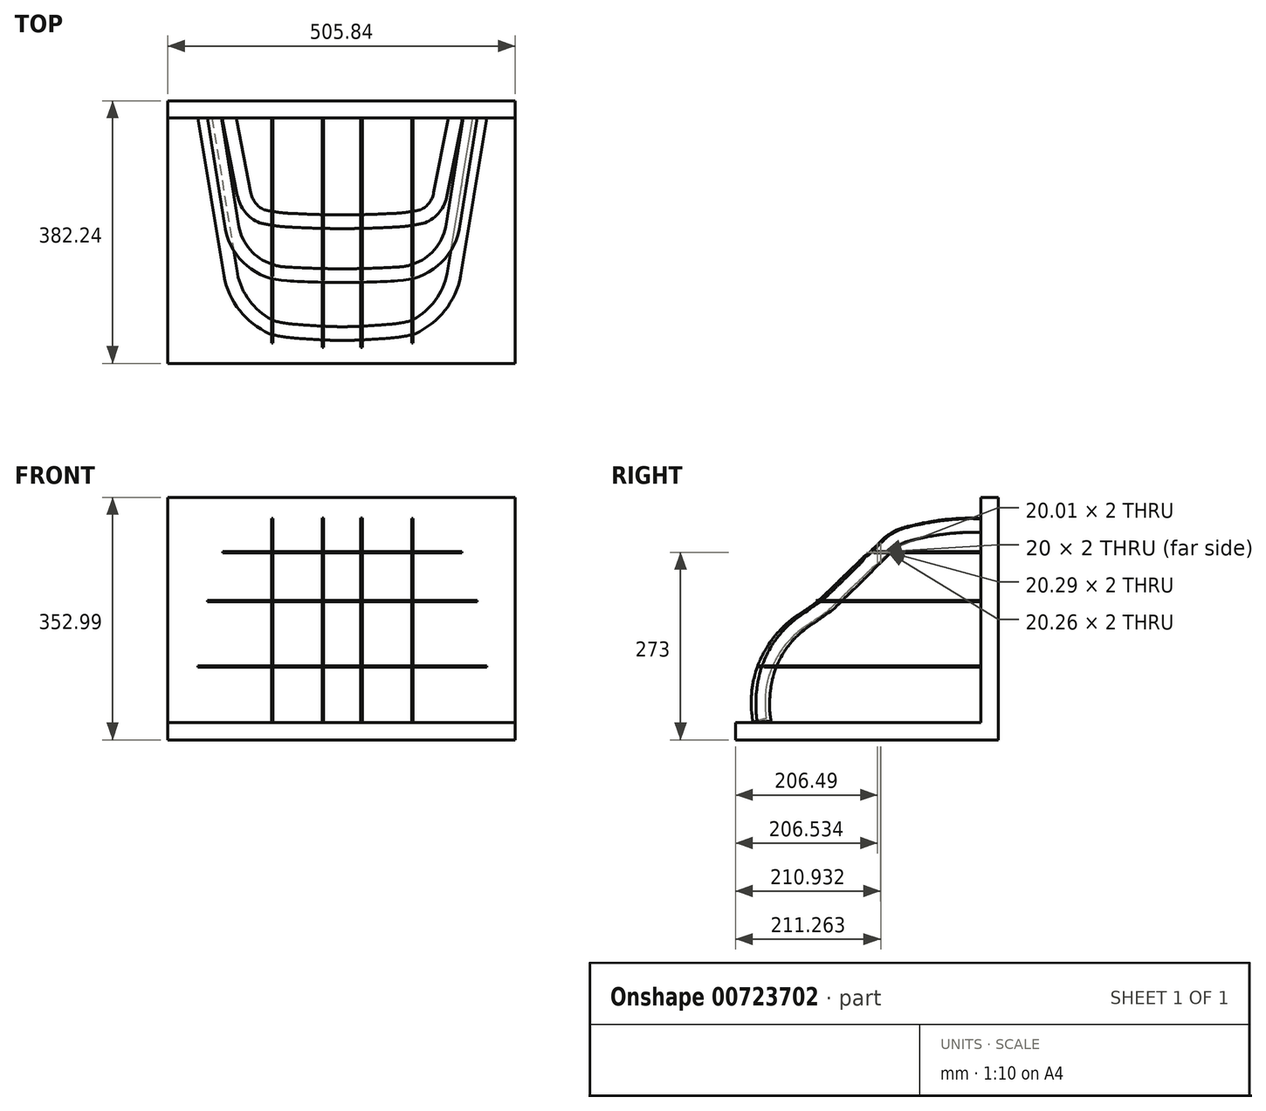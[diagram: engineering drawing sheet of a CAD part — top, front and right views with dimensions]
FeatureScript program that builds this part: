
annotation { "Feature Type Name" : "Feature", "Feature Type Description" : "" }
export const myFeature = defineFeature(function(context is Context, id is Id, definition is map)
    precondition{}
    {
        {
            var Q0;
            Q0=qCreatedBy(makeId("Right.planeOp"),FACE);
            cPlane(context, id + "F0", {"entities" : qUnion([Q0]), "cplaneType" : CPlaneType.OFFSET, "offset" : 28 * mm, "width" : 150 * mm, "height" : 150 * mm});
        }
        {
            var Q0;
            Q0=qCreatedBy(id+"F0.planeOp",FACE);
            var sketch = newSketch(context, id + "F1", { "sketchPlane" : qUnion([Q0])});
            skPoint(sketch, "E0", {"position": v(0, 0) * mm});
            skLineSegment(sketch, "E1", {"start": v(0, 0) * mm, "end": v(-336.64, 0) * mm});
            skLineSegment(sketch, "E2", {"start": v(0, 302.93) * mm, "end": v(-1.33, 302.66) * mm});
            skLineSegment(sketch, "E3", {"start": v(-1.33, 302.66) * mm, "end": v(-1.75, 302.63) * mm});
            skLineSegment(sketch, "E4", {"start": v(-1.75, 302.63) * mm, "end": v(-3.18, 302.69) * mm});
            skLineSegment(sketch, "E5", {"start": v(-3.18, 302.69) * mm, "end": v(-4.19, 302.72) * mm});
            skLineSegment(sketch, "E6", {"start": v(-4.19, 302.72) * mm, "end": v(-4.73, 302.74) * mm});
            skLineSegment(sketch, "E7", {"start": v(-4.73, 302.74) * mm, "end": v(-7.22, 302.8) * mm});
            skLineSegment(sketch, "E8", {"start": v(-7.22, 302.8) * mm, "end": v(-9.08, 302.77) * mm});
            skLineSegment(sketch, "E9", {"start": v(-9.08, 302.77) * mm, "end": v(-11.39, 302.77) * mm});
            skLineSegment(sketch, "E10", {"start": v(-11.39, 302.77) * mm, "end": v(-14.62, 302.87) * mm});
            skLineSegment(sketch, "E11", {"start": v(-14.62, 302.87) * mm, "end": v(-15.84, 302.9) * mm});
            skLineSegment(sketch, "E12", {"start": v(-15.84, 302.9) * mm, "end": v(-16.17, 302.91) * mm});
            skLineSegment(sketch, "E13", {"start": v(-16.17, 302.91) * mm, "end": v(-16.53, 302.91) * mm});
            skLineSegment(sketch, "E14", {"start": v(-16.53, 302.91) * mm, "end": v(-19.91, 302.89) * mm});
            skLineSegment(sketch, "E15", {"start": v(-19.91, 302.89) * mm, "end": v(-22.68, 302.78) * mm});
            skLineSegment(sketch, "E16", {"start": v(-22.68, 302.78) * mm, "end": v(-26.11, 302.63) * mm});
            skLineSegment(sketch, "E17", {"start": v(-26.11, 302.63) * mm, "end": v(-31.16, 302.43) * mm});
            skLineSegment(sketch, "E18", {"start": v(-31.16, 302.43) * mm, "end": v(-32.29, 302.39) * mm});
            skLineSegment(sketch, "E19", {"start": v(-32.29, 302.39) * mm, "end": v(-33.37, 302.32) * mm});
            skLineSegment(sketch, "E20", {"start": v(-33.37, 302.32) * mm, "end": v(-36.32, 302.12) * mm});
            skLineSegment(sketch, "E21", {"start": v(-36.32, 302.12) * mm, "end": v(-38.52, 301.96) * mm});
            skLineSegment(sketch, "E22", {"start": v(-38.52, 301.96) * mm, "end": v(-40.75, 301.8) * mm});
            skLineSegment(sketch, "E23", {"start": v(-40.75, 301.8) * mm, "end": v(-42.89, 301.62) * mm});
            skLineSegment(sketch, "E24", {"start": v(-42.89, 301.62) * mm, "end": v(-43.02, 301.61) * mm});
            skLineSegment(sketch, "E25", {"start": v(-43.02, 301.61) * mm, "end": v(-47.21, 301.28) * mm});
            skLineSegment(sketch, "E26", {"start": v(-47.21, 301.28) * mm, "end": v(-48.36, 301.18) * mm});
            skLineSegment(sketch, "E27", {"start": v(-48.36, 301.18) * mm, "end": v(-51.91, 300.85) * mm});
            skLineSegment(sketch, "E28", {"start": v(-51.91, 300.85) * mm, "end": v(-52.52, 300.78) * mm});
            skLineSegment(sketch, "E29", {"start": v(-52.52, 300.78) * mm, "end": v(-54.54, 300.56) * mm});
            skLineSegment(sketch, "E30", {"start": v(-54.54, 300.56) * mm, "end": v(-57.85, 300.12) * mm});
            skLineSegment(sketch, "E31", {"start": v(-57.85, 300.12) * mm, "end": v(-58.76, 300) * mm});
            skLineSegment(sketch, "E32", {"start": v(-58.76, 300) * mm, "end": v(-62.24, 299.52) * mm});
            skLineSegment(sketch, "E33", {"start": v(-62.24, 299.52) * mm, "end": v(-65.37, 299.1) * mm});
            skLineSegment(sketch, "E34", {"start": v(-65.37, 299.1) * mm, "end": v(-69.73, 298.47) * mm});
            skLineSegment(sketch, "E35", {"start": v(-69.73, 298.47) * mm, "end": v(-71.93, 298.15) * mm});
            skLineSegment(sketch, "E36", {"start": v(-71.93, 298.15) * mm, "end": v(-73.76, 297.84) * mm});
            skLineSegment(sketch, "E37", {"start": v(-73.76, 297.84) * mm, "end": v(-76.97, 297.28) * mm});
            skLineSegment(sketch, "E38", {"start": v(-76.97, 297.28) * mm, "end": v(-79.2, 296.9) * mm});
            skLineSegment(sketch, "E39", {"start": v(-79.2, 296.9) * mm, "end": v(-83.2, 296.17) * mm});
            skLineSegment(sketch, "E40", {"start": v(-83.2, 296.17) * mm, "end": v(-85.92, 295.66) * mm});
            skLineSegment(sketch, "E41", {"start": v(-85.92, 295.66) * mm, "end": v(-87.06, 295.42) * mm});
            skLineSegment(sketch, "E42", {"start": v(-87.06, 295.42) * mm, "end": v(-90.16, 294.74) * mm});
            skLineSegment(sketch, "E43", {"start": v(-90.16, 294.74) * mm, "end": v(-92.74, 294.23) * mm});
            skLineSegment(sketch, "E44", {"start": v(-92.74, 294.23) * mm, "end": v(-96.17, 293.46) * mm});
            skLineSegment(sketch, "E45", {"start": v(-96.17, 293.46) * mm, "end": v(-97.36, 293.2) * mm});
            skLineSegment(sketch, "E46", {"start": v(-97.36, 293.2) * mm, "end": v(-98.2, 293) * mm});
            skLineSegment(sketch, "E47", {"start": v(-98.2, 293) * mm, "end": v(-103.97, 291.56) * mm});
            skLineSegment(sketch, "E48", {"start": v(-103.97, 291.56) * mm, "end": v(-104.02, 291.55) * mm});
            skLineSegment(sketch, "E49", {"start": v(-104.02, 291.55) * mm, "end": v(-104.07, 291.54) * mm});
            skLineSegment(sketch, "E50", {"start": v(-104.07, 291.54) * mm, "end": v(-107.9, 290.6) * mm});
            skLineSegment(sketch, "E51", {"start": v(-107.9, 290.6) * mm, "end": v(-109.48, 290.16) * mm});
            skLineSegment(sketch, "E52", {"start": v(-109.48, 290.16) * mm, "end": v(-112.69, 289.3) * mm});
            skLineSegment(sketch, "E53", {"start": v(-112.69, 289.3) * mm, "end": v(-113, 289.22) * mm});
            skLineSegment(sketch, "E54", {"start": v(-113, 289.22) * mm, "end": v(-113.13, 289.18) * mm});
            skLineSegment(sketch, "E55", {"start": v(-113.13, 289.18) * mm, "end": v(-113.84, 288.97) * mm});
            skLineSegment(sketch, "E56", {"start": v(-113.84, 288.97) * mm, "end": v(-116.81, 288.1) * mm});
            skLineSegment(sketch, "E57", {"start": v(-116.81, 288.1) * mm, "end": v(-118.25, 287.64) * mm});
            skLineSegment(sketch, "E58", {"start": v(-118.25, 287.64) * mm, "end": v(-120.24, 286.96) * mm});
            skLineSegment(sketch, "E59", {"start": v(-120.24, 286.96) * mm, "end": v(-122.17, 286.17) * mm});
            skLineSegment(sketch, "E60", {"start": v(-122.17, 286.17) * mm, "end": v(-123.8, 285.5) * mm});
            skLineSegment(sketch, "E61", {"start": v(-123.8, 285.5) * mm, "end": v(-126.08, 284.5) * mm});
            skLineSegment(sketch, "E62", {"start": v(-126.08, 284.5) * mm, "end": v(-127.05, 283.99) * mm});
            skLineSegment(sketch, "E63", {"start": v(-127.05, 283.99) * mm, "end": v(-129.84, 282.57) * mm});
            skLineSegment(sketch, "E64", {"start": v(-129.84, 282.57) * mm, "end": v(-131.55, 281.62) * mm});
            skLineSegment(sketch, "E65", {"start": v(-131.55, 281.62) * mm, "end": v(-132.06, 281.35) * mm});
            skLineSegment(sketch, "E66", {"start": v(-132.06, 281.35) * mm, "end": v(-132.92, 280.81) * mm});
            skLineSegment(sketch, "E67", {"start": v(-132.92, 280.81) * mm, "end": v(-135.31, 279.39) * mm});
            skLineSegment(sketch, "E68", {"start": v(-135.31, 279.39) * mm, "end": v(-137.16, 278.12) * mm});
            skLineSegment(sketch, "E69", {"start": v(-137.16, 278.12) * mm, "end": v(-138.07, 277.49) * mm});
            skLineSegment(sketch, "E70", {"start": v(-138.07, 277.49) * mm, "end": v(-139.84, 276.19) * mm});
            skLineSegment(sketch, "E71", {"start": v(-139.84, 276.19) * mm, "end": v(-140.9, 275.41) * mm});
            skLineSegment(sketch, "E72", {"start": v(-140.9, 275.41) * mm, "end": v(-141.31, 275.08) * mm});
            skLineSegment(sketch, "E73", {"start": v(-141.31, 275.08) * mm, "end": v(-142.88, 273.8) * mm});
            skLineSegment(sketch, "E74", {"start": v(-142.88, 273.8) * mm, "end": v(-144.14, 272.67) * mm});
            skLineSegment(sketch, "E75", {"start": v(-144.14, 272.67) * mm, "end": v(-145.09, 271.82) * mm});
            skLineSegment(sketch, "E76", {"start": v(-145.09, 271.82) * mm, "end": v(-145.86, 271.04) * mm});
            skLineSegment(sketch, "E77", {"start": v(-145.86, 271.04) * mm, "end": v(-148.57, 268.42) * mm});
            skLineSegment(sketch, "E78", {"start": v(-148.57, 268.42) * mm, "end": v(-148.88, 268.1) * mm});
            skLineSegment(sketch, "E79", {"start": v(-148.88, 268.1) * mm, "end": v(-151.46, 265.56) * mm});
            skLineSegment(sketch, "E80", {"start": v(-151.46, 265.56) * mm, "end": v(-152.25, 264.79) * mm});
            skLineSegment(sketch, "E81", {"start": v(-152.25, 264.79) * mm, "end": v(-153.7, 263.33) * mm});
            skLineSegment(sketch, "E82", {"start": v(-153.7, 263.33) * mm, "end": v(-154.53, 262.44) * mm});
            skLineSegment(sketch, "E83", {"start": v(-154.53, 262.44) * mm, "end": v(-155.9, 261.16) * mm});
            skLineSegment(sketch, "E84", {"start": v(-155.9, 261.16) * mm, "end": v(-156.74, 260.4) * mm});
            skLineSegment(sketch, "E85", {"start": v(-156.74, 260.4) * mm, "end": v(-158.23, 258.88) * mm});
            skLineSegment(sketch, "E86", {"start": v(-158.23, 258.88) * mm, "end": v(-158.94, 258.15) * mm});
            skLineSegment(sketch, "E87", {"start": v(-158.94, 258.15) * mm, "end": v(-160, 257.23) * mm});
            skLineSegment(sketch, "E88", {"start": v(-160, 257.23) * mm, "end": v(-160.75, 256.56) * mm});
            skLineSegment(sketch, "E89", {"start": v(-160.75, 256.56) * mm, "end": v(-161.54, 255.85) * mm});
            skLineSegment(sketch, "E90", {"start": v(-161.54, 255.85) * mm, "end": v(-162.05, 255.37) * mm});
            skLineSegment(sketch, "E91", {"start": v(-162.05, 255.37) * mm, "end": v(-162.8, 254.67) * mm});
            skLineSegment(sketch, "E92", {"start": v(-162.8, 254.67) * mm, "end": v(-164, 253.4) * mm});
            skLineSegment(sketch, "E93", {"start": v(-164, 253.4) * mm, "end": v(-165.4, 251.9) * mm});
            skLineSegment(sketch, "E94", {"start": v(-165.4, 251.9) * mm, "end": v(-165.92, 251.36) * mm});
            skLineSegment(sketch, "E95", {"start": v(-165.92, 251.36) * mm, "end": v(-167.8, 249.6) * mm});
            skLineSegment(sketch, "E96", {"start": v(-167.8, 249.6) * mm, "end": v(-167.93, 249.47) * mm});
            skLineSegment(sketch, "E97", {"start": v(-167.93, 249.47) * mm, "end": v(-167.99, 249.42) * mm});
            skLineSegment(sketch, "E98", {"start": v(-167.99, 249.42) * mm, "end": v(-169.9, 248.03) * mm});
            skLineSegment(sketch, "E99", {"start": v(-169.9, 248.03) * mm, "end": v(-170.93, 247.48) * mm});
            skLineSegment(sketch, "E100", {"start": v(-170.93, 247.48) * mm, "end": v(-172.86, 246.29) * mm});
            skLineSegment(sketch, "E101", {"start": v(-172.86, 246.29) * mm, "end": v(-173.5, 245.9) * mm});
            skLineSegment(sketch, "E102", {"start": v(-173.5, 245.9) * mm, "end": v(-174.08, 245.4) * mm});
            skLineSegment(sketch, "E103", {"start": v(-174.08, 245.4) * mm, "end": v(-175.59, 243.84) * mm});
            skLineSegment(sketch, "E104", {"start": v(-175.59, 243.84) * mm, "end": v(-177.02, 242.22) * mm});
            skLineSegment(sketch, "E105", {"start": v(-177.02, 242.22) * mm, "end": v(-177.21, 242.02) * mm});
            skLineSegment(sketch, "E106", {"start": v(-177.21, 242.02) * mm, "end": v(-177.34, 241.86) * mm});
            skLineSegment(sketch, "E107", {"start": v(-177.34, 241.86) * mm, "end": v(-179.3, 239.74) * mm});
            skLineSegment(sketch, "E108", {"start": v(-179.3, 239.74) * mm, "end": v(-179.45, 239.59) * mm});
            skLineSegment(sketch, "E109", {"start": v(-179.45, 239.59) * mm, "end": v(-180.97, 238.05) * mm});
            skLineSegment(sketch, "E110", {"start": v(-180.97, 238.05) * mm, "end": v(-182.31, 236.77) * mm});
            skLineSegment(sketch, "E111", {"start": v(-182.31, 236.77) * mm, "end": v(-182.86, 236.26) * mm});
            skLineSegment(sketch, "E112", {"start": v(-182.86, 236.26) * mm, "end": v(-182.94, 236.17) * mm});
            skLineSegment(sketch, "E113", {"start": v(-182.94, 236.17) * mm, "end": v(-183.1, 236.01) * mm});
            skLineSegment(sketch, "E114", {"start": v(-183.1, 236.01) * mm, "end": v(-185.59, 233.52) * mm});
            skLineSegment(sketch, "E115", {"start": v(-185.59, 233.52) * mm, "end": v(-187.96, 231.4) * mm});
            skLineSegment(sketch, "E116", {"start": v(-187.96, 231.4) * mm, "end": v(-188.49, 230.9) * mm});
            skLineSegment(sketch, "E117", {"start": v(-188.49, 230.9) * mm, "end": v(-188.86, 230.57) * mm});
            skLineSegment(sketch, "E118", {"start": v(-188.86, 230.57) * mm, "end": v(-189.59, 229.85) * mm});
            skLineSegment(sketch, "E119", {"start": v(-189.59, 229.85) * mm, "end": v(-190.57, 228.87) * mm});
            skLineSegment(sketch, "E120", {"start": v(-190.57, 228.87) * mm, "end": v(-191.42, 228.01) * mm});
            skLineSegment(sketch, "E121", {"start": v(-191.42, 228.01) * mm, "end": v(-192.44, 226.97) * mm});
            skLineSegment(sketch, "E122", {"start": v(-192.44, 226.97) * mm, "end": v(-193, 226.42) * mm});
            skLineSegment(sketch, "E123", {"start": v(-193, 226.42) * mm, "end": v(-194.05, 225.39) * mm});
            skLineSegment(sketch, "E124", {"start": v(-194.05, 225.39) * mm, "end": v(-195.33, 224.13) * mm});
            skLineSegment(sketch, "E125", {"start": v(-195.33, 224.13) * mm, "end": v(-195.92, 223.58) * mm});
            skLineSegment(sketch, "E126", {"start": v(-195.92, 223.58) * mm, "end": v(-197.38, 222.22) * mm});
            skLineSegment(sketch, "E127", {"start": v(-197.38, 222.22) * mm, "end": v(-198.82, 220.76) * mm});
            skLineSegment(sketch, "E128", {"start": v(-198.82, 220.76) * mm, "end": v(-199.99, 219.64) * mm});
            skLineSegment(sketch, "E129", {"start": v(-199.99, 219.64) * mm, "end": v(-201.56, 218.25) * mm});
            skLineSegment(sketch, "E130", {"start": v(-201.56, 218.25) * mm, "end": v(-202.86, 217.04) * mm});
            skLineSegment(sketch, "E131", {"start": v(-202.86, 217.04) * mm, "end": v(-203.74, 216.2) * mm});
            skLineSegment(sketch, "E132", {"start": v(-203.74, 216.2) * mm, "end": v(-205.3, 214.66) * mm});
            skLineSegment(sketch, "E133", {"start": v(-205.3, 214.66) * mm, "end": v(-205.58, 214.38) * mm});
            skLineSegment(sketch, "E134", {"start": v(-205.58, 214.38) * mm, "end": v(-205.87, 214.1) * mm});
            skLineSegment(sketch, "E135", {"start": v(-205.87, 214.1) * mm, "end": v(-206.83, 213.19) * mm});
            skLineSegment(sketch, "E136", {"start": v(-206.83, 213.19) * mm, "end": v(-207.48, 212.61) * mm});
            skLineSegment(sketch, "E137", {"start": v(-207.48, 212.61) * mm, "end": v(-209.68, 210.47) * mm});
            skLineSegment(sketch, "E138", {"start": v(-209.68, 210.47) * mm, "end": v(-209.85, 210.3) * mm});
            skLineSegment(sketch, "E139", {"start": v(-209.85, 210.3) * mm, "end": v(-210.41, 209.77) * mm});
            skLineSegment(sketch, "E140", {"start": v(-210.41, 209.77) * mm, "end": v(-211.57, 208.68) * mm});
            skLineSegment(sketch, "E141", {"start": v(-211.57, 208.68) * mm, "end": v(-211.66, 208.6) * mm});
            skLineSegment(sketch, "E142", {"start": v(-211.66, 208.6) * mm, "end": v(-211.92, 208.3) * mm});
            skLineSegment(sketch, "E143", {"start": v(-211.92, 208.3) * mm, "end": v(-213.3, 206.78) * mm});
            skLineSegment(sketch, "E144", {"start": v(-213.3, 206.78) * mm, "end": v(-213.97, 206.14) * mm});
            skLineSegment(sketch, "E145", {"start": v(-213.97, 206.14) * mm, "end": v(-215.47, 204.64) * mm});
            skLineSegment(sketch, "E146", {"start": v(-215.47, 204.64) * mm, "end": v(-215.51, 204.6) * mm});
            skLineSegment(sketch, "E147", {"start": v(-215.51, 204.6) * mm, "end": v(-217.9, 202.46) * mm});
            skLineSegment(sketch, "E148", {"start": v(-217.9, 202.46) * mm, "end": v(-218.65, 201.68) * mm});
            skLineSegment(sketch, "E149", {"start": v(-218.65, 201.68) * mm, "end": v(-220.09, 200.3) * mm});
            skLineSegment(sketch, "E150", {"start": v(-220.09, 200.3) * mm, "end": v(-221.2, 199.2) * mm});
            skLineSegment(sketch, "E151", {"start": v(-221.2, 199.2) * mm, "end": v(-222.08, 198.31) * mm});
            skLineSegment(sketch, "E152", {"start": v(-222.08, 198.31) * mm, "end": v(-224.26, 196.17) * mm});
            skLineSegment(sketch, "E153", {"start": v(-224.26, 196.17) * mm, "end": v(-224.63, 195.81) * mm});
            skLineSegment(sketch, "E154", {"start": v(-224.63, 195.81) * mm, "end": v(-226.97, 193.6) * mm});
            skLineSegment(sketch, "E155", {"start": v(-226.97, 193.6) * mm, "end": v(-227.75, 192.8) * mm});
            skLineSegment(sketch, "E156", {"start": v(-227.75, 192.8) * mm, "end": v(-228.92, 191.65) * mm});
            skLineSegment(sketch, "E157", {"start": v(-228.92, 191.65) * mm, "end": v(-229.52, 191.09) * mm});
            skLineSegment(sketch, "E158", {"start": v(-229.52, 191.09) * mm, "end": v(-231.22, 189.58) * mm});
            skLineSegment(sketch, "E159", {"start": v(-231.22, 189.58) * mm, "end": v(-231.9, 188.94) * mm});
            skLineSegment(sketch, "E160", {"start": v(-231.9, 188.94) * mm, "end": v(-233.03, 187.87) * mm});
            skLineSegment(sketch, "E161", {"start": v(-233.03, 187.87) * mm, "end": v(-234.44, 186.51) * mm});
            skLineSegment(sketch, "E162", {"start": v(-234.44, 186.51) * mm, "end": v(-234.92, 186.02) * mm});
            skLineSegment(sketch, "E163", {"start": v(-234.92, 186.02) * mm, "end": v(-236.27, 184.62) * mm});
            skLineSegment(sketch, "E164", {"start": v(-236.27, 184.62) * mm, "end": v(-237.66, 183.36) * mm});
            skLineSegment(sketch, "E165", {"start": v(-237.66, 183.36) * mm, "end": v(-238.98, 182.21) * mm});
            skLineSegment(sketch, "E166", {"start": v(-238.98, 182.21) * mm, "end": v(-239.39, 181.85) * mm});
            skLineSegment(sketch, "E167", {"start": v(-239.39, 181.85) * mm, "end": v(-240.67, 180.81) * mm});
            skLineSegment(sketch, "E168", {"start": v(-240.67, 180.81) * mm, "end": v(-242.01, 179.8) * mm});
            skLineSegment(sketch, "E169", {"start": v(-242.01, 179.8) * mm, "end": v(-244.77, 177.54) * mm});
            skLineSegment(sketch, "E170", {"start": v(-244.77, 177.54) * mm, "end": v(-245.52, 176.99) * mm});
            skLineSegment(sketch, "E171", {"start": v(-245.52, 176.99) * mm, "end": v(-248.8, 174.71) * mm});
            skLineSegment(sketch, "E172", {"start": v(-248.8, 174.71) * mm, "end": v(-250.8, 173.34) * mm});
            skLineSegment(sketch, "E173", {"start": v(-250.8, 173.34) * mm, "end": v(-252.2, 172.38) * mm});
            skLineSegment(sketch, "E174", {"start": v(-252.2, 172.38) * mm, "end": v(-252.45, 172.2) * mm});
            skLineSegment(sketch, "E175", {"start": v(-252.45, 172.2) * mm, "end": v(-255.33, 170.33) * mm});
            skLineSegment(sketch, "E176", {"start": v(-255.33, 170.33) * mm, "end": v(-256.3, 169.66) * mm});
            skLineSegment(sketch, "E177", {"start": v(-256.3, 169.66) * mm, "end": v(-258.98, 167.8) * mm});
            skLineSegment(sketch, "E178", {"start": v(-258.98, 167.8) * mm, "end": v(-260.16, 167.01) * mm});
            skLineSegment(sketch, "E179", {"start": v(-260.16, 167.01) * mm, "end": v(-263.77, 164.64) * mm});
            skLineSegment(sketch, "E180", {"start": v(-263.77, 164.64) * mm, "end": v(-265.93, 163.2) * mm});
            skLineSegment(sketch, "E181", {"start": v(-265.93, 163.2) * mm, "end": v(-268.76, 161.26) * mm});
            skLineSegment(sketch, "E182", {"start": v(-268.76, 161.26) * mm, "end": v(-270.69, 160) * mm});
            skLineSegment(sketch, "E183", {"start": v(-270.69, 160) * mm, "end": v(-272.92, 158.48) * mm});
            skLineSegment(sketch, "E184", {"start": v(-272.92, 158.48) * mm, "end": v(-273.06, 158.38) * mm});
            skLineSegment(sketch, "E185", {"start": v(-273.06, 158.38) * mm, "end": v(-278.26, 154.45) * mm});
            skLineSegment(sketch, "E186", {"start": v(-278.26, 154.45) * mm, "end": v(-278.78, 154.07) * mm});
            skLineSegment(sketch, "E187", {"start": v(-278.78, 154.07) * mm, "end": v(-279.79, 153.26) * mm});
            skLineSegment(sketch, "E188", {"start": v(-279.79, 153.26) * mm, "end": v(-282.35, 151.15) * mm});
            skLineSegment(sketch, "E189", {"start": v(-282.35, 151.15) * mm, "end": v(-284.38, 149.41) * mm});
            skLineSegment(sketch, "E190", {"start": v(-284.38, 149.41) * mm, "end": v(-285, 148.87) * mm});
            skLineSegment(sketch, "E191", {"start": v(-285, 148.87) * mm, "end": v(-285.22, 148.68) * mm});
            skLineSegment(sketch, "E192", {"start": v(-285.22, 148.68) * mm, "end": v(-285.57, 148.34) * mm});
            skLineSegment(sketch, "E193", {"start": v(-285.57, 148.34) * mm, "end": v(-288.77, 145.41) * mm});
            skLineSegment(sketch, "E194", {"start": v(-288.77, 145.41) * mm, "end": v(-290.44, 144.04) * mm});
            skLineSegment(sketch, "E195", {"start": v(-290.44, 144.04) * mm, "end": v(-290.8, 143.72) * mm});
            skLineSegment(sketch, "E196", {"start": v(-290.8, 143.72) * mm, "end": v(-292.79, 141.76) * mm});
            skLineSegment(sketch, "E197", {"start": v(-292.79, 141.76) * mm, "end": v(-292.98, 141.56) * mm});
            skLineSegment(sketch, "E198", {"start": v(-292.98, 141.56) * mm, "end": v(-294.2, 140.16) * mm});
            skLineSegment(sketch, "E199", {"start": v(-294.2, 140.16) * mm, "end": v(-296.16, 138.08) * mm});
            skLineSegment(sketch, "E200", {"start": v(-296.16, 138.08) * mm, "end": v(-296.9, 137.28) * mm});
            skLineSegment(sketch, "E201", {"start": v(-296.9, 137.28) * mm, "end": v(-296.96, 137.23) * mm});
            skLineSegment(sketch, "E202", {"start": v(-296.96, 137.23) * mm, "end": v(-297.05, 137.12) * mm});
            skLineSegment(sketch, "E203", {"start": v(-297.05, 137.12) * mm, "end": v(-299.8, 134) * mm});
            skLineSegment(sketch, "E204", {"start": v(-299.8, 134) * mm, "end": v(-302.82, 130.57) * mm});
            skLineSegment(sketch, "E205", {"start": v(-302.82, 130.57) * mm, "end": v(-303.24, 130.12) * mm});
            skLineSegment(sketch, "E206", {"start": v(-303.24, 130.12) * mm, "end": v(-303.57, 129.73) * mm});
            skLineSegment(sketch, "E207", {"start": v(-303.57, 129.73) * mm, "end": v(-303.8, 129.44) * mm});
            skLineSegment(sketch, "E208", {"start": v(-303.8, 129.44) * mm, "end": v(-305.28, 127.58) * mm});
            skLineSegment(sketch, "E209", {"start": v(-305.28, 127.58) * mm, "end": v(-306.17, 126.46) * mm});
            skLineSegment(sketch, "E210", {"start": v(-306.17, 126.46) * mm, "end": v(-307.05, 125.26) * mm});
            skLineSegment(sketch, "E211", {"start": v(-307.05, 125.26) * mm, "end": v(-308.44, 123.37) * mm});
            skLineSegment(sketch, "E212", {"start": v(-308.44, 123.37) * mm, "end": v(-309.47, 121.95) * mm});
            skLineSegment(sketch, "E213", {"start": v(-309.47, 121.95) * mm, "end": v(-310.93, 119.94) * mm});
            skLineSegment(sketch, "E214", {"start": v(-310.93, 119.94) * mm, "end": v(-313.12, 116.8) * mm});
            skLineSegment(sketch, "E215", {"start": v(-313.12, 116.8) * mm, "end": v(-313.66, 116.02) * mm});
            skLineSegment(sketch, "E216", {"start": v(-313.66, 116.02) * mm, "end": v(-313.96, 115.53) * mm});
            skLineSegment(sketch, "E217", {"start": v(-313.96, 115.53) * mm, "end": v(-315.95, 112.29) * mm});
            skLineSegment(sketch, "E218", {"start": v(-315.95, 112.29) * mm, "end": v(-317.6, 109.48) * mm});
            skLineSegment(sketch, "E219", {"start": v(-317.6, 109.48) * mm, "end": v(-317.87, 109.03) * mm});
            skLineSegment(sketch, "E220", {"start": v(-317.87, 109.03) * mm, "end": v(-318.02, 108.73) * mm});
            skLineSegment(sketch, "E221", {"start": v(-318.02, 108.73) * mm, "end": v(-319.3, 106.4) * mm});
            skLineSegment(sketch, "E222", {"start": v(-319.3, 106.4) * mm, "end": v(-320.24, 104.75) * mm});
            skLineSegment(sketch, "E223", {"start": v(-320.24, 104.75) * mm, "end": v(-320.63, 104.06) * mm});
            skLineSegment(sketch, "E224", {"start": v(-320.63, 104.06) * mm, "end": v(-321.62, 102.24) * mm});
            skLineSegment(sketch, "E225", {"start": v(-321.62, 102.24) * mm, "end": v(-323.03, 99.6) * mm});
            skLineSegment(sketch, "E226", {"start": v(-323.03, 99.6) * mm, "end": v(-323.47, 98.71) * mm});
            skLineSegment(sketch, "E227", {"start": v(-323.47, 98.71) * mm, "end": v(-323.78, 98.1) * mm});
            skLineSegment(sketch, "E228", {"start": v(-323.78, 98.1) * mm, "end": v(-323.98, 97.7) * mm});
            skLineSegment(sketch, "E229", {"start": v(-323.98, 97.7) * mm, "end": v(-325.52, 94.3) * mm});
            skLineSegment(sketch, "E230", {"start": v(-325.52, 94.3) * mm, "end": v(-325.87, 93.48) * mm});
            skLineSegment(sketch, "E231", {"start": v(-325.87, 93.48) * mm, "end": v(-326.33, 92.45) * mm});
            skLineSegment(sketch, "E232", {"start": v(-326.33, 92.45) * mm, "end": v(-327.26, 90.3) * mm});
            skLineSegment(sketch, "E233", {"start": v(-327.26, 90.3) * mm, "end": v(-327.7, 89.25) * mm});
            skLineSegment(sketch, "E234", {"start": v(-327.7, 89.25) * mm, "end": v(-328.15, 88.13) * mm});
            skLineSegment(sketch, "E235", {"start": v(-328.15, 88.13) * mm, "end": v(-329.16, 85.49) * mm});
            skLineSegment(sketch, "E236", {"start": v(-329.16, 85.49) * mm, "end": v(-329.47, 84.67) * mm});
            skLineSegment(sketch, "E237", {"start": v(-329.47, 84.67) * mm, "end": v(-331.44, 79.2) * mm});
            skLineSegment(sketch, "E238", {"start": v(-331.44, 79.2) * mm, "end": v(-331.45, 79.17) * mm});
            skLineSegment(sketch, "E239", {"start": v(-331.45, 79.17) * mm, "end": v(-331.46, 79.16) * mm});
            skLineSegment(sketch, "E240", {"start": v(-331.46, 79.16) * mm, "end": v(-331.48, 79.1) * mm});
            skLineSegment(sketch, "E241", {"start": v(-331.48, 79.1) * mm, "end": v(-332.52, 75.95) * mm});
            skLineSegment(sketch, "E242", {"start": v(-332.52, 75.95) * mm, "end": v(-333.6, 72.07) * mm});
            skLineSegment(sketch, "E243", {"start": v(-333.6, 72.07) * mm, "end": v(-333.86, 71.11) * mm});
            skLineSegment(sketch, "E244", {"start": v(-333.86, 71.11) * mm, "end": v(-334.1, 70.22) * mm});
            skLineSegment(sketch, "E245", {"start": v(-334.1, 70.22) * mm, "end": v(-334.92, 67.13) * mm});
            skLineSegment(sketch, "E246", {"start": v(-334.92, 67.13) * mm, "end": v(-335.44, 64.95) * mm});
            skLineSegment(sketch, "E247", {"start": v(-335.44, 64.95) * mm, "end": v(-335.62, 64.11) * mm});
            skLineSegment(sketch, "E248", {"start": v(-335.62, 64.11) * mm, "end": v(-335.76, 63.51) * mm});
            skLineSegment(sketch, "E249", {"start": v(-335.76, 63.51) * mm, "end": v(-336.5, 59.88) * mm});
            skLineSegment(sketch, "E250", {"start": v(-336.5, 59.88) * mm, "end": v(-336.71, 58.45) * mm});
            skLineSegment(sketch, "E251", {"start": v(-336.71, 58.45) * mm, "end": v(-337.06, 56.22) * mm});
            skLineSegment(sketch, "E252", {"start": v(-337.06, 56.22) * mm, "end": v(-337.22, 55.2) * mm});
            skLineSegment(sketch, "E253", {"start": v(-337.22, 55.2) * mm, "end": v(-337.28, 54.78) * mm});
            skLineSegment(sketch, "E254", {"start": v(-337.28, 54.78) * mm, "end": v(-337.72, 52.05) * mm});
            skLineSegment(sketch, "E255", {"start": v(-337.72, 52.05) * mm, "end": v(-337.77, 51.76) * mm});
            skLineSegment(sketch, "E256", {"start": v(-337.77, 51.76) * mm, "end": v(-337.78, 51.72) * mm});
            skLineSegment(sketch, "E257", {"start": v(-337.78, 51.72) * mm, "end": v(-337.84, 51.19) * mm});
            skLineSegment(sketch, "E258", {"start": v(-337.84, 51.19) * mm, "end": v(-338.28, 47.58) * mm});
            skLineSegment(sketch, "E259", {"start": v(-338.28, 47.58) * mm, "end": v(-338.3, 47.38) * mm});
            skLineSegment(sketch, "E260", {"start": v(-338.3, 47.38) * mm, "end": v(-338.32, 47.23) * mm});
            skLineSegment(sketch, "E261", {"start": v(-338.32, 47.23) * mm, "end": v(-338.38, 46.46) * mm});
            skLineSegment(sketch, "E262", {"start": v(-338.38, 46.46) * mm, "end": v(-338.65, 42.8) * mm});
            skLineSegment(sketch, "E263", {"start": v(-338.65, 42.8) * mm, "end": v(-338.73, 41.68) * mm});
            skLineSegment(sketch, "E264", {"start": v(-338.73, 41.68) * mm, "end": v(-338.94, 38.25) * mm});
            skLineSegment(sketch, "E265", {"start": v(-338.94, 38.25) * mm, "end": v(-339.02, 36.07) * mm});
            skLineSegment(sketch, "E266", {"start": v(-339.02, 36.07) * mm, "end": v(-339.05, 34.23) * mm});
            skLineSegment(sketch, "E267", {"start": v(-339.05, 34.23) * mm, "end": v(-339.13, 31.14) * mm});
            skLineSegment(sketch, "E268", {"start": v(-339.13, 31.14) * mm, "end": v(-339.17, 29) * mm});
            skLineSegment(sketch, "E269", {"start": v(-339.17, 29) * mm, "end": v(-339.16, 26.99) * mm});
            skLineSegment(sketch, "E270", {"start": v(-339.16, 26.99) * mm, "end": v(-339.06, 22.17) * mm});
            skLineSegment(sketch, "E271", {"start": v(-339.06, 22.17) * mm, "end": v(-339.05, 21.97) * mm});
            skLineSegment(sketch, "E272", {"start": v(-339.05, 21.97) * mm, "end": v(-338.98, 18.69) * mm});
            skLineSegment(sketch, "E273", {"start": v(-338.98, 18.69) * mm, "end": v(-338.98, 18.55) * mm});
            skLineSegment(sketch, "E274", {"start": v(-338.98, 18.55) * mm, "end": v(-338.97, 18.41) * mm});
            skLineSegment(sketch, "E275", {"start": v(-338.97, 18.41) * mm, "end": v(-338.55, 14.3) * mm});
            skLineSegment(sketch, "E276", {"start": v(-338.55, 14.3) * mm, "end": v(-338.47, 13.43) * mm});
            skLineSegment(sketch, "E277", {"start": v(-338.47, 13.43) * mm, "end": v(-338.23, 10.74) * mm});
            skLineSegment(sketch, "E278", {"start": v(-338.23, 10.74) * mm, "end": v(-338.2, 10.44) * mm});
            skLineSegment(sketch, "E279", {"start": v(-338.2, 10.44) * mm, "end": v(-337.78, 7.15) * mm});
            skLineSegment(sketch, "E280", {"start": v(-337.78, 7.15) * mm, "end": v(-337.77, 7.1) * mm});
            skLineSegment(sketch, "E281", {"start": v(-337.77, 7.1) * mm, "end": v(-337.07, 2.53) * mm});
            skLineSegment(sketch, "E282", {"start": v(-337.07, 2.53) * mm, "end": v(-336.8, 0.73) * mm});
            skLineSegment(sketch, "E283", {"start": v(-336.8, 0.73) * mm, "end": v(-336.64, 0) * mm});
            skLineSegment(sketch, "E284.0", {"start": v(-312.36, 6.3) * mm, "end": v(-312.35, 6.3) * mm});
            skLineSegment(sketch, "E284.1", {"start": v(-313.03, 10.68) * mm, "end": v(-312.36, 6.3) * mm});
            skLineSegment(sketch, "E284.2", {"start": v(-313.36, 13.3) * mm, "end": v(-313.03, 10.68) * mm});
            skLineSegment(sketch, "E284.3", {"start": v(-313.57, 15.7) * mm, "end": v(-313.36, 13.3) * mm});
            skLineSegment(sketch, "E284.4", {"start": v(-313.67, 16.71) * mm, "end": v(-313.57, 15.7) * mm});
            skLineSegment(sketch, "E284.5", {"start": v(-314, 20.02) * mm, "end": v(-313.67, 16.71) * mm});
            skLineSegment(sketch, "E284.6", {"start": v(-314.06, 22.62) * mm, "end": v(-314, 20.02) * mm});
            skLineSegment(sketch, "E284.7", {"start": v(-314.06, 22.81) * mm, "end": v(-314.06, 22.62) * mm});
            skLineSegment(sketch, "E284.8", {"start": v(-186.3, 198.28) * mm, "end": v(-187.73, 196.87) * mm});
            skLineSegment(sketch, "E284.9", {"start": v(-185.69, 198.88) * mm, "end": v(-186.3, 198.28) * mm});
            skLineSegment(sketch, "E284.10", {"start": v(-184.78, 199.72) * mm, "end": v(-185.69, 198.88) * mm});
            skLineSegment(sketch, "E284.11", {"start": v(-183.07, 201.23) * mm, "end": v(-184.78, 199.72) * mm});
            skLineSegment(sketch, "E284.12", {"start": v(-181.27, 202.95) * mm, "end": v(-183.07, 201.23) * mm});
            skLineSegment(sketch, "E284.13", {"start": v(-179.93, 204.3) * mm, "end": v(-181.27, 202.95) * mm});
            skLineSegment(sketch, "E284.14", {"start": v(-178.83, 205.33) * mm, "end": v(-179.93, 204.3) * mm});
            skLineSegment(sketch, "E284.15", {"start": v(-178.04, 206.08) * mm, "end": v(-178.83, 205.33) * mm});
            skLineSegment(sketch, "E284.16", {"start": v(-176.53, 207.54) * mm, "end": v(-178.04, 206.08) * mm});
            skLineSegment(sketch, "E284.17", {"start": v(-175.5, 208.57) * mm, "end": v(-176.53, 207.54) * mm});
            skLineSegment(sketch, "E284.18", {"start": v(-174.77, 209.28) * mm, "end": v(-175.5, 208.57) * mm});
            skLineSegment(sketch, "E284.19", {"start": v(-173.57, 210.51) * mm, "end": v(-174.77, 209.28) * mm});
            skLineSegment(sketch, "E284.20", {"start": v(-172.87, 211.22) * mm, "end": v(-173.57, 210.51) * mm});
            skLineSegment(sketch, "E284.21", {"start": v(-171.63, 212.45) * mm, "end": v(-172.87, 211.22) * mm});
            skLineSegment(sketch, "E284.22", {"start": v(-168.38, 215.37) * mm, "end": v(-171.63, 212.45) * mm});
            skLineSegment(sketch, "E284.23", {"start": v(-165.38, 218.37) * mm, "end": v(-168.38, 215.37) * mm});
            skLineSegment(sketch, "E284.24", {"start": v(-163.47, 220.2) * mm, "end": v(-165.38, 218.37) * mm});
            skLineSegment(sketch, "E284.25", {"start": v(-161.5, 222.18) * mm, "end": v(-163.47, 220.2) * mm});
            skLineSegment(sketch, "E284.26", {"start": v(-161.04, 222.66) * mm, "end": v(-161.5, 222.18) * mm});
            skLineSegment(sketch, "E284.27", {"start": v(-158.54, 225.37) * mm, "end": v(-161.04, 222.66) * mm});
            skLineSegment(sketch, "E284.28", {"start": v(-152.7, 229.64) * mm, "end": v(-158.54, 225.37) * mm});
            skLineSegment(sketch, "E284.29", {"start": v(-151.44, 230.66) * mm, "end": v(-152.7, 229.64) * mm});
            skLineSegment(sketch, "E284.30", {"start": v(-150.68, 231.37) * mm, "end": v(-151.44, 230.66) * mm});
            skLineSegment(sketch, "E284.31", {"start": v(-148.34, 233.58) * mm, "end": v(-150.68, 231.37) * mm});
            skLineSegment(sketch, "E284.32", {"start": v(-147.23, 234.73) * mm, "end": v(-148.34, 233.58) * mm});
            skLineSegment(sketch, "E284.33", {"start": v(-145.08, 237.04) * mm, "end": v(-147.23, 234.73) * mm});
            skLineSegment(sketch, "E284.34", {"start": v(-143.49, 238.45) * mm, "end": v(-145.08, 237.04) * mm});
            skLineSegment(sketch, "E284.35", {"start": v(-141.78, 239.94) * mm, "end": v(-143.49, 238.45) * mm});
            skLineSegment(sketch, "E284.36", {"start": v(-140.34, 241.4) * mm, "end": v(-141.78, 239.94) * mm});
            skLineSegment(sketch, "E284.37", {"start": v(-139.42, 242.35) * mm, "end": v(-140.34, 241.4) * mm});
            skLineSegment(sketch, "E284.38", {"start": v(-136.9, 244.69) * mm, "end": v(-139.42, 242.35) * mm});
            skLineSegment(sketch, "E284.39", {"start": v(-135.7, 245.96) * mm, "end": v(-136.9, 244.69) * mm});
            skLineSegment(sketch, "E284.40", {"start": v(-134.62, 247.06) * mm, "end": v(-135.7, 245.96) * mm});
            skLineSegment(sketch, "E284.41", {"start": v(-133.96, 247.71) * mm, "end": v(-134.62, 247.06) * mm});
            skLineSegment(sketch, "E284.42", {"start": v(-131.23, 250.4) * mm, "end": v(-133.96, 247.71) * mm});
            skLineSegment(sketch, "E284.43", {"start": v(-130.98, 250.65) * mm, "end": v(-131.23, 250.4) * mm});
            skLineSegment(sketch, "E284.44", {"start": v(-126.64, 254.86) * mm, "end": v(-130.98, 250.65) * mm});
            skLineSegment(sketch, "E284.45", {"start": v(-123.5, 257.17) * mm, "end": v(-126.64, 254.86) * mm});
            skLineSegment(sketch, "E284.46", {"start": v(-122.94, 257.56) * mm, "end": v(-123.5, 257.17) * mm});
            skLineSegment(sketch, "E284.47", {"start": v(-121.84, 258.32) * mm, "end": v(-122.94, 257.56) * mm});
            skLineSegment(sketch, "E284.48", {"start": v(-119.22, 259.87) * mm, "end": v(-121.84, 258.32) * mm});
            skLineSegment(sketch, "E284.49", {"start": v(-118.11, 260.49) * mm, "end": v(-119.22, 259.87) * mm});
            skLineSegment(sketch, "E284.50", {"start": v(-114.7, 262.22) * mm, "end": v(-118.11, 260.49) * mm});
            skLineSegment(sketch, "E284.51", {"start": v(-112.72, 263.03) * mm, "end": v(-114.7, 262.22) * mm});
            skLineSegment(sketch, "E284.52", {"start": v(-111.22, 263.64) * mm, "end": v(-112.72, 263.03) * mm});
            skLineSegment(sketch, "E284.53", {"start": v(-109.51, 264.18) * mm, "end": v(-111.22, 263.64) * mm});
            skLineSegment(sketch, "E284.54", {"start": v(-106.74, 265) * mm, "end": v(-109.51, 264.18) * mm});
            skLineSegment(sketch, "E284.55", {"start": v(-106.24, 265.15) * mm, "end": v(-106.74, 265) * mm});
            skLineSegment(sketch, "E284.56", {"start": v(-102.94, 266.03) * mm, "end": v(-106.24, 265.15) * mm});
            skLineSegment(sketch, "E284.57", {"start": v(-101.63, 266.4) * mm, "end": v(-102.94, 266.03) * mm});
            skLineSegment(sketch, "E284.58", {"start": v(-41.08, 276.69) * mm, "end": v(-45.18, 276.36) * mm});
            skLineSegment(sketch, "E284.59", {"start": v(-40.91, 276.7) * mm, "end": v(-41.08, 276.69) * mm});
            skLineSegment(sketch, "E284.60", {"start": v(-38.8, 276.87) * mm, "end": v(-40.91, 276.7) * mm});
            skLineSegment(sketch, "E284.61", {"start": v(-36.73, 277.03) * mm, "end": v(-38.8, 276.87) * mm});
            skLineSegment(sketch, "E284.62", {"start": v(-34.6, 277.17) * mm, "end": v(-36.73, 277.03) * mm});
            skLineSegment(sketch, "E284.63", {"start": v(-31.71, 277.37) * mm, "end": v(-34.6, 277.17) * mm});
            skLineSegment(sketch, "E284.64", {"start": v(-30.98, 277.42) * mm, "end": v(-31.71, 277.37) * mm});
            skLineSegment(sketch, "E284.65", {"start": v(-30.17, 277.45) * mm, "end": v(-30.98, 277.42) * mm});
            skLineSegment(sketch, "E284.66", {"start": v(-25.07, 277.65) * mm, "end": v(-30.17, 277.45) * mm});
            skLineSegment(sketch, "E284.67", {"start": v(-21.66, 277.8) * mm, "end": v(-25.07, 277.65) * mm});
            skLineSegment(sketch, "E284.68", {"start": v(-19.34, 277.89) * mm, "end": v(-21.66, 277.8) * mm});
            skLineSegment(sketch, "E284.69", {"start": v(-16.39, 277.91) * mm, "end": v(-19.34, 277.89) * mm});
            skLineSegment(sketch, "E284.70", {"start": v(-4.14, 277.7) * mm, "end": v(-5.03, 277.74) * mm});
            skLineSegment(sketch, "E284.71", {"start": v(-1.3, 277.59) * mm, "end": v(-4.14, 277.7) * mm});
            skLineSegment(sketch, "E284.72", {"start": v(2.14, 277.85) * mm, "end": v(-1.3, 277.59) * mm});
            skLineSegment(sketch, "E284.73", {"start": v(5, 278.43) * mm, "end": v(2.14, 277.85) * mm});
            skLineSegment(sketch, "E284.74", {"start": v(-5.03, 277.74) * mm, "end": v(-5.42, 277.75) * mm});
            skLineSegment(sketch, "E284.75", {"start": v(-5.42, 277.75) * mm, "end": v(-7.36, 277.8) * mm});
            skLineSegment(sketch, "E284.76", {"start": v(-7.36, 277.8) * mm, "end": v(-8.9, 277.77) * mm});
            skLineSegment(sketch, "E284.77", {"start": v(-8.9, 277.77) * mm, "end": v(-11.77, 277.77) * mm});
            skLineSegment(sketch, "E284.78", {"start": v(-11.77, 277.77) * mm, "end": v(-15.35, 277.88) * mm});
            skLineSegment(sketch, "E284.79", {"start": v(-15.35, 277.88) * mm, "end": v(-16.39, 277.91) * mm});
            skLineSegment(sketch, "E284.80", {"start": v(-45.18, 276.36) * mm, "end": v(-46.14, 276.28) * mm});
            skLineSegment(sketch, "E284.81", {"start": v(-46.14, 276.28) * mm, "end": v(-49.45, 275.97) * mm});
            skLineSegment(sketch, "E284.82", {"start": v(-49.45, 275.97) * mm, "end": v(-49.87, 275.93) * mm});
            skLineSegment(sketch, "E284.83", {"start": v(-49.87, 275.93) * mm, "end": v(-51.53, 275.74) * mm});
            skLineSegment(sketch, "E284.84", {"start": v(-51.53, 275.74) * mm, "end": v(-54.54, 275.34) * mm});
            skLineSegment(sketch, "E284.85", {"start": v(-54.54, 275.34) * mm, "end": v(-55.38, 275.23) * mm});
            skLineSegment(sketch, "E284.86", {"start": v(-55.38, 275.23) * mm, "end": v(-58.87, 274.74) * mm});
            skLineSegment(sketch, "E284.87", {"start": v(-58.87, 274.74) * mm, "end": v(-61.95, 274.34) * mm});
            skLineSegment(sketch, "E284.88", {"start": v(-61.95, 274.34) * mm, "end": v(-66.11, 273.74) * mm});
            skLineSegment(sketch, "E284.89", {"start": v(-66.11, 273.74) * mm, "end": v(-68.03, 273.45) * mm});
            skLineSegment(sketch, "E284.90", {"start": v(-68.03, 273.45) * mm, "end": v(-69.54, 273.2) * mm});
            skLineSegment(sketch, "E284.91", {"start": v(-69.54, 273.2) * mm, "end": v(-72.72, 272.64) * mm});
            skLineSegment(sketch, "E284.92", {"start": v(-72.72, 272.64) * mm, "end": v(-74.85, 272.28) * mm});
            skLineSegment(sketch, "E284.93", {"start": v(-74.85, 272.28) * mm, "end": v(-78.67, 271.58) * mm});
            skLineSegment(sketch, "E284.94", {"start": v(-78.67, 271.58) * mm, "end": v(-81.05, 271.14) * mm});
            skLineSegment(sketch, "E284.95", {"start": v(-81.05, 271.14) * mm, "end": v(-81.77, 270.99) * mm});
            skLineSegment(sketch, "E284.96", {"start": v(-81.77, 270.99) * mm, "end": v(-85.04, 270.27) * mm});
            skLineSegment(sketch, "E284.97", {"start": v(-85.04, 270.27) * mm, "end": v(-87.6, 269.76) * mm});
            skLineSegment(sketch, "E284.98", {"start": v(-87.6, 269.76) * mm, "end": v(-90.78, 269.05) * mm});
            skLineSegment(sketch, "E284.99", {"start": v(-90.78, 269.05) * mm, "end": v(-91.67, 268.85) * mm});
            skLineSegment(sketch, "E284.100", {"start": v(-91.67, 268.85) * mm, "end": v(-92.17, 268.73) * mm});
            skLineSegment(sketch, "E284.101", {"start": v(-92.17, 268.73) * mm, "end": v(-98.07, 267.27) * mm});
            skLineSegment(sketch, "E284.102", {"start": v(-98.07, 267.27) * mm, "end": v(-98.13, 267.25) * mm});
            skLineSegment(sketch, "E284.103", {"start": v(-98.13, 267.25) * mm, "end": v(-101.63, 266.4) * mm});
            skLineSegment(sketch, "E284.104", {"start": v(-187.73, 196.87) * mm, "end": v(-188, 196.62) * mm});
            skLineSegment(sketch, "E284.105", {"start": v(-188, 196.62) * mm, "end": v(-188.5, 196.11) * mm});
            skLineSegment(sketch, "E284.106", {"start": v(-188.5, 196.11) * mm, "end": v(-189.96, 194.74) * mm});
            skLineSegment(sketch, "E284.107", {"start": v(-189.96, 194.74) * mm, "end": v(-190.45, 194.3) * mm});
            skLineSegment(sketch, "E284.108", {"start": v(-190.45, 194.3) * mm, "end": v(-192.16, 192.63) * mm});
            skLineSegment(sketch, "E284.109", {"start": v(-192.16, 192.63) * mm, "end": v(-192.48, 192.32) * mm});
            skLineSegment(sketch, "E284.110", {"start": v(-192.48, 192.32) * mm, "end": v(-193.78, 191.1) * mm});
            skLineSegment(sketch, "E284.111", {"start": v(-193.78, 191.1) * mm, "end": v(-195.39, 189.31) * mm});
            skLineSegment(sketch, "E284.112", {"start": v(-195.39, 189.31) * mm, "end": v(-196.5, 188.25) * mm});
            skLineSegment(sketch, "E284.113", {"start": v(-196.5, 188.25) * mm, "end": v(-198.15, 186.6) * mm});
            skLineSegment(sketch, "E284.114", {"start": v(-198.15, 186.6) * mm, "end": v(-198.72, 186.08) * mm});
            skLineSegment(sketch, "E284.115", {"start": v(-198.72, 186.08) * mm, "end": v(-200.02, 184.91) * mm});
            skLineSegment(sketch, "E284.116", {"start": v(-200.02, 184.91) * mm, "end": v(-202.66, 182.37) * mm});
            skLineSegment(sketch, "E284.117", {"start": v(-202.66, 182.37) * mm, "end": v(-203.59, 181.46) * mm});
            skLineSegment(sketch, "E284.118", {"start": v(-203.59, 181.46) * mm, "end": v(-204.45, 180.59) * mm});
            skLineSegment(sketch, "E284.119", {"start": v(-204.45, 180.59) * mm, "end": v(-206.8, 178.28) * mm});
            skLineSegment(sketch, "E284.120", {"start": v(-206.8, 178.28) * mm, "end": v(-207.35, 177.75) * mm});
            skLineSegment(sketch, "E284.121", {"start": v(-207.35, 177.75) * mm, "end": v(-209.42, 175.78) * mm});
            skLineSegment(sketch, "E284.122", {"start": v(-209.42, 175.78) * mm, "end": v(-210.06, 175.13) * mm});
            skLineSegment(sketch, "E284.123", {"start": v(-210.06, 175.13) * mm, "end": v(-211.66, 173.56) * mm});
            skLineSegment(sketch, "E284.124", {"start": v(-211.66, 173.56) * mm, "end": v(-212.71, 172.59) * mm});
            skLineSegment(sketch, "E284.125", {"start": v(-212.71, 172.59) * mm, "end": v(-214.53, 170.96) * mm});
            skLineSegment(sketch, "E284.126", {"start": v(-214.53, 170.96) * mm, "end": v(-215.71, 169.83) * mm});
            skLineSegment(sketch, "E284.127", {"start": v(-215.71, 169.83) * mm, "end": v(-216.85, 168.74) * mm});
            skLineSegment(sketch, "E284.128", {"start": v(-216.85, 168.74) * mm, "end": v(-218.9, 166.61) * mm});
            skLineSegment(sketch, "E284.129", {"start": v(-218.9, 166.61) * mm, "end": v(-221.1, 164.65) * mm});
            skLineSegment(sketch, "E284.130", {"start": v(-221.1, 164.65) * mm, "end": v(-222.46, 163.45) * mm});
            skLineSegment(sketch, "E284.131", {"start": v(-222.46, 163.45) * mm, "end": v(-223.2, 162.79) * mm});
            skLineSegment(sketch, "E284.132", {"start": v(-223.2, 162.79) * mm, "end": v(-225.25, 161.13) * mm});
            skLineSegment(sketch, "E284.133", {"start": v(-225.25, 161.13) * mm, "end": v(-226.54, 160.15) * mm});
            skLineSegment(sketch, "E284.134", {"start": v(-226.54, 160.15) * mm, "end": v(-229.4, 157.81) * mm});
            skLineSegment(sketch, "E284.135", {"start": v(-229.4, 157.81) * mm, "end": v(-230.96, 156.66) * mm});
            skLineSegment(sketch, "E284.136", {"start": v(-230.96, 156.66) * mm, "end": v(-234.63, 154.12) * mm});
            skLineSegment(sketch, "E284.137", {"start": v(-234.63, 154.12) * mm, "end": v(-236.61, 152.76) * mm});
            skLineSegment(sketch, "E284.138", {"start": v(-236.61, 152.76) * mm, "end": v(-238.2, 151.67) * mm});
            skLineSegment(sketch, "E284.139", {"start": v(-238.2, 151.67) * mm, "end": v(-238.73, 151.31) * mm});
            skLineSegment(sketch, "E284.140", {"start": v(-238.73, 151.31) * mm, "end": v(-241.35, 149.6) * mm});
            skLineSegment(sketch, "E284.141", {"start": v(-241.35, 149.6) * mm, "end": v(-242.05, 149.12) * mm});
            skLineSegment(sketch, "E284.142", {"start": v(-242.05, 149.12) * mm, "end": v(-244.9, 147.14) * mm});
            skLineSegment(sketch, "E284.143", {"start": v(-244.9, 147.14) * mm, "end": v(-246.34, 146.17) * mm});
            skLineSegment(sketch, "E284.144", {"start": v(-246.34, 146.17) * mm, "end": v(-249.97, 143.8) * mm});
            skLineSegment(sketch, "E284.145", {"start": v(-249.97, 143.8) * mm, "end": v(-251.92, 142.5) * mm});
            skLineSegment(sketch, "E284.146", {"start": v(-251.92, 142.5) * mm, "end": v(-254.86, 140.48) * mm});
            skLineSegment(sketch, "E284.147", {"start": v(-254.86, 140.48) * mm, "end": v(-256.8, 139.21) * mm});
            skLineSegment(sketch, "E284.148", {"start": v(-256.8, 139.21) * mm, "end": v(-258.38, 138.14) * mm});
            skLineSegment(sketch, "E284.149", {"start": v(-258.38, 138.14) * mm, "end": v(-263.74, 134.08) * mm});
            skLineSegment(sketch, "E284.150", {"start": v(-263.74, 134.08) * mm, "end": v(-266.29, 132) * mm});
            skLineSegment(sketch, "E284.151", {"start": v(-266.29, 132) * mm, "end": v(-268.16, 130.39) * mm});
            skLineSegment(sketch, "E284.152", {"start": v(-268.16, 130.39) * mm, "end": v(-272.38, 126.53) * mm});
            skLineSegment(sketch, "E284.153", {"start": v(-272.38, 126.53) * mm, "end": v(-273.82, 125.34) * mm});
            skLineSegment(sketch, "E284.154", {"start": v(-273.82, 125.34) * mm, "end": v(-277.95, 120.94) * mm});
            skLineSegment(sketch, "E284.155", {"start": v(-277.95, 120.94) * mm, "end": v(-278.47, 120.4) * mm});
            skLineSegment(sketch, "E284.156", {"start": v(-278.47, 120.4) * mm, "end": v(-281.04, 117.48) * mm});
            skLineSegment(sketch, "E284.157", {"start": v(-281.04, 117.48) * mm, "end": v(-284.5, 113.55) * mm});
            skLineSegment(sketch, "E284.158", {"start": v(-284.5, 113.55) * mm, "end": v(-285.72, 112) * mm});
            skLineSegment(sketch, "E284.159", {"start": v(-285.72, 112) * mm, "end": v(-286.34, 111.23) * mm});
            skLineSegment(sketch, "E284.160", {"start": v(-286.34, 111.23) * mm, "end": v(-286.92, 110.44) * mm});
            skLineSegment(sketch, "E284.161", {"start": v(-286.92, 110.44) * mm, "end": v(-288.24, 108.65) * mm});
            skLineSegment(sketch, "E284.162", {"start": v(-288.24, 108.65) * mm, "end": v(-289.23, 107.28) * mm});
            skLineSegment(sketch, "E284.163", {"start": v(-289.23, 107.28) * mm, "end": v(-290.56, 105.45) * mm});
            skLineSegment(sketch, "E284.164", {"start": v(-290.56, 105.45) * mm, "end": v(-292.73, 102.32) * mm});
            skLineSegment(sketch, "E284.165", {"start": v(-292.73, 102.32) * mm, "end": v(-294.52, 99.41) * mm});
            skLineSegment(sketch, "E284.166", {"start": v(-294.52, 99.41) * mm, "end": v(-296, 96.9) * mm});
            skLineSegment(sketch, "E284.167", {"start": v(-296, 96.9) * mm, "end": v(-297.48, 94.2) * mm});
            skLineSegment(sketch, "E284.168", {"start": v(-297.48, 94.2) * mm, "end": v(-298.47, 92.47) * mm});
            skLineSegment(sketch, "E284.169", {"start": v(-298.47, 92.47) * mm, "end": v(-298.72, 92.02) * mm});
            skLineSegment(sketch, "E284.170", {"start": v(-298.72, 92.02) * mm, "end": v(-299.61, 90.37) * mm});
            skLineSegment(sketch, "E284.171", {"start": v(-299.61, 90.37) * mm, "end": v(-300.81, 88.13) * mm});
            skLineSegment(sketch, "E284.172", {"start": v(-300.81, 88.13) * mm, "end": v(-301.52, 86.7) * mm});
            skLineSegment(sketch, "E284.173", {"start": v(-301.52, 86.7) * mm, "end": v(-302.64, 84.24) * mm});
            skLineSegment(sketch, "E284.174", {"start": v(-302.64, 84.24) * mm, "end": v(-302.92, 83.57) * mm});
            skLineSegment(sketch, "E284.175", {"start": v(-302.92, 83.57) * mm, "end": v(-303.41, 82.45) * mm});
            skLineSegment(sketch, "E284.176", {"start": v(-303.41, 82.45) * mm, "end": v(-304.29, 80.44) * mm});
            skLineSegment(sketch, "E284.177", {"start": v(-304.29, 80.44) * mm, "end": v(-304.56, 79.8) * mm});
            skLineSegment(sketch, "E284.178", {"start": v(-304.56, 79.8) * mm, "end": v(-304.85, 79.06) * mm});
            skLineSegment(sketch, "E284.179", {"start": v(-304.85, 79.06) * mm, "end": v(-305.77, 76.68) * mm});
            skLineSegment(sketch, "E284.180", {"start": v(-305.77, 76.68) * mm, "end": v(-305.99, 76.08) * mm});
            skLineSegment(sketch, "E284.181", {"start": v(-305.99, 76.08) * mm, "end": v(-307.82, 71) * mm});
            skLineSegment(sketch, "E284.182", {"start": v(-307.82, 71) * mm, "end": v(-308.6, 68.67) * mm});
            skLineSegment(sketch, "E284.183", {"start": v(-308.6, 68.67) * mm, "end": v(-309.5, 65.4) * mm});
            skLineSegment(sketch, "E284.184", {"start": v(-309.5, 65.4) * mm, "end": v(-309.75, 64.5) * mm});
            skLineSegment(sketch, "E284.185", {"start": v(-309.75, 64.5) * mm, "end": v(-309.96, 63.74) * mm});
            skLineSegment(sketch, "E284.186", {"start": v(-309.96, 63.74) * mm, "end": v(-310.67, 61.03) * mm});
            skLineSegment(sketch, "E284.187", {"start": v(-310.67, 61.03) * mm, "end": v(-311.05, 59.45) * mm});
            skLineSegment(sketch, "E284.188", {"start": v(-311.05, 59.45) * mm, "end": v(-311.2, 58.74) * mm});
            skLineSegment(sketch, "E284.189", {"start": v(-311.2, 58.74) * mm, "end": v(-311.32, 58.2) * mm});
            skLineSegment(sketch, "E284.190", {"start": v(-311.32, 58.2) * mm, "end": v(-311.87, 55.54) * mm});
            skLineSegment(sketch, "E284.191", {"start": v(-311.87, 55.54) * mm, "end": v(-312, 54.66) * mm});
            skLineSegment(sketch, "E284.192", {"start": v(-312, 54.66) * mm, "end": v(-312.36, 52.36) * mm});
            skLineSegment(sketch, "E284.193", {"start": v(-312.36, 52.36) * mm, "end": v(-312.5, 51.5) * mm});
            skLineSegment(sketch, "E284.194", {"start": v(-312.5, 51.5) * mm, "end": v(-312.57, 50.98) * mm});
            skLineSegment(sketch, "E284.195", {"start": v(-312.57, 50.98) * mm, "end": v(-313.02, 48.24) * mm});
            skLineSegment(sketch, "E284.196", {"start": v(-313.02, 48.24) * mm, "end": v(-313.44, 44.74) * mm});
            skLineSegment(sketch, "E284.197", {"start": v(-313.44, 44.74) * mm, "end": v(-313.72, 41.02) * mm});
            skLineSegment(sketch, "E284.198", {"start": v(-313.72, 41.02) * mm, "end": v(-313.78, 40.04) * mm});
            skLineSegment(sketch, "E284.199", {"start": v(-313.78, 40.04) * mm, "end": v(-313.97, 37.04) * mm});
            skLineSegment(sketch, "E284.200", {"start": v(-313.97, 37.04) * mm, "end": v(-314.03, 35.44) * mm});
            skLineSegment(sketch, "E284.201", {"start": v(-314.03, 35.44) * mm, "end": v(-314.05, 33.72) * mm});
            skLineSegment(sketch, "E284.202", {"start": v(-314.05, 33.72) * mm, "end": v(-314.13, 30.57) * mm});
            skLineSegment(sketch, "E284.203", {"start": v(-314.13, 30.57) * mm, "end": v(-314.17, 28.81) * mm});
            skLineSegment(sketch, "E284.204", {"start": v(-314.17, 28.81) * mm, "end": v(-314.16, 27.32) * mm});
            skLineSegment(sketch, "E284.205", {"start": v(-314.16, 27.32) * mm, "end": v(-314.06, 22.81) * mm});
            skLineSegment(sketch, "E285.0", {"start": v(-331.88, 1.64) * mm, "end": v(-331.75, 1.06) * mm});
            skLineSegment(sketch, "E285.1", {"start": v(-332.13, 3.28) * mm, "end": v(-331.88, 1.64) * mm});
            skLineSegment(sketch, "E285.2", {"start": v(-332.84, 7.9) * mm, "end": v(-332.13, 3.28) * mm});
            skLineSegment(sketch, "E285.3", {"start": v(-333.23, 11.03) * mm, "end": v(-332.84, 7.9) * mm});
            skLineSegment(sketch, "E285.4", {"start": v(-333.26, 11.24) * mm, "end": v(-333.23, 11.03) * mm});
            skLineSegment(sketch, "E285.5", {"start": v(-333.5, 13.88) * mm, "end": v(-333.26, 11.24) * mm});
            skLineSegment(sketch, "E285.6", {"start": v(-333.58, 14.78) * mm, "end": v(-333.5, 13.88) * mm});
            skLineSegment(sketch, "E285.7", {"start": v(-333.98, 18.8) * mm, "end": v(-333.58, 14.78) * mm});
            skLineSegment(sketch, "E285.8", {"start": v(-334.05, 22.1) * mm, "end": v(-333.98, 18.8) * mm});
            skLineSegment(sketch, "E285.9", {"start": v(-334.06, 22.3) * mm, "end": v(-334.05, 22.1) * mm});
            skLineSegment(sketch, "E285.10", {"start": v(-334.16, 27.05) * mm, "end": v(-334.06, 22.3) * mm});
            skLineSegment(sketch, "E285.11", {"start": v(-334.17, 28.97) * mm, "end": v(-334.16, 27.05) * mm});
            skLineSegment(sketch, "E285.12", {"start": v(-334.13, 31.03) * mm, "end": v(-334.17, 28.97) * mm});
            skLineSegment(sketch, "E285.13", {"start": v(-334.05, 34.12) * mm, "end": v(-334.13, 31.03) * mm});
            skLineSegment(sketch, "E285.14", {"start": v(-334.02, 35.95) * mm, "end": v(-334.05, 34.12) * mm});
            skLineSegment(sketch, "E285.15", {"start": v(-333.95, 38.01) * mm, "end": v(-334.02, 35.95) * mm});
            skLineSegment(sketch, "E285.16", {"start": v(-333.74, 41.35) * mm, "end": v(-333.95, 38.01) * mm});
            skLineSegment(sketch, "E285.17", {"start": v(-333.67, 42.45) * mm, "end": v(-333.74, 41.35) * mm});
            skLineSegment(sketch, "E285.18", {"start": v(-333.4, 46.07) * mm, "end": v(-333.67, 42.45) * mm});
            skLineSegment(sketch, "E285.19", {"start": v(-333.34, 46.77) * mm, "end": v(-333.4, 46.07) * mm});
            skLineSegment(sketch, "E285.20", {"start": v(-333.33, 46.82) * mm, "end": v(-333.34, 46.77) * mm});
            skLineSegment(sketch, "E285.21", {"start": v(-333.31, 46.99) * mm, "end": v(-333.33, 46.82) * mm});
            skLineSegment(sketch, "E285.22", {"start": v(-332.88, 50.58) * mm, "end": v(-333.31, 46.99) * mm});
            skLineSegment(sketch, "E285.23", {"start": v(-332.82, 51.04) * mm, "end": v(-332.88, 50.58) * mm});
            skLineSegment(sketch, "E285.24", {"start": v(-332.79, 51.26) * mm, "end": v(-332.82, 51.04) * mm});
            skLineSegment(sketch, "E285.25", {"start": v(-332.34, 54.02) * mm, "end": v(-332.79, 51.26) * mm});
            skLineSegment(sketch, "E285.26", {"start": v(-332.28, 54.47) * mm, "end": v(-332.34, 54.02) * mm});
            skLineSegment(sketch, "E285.27", {"start": v(-332.12, 55.45) * mm, "end": v(-332.28, 54.47) * mm});
            skLineSegment(sketch, "E285.28", {"start": v(-331.77, 57.7) * mm, "end": v(-332.12, 55.45) * mm});
            skLineSegment(sketch, "E285.29", {"start": v(-331.57, 59.01) * mm, "end": v(-331.77, 57.7) * mm});
            skLineSegment(sketch, "E285.30", {"start": v(-330.87, 62.45) * mm, "end": v(-331.57, 59.01) * mm});
            skLineSegment(sketch, "E285.31", {"start": v(-330.73, 63.04) * mm, "end": v(-330.87, 62.45) * mm});
            skLineSegment(sketch, "E285.32", {"start": v(-330.57, 63.85) * mm, "end": v(-330.73, 63.04) * mm});
            skLineSegment(sketch, "E285.33", {"start": v(-330.07, 65.91) * mm, "end": v(-330.57, 63.85) * mm});
            skLineSegment(sketch, "E285.34", {"start": v(-329.28, 68.93) * mm, "end": v(-330.07, 65.91) * mm});
            skLineSegment(sketch, "E285.35", {"start": v(-329.04, 69.8) * mm, "end": v(-329.28, 68.93) * mm});
            skLineSegment(sketch, "E285.36", {"start": v(-328.78, 70.74) * mm, "end": v(-329.04, 69.8) * mm});
            skLineSegment(sketch, "E285.37", {"start": v(-327.73, 74.5) * mm, "end": v(-328.78, 70.74) * mm});
            skLineSegment(sketch, "E285.38", {"start": v(-326.73, 77.53) * mm, "end": v(-327.73, 74.5) * mm});
            skLineSegment(sketch, "E285.39", {"start": v(-324.77, 82.95) * mm, "end": v(-326.73, 77.53) * mm});
            skLineSegment(sketch, "E285.40", {"start": v(-324.48, 83.72) * mm, "end": v(-324.77, 82.95) * mm});
            skLineSegment(sketch, "E285.41", {"start": v(-323.49, 86.32) * mm, "end": v(-324.48, 83.72) * mm});
            skLineSegment(sketch, "E285.42", {"start": v(-323.08, 87.36) * mm, "end": v(-323.49, 86.32) * mm});
            skLineSegment(sketch, "E285.43", {"start": v(-322.67, 88.33) * mm, "end": v(-323.08, 87.36) * mm});
            skLineSegment(sketch, "E285.44", {"start": v(-321.74, 90.45) * mm, "end": v(-322.67, 88.33) * mm});
            skLineSegment(sketch, "E285.45", {"start": v(-321.28, 91.5) * mm, "end": v(-321.74, 90.45) * mm});
            skLineSegment(sketch, "E285.46", {"start": v(-320.95, 92.3) * mm, "end": v(-321.28, 91.5) * mm});
            skLineSegment(sketch, "E285.47", {"start": v(-319.47, 95.55) * mm, "end": v(-320.95, 92.3) * mm});
            skLineSegment(sketch, "E285.48", {"start": v(-319.32, 95.84) * mm, "end": v(-319.47, 95.55) * mm});
            skLineSegment(sketch, "E285.49", {"start": v(-319, 96.46) * mm, "end": v(-319.32, 95.84) * mm});
            skLineSegment(sketch, "E285.50", {"start": v(-318.59, 97.3) * mm, "end": v(-319, 96.46) * mm});
            skLineSegment(sketch, "E285.51", {"start": v(-317.22, 99.86) * mm, "end": v(-318.59, 97.3) * mm});
            skLineSegment(sketch, "E285.52", {"start": v(-316.24, 101.65) * mm, "end": v(-317.22, 99.86) * mm});
            skLineSegment(sketch, "E285.53", {"start": v(-315.89, 102.3) * mm, "end": v(-316.24, 101.65) * mm});
            skLineSegment(sketch, "E285.54", {"start": v(-314.93, 103.97) * mm, "end": v(-315.89, 102.3) * mm});
            skLineSegment(sketch, "E285.55", {"start": v(-313.61, 106.38) * mm, "end": v(-314.93, 103.97) * mm});
            skLineSegment(sketch, "E285.56", {"start": v(-313.49, 106.61) * mm, "end": v(-313.61, 106.38) * mm});
            skLineSegment(sketch, "E285.57", {"start": v(-313.3, 106.94) * mm, "end": v(-313.49, 106.61) * mm});
            skLineSegment(sketch, "E285.58", {"start": v(-311.67, 109.71) * mm, "end": v(-313.3, 106.94) * mm});
            skLineSegment(sketch, "E285.59", {"start": v(-309.7, 112.91) * mm, "end": v(-311.67, 109.71) * mm});
            skLineSegment(sketch, "E285.60", {"start": v(-309.47, 113.28) * mm, "end": v(-309.7, 112.91) * mm});
            skLineSegment(sketch, "E285.61", {"start": v(-309.01, 113.95) * mm, "end": v(-309.47, 113.28) * mm});
            skLineSegment(sketch, "E285.62", {"start": v(-306.86, 117.04) * mm, "end": v(-309.01, 113.95) * mm});
            skLineSegment(sketch, "E285.63", {"start": v(-305.42, 119.02) * mm, "end": v(-306.86, 117.04) * mm});
            skLineSegment(sketch, "E285.64", {"start": v(-304.4, 120.43) * mm, "end": v(-305.42, 119.02) * mm});
            skLineSegment(sketch, "E285.65", {"start": v(-303.03, 122.3) * mm, "end": v(-304.4, 120.43) * mm});
            skLineSegment(sketch, "E285.66", {"start": v(-302.2, 123.42) * mm, "end": v(-303.03, 122.3) * mm});
            skLineSegment(sketch, "E285.67", {"start": v(-301.37, 124.46) * mm, "end": v(-302.2, 123.42) * mm});
            skLineSegment(sketch, "E285.68", {"start": v(-299.86, 126.36) * mm, "end": v(-301.37, 124.46) * mm});
            skLineSegment(sketch, "E285.69", {"start": v(-299.7, 126.57) * mm, "end": v(-299.86, 126.36) * mm});
            skLineSegment(sketch, "E285.70", {"start": v(-299.52, 126.78) * mm, "end": v(-299.7, 126.57) * mm});
            skLineSegment(sketch, "E285.71", {"start": v(-299.11, 127.21) * mm, "end": v(-299.52, 126.78) * mm});
            skLineSegment(sketch, "E285.72", {"start": v(-164.63, 245.7) * mm, "end": v(-164.93, 245.46) * mm});
            skLineSegment(sketch, "E285.73", {"start": v(-164.37, 245.95) * mm, "end": v(-164.63, 245.7) * mm});
            skLineSegment(sketch, "E285.74", {"start": v(-162.4, 247.8) * mm, "end": v(-164.37, 245.95) * mm});
            skLineSegment(sketch, "E285.75", {"start": v(-161.76, 248.47) * mm, "end": v(-162.4, 247.8) * mm});
            skLineSegment(sketch, "E285.76", {"start": v(-160.36, 249.98) * mm, "end": v(-161.76, 248.47) * mm});
            skLineSegment(sketch, "E285.77", {"start": v(-159.28, 251.11) * mm, "end": v(-160.36, 249.98) * mm});
            skLineSegment(sketch, "E285.78", {"start": v(-158.63, 251.73) * mm, "end": v(-159.28, 251.11) * mm});
            skLineSegment(sketch, "E285.79", {"start": v(-158.16, 252.17) * mm, "end": v(-158.63, 251.73) * mm});
            skLineSegment(sketch, "E285.80", {"start": v(-157.42, 252.83) * mm, "end": v(-158.16, 252.17) * mm});
            skLineSegment(sketch, "E285.81", {"start": v(-156.7, 253.48) * mm, "end": v(-157.42, 252.83) * mm});
            skLineSegment(sketch, "E285.82", {"start": v(-155.5, 254.5) * mm, "end": v(-156.7, 253.48) * mm});
            skLineSegment(sketch, "E285.83", {"start": v(-154.65, 255.38) * mm, "end": v(-155.5, 254.5) * mm});
            skLineSegment(sketch, "E285.84", {"start": v(-153.27, 256.8) * mm, "end": v(-154.65, 255.38) * mm});
            skLineSegment(sketch, "E285.85", {"start": v(-152.52, 257.49) * mm, "end": v(-153.27, 256.8) * mm});
            skLineSegment(sketch, "E285.86", {"start": v(-151, 258.89) * mm, "end": v(-152.52, 257.49) * mm});
            skLineSegment(sketch, "E285.87", {"start": v(-150.1, 259.85) * mm, "end": v(-151, 258.89) * mm});
            skLineSegment(sketch, "E285.88", {"start": v(-148.73, 261.24) * mm, "end": v(-150.1, 259.85) * mm});
            skLineSegment(sketch, "E285.89", {"start": v(-147.96, 262) * mm, "end": v(-148.73, 261.24) * mm});
            skLineSegment(sketch, "E285.90", {"start": v(-145.35, 264.56) * mm, "end": v(-147.96, 262) * mm});
            skLineSegment(sketch, "E285.91", {"start": v(-145.05, 264.86) * mm, "end": v(-145.35, 264.56) * mm});
            skLineSegment(sketch, "E285.92", {"start": v(-142.35, 267.48) * mm, "end": v(-145.05, 264.86) * mm});
            skLineSegment(sketch, "E285.93", {"start": v(-141.64, 268.19) * mm, "end": v(-142.35, 267.48) * mm});
            skLineSegment(sketch, "E285.94", {"start": v(-140.79, 268.96) * mm, "end": v(-141.64, 268.19) * mm});
            skLineSegment(sketch, "E285.95", {"start": v(-139.63, 270) * mm, "end": v(-140.79, 268.96) * mm});
            skLineSegment(sketch, "E285.96", {"start": v(-138.17, 271.19) * mm, "end": v(-139.63, 270) * mm});
            skLineSegment(sketch, "E285.97", {"start": v(-137.84, 271.45) * mm, "end": v(-138.17, 271.19) * mm});
            skLineSegment(sketch, "E285.98", {"start": v(-136.88, 272.15) * mm, "end": v(-137.84, 271.45) * mm});
            skLineSegment(sketch, "E285.99", {"start": v(-135.16, 273.42) * mm, "end": v(-136.88, 272.15) * mm});
            skLineSegment(sketch, "E285.100", {"start": v(-134.32, 274) * mm, "end": v(-135.16, 273.42) * mm});
            skLineSegment(sketch, "E285.101", {"start": v(-132.62, 275.18) * mm, "end": v(-134.32, 274) * mm});
            skLineSegment(sketch, "E285.102", {"start": v(-130.32, 276.54) * mm, "end": v(-132.62, 275.18) * mm});
            skLineSegment(sketch, "E285.103", {"start": v(-129.55, 277.02) * mm, "end": v(-130.32, 276.54) * mm});
            skLineSegment(sketch, "E285.104", {"start": v(-129.16, 277.23) * mm, "end": v(-129.55, 277.02) * mm});
            skLineSegment(sketch, "E285.105", {"start": v(-127.5, 278.15) * mm, "end": v(-129.16, 277.23) * mm});
            skLineSegment(sketch, "E285.106", {"start": v(-124.77, 279.54) * mm, "end": v(-127.5, 278.15) * mm});
            skLineSegment(sketch, "E285.107", {"start": v(-123.9, 279.98) * mm, "end": v(-124.77, 279.54) * mm});
            skLineSegment(sketch, "E285.108", {"start": v(-121.83, 280.91) * mm, "end": v(-123.9, 279.98) * mm});
            skLineSegment(sketch, "E285.109", {"start": v(-120.28, 281.54) * mm, "end": v(-121.83, 280.91) * mm});
            skLineSegment(sketch, "E285.110", {"start": v(-118.5, 282.28) * mm, "end": v(-120.28, 281.54) * mm});
            skLineSegment(sketch, "E285.111", {"start": v(-116.7, 282.89) * mm, "end": v(-118.5, 282.28) * mm});
            skLineSegment(sketch, "E285.112", {"start": v(-115.35, 283.31) * mm, "end": v(-116.7, 282.89) * mm});
            skLineSegment(sketch, "E285.113", {"start": v(-112.42, 284.17) * mm, "end": v(-115.35, 283.31) * mm});
            skLineSegment(sketch, "E285.114", {"start": v(-111.72, 284.38) * mm, "end": v(-112.42, 284.17) * mm});
            skLineSegment(sketch, "E285.115", {"start": v(-111.66, 284.4) * mm, "end": v(-111.72, 284.38) * mm});
            skLineSegment(sketch, "E285.116", {"start": v(-111.4, 284.47) * mm, "end": v(-111.66, 284.4) * mm});
            skLineSegment(sketch, "E285.117", {"start": v(-108.18, 285.34) * mm, "end": v(-111.4, 284.47) * mm});
            skLineSegment(sketch, "E285.118", {"start": v(-106.65, 285.75) * mm, "end": v(-108.18, 285.34) * mm});
            skLineSegment(sketch, "E285.119", {"start": v(-102.87, 286.68) * mm, "end": v(-106.65, 285.75) * mm});
            skLineSegment(sketch, "E285.120", {"start": v(-102.84, 286.69) * mm, "end": v(-102.87, 286.68) * mm});
            skLineSegment(sketch, "E285.121", {"start": v(-102.8, 286.7) * mm, "end": v(-102.84, 286.69) * mm});
            skLineSegment(sketch, "E285.122", {"start": v(-40.36, 296.81) * mm, "end": v(-42.5, 296.64) * mm});
            skLineSegment(sketch, "E285.123", {"start": v(-38.16, 296.98) * mm, "end": v(-40.36, 296.81) * mm});
            skLineSegment(sketch, "E285.124", {"start": v(-35.97, 297.13) * mm, "end": v(-38.16, 296.98) * mm});
            skLineSegment(sketch, "E285.125", {"start": v(-33.04, 297.33) * mm, "end": v(-35.97, 297.13) * mm});
            skLineSegment(sketch, "E285.126", {"start": v(-32.03, 297.4) * mm, "end": v(-33.04, 297.33) * mm});
            skLineSegment(sketch, "E285.127", {"start": v(-30.96, 297.44) * mm, "end": v(-32.03, 297.4) * mm});
            skLineSegment(sketch, "E285.128", {"start": v(-25.9, 297.63) * mm, "end": v(-30.96, 297.44) * mm});
            skLineSegment(sketch, "E285.129", {"start": v(-22.47, 297.79) * mm, "end": v(-25.9, 297.63) * mm});
            skLineSegment(sketch, "E285.130", {"start": v(-19.8, 297.89) * mm, "end": v(-22.47, 297.79) * mm});
            skLineSegment(sketch, "E285.131", {"start": v(-16.5, 297.91) * mm, "end": v(-19.8, 297.89) * mm});
            skLineSegment(sketch, "E285.132", {"start": v(-16.2, 297.91) * mm, "end": v(-16.5, 297.91) * mm});
            skLineSegment(sketch, "E285.133", {"start": v(-15.97, 297.9) * mm, "end": v(-16.2, 297.91) * mm});
            skLineSegment(sketch, "E285.134", {"start": v(-3.37, 297.69) * mm, "end": v(-4.35, 297.72) * mm});
            skLineSegment(sketch, "E285.135", {"start": v(-1.66, 297.62) * mm, "end": v(-3.37, 297.69) * mm});
            skLineSegment(sketch, "E285.136", {"start": v(-0.63, 297.7) * mm, "end": v(-1.66, 297.62) * mm});
            skLineSegment(sketch, "E285.137", {"start": v(1, 298.03) * mm, "end": v(-0.63, 297.7) * mm});
            skLineSegment(sketch, "E285.138", {"start": v(-4.35, 297.72) * mm, "end": v(-4.87, 297.74) * mm});
            skLineSegment(sketch, "E285.139", {"start": v(-4.87, 297.74) * mm, "end": v(-7.25, 297.8) * mm});
            skLineSegment(sketch, "E285.140", {"start": v(-7.25, 297.8) * mm, "end": v(-9.05, 297.77) * mm});
            skLineSegment(sketch, "E285.141", {"start": v(-9.05, 297.77) * mm, "end": v(-11.46, 297.77) * mm});
            skLineSegment(sketch, "E285.142", {"start": v(-11.46, 297.77) * mm, "end": v(-14.76, 297.88) * mm});
            skLineSegment(sketch, "E285.143", {"start": v(-14.76, 297.88) * mm, "end": v(-15.97, 297.9) * mm});
            skLineSegment(sketch, "E285.144", {"start": v(-42.5, 296.64) * mm, "end": v(-42.63, 296.63) * mm});
            skLineSegment(sketch, "E285.145", {"start": v(-42.63, 296.63) * mm, "end": v(-46.8, 296.3) * mm});
            skLineSegment(sketch, "E285.146", {"start": v(-46.8, 296.3) * mm, "end": v(-47.92, 296.2) * mm});
            skLineSegment(sketch, "E285.147", {"start": v(-47.92, 296.2) * mm, "end": v(-51.42, 295.87) * mm});
            skLineSegment(sketch, "E285.148", {"start": v(-51.42, 295.87) * mm, "end": v(-51.99, 295.81) * mm});
            skLineSegment(sketch, "E285.149", {"start": v(-51.99, 295.81) * mm, "end": v(-53.94, 295.6) * mm});
            skLineSegment(sketch, "E285.150", {"start": v(-53.94, 295.6) * mm, "end": v(-57.19, 295.17) * mm});
            skLineSegment(sketch, "E285.151", {"start": v(-57.19, 295.17) * mm, "end": v(-58.09, 295.05) * mm});
            skLineSegment(sketch, "E285.152", {"start": v(-58.09, 295.05) * mm, "end": v(-61.56, 294.56) * mm});
            skLineSegment(sketch, "E285.153", {"start": v(-61.56, 294.56) * mm, "end": v(-64.69, 294.15) * mm});
            skLineSegment(sketch, "E285.154", {"start": v(-64.69, 294.15) * mm, "end": v(-69, 293.53) * mm});
            skLineSegment(sketch, "E285.155", {"start": v(-69, 293.53) * mm, "end": v(-71.15, 293.2) * mm});
            skLineSegment(sketch, "E285.156", {"start": v(-71.15, 293.2) * mm, "end": v(-72.91, 292.91) * mm});
            skLineSegment(sketch, "E285.157", {"start": v(-72.91, 292.91) * mm, "end": v(-76.12, 292.35) * mm});
            skLineSegment(sketch, "E285.158", {"start": v(-76.12, 292.35) * mm, "end": v(-78.33, 291.98) * mm});
            skLineSegment(sketch, "E285.159", {"start": v(-78.33, 291.98) * mm, "end": v(-82.3, 291.25) * mm});
            skLineSegment(sketch, "E285.160", {"start": v(-82.3, 291.25) * mm, "end": v(-84.94, 290.76) * mm});
            skLineSegment(sketch, "E285.161", {"start": v(-84.94, 290.76) * mm, "end": v(-86, 290.53) * mm});
            skLineSegment(sketch, "E285.162", {"start": v(-86, 290.53) * mm, "end": v(-89.14, 289.84) * mm});
            skLineSegment(sketch, "E285.163", {"start": v(-89.14, 289.84) * mm, "end": v(-91.71, 289.33) * mm});
            skLineSegment(sketch, "E285.164", {"start": v(-91.71, 289.33) * mm, "end": v(-95.09, 288.58) * mm});
            skLineSegment(sketch, "E285.165", {"start": v(-95.09, 288.58) * mm, "end": v(-96.22, 288.33) * mm});
            skLineSegment(sketch, "E285.166", {"start": v(-96.22, 288.33) * mm, "end": v(-97, 288.14) * mm});
            skLineSegment(sketch, "E285.167", {"start": v(-97, 288.14) * mm, "end": v(-102.8, 286.7) * mm});
            skLineSegment(sketch, "E285.168", {"start": v(-164.93, 245.46) * mm, "end": v(-167.23, 243.79) * mm});
            skLineSegment(sketch, "E285.169", {"start": v(-167.23, 243.79) * mm, "end": v(-168.43, 243.14) * mm});
            skLineSegment(sketch, "E285.170", {"start": v(-168.43, 243.14) * mm, "end": v(-170.26, 242.01) * mm});
            skLineSegment(sketch, "E285.171", {"start": v(-170.26, 242.01) * mm, "end": v(-170.6, 241.82) * mm});
            skLineSegment(sketch, "E285.172", {"start": v(-170.6, 241.82) * mm, "end": v(-171.92, 240.44) * mm});
            skLineSegment(sketch, "E285.173", {"start": v(-171.92, 240.44) * mm, "end": v(-173.35, 238.82) * mm});
            skLineSegment(sketch, "E285.174", {"start": v(-173.35, 238.82) * mm, "end": v(-173.46, 238.7) * mm});
            skLineSegment(sketch, "E285.175", {"start": v(-173.46, 238.7) * mm, "end": v(-173.56, 238.59) * mm});
            skLineSegment(sketch, "E285.176", {"start": v(-173.56, 238.59) * mm, "end": v(-175.65, 236.32) * mm});
            skLineSegment(sketch, "E285.177", {"start": v(-175.65, 236.32) * mm, "end": v(-175.86, 236.1) * mm});
            skLineSegment(sketch, "E285.178", {"start": v(-175.86, 236.1) * mm, "end": v(-177.47, 234.48) * mm});
            skLineSegment(sketch, "E285.179", {"start": v(-177.47, 234.48) * mm, "end": v(-178.87, 233.14) * mm});
            skLineSegment(sketch, "E285.180", {"start": v(-178.87, 233.14) * mm, "end": v(-179.38, 232.67) * mm});
            skLineSegment(sketch, "E285.181", {"start": v(-179.38, 232.67) * mm, "end": v(-179.53, 232.5) * mm});
            skLineSegment(sketch, "E285.182", {"start": v(-179.53, 232.5) * mm, "end": v(-182.14, 229.89) * mm});
            skLineSegment(sketch, "E285.183", {"start": v(-182.14, 229.89) * mm, "end": v(-184.61, 227.67) * mm});
            skLineSegment(sketch, "E285.184", {"start": v(-184.61, 227.67) * mm, "end": v(-185.13, 227.2) * mm});
            skLineSegment(sketch, "E285.185", {"start": v(-185.13, 227.2) * mm, "end": v(-185.41, 226.95) * mm});
            skLineSegment(sketch, "E285.186", {"start": v(-185.41, 226.95) * mm, "end": v(-186.07, 226.3) * mm});
            skLineSegment(sketch, "E285.187", {"start": v(-186.07, 226.3) * mm, "end": v(-187.03, 225.34) * mm});
            skLineSegment(sketch, "E285.188", {"start": v(-187.03, 225.34) * mm, "end": v(-187.85, 224.51) * mm});
            skLineSegment(sketch, "E285.189", {"start": v(-187.85, 224.51) * mm, "end": v(-188.9, 223.43) * mm});
            skLineSegment(sketch, "E285.190", {"start": v(-188.9, 223.43) * mm, "end": v(-189.5, 222.85) * mm});
            skLineSegment(sketch, "E285.191", {"start": v(-189.5, 222.85) * mm, "end": v(-190.54, 221.82) * mm});
            skLineSegment(sketch, "E285.192", {"start": v(-190.54, 221.82) * mm, "end": v(-191.87, 220.52) * mm});
            skLineSegment(sketch, "E285.193", {"start": v(-191.87, 220.52) * mm, "end": v(-192.5, 219.93) * mm});
            skLineSegment(sketch, "E285.194", {"start": v(-192.5, 219.93) * mm, "end": v(-193.9, 218.64) * mm});
            skLineSegment(sketch, "E285.195", {"start": v(-193.9, 218.64) * mm, "end": v(-195.3, 217.2) * mm});
            skLineSegment(sketch, "E285.196", {"start": v(-195.3, 217.2) * mm, "end": v(-196.6, 215.96) * mm});
            skLineSegment(sketch, "E285.197", {"start": v(-196.6, 215.96) * mm, "end": v(-198.2, 214.54) * mm});
            skLineSegment(sketch, "E285.198", {"start": v(-198.2, 214.54) * mm, "end": v(-199.43, 213.4) * mm});
            skLineSegment(sketch, "E285.199", {"start": v(-199.43, 213.4) * mm, "end": v(-200.25, 212.61) * mm});
            skLineSegment(sketch, "E285.200", {"start": v(-200.25, 212.61) * mm, "end": v(-201.79, 211.1) * mm});
            skLineSegment(sketch, "E285.201", {"start": v(-201.79, 211.1) * mm, "end": v(-202.06, 210.83) * mm});
            skLineSegment(sketch, "E285.202", {"start": v(-202.06, 210.83) * mm, "end": v(-202.4, 210.5) * mm});
            skLineSegment(sketch, "E285.203", {"start": v(-202.4, 210.5) * mm, "end": v(-203.46, 209.5) * mm});
            skLineSegment(sketch, "E285.204", {"start": v(-203.46, 209.5) * mm, "end": v(-204.08, 208.95) * mm});
            skLineSegment(sketch, "E285.205", {"start": v(-204.08, 208.95) * mm, "end": v(-206.17, 206.9) * mm});
            skLineSegment(sketch, "E285.206", {"start": v(-206.17, 206.9) * mm, "end": v(-206.38, 206.7) * mm});
            skLineSegment(sketch, "E285.207", {"start": v(-206.38, 206.7) * mm, "end": v(-206.99, 206.13) * mm});
            skLineSegment(sketch, "E285.208", {"start": v(-206.99, 206.13) * mm, "end": v(-208.05, 205.13) * mm});
            skLineSegment(sketch, "E285.209", {"start": v(-208.05, 205.13) * mm, "end": v(-208.2, 204.96) * mm});
            skLineSegment(sketch, "E285.210", {"start": v(-208.2, 204.96) * mm, "end": v(-209.71, 203.29) * mm});
            skLineSegment(sketch, "E285.211", {"start": v(-209.71, 203.29) * mm, "end": v(-210.48, 202.56) * mm});
            skLineSegment(sketch, "E285.212", {"start": v(-210.48, 202.56) * mm, "end": v(-212, 201.03) * mm});
            skLineSegment(sketch, "E285.213", {"start": v(-212, 201.03) * mm, "end": v(-212.15, 200.9) * mm});
            skLineSegment(sketch, "E285.214", {"start": v(-212.15, 200.9) * mm, "end": v(-214.43, 198.86) * mm});
            skLineSegment(sketch, "E285.215", {"start": v(-214.43, 198.86) * mm, "end": v(-215.1, 198.16) * mm});
            skLineSegment(sketch, "E285.216", {"start": v(-215.1, 198.16) * mm, "end": v(-216.6, 196.7) * mm});
            skLineSegment(sketch, "E285.217", {"start": v(-216.6, 196.7) * mm, "end": v(-217.67, 195.66) * mm});
            skLineSegment(sketch, "E285.218", {"start": v(-217.67, 195.66) * mm, "end": v(-218.56, 194.77) * mm});
            skLineSegment(sketch, "E285.219", {"start": v(-218.56, 194.77) * mm, "end": v(-220.77, 192.6) * mm});
            skLineSegment(sketch, "E285.220", {"start": v(-220.77, 192.6) * mm, "end": v(-221.17, 192.2) * mm});
            skLineSegment(sketch, "E285.221", {"start": v(-221.17, 192.2) * mm, "end": v(-223.46, 190.03) * mm});
            skLineSegment(sketch, "E285.222", {"start": v(-223.46, 190.03) * mm, "end": v(-224.2, 189.27) * mm});
            skLineSegment(sketch, "E285.223", {"start": v(-224.2, 189.27) * mm, "end": v(-225.47, 188.03) * mm});
            skLineSegment(sketch, "E285.224", {"start": v(-225.47, 188.03) * mm, "end": v(-226.16, 187.39) * mm});
            skLineSegment(sketch, "E285.225", {"start": v(-226.16, 187.39) * mm, "end": v(-227.86, 185.88) * mm});
            skLineSegment(sketch, "E285.226", {"start": v(-227.86, 185.88) * mm, "end": v(-228.47, 185.3) * mm});
            skLineSegment(sketch, "E285.227", {"start": v(-228.47, 185.3) * mm, "end": v(-229.57, 184.26) * mm});
            skLineSegment(sketch, "E285.228", {"start": v(-229.57, 184.26) * mm, "end": v(-230.92, 182.96) * mm});
            skLineSegment(sketch, "E285.229", {"start": v(-230.92, 182.96) * mm, "end": v(-231.33, 182.54) * mm});
            skLineSegment(sketch, "E285.230", {"start": v(-231.33, 182.54) * mm, "end": v(-232.8, 181.02) * mm});
            skLineSegment(sketch, "E285.231", {"start": v(-232.8, 181.02) * mm, "end": v(-234.35, 179.62) * mm});
            skLineSegment(sketch, "E285.232", {"start": v(-234.35, 179.62) * mm, "end": v(-235.68, 178.46) * mm});
            skLineSegment(sketch, "E285.233", {"start": v(-235.68, 178.46) * mm, "end": v(-236.15, 178.04) * mm});
            skLineSegment(sketch, "E285.234", {"start": v(-236.15, 178.04) * mm, "end": v(-237.59, 176.87) * mm});
            skLineSegment(sketch, "E285.235", {"start": v(-237.59, 176.87) * mm, "end": v(-238.92, 175.87) * mm});
            skLineSegment(sketch, "E285.236", {"start": v(-238.92, 175.87) * mm, "end": v(-241.7, 173.6) * mm});
            skLineSegment(sketch, "E285.237", {"start": v(-241.7, 173.6) * mm, "end": v(-242.6, 172.92) * mm});
            skLineSegment(sketch, "E285.238", {"start": v(-242.6, 172.92) * mm, "end": v(-245.97, 170.6) * mm});
            skLineSegment(sketch, "E285.239", {"start": v(-245.97, 170.6) * mm, "end": v(-247.96, 169.23) * mm});
            skLineSegment(sketch, "E285.240", {"start": v(-247.96, 169.23) * mm, "end": v(-249.4, 168.24) * mm});
            skLineSegment(sketch, "E285.241", {"start": v(-249.4, 168.24) * mm, "end": v(-249.7, 168.03) * mm});
            skLineSegment(sketch, "E285.242", {"start": v(-249.7, 168.03) * mm, "end": v(-252.53, 166.19) * mm});
            skLineSegment(sketch, "E285.243", {"start": v(-252.53, 166.19) * mm, "end": v(-253.44, 165.55) * mm});
            skLineSegment(sketch, "E285.244", {"start": v(-253.44, 165.55) * mm, "end": v(-256.16, 163.67) * mm});
            skLineSegment(sketch, "E285.245", {"start": v(-256.16, 163.67) * mm, "end": v(-257.4, 162.84) * mm});
            skLineSegment(sketch, "E285.246", {"start": v(-257.4, 162.84) * mm, "end": v(-261.01, 160.48) * mm});
            skLineSegment(sketch, "E285.247", {"start": v(-261.01, 160.48) * mm, "end": v(-263.13, 159.06) * mm});
            skLineSegment(sketch, "E285.248", {"start": v(-263.13, 159.06) * mm, "end": v(-265.98, 157.1) * mm});
            skLineSegment(sketch, "E285.249", {"start": v(-265.98, 157.1) * mm, "end": v(-267.91, 155.84) * mm});
            skLineSegment(sketch, "E285.250", {"start": v(-267.91, 155.84) * mm, "end": v(-270.05, 154.4) * mm});
            skLineSegment(sketch, "E285.251", {"start": v(-270.05, 154.4) * mm, "end": v(-275.28, 150.43) * mm});
            skLineSegment(sketch, "E285.252", {"start": v(-275.28, 150.43) * mm, "end": v(-275.74, 150.1) * mm});
            skLineSegment(sketch, "E285.253", {"start": v(-275.74, 150.1) * mm, "end": v(-276.63, 149.38) * mm});
            skLineSegment(sketch, "E285.254", {"start": v(-276.63, 149.38) * mm, "end": v(-279.14, 147.32) * mm});
            skLineSegment(sketch, "E285.255", {"start": v(-279.14, 147.32) * mm, "end": v(-281.12, 145.62) * mm});
            skLineSegment(sketch, "E285.256", {"start": v(-281.12, 145.62) * mm, "end": v(-281.7, 145.12) * mm});
            skLineSegment(sketch, "E285.257", {"start": v(-281.7, 145.12) * mm, "end": v(-281.8, 145.03) * mm});
            skLineSegment(sketch, "E285.258", {"start": v(-281.8, 145.03) * mm, "end": v(-282.15, 144.7) * mm});
            skLineSegment(sketch, "E285.259", {"start": v(-282.15, 144.7) * mm, "end": v(-285.5, 141.63) * mm});
            skLineSegment(sketch, "E285.260", {"start": v(-285.5, 141.63) * mm, "end": v(-287.2, 140.23) * mm});
            skLineSegment(sketch, "E285.261", {"start": v(-287.2, 140.23) * mm, "end": v(-287.4, 140.06) * mm});
            skLineSegment(sketch, "E285.262", {"start": v(-287.4, 140.06) * mm, "end": v(-289.24, 138.24) * mm});
            skLineSegment(sketch, "E285.263", {"start": v(-289.24, 138.24) * mm, "end": v(-289.3, 138.18) * mm});
            skLineSegment(sketch, "E285.264", {"start": v(-289.3, 138.18) * mm, "end": v(-290.49, 136.81) * mm});
            skLineSegment(sketch, "E285.265", {"start": v(-290.49, 136.81) * mm, "end": v(-292.52, 134.65) * mm});
            skLineSegment(sketch, "E285.266", {"start": v(-292.52, 134.65) * mm, "end": v(-293.25, 133.87) * mm});
            skLineSegment(sketch, "E285.267", {"start": v(-293.25, 133.87) * mm, "end": v(-293.29, 133.83) * mm});
            skLineSegment(sketch, "E285.268", {"start": v(-293.29, 133.83) * mm, "end": v(-296.05, 130.7) * mm});
            skLineSegment(sketch, "E285.269", {"start": v(-296.05, 130.7) * mm, "end": v(-299.11, 127.21) * mm});
            skLineSegment(sketch, "E286", {"start": v(1, 298.03) * mm, "end": v(5, 278.43) * mm});
            skLineSegment(sketch, "E287", {"start": v(-312.35, 6.3) * mm, "end": v(-331.75, 1.06) * mm});
            skSolve(sketch);
        }
        {
            var Q0;
            Q0=qCreatedBy(makeId("Right.planeOp"),FACE);
            cPlane(context, id + "F2", {"entities" : qUnion([Q0]), "cplaneType" : CPlaneType.OFFSET, "offset" : 28 * mm, "oppositeDirection" : true, "width" : 150 * mm, "height" : 150 * mm});
        }
        {
            var Q0;
            Q0=qCreatedBy(id+"F2.planeOp",FACE);
            var sketch = newSketch(context, id + "F3", { "sketchPlane" : qUnion([Q0])});
            skPoint(sketch, "E288", {"position": v(0, 0) * mm});
            skLineSegment(sketch, "E289", {"start": v(0, 302.93) * mm, "end": v(-1.33, 302.66) * mm});
            skLineSegment(sketch, "E290", {"start": v(-1.33, 302.66) * mm, "end": v(-1.75, 302.63) * mm});
            skLineSegment(sketch, "E291", {"start": v(-1.75, 302.63) * mm, "end": v(-3.18, 302.69) * mm});
            skLineSegment(sketch, "E292", {"start": v(-3.18, 302.69) * mm, "end": v(-4.19, 302.72) * mm});
            skLineSegment(sketch, "E293", {"start": v(-4.19, 302.72) * mm, "end": v(-4.73, 302.74) * mm});
            skLineSegment(sketch, "E294", {"start": v(-4.73, 302.74) * mm, "end": v(-7.22, 302.8) * mm});
            skLineSegment(sketch, "E295", {"start": v(-7.22, 302.8) * mm, "end": v(-9.08, 302.77) * mm});
            skLineSegment(sketch, "E296", {"start": v(-9.08, 302.77) * mm, "end": v(-11.39, 302.77) * mm});
            skLineSegment(sketch, "E297", {"start": v(-11.39, 302.77) * mm, "end": v(-14.62, 302.87) * mm});
            skLineSegment(sketch, "E298", {"start": v(-14.62, 302.87) * mm, "end": v(-15.84, 302.9) * mm});
            skLineSegment(sketch, "E299", {"start": v(-15.84, 302.9) * mm, "end": v(-16.17, 302.91) * mm});
            skLineSegment(sketch, "E300", {"start": v(-16.17, 302.91) * mm, "end": v(-16.53, 302.91) * mm});
            skLineSegment(sketch, "E301", {"start": v(-16.53, 302.91) * mm, "end": v(-19.91, 302.89) * mm});
            skLineSegment(sketch, "E302", {"start": v(-19.91, 302.89) * mm, "end": v(-22.68, 302.78) * mm});
            skLineSegment(sketch, "E303", {"start": v(-22.68, 302.78) * mm, "end": v(-26.11, 302.63) * mm});
            skLineSegment(sketch, "E304", {"start": v(-26.11, 302.63) * mm, "end": v(-31.16, 302.43) * mm});
            skLineSegment(sketch, "E305", {"start": v(-31.16, 302.43) * mm, "end": v(-32.29, 302.39) * mm});
            skLineSegment(sketch, "E306", {"start": v(-32.29, 302.39) * mm, "end": v(-33.37, 302.32) * mm});
            skLineSegment(sketch, "E307", {"start": v(-33.37, 302.32) * mm, "end": v(-36.32, 302.12) * mm});
            skLineSegment(sketch, "E308", {"start": v(-36.32, 302.12) * mm, "end": v(-38.52, 301.96) * mm});
            skLineSegment(sketch, "E309", {"start": v(-38.52, 301.96) * mm, "end": v(-40.75, 301.8) * mm});
            skLineSegment(sketch, "E310", {"start": v(-40.75, 301.8) * mm, "end": v(-42.89, 301.62) * mm});
            skLineSegment(sketch, "E311", {"start": v(-42.89, 301.62) * mm, "end": v(-43.02, 301.61) * mm});
            skLineSegment(sketch, "E312", {"start": v(-43.02, 301.61) * mm, "end": v(-47.21, 301.28) * mm});
            skLineSegment(sketch, "E313", {"start": v(-47.21, 301.28) * mm, "end": v(-48.36, 301.18) * mm});
            skLineSegment(sketch, "E314", {"start": v(-48.36, 301.18) * mm, "end": v(-51.91, 300.85) * mm});
            skLineSegment(sketch, "E315", {"start": v(-51.91, 300.85) * mm, "end": v(-52.52, 300.78) * mm});
            skLineSegment(sketch, "E316", {"start": v(-52.52, 300.78) * mm, "end": v(-54.54, 300.56) * mm});
            skLineSegment(sketch, "E317", {"start": v(-54.54, 300.56) * mm, "end": v(-57.85, 300.12) * mm});
            skLineSegment(sketch, "E318", {"start": v(-57.85, 300.12) * mm, "end": v(-58.76, 300) * mm});
            skLineSegment(sketch, "E319", {"start": v(-58.76, 300) * mm, "end": v(-62.24, 299.52) * mm});
            skLineSegment(sketch, "E320", {"start": v(-62.24, 299.52) * mm, "end": v(-65.37, 299.1) * mm});
            skLineSegment(sketch, "E321", {"start": v(-65.37, 299.1) * mm, "end": v(-69.73, 298.47) * mm});
            skLineSegment(sketch, "E322", {"start": v(-69.73, 298.47) * mm, "end": v(-71.93, 298.15) * mm});
            skLineSegment(sketch, "E323", {"start": v(-71.93, 298.15) * mm, "end": v(-73.76, 297.84) * mm});
            skLineSegment(sketch, "E324", {"start": v(-73.76, 297.84) * mm, "end": v(-76.97, 297.28) * mm});
            skLineSegment(sketch, "E325", {"start": v(-76.97, 297.28) * mm, "end": v(-79.2, 296.9) * mm});
            skLineSegment(sketch, "E326", {"start": v(-79.2, 296.9) * mm, "end": v(-83.2, 296.17) * mm});
            skLineSegment(sketch, "E327", {"start": v(-83.2, 296.17) * mm, "end": v(-85.92, 295.66) * mm});
            skLineSegment(sketch, "E328", {"start": v(-85.92, 295.66) * mm, "end": v(-87.06, 295.42) * mm});
            skLineSegment(sketch, "E329", {"start": v(-87.06, 295.42) * mm, "end": v(-90.16, 294.74) * mm});
            skLineSegment(sketch, "E330", {"start": v(-90.16, 294.74) * mm, "end": v(-92.74, 294.23) * mm});
            skLineSegment(sketch, "E331", {"start": v(-92.74, 294.23) * mm, "end": v(-96.17, 293.46) * mm});
            skLineSegment(sketch, "E332", {"start": v(-96.17, 293.46) * mm, "end": v(-97.36, 293.2) * mm});
            skLineSegment(sketch, "E333", {"start": v(-97.36, 293.2) * mm, "end": v(-98.2, 293) * mm});
            skLineSegment(sketch, "E334", {"start": v(-98.2, 293) * mm, "end": v(-103.97, 291.56) * mm});
            skLineSegment(sketch, "E335", {"start": v(-103.97, 291.56) * mm, "end": v(-104.02, 291.55) * mm});
            skLineSegment(sketch, "E336", {"start": v(-104.02, 291.55) * mm, "end": v(-104.07, 291.54) * mm});
            skLineSegment(sketch, "E337", {"start": v(-104.07, 291.54) * mm, "end": v(-107.9, 290.6) * mm});
            skLineSegment(sketch, "E338", {"start": v(-107.9, 290.6) * mm, "end": v(-109.48, 290.16) * mm});
            skLineSegment(sketch, "E339", {"start": v(-109.48, 290.16) * mm, "end": v(-112.69, 289.3) * mm});
            skLineSegment(sketch, "E340", {"start": v(-112.69, 289.3) * mm, "end": v(-113, 289.22) * mm});
            skLineSegment(sketch, "E341", {"start": v(-113, 289.22) * mm, "end": v(-113.13, 289.18) * mm});
            skLineSegment(sketch, "E342", {"start": v(-113.13, 289.18) * mm, "end": v(-113.84, 288.97) * mm});
            skLineSegment(sketch, "E343", {"start": v(-113.84, 288.97) * mm, "end": v(-116.81, 288.1) * mm});
            skLineSegment(sketch, "E344", {"start": v(-116.81, 288.1) * mm, "end": v(-118.25, 287.64) * mm});
            skLineSegment(sketch, "E345", {"start": v(-118.25, 287.64) * mm, "end": v(-120.24, 286.96) * mm});
            skLineSegment(sketch, "E346", {"start": v(-120.24, 286.96) * mm, "end": v(-122.17, 286.17) * mm});
            skLineSegment(sketch, "E347", {"start": v(-122.17, 286.17) * mm, "end": v(-123.8, 285.5) * mm});
            skLineSegment(sketch, "E348", {"start": v(-123.8, 285.5) * mm, "end": v(-126.08, 284.5) * mm});
            skLineSegment(sketch, "E349", {"start": v(-126.08, 284.5) * mm, "end": v(-127.05, 283.99) * mm});
            skLineSegment(sketch, "E350", {"start": v(-127.05, 283.99) * mm, "end": v(-129.84, 282.57) * mm});
            skLineSegment(sketch, "E351", {"start": v(-129.84, 282.57) * mm, "end": v(-131.55, 281.62) * mm});
            skLineSegment(sketch, "E352", {"start": v(-131.55, 281.62) * mm, "end": v(-132.06, 281.35) * mm});
            skLineSegment(sketch, "E353", {"start": v(-132.06, 281.35) * mm, "end": v(-132.92, 280.81) * mm});
            skLineSegment(sketch, "E354", {"start": v(-132.92, 280.81) * mm, "end": v(-135.31, 279.39) * mm});
            skLineSegment(sketch, "E355", {"start": v(-135.31, 279.39) * mm, "end": v(-137.16, 278.12) * mm});
            skLineSegment(sketch, "E356", {"start": v(-137.16, 278.12) * mm, "end": v(-138.07, 277.49) * mm});
            skLineSegment(sketch, "E357", {"start": v(-138.07, 277.49) * mm, "end": v(-139.84, 276.19) * mm});
            skLineSegment(sketch, "E358", {"start": v(-139.84, 276.19) * mm, "end": v(-140.9, 275.41) * mm});
            skLineSegment(sketch, "E359", {"start": v(-140.9, 275.41) * mm, "end": v(-141.31, 275.08) * mm});
            skLineSegment(sketch, "E360", {"start": v(-141.31, 275.08) * mm, "end": v(-142.88, 273.8) * mm});
            skLineSegment(sketch, "E361", {"start": v(-142.88, 273.8) * mm, "end": v(-144.14, 272.67) * mm});
            skLineSegment(sketch, "E362", {"start": v(-144.14, 272.67) * mm, "end": v(-145.09, 271.82) * mm});
            skLineSegment(sketch, "E363", {"start": v(-145.09, 271.82) * mm, "end": v(-145.86, 271.04) * mm});
            skLineSegment(sketch, "E364", {"start": v(-145.86, 271.04) * mm, "end": v(-148.57, 268.42) * mm});
            skLineSegment(sketch, "E365", {"start": v(-148.57, 268.42) * mm, "end": v(-148.88, 268.1) * mm});
            skLineSegment(sketch, "E366", {"start": v(-148.88, 268.1) * mm, "end": v(-151.46, 265.56) * mm});
            skLineSegment(sketch, "E367", {"start": v(-151.46, 265.56) * mm, "end": v(-152.25, 264.79) * mm});
            skLineSegment(sketch, "E368", {"start": v(-152.25, 264.79) * mm, "end": v(-153.7, 263.33) * mm});
            skLineSegment(sketch, "E369", {"start": v(-153.7, 263.33) * mm, "end": v(-154.53, 262.44) * mm});
            skLineSegment(sketch, "E370", {"start": v(-154.53, 262.44) * mm, "end": v(-155.9, 261.16) * mm});
            skLineSegment(sketch, "E371", {"start": v(-155.9, 261.16) * mm, "end": v(-156.74, 260.4) * mm});
            skLineSegment(sketch, "E372", {"start": v(-156.74, 260.4) * mm, "end": v(-158.23, 258.88) * mm});
            skLineSegment(sketch, "E373", {"start": v(-158.23, 258.88) * mm, "end": v(-158.94, 258.15) * mm});
            skLineSegment(sketch, "E374", {"start": v(-158.94, 258.15) * mm, "end": v(-160, 257.23) * mm});
            skLineSegment(sketch, "E375", {"start": v(-160, 257.23) * mm, "end": v(-160.75, 256.56) * mm});
            skLineSegment(sketch, "E376", {"start": v(-160.75, 256.56) * mm, "end": v(-161.54, 255.85) * mm});
            skLineSegment(sketch, "E377", {"start": v(-161.54, 255.85) * mm, "end": v(-162.05, 255.37) * mm});
            skLineSegment(sketch, "E378", {"start": v(-162.05, 255.37) * mm, "end": v(-162.8, 254.67) * mm});
            skLineSegment(sketch, "E379", {"start": v(-162.8, 254.67) * mm, "end": v(-164, 253.4) * mm});
            skLineSegment(sketch, "E380", {"start": v(-164, 253.4) * mm, "end": v(-165.4, 251.9) * mm});
            skLineSegment(sketch, "E381", {"start": v(-165.4, 251.9) * mm, "end": v(-165.92, 251.36) * mm});
            skLineSegment(sketch, "E382", {"start": v(-165.92, 251.36) * mm, "end": v(-167.8, 249.6) * mm});
            skLineSegment(sketch, "E383", {"start": v(-167.8, 249.6) * mm, "end": v(-167.93, 249.47) * mm});
            skLineSegment(sketch, "E384", {"start": v(-167.93, 249.47) * mm, "end": v(-167.99, 249.42) * mm});
            skLineSegment(sketch, "E385", {"start": v(-167.99, 249.42) * mm, "end": v(-169.9, 248.03) * mm});
            skLineSegment(sketch, "E386", {"start": v(-169.9, 248.03) * mm, "end": v(-170.93, 247.48) * mm});
            skLineSegment(sketch, "E387", {"start": v(-170.93, 247.48) * mm, "end": v(-172.86, 246.29) * mm});
            skLineSegment(sketch, "E388", {"start": v(-172.86, 246.29) * mm, "end": v(-173.5, 245.9) * mm});
            skLineSegment(sketch, "E389", {"start": v(-173.5, 245.9) * mm, "end": v(-174.08, 245.4) * mm});
            skLineSegment(sketch, "E390", {"start": v(-174.08, 245.4) * mm, "end": v(-175.59, 243.84) * mm});
            skLineSegment(sketch, "E391", {"start": v(-175.59, 243.84) * mm, "end": v(-177.02, 242.22) * mm});
            skLineSegment(sketch, "E392", {"start": v(-177.02, 242.22) * mm, "end": v(-177.21, 242.02) * mm});
            skLineSegment(sketch, "E393", {"start": v(-177.21, 242.02) * mm, "end": v(-177.34, 241.86) * mm});
            skLineSegment(sketch, "E394", {"start": v(-177.34, 241.86) * mm, "end": v(-179.3, 239.74) * mm});
            skLineSegment(sketch, "E395", {"start": v(-179.3, 239.74) * mm, "end": v(-179.45, 239.59) * mm});
            skLineSegment(sketch, "E396", {"start": v(-179.45, 239.59) * mm, "end": v(-180.97, 238.05) * mm});
            skLineSegment(sketch, "E397", {"start": v(-180.97, 238.05) * mm, "end": v(-182.31, 236.77) * mm});
            skLineSegment(sketch, "E398", {"start": v(-182.31, 236.77) * mm, "end": v(-182.86, 236.26) * mm});
            skLineSegment(sketch, "E399", {"start": v(-182.86, 236.26) * mm, "end": v(-182.94, 236.17) * mm});
            skLineSegment(sketch, "E400", {"start": v(-182.94, 236.17) * mm, "end": v(-183.1, 236.01) * mm});
            skLineSegment(sketch, "E401", {"start": v(-183.1, 236.01) * mm, "end": v(-185.59, 233.52) * mm});
            skLineSegment(sketch, "E402", {"start": v(-185.59, 233.52) * mm, "end": v(-187.96, 231.4) * mm});
            skLineSegment(sketch, "E403", {"start": v(-187.96, 231.4) * mm, "end": v(-188.49, 230.9) * mm});
            skLineSegment(sketch, "E404", {"start": v(-188.49, 230.9) * mm, "end": v(-188.86, 230.57) * mm});
            skLineSegment(sketch, "E405", {"start": v(-188.86, 230.57) * mm, "end": v(-189.59, 229.85) * mm});
            skLineSegment(sketch, "E406", {"start": v(-189.59, 229.85) * mm, "end": v(-190.57, 228.87) * mm});
            skLineSegment(sketch, "E407", {"start": v(-190.57, 228.87) * mm, "end": v(-191.42, 228.01) * mm});
            skLineSegment(sketch, "E408", {"start": v(-191.42, 228.01) * mm, "end": v(-192.44, 226.97) * mm});
            skLineSegment(sketch, "E409", {"start": v(-192.44, 226.97) * mm, "end": v(-193, 226.42) * mm});
            skLineSegment(sketch, "E410", {"start": v(-193, 226.42) * mm, "end": v(-194.05, 225.39) * mm});
            skLineSegment(sketch, "E411", {"start": v(-194.05, 225.39) * mm, "end": v(-195.33, 224.13) * mm});
            skLineSegment(sketch, "E412", {"start": v(-195.33, 224.13) * mm, "end": v(-195.92, 223.58) * mm});
            skLineSegment(sketch, "E413", {"start": v(-195.92, 223.58) * mm, "end": v(-197.38, 222.22) * mm});
            skLineSegment(sketch, "E414", {"start": v(-197.38, 222.22) * mm, "end": v(-198.82, 220.76) * mm});
            skLineSegment(sketch, "E415", {"start": v(-198.82, 220.76) * mm, "end": v(-199.99, 219.64) * mm});
            skLineSegment(sketch, "E416", {"start": v(-199.99, 219.64) * mm, "end": v(-201.56, 218.25) * mm});
            skLineSegment(sketch, "E417", {"start": v(-201.56, 218.25) * mm, "end": v(-202.86, 217.04) * mm});
            skLineSegment(sketch, "E418", {"start": v(-202.86, 217.04) * mm, "end": v(-203.74, 216.2) * mm});
            skLineSegment(sketch, "E419", {"start": v(-203.74, 216.2) * mm, "end": v(-205.3, 214.66) * mm});
            skLineSegment(sketch, "E420", {"start": v(-205.3, 214.66) * mm, "end": v(-205.58, 214.38) * mm});
            skLineSegment(sketch, "E421", {"start": v(-205.58, 214.38) * mm, "end": v(-205.87, 214.1) * mm});
            skLineSegment(sketch, "E422", {"start": v(-205.87, 214.1) * mm, "end": v(-206.83, 213.19) * mm});
            skLineSegment(sketch, "E423", {"start": v(-206.83, 213.19) * mm, "end": v(-207.48, 212.61) * mm});
            skLineSegment(sketch, "E424", {"start": v(-207.48, 212.61) * mm, "end": v(-209.68, 210.47) * mm});
            skLineSegment(sketch, "E425", {"start": v(-209.68, 210.47) * mm, "end": v(-209.85, 210.3) * mm});
            skLineSegment(sketch, "E426", {"start": v(-209.85, 210.3) * mm, "end": v(-210.41, 209.77) * mm});
            skLineSegment(sketch, "E427", {"start": v(-210.41, 209.77) * mm, "end": v(-211.57, 208.68) * mm});
            skLineSegment(sketch, "E428", {"start": v(-211.57, 208.68) * mm, "end": v(-211.66, 208.6) * mm});
            skLineSegment(sketch, "E429", {"start": v(-211.66, 208.6) * mm, "end": v(-211.92, 208.3) * mm});
            skLineSegment(sketch, "E430", {"start": v(-211.92, 208.3) * mm, "end": v(-213.3, 206.78) * mm});
            skLineSegment(sketch, "E431", {"start": v(-213.3, 206.78) * mm, "end": v(-213.97, 206.14) * mm});
            skLineSegment(sketch, "E432", {"start": v(-213.97, 206.14) * mm, "end": v(-215.47, 204.64) * mm});
            skLineSegment(sketch, "E433", {"start": v(-215.47, 204.64) * mm, "end": v(-215.51, 204.6) * mm});
            skLineSegment(sketch, "E434", {"start": v(-215.51, 204.6) * mm, "end": v(-217.9, 202.46) * mm});
            skLineSegment(sketch, "E435", {"start": v(-217.9, 202.46) * mm, "end": v(-218.65, 201.68) * mm});
            skLineSegment(sketch, "E436", {"start": v(-218.65, 201.68) * mm, "end": v(-220.09, 200.3) * mm});
            skLineSegment(sketch, "E437", {"start": v(-220.09, 200.3) * mm, "end": v(-221.2, 199.2) * mm});
            skLineSegment(sketch, "E438", {"start": v(-221.2, 199.2) * mm, "end": v(-222.08, 198.31) * mm});
            skLineSegment(sketch, "E439", {"start": v(-222.08, 198.31) * mm, "end": v(-224.26, 196.17) * mm});
            skLineSegment(sketch, "E440", {"start": v(-224.26, 196.17) * mm, "end": v(-224.63, 195.81) * mm});
            skLineSegment(sketch, "E441", {"start": v(-224.63, 195.81) * mm, "end": v(-226.97, 193.6) * mm});
            skLineSegment(sketch, "E442", {"start": v(-226.97, 193.6) * mm, "end": v(-227.75, 192.8) * mm});
            skLineSegment(sketch, "E443", {"start": v(-227.75, 192.8) * mm, "end": v(-228.92, 191.65) * mm});
            skLineSegment(sketch, "E444", {"start": v(-228.92, 191.65) * mm, "end": v(-229.52, 191.09) * mm});
            skLineSegment(sketch, "E445", {"start": v(-229.52, 191.09) * mm, "end": v(-231.22, 189.58) * mm});
            skLineSegment(sketch, "E446", {"start": v(-231.22, 189.58) * mm, "end": v(-231.9, 188.94) * mm});
            skLineSegment(sketch, "E447", {"start": v(-231.9, 188.94) * mm, "end": v(-233.03, 187.87) * mm});
            skLineSegment(sketch, "E448", {"start": v(-233.03, 187.87) * mm, "end": v(-234.44, 186.51) * mm});
            skLineSegment(sketch, "E449", {"start": v(-234.44, 186.51) * mm, "end": v(-234.92, 186.02) * mm});
            skLineSegment(sketch, "E450", {"start": v(-234.92, 186.02) * mm, "end": v(-236.27, 184.62) * mm});
            skLineSegment(sketch, "E451", {"start": v(-236.27, 184.62) * mm, "end": v(-237.66, 183.36) * mm});
            skLineSegment(sketch, "E452", {"start": v(-237.66, 183.36) * mm, "end": v(-238.98, 182.21) * mm});
            skLineSegment(sketch, "E453", {"start": v(-238.98, 182.21) * mm, "end": v(-239.39, 181.85) * mm});
            skLineSegment(sketch, "E454", {"start": v(-239.39, 181.85) * mm, "end": v(-240.67, 180.81) * mm});
            skLineSegment(sketch, "E455", {"start": v(-240.67, 180.81) * mm, "end": v(-242.01, 179.8) * mm});
            skLineSegment(sketch, "E456", {"start": v(-242.01, 179.8) * mm, "end": v(-244.77, 177.54) * mm});
            skLineSegment(sketch, "E457", {"start": v(-244.77, 177.54) * mm, "end": v(-245.52, 176.99) * mm});
            skLineSegment(sketch, "E458", {"start": v(-245.52, 176.99) * mm, "end": v(-248.8, 174.71) * mm});
            skLineSegment(sketch, "E459", {"start": v(-248.8, 174.71) * mm, "end": v(-250.8, 173.34) * mm});
            skLineSegment(sketch, "E460", {"start": v(-250.8, 173.34) * mm, "end": v(-252.2, 172.38) * mm});
            skLineSegment(sketch, "E461", {"start": v(-252.2, 172.38) * mm, "end": v(-252.45, 172.2) * mm});
            skLineSegment(sketch, "E462", {"start": v(-252.45, 172.2) * mm, "end": v(-255.33, 170.33) * mm});
            skLineSegment(sketch, "E463", {"start": v(-255.33, 170.33) * mm, "end": v(-256.3, 169.66) * mm});
            skLineSegment(sketch, "E464", {"start": v(-256.3, 169.66) * mm, "end": v(-258.98, 167.8) * mm});
            skLineSegment(sketch, "E465", {"start": v(-258.98, 167.8) * mm, "end": v(-260.16, 167.01) * mm});
            skLineSegment(sketch, "E466", {"start": v(-260.16, 167.01) * mm, "end": v(-263.77, 164.64) * mm});
            skLineSegment(sketch, "E467", {"start": v(-263.77, 164.64) * mm, "end": v(-265.93, 163.2) * mm});
            skLineSegment(sketch, "E468", {"start": v(-265.93, 163.2) * mm, "end": v(-268.76, 161.26) * mm});
            skLineSegment(sketch, "E469", {"start": v(-268.76, 161.26) * mm, "end": v(-270.69, 160) * mm});
            skLineSegment(sketch, "E470", {"start": v(-270.69, 160) * mm, "end": v(-272.92, 158.48) * mm});
            skLineSegment(sketch, "E471", {"start": v(-272.92, 158.48) * mm, "end": v(-273.06, 158.38) * mm});
            skLineSegment(sketch, "E472", {"start": v(-273.06, 158.38) * mm, "end": v(-278.26, 154.45) * mm});
            skLineSegment(sketch, "E473", {"start": v(-278.26, 154.45) * mm, "end": v(-278.78, 154.07) * mm});
            skLineSegment(sketch, "E474", {"start": v(-278.78, 154.07) * mm, "end": v(-279.79, 153.26) * mm});
            skLineSegment(sketch, "E475", {"start": v(-279.79, 153.26) * mm, "end": v(-282.35, 151.15) * mm});
            skLineSegment(sketch, "E476", {"start": v(-282.35, 151.15) * mm, "end": v(-284.38, 149.41) * mm});
            skLineSegment(sketch, "E477", {"start": v(-284.38, 149.41) * mm, "end": v(-285, 148.87) * mm});
            skLineSegment(sketch, "E478", {"start": v(-285, 148.87) * mm, "end": v(-285.22, 148.68) * mm});
            skLineSegment(sketch, "E479", {"start": v(-285.22, 148.68) * mm, "end": v(-285.57, 148.34) * mm});
            skLineSegment(sketch, "E480", {"start": v(-285.57, 148.34) * mm, "end": v(-288.77, 145.41) * mm});
            skLineSegment(sketch, "E481", {"start": v(-288.77, 145.41) * mm, "end": v(-290.44, 144.04) * mm});
            skLineSegment(sketch, "E482", {"start": v(-290.44, 144.04) * mm, "end": v(-290.8, 143.72) * mm});
            skLineSegment(sketch, "E483", {"start": v(-290.8, 143.72) * mm, "end": v(-292.79, 141.76) * mm});
            skLineSegment(sketch, "E484", {"start": v(-292.79, 141.76) * mm, "end": v(-292.98, 141.56) * mm});
            skLineSegment(sketch, "E485", {"start": v(-292.98, 141.56) * mm, "end": v(-294.2, 140.16) * mm});
            skLineSegment(sketch, "E486", {"start": v(-294.2, 140.16) * mm, "end": v(-296.16, 138.08) * mm});
            skLineSegment(sketch, "E487", {"start": v(-296.16, 138.08) * mm, "end": v(-296.9, 137.28) * mm});
            skLineSegment(sketch, "E488", {"start": v(-296.9, 137.28) * mm, "end": v(-296.96, 137.23) * mm});
            skLineSegment(sketch, "E489", {"start": v(-296.96, 137.23) * mm, "end": v(-297.05, 137.12) * mm});
            skLineSegment(sketch, "E490", {"start": v(-297.05, 137.12) * mm, "end": v(-299.8, 134) * mm});
            skLineSegment(sketch, "E491", {"start": v(-299.8, 134) * mm, "end": v(-302.82, 130.57) * mm});
            skLineSegment(sketch, "E492", {"start": v(-302.82, 130.57) * mm, "end": v(-303.24, 130.12) * mm});
            skLineSegment(sketch, "E493", {"start": v(-303.24, 130.12) * mm, "end": v(-303.57, 129.73) * mm});
            skLineSegment(sketch, "E494", {"start": v(-303.57, 129.73) * mm, "end": v(-303.8, 129.44) * mm});
            skLineSegment(sketch, "E495", {"start": v(-303.8, 129.44) * mm, "end": v(-305.28, 127.58) * mm});
            skLineSegment(sketch, "E496", {"start": v(-305.28, 127.58) * mm, "end": v(-306.17, 126.46) * mm});
            skLineSegment(sketch, "E497", {"start": v(-306.17, 126.46) * mm, "end": v(-307.05, 125.26) * mm});
            skLineSegment(sketch, "E498", {"start": v(-307.05, 125.26) * mm, "end": v(-308.44, 123.37) * mm});
            skLineSegment(sketch, "E499", {"start": v(-308.44, 123.37) * mm, "end": v(-309.47, 121.95) * mm});
            skLineSegment(sketch, "E500", {"start": v(-309.47, 121.95) * mm, "end": v(-310.93, 119.94) * mm});
            skLineSegment(sketch, "E501", {"start": v(-310.93, 119.94) * mm, "end": v(-313.12, 116.8) * mm});
            skLineSegment(sketch, "E502", {"start": v(-313.12, 116.8) * mm, "end": v(-313.66, 116.02) * mm});
            skLineSegment(sketch, "E503", {"start": v(-313.66, 116.02) * mm, "end": v(-313.96, 115.53) * mm});
            skLineSegment(sketch, "E504", {"start": v(-313.96, 115.53) * mm, "end": v(-315.95, 112.29) * mm});
            skLineSegment(sketch, "E505", {"start": v(-315.95, 112.29) * mm, "end": v(-317.6, 109.48) * mm});
            skLineSegment(sketch, "E506", {"start": v(-317.6, 109.48) * mm, "end": v(-317.87, 109.03) * mm});
            skLineSegment(sketch, "E507", {"start": v(-317.87, 109.03) * mm, "end": v(-318.02, 108.73) * mm});
            skLineSegment(sketch, "E508", {"start": v(-318.02, 108.73) * mm, "end": v(-319.3, 106.4) * mm});
            skLineSegment(sketch, "E509", {"start": v(-319.3, 106.4) * mm, "end": v(-320.24, 104.75) * mm});
            skLineSegment(sketch, "E510", {"start": v(-320.24, 104.75) * mm, "end": v(-320.63, 104.06) * mm});
            skLineSegment(sketch, "E511", {"start": v(-320.63, 104.06) * mm, "end": v(-321.62, 102.24) * mm});
            skLineSegment(sketch, "E512", {"start": v(-321.62, 102.24) * mm, "end": v(-323.03, 99.6) * mm});
            skLineSegment(sketch, "E513", {"start": v(-323.03, 99.6) * mm, "end": v(-323.47, 98.71) * mm});
            skLineSegment(sketch, "E514", {"start": v(-323.47, 98.71) * mm, "end": v(-323.78, 98.1) * mm});
            skLineSegment(sketch, "E515", {"start": v(-323.78, 98.1) * mm, "end": v(-323.98, 97.7) * mm});
            skLineSegment(sketch, "E516", {"start": v(-323.98, 97.7) * mm, "end": v(-325.52, 94.3) * mm});
            skLineSegment(sketch, "E517", {"start": v(-325.52, 94.3) * mm, "end": v(-325.87, 93.48) * mm});
            skLineSegment(sketch, "E518", {"start": v(-325.87, 93.48) * mm, "end": v(-326.33, 92.45) * mm});
            skLineSegment(sketch, "E519", {"start": v(-326.33, 92.45) * mm, "end": v(-327.26, 90.3) * mm});
            skLineSegment(sketch, "E520", {"start": v(-327.26, 90.3) * mm, "end": v(-327.7, 89.25) * mm});
            skLineSegment(sketch, "E521", {"start": v(-327.7, 89.25) * mm, "end": v(-328.15, 88.13) * mm});
            skLineSegment(sketch, "E522", {"start": v(-328.15, 88.13) * mm, "end": v(-329.16, 85.49) * mm});
            skLineSegment(sketch, "E523", {"start": v(-329.16, 85.49) * mm, "end": v(-329.47, 84.67) * mm});
            skLineSegment(sketch, "E524", {"start": v(-329.47, 84.67) * mm, "end": v(-331.44, 79.2) * mm});
            skLineSegment(sketch, "E525", {"start": v(-331.44, 79.2) * mm, "end": v(-331.45, 79.17) * mm});
            skLineSegment(sketch, "E526", {"start": v(-331.45, 79.17) * mm, "end": v(-331.46, 79.16) * mm});
            skLineSegment(sketch, "E527", {"start": v(-331.46, 79.16) * mm, "end": v(-331.48, 79.1) * mm});
            skLineSegment(sketch, "E528", {"start": v(-331.48, 79.1) * mm, "end": v(-332.52, 75.95) * mm});
            skLineSegment(sketch, "E529", {"start": v(-332.52, 75.95) * mm, "end": v(-333.6, 72.07) * mm});
            skLineSegment(sketch, "E530", {"start": v(-333.6, 72.07) * mm, "end": v(-333.86, 71.11) * mm});
            skLineSegment(sketch, "E531", {"start": v(-333.86, 71.11) * mm, "end": v(-334.1, 70.22) * mm});
            skLineSegment(sketch, "E532", {"start": v(-334.1, 70.22) * mm, "end": v(-334.92, 67.13) * mm});
            skLineSegment(sketch, "E533", {"start": v(-334.92, 67.13) * mm, "end": v(-335.44, 64.95) * mm});
            skLineSegment(sketch, "E534", {"start": v(-335.44, 64.95) * mm, "end": v(-335.62, 64.11) * mm});
            skLineSegment(sketch, "E535", {"start": v(-335.62, 64.11) * mm, "end": v(-335.76, 63.51) * mm});
            skLineSegment(sketch, "E536", {"start": v(-335.76, 63.51) * mm, "end": v(-336.5, 59.88) * mm});
            skLineSegment(sketch, "E537", {"start": v(-336.5, 59.88) * mm, "end": v(-336.71, 58.45) * mm});
            skLineSegment(sketch, "E538", {"start": v(-336.71, 58.45) * mm, "end": v(-337.06, 56.22) * mm});
            skLineSegment(sketch, "E539", {"start": v(-337.06, 56.22) * mm, "end": v(-337.22, 55.2) * mm});
            skLineSegment(sketch, "E540", {"start": v(-337.22, 55.2) * mm, "end": v(-337.28, 54.78) * mm});
            skLineSegment(sketch, "E541", {"start": v(-337.28, 54.78) * mm, "end": v(-337.72, 52.05) * mm});
            skLineSegment(sketch, "E542", {"start": v(-337.72, 52.05) * mm, "end": v(-337.77, 51.76) * mm});
            skLineSegment(sketch, "E543", {"start": v(-337.77, 51.76) * mm, "end": v(-337.78, 51.72) * mm});
            skLineSegment(sketch, "E544", {"start": v(-337.78, 51.72) * mm, "end": v(-337.84, 51.19) * mm});
            skLineSegment(sketch, "E545", {"start": v(-337.84, 51.19) * mm, "end": v(-338.28, 47.58) * mm});
            skLineSegment(sketch, "E546", {"start": v(-338.28, 47.58) * mm, "end": v(-338.3, 47.38) * mm});
            skLineSegment(sketch, "E547", {"start": v(-338.3, 47.38) * mm, "end": v(-338.32, 47.23) * mm});
            skLineSegment(sketch, "E548", {"start": v(-338.32, 47.23) * mm, "end": v(-338.38, 46.46) * mm});
            skLineSegment(sketch, "E549", {"start": v(-338.38, 46.46) * mm, "end": v(-338.65, 42.8) * mm});
            skLineSegment(sketch, "E550", {"start": v(-338.65, 42.8) * mm, "end": v(-338.73, 41.68) * mm});
            skLineSegment(sketch, "E551", {"start": v(-338.73, 41.68) * mm, "end": v(-338.94, 38.25) * mm});
            skLineSegment(sketch, "E552", {"start": v(-338.94, 38.25) * mm, "end": v(-339.02, 36.07) * mm});
            skLineSegment(sketch, "E553", {"start": v(-339.02, 36.07) * mm, "end": v(-339.05, 34.23) * mm});
            skLineSegment(sketch, "E554", {"start": v(-339.05, 34.23) * mm, "end": v(-339.13, 31.14) * mm});
            skLineSegment(sketch, "E555", {"start": v(-339.13, 31.14) * mm, "end": v(-339.17, 29) * mm});
            skLineSegment(sketch, "E556", {"start": v(-339.17, 29) * mm, "end": v(-339.16, 26.99) * mm});
            skLineSegment(sketch, "E557", {"start": v(-339.16, 26.99) * mm, "end": v(-339.06, 22.17) * mm});
            skLineSegment(sketch, "E558", {"start": v(-339.06, 22.17) * mm, "end": v(-339.05, 21.97) * mm});
            skLineSegment(sketch, "E559", {"start": v(-339.05, 21.97) * mm, "end": v(-338.98, 18.69) * mm});
            skLineSegment(sketch, "E560", {"start": v(-338.98, 18.69) * mm, "end": v(-338.98, 18.55) * mm});
            skLineSegment(sketch, "E561", {"start": v(-338.98, 18.55) * mm, "end": v(-338.97, 18.41) * mm});
            skLineSegment(sketch, "E562", {"start": v(-338.97, 18.41) * mm, "end": v(-338.55, 14.3) * mm});
            skLineSegment(sketch, "E563", {"start": v(-338.55, 14.3) * mm, "end": v(-338.47, 13.43) * mm});
            skLineSegment(sketch, "E564", {"start": v(-338.47, 13.43) * mm, "end": v(-338.23, 10.74) * mm});
            skLineSegment(sketch, "E565", {"start": v(-338.23, 10.74) * mm, "end": v(-338.2, 10.44) * mm});
            skLineSegment(sketch, "E566", {"start": v(-338.2, 10.44) * mm, "end": v(-337.78, 7.15) * mm});
            skLineSegment(sketch, "E567", {"start": v(-337.78, 7.15) * mm, "end": v(-337.77, 7.1) * mm});
            skLineSegment(sketch, "E568", {"start": v(-337.77, 7.1) * mm, "end": v(-337.07, 2.53) * mm});
            skLineSegment(sketch, "E569", {"start": v(-337.07, 2.53) * mm, "end": v(-336.8, 0.73) * mm});
            skLineSegment(sketch, "E570", {"start": v(-336.8, 0.73) * mm, "end": v(-336.64, 0) * mm});
            skLineSegment(sketch, "E571.0", {"start": v(-312.36, 6.3) * mm, "end": v(-312.26, 5.65) * mm});
            skLineSegment(sketch, "E571.1", {"start": v(-313.03, 10.68) * mm, "end": v(-312.36, 6.3) * mm});
            skLineSegment(sketch, "E571.2", {"start": v(-313.36, 13.3) * mm, "end": v(-313.03, 10.68) * mm});
            skLineSegment(sketch, "E571.3", {"start": v(-313.57, 15.7) * mm, "end": v(-313.36, 13.3) * mm});
            skLineSegment(sketch, "E571.4", {"start": v(-313.67, 16.71) * mm, "end": v(-313.57, 15.7) * mm});
            skLineSegment(sketch, "E571.5", {"start": v(-314, 20.02) * mm, "end": v(-313.67, 16.71) * mm});
            skLineSegment(sketch, "E571.6", {"start": v(-314.06, 22.62) * mm, "end": v(-314, 20.02) * mm});
            skLineSegment(sketch, "E571.7", {"start": v(-314.06, 22.81) * mm, "end": v(-314.06, 22.62) * mm});
            skLineSegment(sketch, "E571.8", {"start": v(-314.16, 27.32) * mm, "end": v(-314.06, 22.81) * mm});
            skLineSegment(sketch, "E571.9", {"start": v(-314.17, 28.81) * mm, "end": v(-314.16, 27.32) * mm});
            skLineSegment(sketch, "E571.10", {"start": v(-314.13, 30.57) * mm, "end": v(-314.17, 28.81) * mm});
            skLineSegment(sketch, "E571.11", {"start": v(-314.05, 33.72) * mm, "end": v(-314.13, 30.57) * mm});
            skLineSegment(sketch, "E571.12", {"start": v(-314.03, 35.44) * mm, "end": v(-314.05, 33.72) * mm});
            skLineSegment(sketch, "E571.13", {"start": v(-313.97, 37.04) * mm, "end": v(-314.03, 35.44) * mm});
            skLineSegment(sketch, "E571.14", {"start": v(-313.78, 40.04) * mm, "end": v(-313.97, 37.04) * mm});
            skLineSegment(sketch, "E571.15", {"start": v(-313.72, 41.02) * mm, "end": v(-313.78, 40.04) * mm});
            skLineSegment(sketch, "E571.16", {"start": v(-313.44, 44.74) * mm, "end": v(-313.72, 41.02) * mm});
            skLineSegment(sketch, "E571.17", {"start": v(-313.02, 48.24) * mm, "end": v(-313.44, 44.74) * mm});
            skLineSegment(sketch, "E571.18", {"start": v(-312.57, 50.98) * mm, "end": v(-313.02, 48.24) * mm});
            skLineSegment(sketch, "E571.19", {"start": v(-312.5, 51.5) * mm, "end": v(-312.57, 50.98) * mm});
            skLineSegment(sketch, "E571.20", {"start": v(-312.36, 52.36) * mm, "end": v(-312.5, 51.5) * mm});
            skLineSegment(sketch, "E571.21", {"start": v(-312, 54.66) * mm, "end": v(-312.36, 52.36) * mm});
            skLineSegment(sketch, "E571.22", {"start": v(-311.87, 55.54) * mm, "end": v(-312, 54.66) * mm});
            skLineSegment(sketch, "E571.23", {"start": v(-311.32, 58.2) * mm, "end": v(-311.87, 55.54) * mm});
            skLineSegment(sketch, "E571.24", {"start": v(-311.2, 58.74) * mm, "end": v(-311.32, 58.2) * mm});
            skLineSegment(sketch, "E571.25", {"start": v(-311.05, 59.45) * mm, "end": v(-311.2, 58.74) * mm});
            skLineSegment(sketch, "E571.26", {"start": v(-310.67, 61.03) * mm, "end": v(-311.05, 59.45) * mm});
            skLineSegment(sketch, "E571.27", {"start": v(-309.96, 63.74) * mm, "end": v(-310.67, 61.03) * mm});
            skLineSegment(sketch, "E571.28", {"start": v(-309.75, 64.5) * mm, "end": v(-309.96, 63.74) * mm});
            skLineSegment(sketch, "E571.29", {"start": v(-309.5, 65.4) * mm, "end": v(-309.75, 64.5) * mm});
            skLineSegment(sketch, "E571.30", {"start": v(-308.6, 68.67) * mm, "end": v(-309.5, 65.4) * mm});
            skLineSegment(sketch, "E571.31", {"start": v(-307.82, 71) * mm, "end": v(-308.6, 68.67) * mm});
            skLineSegment(sketch, "E571.32", {"start": v(-305.99, 76.08) * mm, "end": v(-307.82, 71) * mm});
            skLineSegment(sketch, "E571.33", {"start": v(-305.77, 76.68) * mm, "end": v(-305.99, 76.08) * mm});
            skLineSegment(sketch, "E571.34", {"start": v(-165.34, 218.42) * mm, "end": v(-168.38, 215.37) * mm});
            skLineSegment(sketch, "E571.35", {"start": v(-165.1, 218.65) * mm, "end": v(-165.34, 218.42) * mm});
            skLineSegment(sketch, "E571.36", {"start": v(-163.47, 220.2) * mm, "end": v(-165.1, 218.65) * mm});
            skLineSegment(sketch, "E571.37", {"start": v(-161.5, 222.18) * mm, "end": v(-163.47, 220.2) * mm});
            skLineSegment(sketch, "E571.38", {"start": v(-161.04, 222.66) * mm, "end": v(-161.5, 222.18) * mm});
            skLineSegment(sketch, "E571.39", {"start": v(-157.84, 226.13) * mm, "end": v(-161.04, 222.66) * mm});
            skLineSegment(sketch, "E571.40", {"start": v(-156.57, 226.8) * mm, "end": v(-157.84, 226.13) * mm});
            skLineSegment(sketch, "E571.41", {"start": v(-152.7, 229.64) * mm, "end": v(-156.57, 226.8) * mm});
            skLineSegment(sketch, "E571.42", {"start": v(-151.44, 230.66) * mm, "end": v(-152.7, 229.64) * mm});
            skLineSegment(sketch, "E571.43", {"start": v(-150.68, 231.37) * mm, "end": v(-151.44, 230.66) * mm});
            skLineSegment(sketch, "E571.44", {"start": v(-148.34, 233.58) * mm, "end": v(-150.68, 231.37) * mm});
            skLineSegment(sketch, "E571.45", {"start": v(-147.23, 234.73) * mm, "end": v(-148.34, 233.58) * mm});
            skLineSegment(sketch, "E571.46", {"start": v(-145.77, 236.3) * mm, "end": v(-147.23, 234.73) * mm});
            skLineSegment(sketch, "E571.47", {"start": v(-145.22, 236.88) * mm, "end": v(-145.77, 236.3) * mm});
            skLineSegment(sketch, "E571.48", {"start": v(-144.62, 237.45) * mm, "end": v(-145.22, 236.88) * mm});
            skLineSegment(sketch, "E571.49", {"start": v(-144.11, 237.9) * mm, "end": v(-144.62, 237.45) * mm});
            skLineSegment(sketch, "E571.50", {"start": v(-143.49, 238.45) * mm, "end": v(-144.11, 237.9) * mm});
            skLineSegment(sketch, "E571.51", {"start": v(-141.78, 239.94) * mm, "end": v(-143.49, 238.45) * mm});
            skLineSegment(sketch, "E571.52", {"start": v(-140.34, 241.4) * mm, "end": v(-141.78, 239.94) * mm});
            skLineSegment(sketch, "E571.53", {"start": v(-139.35, 242.42) * mm, "end": v(-140.34, 241.4) * mm});
            skLineSegment(sketch, "E571.54", {"start": v(-138.98, 242.77) * mm, "end": v(-139.35, 242.42) * mm});
            skLineSegment(sketch, "E571.55", {"start": v(-136.9, 244.69) * mm, "end": v(-138.98, 242.77) * mm});
            skLineSegment(sketch, "E571.56", {"start": v(-135.7, 245.96) * mm, "end": v(-136.9, 244.69) * mm});
            skLineSegment(sketch, "E571.57", {"start": v(-134.62, 247.06) * mm, "end": v(-135.7, 245.96) * mm});
            skLineSegment(sketch, "E571.58", {"start": v(-133.96, 247.71) * mm, "end": v(-134.62, 247.06) * mm});
            skLineSegment(sketch, "E571.59", {"start": v(-131.23, 250.4) * mm, "end": v(-133.96, 247.71) * mm});
            skLineSegment(sketch, "E571.60", {"start": v(-130.98, 250.65) * mm, "end": v(-131.23, 250.4) * mm});
            skLineSegment(sketch, "E571.61", {"start": v(-128.32, 253.23) * mm, "end": v(-130.98, 250.65) * mm});
            skLineSegment(sketch, "E571.62", {"start": v(-127.88, 253.67) * mm, "end": v(-128.32, 253.23) * mm});
            skLineSegment(sketch, "E571.63", {"start": v(-127.39, 254.11) * mm, "end": v(-127.88, 253.67) * mm});
            skLineSegment(sketch, "E571.64", {"start": v(-126.62, 254.8) * mm, "end": v(-127.39, 254.11) * mm});
            skLineSegment(sketch, "E571.65", {"start": v(-125.63, 255.6) * mm, "end": v(-126.62, 254.8) * mm});
            skLineSegment(sketch, "E571.66", {"start": v(-125.05, 256.03) * mm, "end": v(-125.63, 255.6) * mm});
            skLineSegment(sketch, "E571.67", {"start": v(-123.5, 257.17) * mm, "end": v(-125.05, 256.03) * mm});
            skLineSegment(sketch, "E571.68", {"start": v(-122.94, 257.56) * mm, "end": v(-123.5, 257.17) * mm});
            skLineSegment(sketch, "E571.69", {"start": v(-121.84, 258.32) * mm, "end": v(-122.94, 257.56) * mm});
            skLineSegment(sketch, "E571.70", {"start": v(-119.9, 259.47) * mm, "end": v(-121.84, 258.32) * mm});
            skLineSegment(sketch, "E571.71", {"start": v(-119.52, 259.7) * mm, "end": v(-119.9, 259.47) * mm});
            skLineSegment(sketch, "E571.72", {"start": v(-118.11, 260.49) * mm, "end": v(-119.52, 259.7) * mm});
            skLineSegment(sketch, "E571.73", {"start": v(-115.67, 261.73) * mm, "end": v(-118.11, 260.49) * mm});
            skLineSegment(sketch, "E571.74", {"start": v(-115.24, 261.95) * mm, "end": v(-115.67, 261.73) * mm});
            skLineSegment(sketch, "E571.75", {"start": v(-113.96, 262.52) * mm, "end": v(-115.24, 261.95) * mm});
            skLineSegment(sketch, "E571.76", {"start": v(-112.72, 263.03) * mm, "end": v(-113.96, 262.52) * mm});
            skLineSegment(sketch, "E571.77", {"start": v(-111.49, 263.53) * mm, "end": v(-112.72, 263.03) * mm});
            skLineSegment(sketch, "E571.78", {"start": v(-110.44, 263.89) * mm, "end": v(-111.49, 263.53) * mm});
            skLineSegment(sketch, "E571.79", {"start": v(-109.51, 264.18) * mm, "end": v(-110.44, 263.89) * mm});
            skLineSegment(sketch, "E571.80", {"start": v(-106.74, 265) * mm, "end": v(-109.51, 264.18) * mm});
            skLineSegment(sketch, "E571.81", {"start": v(-106.24, 265.15) * mm, "end": v(-106.74, 265) * mm});
            skLineSegment(sketch, "E571.82", {"start": v(-102.94, 266.03) * mm, "end": v(-106.24, 265.15) * mm});
            skLineSegment(sketch, "E571.83", {"start": v(-101.63, 266.4) * mm, "end": v(-102.94, 266.03) * mm});
            skLineSegment(sketch, "E571.84", {"start": v(-41.08, 276.69) * mm, "end": v(-45.18, 276.36) * mm});
            skLineSegment(sketch, "E571.85", {"start": v(-40.91, 276.7) * mm, "end": v(-41.08, 276.69) * mm});
            skLineSegment(sketch, "E571.86", {"start": v(-38.8, 276.87) * mm, "end": v(-40.91, 276.7) * mm});
            skLineSegment(sketch, "E571.87", {"start": v(-36.73, 277.03) * mm, "end": v(-38.8, 276.87) * mm});
            skLineSegment(sketch, "E571.88", {"start": v(-34.6, 277.17) * mm, "end": v(-36.73, 277.03) * mm});
            skLineSegment(sketch, "E571.89", {"start": v(-31.71, 277.37) * mm, "end": v(-34.6, 277.17) * mm});
            skLineSegment(sketch, "E571.90", {"start": v(-30.98, 277.42) * mm, "end": v(-31.71, 277.37) * mm});
            skLineSegment(sketch, "E571.91", {"start": v(-30.17, 277.45) * mm, "end": v(-30.98, 277.42) * mm});
            skLineSegment(sketch, "E571.92", {"start": v(-25.07, 277.65) * mm, "end": v(-30.17, 277.45) * mm});
            skLineSegment(sketch, "E571.93", {"start": v(-21.66, 277.8) * mm, "end": v(-25.07, 277.65) * mm});
            skLineSegment(sketch, "E571.94", {"start": v(-19.34, 277.89) * mm, "end": v(-21.66, 277.8) * mm});
            skLineSegment(sketch, "E571.95", {"start": v(-16.39, 277.91) * mm, "end": v(-19.34, 277.89) * mm});
            skLineSegment(sketch, "E571.96", {"start": v(-4.14, 277.7) * mm, "end": v(-5.03, 277.74) * mm});
            skLineSegment(sketch, "E571.97", {"start": v(-1.3, 277.59) * mm, "end": v(-4.14, 277.7) * mm});
            skLineSegment(sketch, "E571.98", {"start": v(2.14, 277.85) * mm, "end": v(-1.3, 277.59) * mm});
            skLineSegment(sketch, "E571.99", {"start": v(5, 278.43) * mm, "end": v(2.14, 277.85) * mm});
            skLineSegment(sketch, "E571.100", {"start": v(-5.03, 277.74) * mm, "end": v(-5.42, 277.75) * mm});
            skLineSegment(sketch, "E571.101", {"start": v(-5.42, 277.75) * mm, "end": v(-7.36, 277.8) * mm});
            skLineSegment(sketch, "E571.102", {"start": v(-7.36, 277.8) * mm, "end": v(-8.9, 277.77) * mm});
            skLineSegment(sketch, "E571.103", {"start": v(-8.9, 277.77) * mm, "end": v(-11.77, 277.77) * mm});
            skLineSegment(sketch, "E571.104", {"start": v(-11.77, 277.77) * mm, "end": v(-15.35, 277.88) * mm});
            skLineSegment(sketch, "E571.105", {"start": v(-15.35, 277.88) * mm, "end": v(-16.39, 277.91) * mm});
            skLineSegment(sketch, "E571.106", {"start": v(-45.18, 276.36) * mm, "end": v(-46.14, 276.28) * mm});
            skLineSegment(sketch, "E571.107", {"start": v(-46.14, 276.28) * mm, "end": v(-49.45, 275.97) * mm});
            skLineSegment(sketch, "E571.108", {"start": v(-49.45, 275.97) * mm, "end": v(-49.87, 275.93) * mm});
            skLineSegment(sketch, "E571.109", {"start": v(-49.87, 275.93) * mm, "end": v(-51.53, 275.74) * mm});
            skLineSegment(sketch, "E571.110", {"start": v(-51.53, 275.74) * mm, "end": v(-54.54, 275.34) * mm});
            skLineSegment(sketch, "E571.111", {"start": v(-54.54, 275.34) * mm, "end": v(-55.38, 275.23) * mm});
            skLineSegment(sketch, "E571.112", {"start": v(-55.38, 275.23) * mm, "end": v(-58.87, 274.74) * mm});
            skLineSegment(sketch, "E571.113", {"start": v(-58.87, 274.74) * mm, "end": v(-61.95, 274.34) * mm});
            skLineSegment(sketch, "E571.114", {"start": v(-61.95, 274.34) * mm, "end": v(-66.11, 273.74) * mm});
            skLineSegment(sketch, "E571.115", {"start": v(-66.11, 273.74) * mm, "end": v(-68.03, 273.45) * mm});
            skLineSegment(sketch, "E571.116", {"start": v(-68.03, 273.45) * mm, "end": v(-69.54, 273.2) * mm});
            skLineSegment(sketch, "E571.117", {"start": v(-69.54, 273.2) * mm, "end": v(-72.72, 272.64) * mm});
            skLineSegment(sketch, "E571.118", {"start": v(-72.72, 272.64) * mm, "end": v(-74.85, 272.28) * mm});
            skLineSegment(sketch, "E571.119", {"start": v(-74.85, 272.28) * mm, "end": v(-78.67, 271.58) * mm});
            skLineSegment(sketch, "E571.120", {"start": v(-78.67, 271.58) * mm, "end": v(-81.05, 271.14) * mm});
            skLineSegment(sketch, "E571.121", {"start": v(-81.05, 271.14) * mm, "end": v(-81.77, 270.99) * mm});
            skLineSegment(sketch, "E571.122", {"start": v(-81.77, 270.99) * mm, "end": v(-85.04, 270.27) * mm});
            skLineSegment(sketch, "E571.123", {"start": v(-85.04, 270.27) * mm, "end": v(-87.6, 269.76) * mm});
            skLineSegment(sketch, "E571.124", {"start": v(-87.6, 269.76) * mm, "end": v(-90.78, 269.05) * mm});
            skLineSegment(sketch, "E571.125", {"start": v(-90.78, 269.05) * mm, "end": v(-91.67, 268.85) * mm});
            skLineSegment(sketch, "E571.126", {"start": v(-91.67, 268.85) * mm, "end": v(-92.17, 268.73) * mm});
            skLineSegment(sketch, "E571.127", {"start": v(-92.17, 268.73) * mm, "end": v(-98.07, 267.27) * mm});
            skLineSegment(sketch, "E571.128", {"start": v(-98.07, 267.27) * mm, "end": v(-98.13, 267.25) * mm});
            skLineSegment(sketch, "E571.129", {"start": v(-98.13, 267.25) * mm, "end": v(-101.63, 266.4) * mm});
            skLineSegment(sketch, "E571.130", {"start": v(-168.38, 215.37) * mm, "end": v(-171.23, 212.8) * mm});
            skLineSegment(sketch, "E571.131", {"start": v(-171.23, 212.8) * mm, "end": v(-171.63, 212.45) * mm});
            skLineSegment(sketch, "E571.132", {"start": v(-171.63, 212.45) * mm, "end": v(-171.99, 212.1) * mm});
            skLineSegment(sketch, "E571.133", {"start": v(-171.99, 212.1) * mm, "end": v(-172.87, 211.22) * mm});
            skLineSegment(sketch, "E571.134", {"start": v(-172.87, 211.22) * mm, "end": v(-173.57, 210.51) * mm});
            skLineSegment(sketch, "E571.135", {"start": v(-173.57, 210.51) * mm, "end": v(-174.77, 209.28) * mm});
            skLineSegment(sketch, "E571.136", {"start": v(-174.77, 209.28) * mm, "end": v(-175.5, 208.57) * mm});
            skLineSegment(sketch, "E571.137", {"start": v(-175.5, 208.57) * mm, "end": v(-176.53, 207.54) * mm});
            skLineSegment(sketch, "E571.138", {"start": v(-176.53, 207.54) * mm, "end": v(-178.04, 206.08) * mm});
            skLineSegment(sketch, "E571.139", {"start": v(-178.04, 206.08) * mm, "end": v(-178.83, 205.33) * mm});
            skLineSegment(sketch, "E571.140", {"start": v(-178.83, 205.33) * mm, "end": v(-179.93, 204.3) * mm});
            skLineSegment(sketch, "E571.141", {"start": v(-179.93, 204.3) * mm, "end": v(-181.27, 202.95) * mm});
            skLineSegment(sketch, "E571.142", {"start": v(-181.27, 202.95) * mm, "end": v(-183.07, 201.23) * mm});
            skLineSegment(sketch, "E571.143", {"start": v(-183.07, 201.23) * mm, "end": v(-184.78, 199.72) * mm});
            skLineSegment(sketch, "E571.144", {"start": v(-184.78, 199.72) * mm, "end": v(-185.69, 198.88) * mm});
            skLineSegment(sketch, "E571.145", {"start": v(-185.69, 198.88) * mm, "end": v(-186.3, 198.28) * mm});
            skLineSegment(sketch, "E571.146", {"start": v(-186.3, 198.28) * mm, "end": v(-187.73, 196.87) * mm});
            skLineSegment(sketch, "E571.147", {"start": v(-187.73, 196.87) * mm, "end": v(-188, 196.62) * mm});
            skLineSegment(sketch, "E571.148", {"start": v(-188, 196.62) * mm, "end": v(-188.5, 196.11) * mm});
            skLineSegment(sketch, "E571.149", {"start": v(-188.5, 196.11) * mm, "end": v(-189.96, 194.74) * mm});
            skLineSegment(sketch, "E571.150", {"start": v(-189.96, 194.74) * mm, "end": v(-190.45, 194.3) * mm});
            skLineSegment(sketch, "E571.151", {"start": v(-190.45, 194.3) * mm, "end": v(-192.16, 192.63) * mm});
            skLineSegment(sketch, "E571.152", {"start": v(-192.16, 192.63) * mm, "end": v(-192.48, 192.32) * mm});
            skLineSegment(sketch, "E571.153", {"start": v(-192.48, 192.32) * mm, "end": v(-193.27, 191.57) * mm});
            skLineSegment(sketch, "E571.154", {"start": v(-193.27, 191.57) * mm, "end": v(-193.76, 191.12) * mm});
            skLineSegment(sketch, "E571.155", {"start": v(-193.76, 191.12) * mm, "end": v(-195.39, 189.31) * mm});
            skLineSegment(sketch, "E571.156", {"start": v(-195.39, 189.31) * mm, "end": v(-196.5, 188.25) * mm});
            skLineSegment(sketch, "E571.157", {"start": v(-196.5, 188.25) * mm, "end": v(-198.15, 186.6) * mm});
            skLineSegment(sketch, "E571.158", {"start": v(-198.15, 186.6) * mm, "end": v(-198.72, 186.08) * mm});
            skLineSegment(sketch, "E571.159", {"start": v(-198.72, 186.08) * mm, "end": v(-200.5, 184.49) * mm});
            skLineSegment(sketch, "E571.160", {"start": v(-200.5, 184.49) * mm, "end": v(-200.9, 184.06) * mm});
            skLineSegment(sketch, "E571.161", {"start": v(-200.9, 184.06) * mm, "end": v(-202.66, 182.37) * mm});
            skLineSegment(sketch, "E571.162", {"start": v(-202.66, 182.37) * mm, "end": v(-203.59, 181.46) * mm});
            skLineSegment(sketch, "E571.163", {"start": v(-203.59, 181.46) * mm, "end": v(-204.45, 180.59) * mm});
            skLineSegment(sketch, "E571.164", {"start": v(-204.45, 180.59) * mm, "end": v(-206.8, 178.28) * mm});
            skLineSegment(sketch, "E571.165", {"start": v(-206.8, 178.28) * mm, "end": v(-207.35, 177.75) * mm});
            skLineSegment(sketch, "E571.166", {"start": v(-207.35, 177.75) * mm, "end": v(-209.42, 175.78) * mm});
            skLineSegment(sketch, "E571.167", {"start": v(-209.42, 175.78) * mm, "end": v(-210.06, 175.13) * mm});
            skLineSegment(sketch, "E571.168", {"start": v(-210.06, 175.13) * mm, "end": v(-211.66, 173.56) * mm});
            skLineSegment(sketch, "E571.169", {"start": v(-211.66, 173.56) * mm, "end": v(-212.71, 172.59) * mm});
            skLineSegment(sketch, "E571.170", {"start": v(-212.71, 172.59) * mm, "end": v(-214.4, 171.09) * mm});
            skLineSegment(sketch, "E571.171", {"start": v(-214.4, 171.09) * mm, "end": v(-214.74, 170.77) * mm});
            skLineSegment(sketch, "E571.172", {"start": v(-214.74, 170.77) * mm, "end": v(-215.71, 169.83) * mm});
            skLineSegment(sketch, "E571.173", {"start": v(-215.71, 169.83) * mm, "end": v(-216.85, 168.74) * mm});
            skLineSegment(sketch, "E571.174", {"start": v(-216.85, 168.74) * mm, "end": v(-218.9, 166.61) * mm});
            skLineSegment(sketch, "E571.175", {"start": v(-218.9, 166.61) * mm, "end": v(-221.1, 164.65) * mm});
            skLineSegment(sketch, "E571.176", {"start": v(-221.1, 164.65) * mm, "end": v(-222.46, 163.45) * mm});
            skLineSegment(sketch, "E571.177", {"start": v(-222.46, 163.45) * mm, "end": v(-223.2, 162.79) * mm});
            skLineSegment(sketch, "E571.178", {"start": v(-223.2, 162.79) * mm, "end": v(-225.25, 161.13) * mm});
            skLineSegment(sketch, "E571.179", {"start": v(-225.25, 161.13) * mm, "end": v(-226.54, 160.15) * mm});
            skLineSegment(sketch, "E571.180", {"start": v(-226.54, 160.15) * mm, "end": v(-229.4, 157.81) * mm});
            skLineSegment(sketch, "E571.181", {"start": v(-229.4, 157.81) * mm, "end": v(-230.96, 156.66) * mm});
            skLineSegment(sketch, "E571.182", {"start": v(-230.96, 156.66) * mm, "end": v(-234.63, 154.12) * mm});
            skLineSegment(sketch, "E571.183", {"start": v(-234.63, 154.12) * mm, "end": v(-236.61, 152.76) * mm});
            skLineSegment(sketch, "E571.184", {"start": v(-236.61, 152.76) * mm, "end": v(-238.2, 151.67) * mm});
            skLineSegment(sketch, "E571.185", {"start": v(-238.2, 151.67) * mm, "end": v(-238.73, 151.31) * mm});
            skLineSegment(sketch, "E571.186", {"start": v(-238.73, 151.31) * mm, "end": v(-241.35, 149.6) * mm});
            skLineSegment(sketch, "E571.187", {"start": v(-241.35, 149.6) * mm, "end": v(-242.05, 149.12) * mm});
            skLineSegment(sketch, "E571.188", {"start": v(-242.05, 149.12) * mm, "end": v(-244.9, 147.14) * mm});
            skLineSegment(sketch, "E571.189", {"start": v(-244.9, 147.14) * mm, "end": v(-246.34, 146.17) * mm});
            skLineSegment(sketch, "E571.190", {"start": v(-246.34, 146.17) * mm, "end": v(-249.97, 143.8) * mm});
            skLineSegment(sketch, "E571.191", {"start": v(-249.97, 143.8) * mm, "end": v(-251.92, 142.5) * mm});
            skLineSegment(sketch, "E571.192", {"start": v(-251.92, 142.5) * mm, "end": v(-254.86, 140.48) * mm});
            skLineSegment(sketch, "E571.193", {"start": v(-254.86, 140.48) * mm, "end": v(-256.8, 139.21) * mm});
            skLineSegment(sketch, "E571.194", {"start": v(-256.8, 139.21) * mm, "end": v(-258.38, 138.14) * mm});
            skLineSegment(sketch, "E571.195", {"start": v(-258.38, 138.14) * mm, "end": v(-263.36, 134.37) * mm});
            skLineSegment(sketch, "E571.196", {"start": v(-263.36, 134.37) * mm, "end": v(-263.56, 134.22) * mm});
            skLineSegment(sketch, "E571.197", {"start": v(-263.56, 134.22) * mm, "end": v(-264.01, 133.86) * mm});
            skLineSegment(sketch, "E571.198", {"start": v(-264.01, 133.86) * mm, "end": v(-266.29, 132) * mm});
            skLineSegment(sketch, "E571.199", {"start": v(-266.29, 132) * mm, "end": v(-268.3, 130.27) * mm});
            skLineSegment(sketch, "E571.200", {"start": v(-268.3, 130.27) * mm, "end": v(-268.45, 130.12) * mm});
            skLineSegment(sketch, "E571.201", {"start": v(-268.45, 130.12) * mm, "end": v(-272.38, 126.53) * mm});
            skLineSegment(sketch, "E571.202", {"start": v(-272.38, 126.53) * mm, "end": v(-273.91, 125.26) * mm});
            skLineSegment(sketch, "E571.203", {"start": v(-273.91, 125.26) * mm, "end": v(-274.69, 124.5) * mm});
            skLineSegment(sketch, "E571.204", {"start": v(-274.69, 124.5) * mm, "end": v(-275.65, 123.4) * mm});
            skLineSegment(sketch, "E571.205", {"start": v(-275.65, 123.4) * mm, "end": v(-277.95, 120.94) * mm});
            skLineSegment(sketch, "E571.206", {"start": v(-277.95, 120.94) * mm, "end": v(-278.47, 120.4) * mm});
            skLineSegment(sketch, "E571.207", {"start": v(-278.47, 120.4) * mm, "end": v(-281.04, 117.48) * mm});
            skLineSegment(sketch, "E571.208", {"start": v(-281.04, 117.48) * mm, "end": v(-284.5, 113.55) * mm});
            skLineSegment(sketch, "E571.209", {"start": v(-284.5, 113.55) * mm, "end": v(-285.72, 112) * mm});
            skLineSegment(sketch, "E571.210", {"start": v(-285.72, 112) * mm, "end": v(-286.34, 111.23) * mm});
            skLineSegment(sketch, "E571.211", {"start": v(-286.34, 111.23) * mm, "end": v(-286.92, 110.44) * mm});
            skLineSegment(sketch, "E571.212", {"start": v(-286.92, 110.44) * mm, "end": v(-288.24, 108.65) * mm});
            skLineSegment(sketch, "E571.213", {"start": v(-288.24, 108.65) * mm, "end": v(-289.23, 107.28) * mm});
            skLineSegment(sketch, "E571.214", {"start": v(-289.23, 107.28) * mm, "end": v(-290.56, 105.45) * mm});
            skLineSegment(sketch, "E571.215", {"start": v(-290.56, 105.45) * mm, "end": v(-292.73, 102.32) * mm});
            skLineSegment(sketch, "E571.216", {"start": v(-292.73, 102.32) * mm, "end": v(-294.52, 99.41) * mm});
            skLineSegment(sketch, "E571.217", {"start": v(-294.52, 99.41) * mm, "end": v(-296, 96.9) * mm});
            skLineSegment(sketch, "E571.218", {"start": v(-296, 96.9) * mm, "end": v(-297.48, 94.2) * mm});
            skLineSegment(sketch, "E571.219", {"start": v(-297.48, 94.2) * mm, "end": v(-298.47, 92.47) * mm});
            skLineSegment(sketch, "E571.220", {"start": v(-298.47, 92.47) * mm, "end": v(-298.72, 92.02) * mm});
            skLineSegment(sketch, "E571.221", {"start": v(-298.72, 92.02) * mm, "end": v(-299.61, 90.37) * mm});
            skLineSegment(sketch, "E571.222", {"start": v(-299.61, 90.37) * mm, "end": v(-300.81, 88.13) * mm});
            skLineSegment(sketch, "E571.223", {"start": v(-300.81, 88.13) * mm, "end": v(-301.15, 87.44) * mm});
            skLineSegment(sketch, "E571.224", {"start": v(-301.15, 87.44) * mm, "end": v(-301.43, 86.9) * mm});
            skLineSegment(sketch, "E571.225", {"start": v(-301.43, 86.9) * mm, "end": v(-302.64, 84.24) * mm});
            skLineSegment(sketch, "E571.226", {"start": v(-302.64, 84.24) * mm, "end": v(-302.92, 83.57) * mm});
            skLineSegment(sketch, "E571.227", {"start": v(-302.92, 83.57) * mm, "end": v(-303.41, 82.45) * mm});
            skLineSegment(sketch, "E571.228", {"start": v(-303.41, 82.45) * mm, "end": v(-304.29, 80.44) * mm});
            skLineSegment(sketch, "E571.229", {"start": v(-304.29, 80.44) * mm, "end": v(-304.56, 79.8) * mm});
            skLineSegment(sketch, "E571.230", {"start": v(-304.56, 79.8) * mm, "end": v(-304.85, 79.06) * mm});
            skLineSegment(sketch, "E571.231", {"start": v(-304.85, 79.06) * mm, "end": v(-305.77, 76.68) * mm});
            skLineSegment(sketch, "E572.0", {"start": v(-331.88, 1.64) * mm, "end": v(-331.75, 1.06) * mm});
            skLineSegment(sketch, "E572.1", {"start": v(-332.13, 3.28) * mm, "end": v(-331.88, 1.64) * mm});
            skLineSegment(sketch, "E572.2", {"start": v(-332.84, 7.9) * mm, "end": v(-332.13, 3.28) * mm});
            skLineSegment(sketch, "E572.3", {"start": v(-333.23, 11.03) * mm, "end": v(-332.84, 7.9) * mm});
            skLineSegment(sketch, "E572.4", {"start": v(-333.26, 11.24) * mm, "end": v(-333.23, 11.03) * mm});
            skLineSegment(sketch, "E572.5", {"start": v(-333.5, 13.88) * mm, "end": v(-333.26, 11.24) * mm});
            skLineSegment(sketch, "E572.6", {"start": v(-333.58, 14.78) * mm, "end": v(-333.5, 13.88) * mm});
            skLineSegment(sketch, "E572.7", {"start": v(-333.98, 18.8) * mm, "end": v(-333.58, 14.78) * mm});
            skLineSegment(sketch, "E572.8", {"start": v(-334.05, 22.1) * mm, "end": v(-333.98, 18.8) * mm});
            skLineSegment(sketch, "E572.9", {"start": v(-334.06, 22.3) * mm, "end": v(-334.05, 22.1) * mm});
            skLineSegment(sketch, "E572.10", {"start": v(-334.16, 27.05) * mm, "end": v(-334.06, 22.3) * mm});
            skLineSegment(sketch, "E572.11", {"start": v(-334.17, 28.97) * mm, "end": v(-334.16, 27.05) * mm});
            skLineSegment(sketch, "E572.12", {"start": v(-334.13, 31.03) * mm, "end": v(-334.17, 28.97) * mm});
            skLineSegment(sketch, "E572.13", {"start": v(-334.05, 34.12) * mm, "end": v(-334.13, 31.03) * mm});
            skLineSegment(sketch, "E572.14", {"start": v(-334.02, 35.95) * mm, "end": v(-334.05, 34.12) * mm});
            skLineSegment(sketch, "E572.15", {"start": v(-333.95, 38.01) * mm, "end": v(-334.02, 35.95) * mm});
            skLineSegment(sketch, "E572.16", {"start": v(-333.74, 41.35) * mm, "end": v(-333.95, 38.01) * mm});
            skLineSegment(sketch, "E572.17", {"start": v(-333.67, 42.45) * mm, "end": v(-333.74, 41.35) * mm});
            skLineSegment(sketch, "E572.18", {"start": v(-333.4, 46.07) * mm, "end": v(-333.67, 42.45) * mm});
            skLineSegment(sketch, "E572.19", {"start": v(-333.34, 46.77) * mm, "end": v(-333.4, 46.07) * mm});
            skLineSegment(sketch, "E572.20", {"start": v(-333.33, 46.82) * mm, "end": v(-333.34, 46.77) * mm});
            skLineSegment(sketch, "E572.21", {"start": v(-333.31, 46.99) * mm, "end": v(-333.33, 46.82) * mm});
            skLineSegment(sketch, "E572.22", {"start": v(-332.88, 50.58) * mm, "end": v(-333.31, 46.99) * mm});
            skLineSegment(sketch, "E572.23", {"start": v(-332.82, 51.04) * mm, "end": v(-332.88, 50.58) * mm});
            skLineSegment(sketch, "E572.24", {"start": v(-332.79, 51.26) * mm, "end": v(-332.82, 51.04) * mm});
            skLineSegment(sketch, "E572.25", {"start": v(-332.34, 54.02) * mm, "end": v(-332.79, 51.26) * mm});
            skLineSegment(sketch, "E572.26", {"start": v(-332.28, 54.47) * mm, "end": v(-332.34, 54.02) * mm});
            skLineSegment(sketch, "E572.27", {"start": v(-332.12, 55.45) * mm, "end": v(-332.28, 54.47) * mm});
            skLineSegment(sketch, "E572.28", {"start": v(-331.77, 57.7) * mm, "end": v(-332.12, 55.45) * mm});
            skLineSegment(sketch, "E572.29", {"start": v(-331.57, 59.01) * mm, "end": v(-331.77, 57.7) * mm});
            skLineSegment(sketch, "E572.30", {"start": v(-330.87, 62.45) * mm, "end": v(-331.57, 59.01) * mm});
            skLineSegment(sketch, "E572.31", {"start": v(-330.73, 63.04) * mm, "end": v(-330.87, 62.45) * mm});
            skLineSegment(sketch, "E572.32", {"start": v(-330.57, 63.85) * mm, "end": v(-330.73, 63.04) * mm});
            skLineSegment(sketch, "E572.33", {"start": v(-330.07, 65.91) * mm, "end": v(-330.57, 63.85) * mm});
            skLineSegment(sketch, "E572.34", {"start": v(-329.28, 68.93) * mm, "end": v(-330.07, 65.91) * mm});
            skLineSegment(sketch, "E572.35", {"start": v(-329.04, 69.8) * mm, "end": v(-329.28, 68.93) * mm});
            skLineSegment(sketch, "E572.36", {"start": v(-328.78, 70.74) * mm, "end": v(-329.04, 69.8) * mm});
            skLineSegment(sketch, "E572.37", {"start": v(-327.73, 74.5) * mm, "end": v(-328.78, 70.74) * mm});
            skLineSegment(sketch, "E572.38", {"start": v(-326.73, 77.53) * mm, "end": v(-327.73, 74.5) * mm});
            skLineSegment(sketch, "E572.39", {"start": v(-324.77, 82.95) * mm, "end": v(-326.73, 77.53) * mm});
            skLineSegment(sketch, "E572.40", {"start": v(-324.48, 83.72) * mm, "end": v(-324.77, 82.95) * mm});
            skLineSegment(sketch, "E572.41", {"start": v(-323.49, 86.32) * mm, "end": v(-324.48, 83.72) * mm});
            skLineSegment(sketch, "E572.42", {"start": v(-323.08, 87.36) * mm, "end": v(-323.49, 86.32) * mm});
            skLineSegment(sketch, "E572.43", {"start": v(-322.67, 88.33) * mm, "end": v(-323.08, 87.36) * mm});
            skLineSegment(sketch, "E572.44", {"start": v(-321.74, 90.45) * mm, "end": v(-322.67, 88.33) * mm});
            skLineSegment(sketch, "E572.45", {"start": v(-321.28, 91.5) * mm, "end": v(-321.74, 90.45) * mm});
            skLineSegment(sketch, "E572.46", {"start": v(-320.95, 92.3) * mm, "end": v(-321.28, 91.5) * mm});
            skLineSegment(sketch, "E572.47", {"start": v(-319.47, 95.55) * mm, "end": v(-320.95, 92.3) * mm});
            skLineSegment(sketch, "E572.48", {"start": v(-319.32, 95.84) * mm, "end": v(-319.47, 95.55) * mm});
            skLineSegment(sketch, "E572.49", {"start": v(-319, 96.46) * mm, "end": v(-319.32, 95.84) * mm});
            skLineSegment(sketch, "E572.50", {"start": v(-318.59, 97.3) * mm, "end": v(-319, 96.46) * mm});
            skLineSegment(sketch, "E572.51", {"start": v(-317.22, 99.86) * mm, "end": v(-318.59, 97.3) * mm});
            skLineSegment(sketch, "E572.52", {"start": v(-316.24, 101.65) * mm, "end": v(-317.22, 99.86) * mm});
            skLineSegment(sketch, "E572.53", {"start": v(-315.89, 102.3) * mm, "end": v(-316.24, 101.65) * mm});
            skLineSegment(sketch, "E572.54", {"start": v(-314.93, 103.97) * mm, "end": v(-315.89, 102.3) * mm});
            skLineSegment(sketch, "E572.55", {"start": v(-313.61, 106.38) * mm, "end": v(-314.93, 103.97) * mm});
            skLineSegment(sketch, "E572.56", {"start": v(-313.49, 106.61) * mm, "end": v(-313.61, 106.38) * mm});
            skLineSegment(sketch, "E572.57", {"start": v(-313.3, 106.94) * mm, "end": v(-313.49, 106.61) * mm});
            skLineSegment(sketch, "E572.58", {"start": v(-311.67, 109.71) * mm, "end": v(-313.3, 106.94) * mm});
            skLineSegment(sketch, "E572.59", {"start": v(-309.7, 112.91) * mm, "end": v(-311.67, 109.71) * mm});
            skLineSegment(sketch, "E572.60", {"start": v(-309.47, 113.28) * mm, "end": v(-309.7, 112.91) * mm});
            skLineSegment(sketch, "E572.61", {"start": v(-309.01, 113.95) * mm, "end": v(-309.47, 113.28) * mm});
            skLineSegment(sketch, "E572.62", {"start": v(-306.86, 117.04) * mm, "end": v(-309.01, 113.95) * mm});
            skLineSegment(sketch, "E572.63", {"start": v(-305.42, 119.02) * mm, "end": v(-306.86, 117.04) * mm});
            skLineSegment(sketch, "E572.64", {"start": v(-304.4, 120.43) * mm, "end": v(-305.42, 119.02) * mm});
            skLineSegment(sketch, "E572.65", {"start": v(-303.03, 122.3) * mm, "end": v(-304.4, 120.43) * mm});
            skLineSegment(sketch, "E572.66", {"start": v(-302.2, 123.42) * mm, "end": v(-303.03, 122.3) * mm});
            skLineSegment(sketch, "E572.67", {"start": v(-301.37, 124.46) * mm, "end": v(-302.2, 123.42) * mm});
            skLineSegment(sketch, "E572.68", {"start": v(-299.86, 126.36) * mm, "end": v(-301.37, 124.46) * mm});
            skLineSegment(sketch, "E572.69", {"start": v(-299.7, 126.57) * mm, "end": v(-299.86, 126.36) * mm});
            skLineSegment(sketch, "E572.70", {"start": v(-299.52, 126.78) * mm, "end": v(-299.7, 126.57) * mm});
            skLineSegment(sketch, "E572.71", {"start": v(-299.11, 127.21) * mm, "end": v(-299.52, 126.78) * mm});
            skLineSegment(sketch, "E572.72", {"start": v(-296.05, 130.7) * mm, "end": v(-299.11, 127.21) * mm});
            skLineSegment(sketch, "E572.73", {"start": v(-164.63, 245.7) * mm, "end": v(-164.93, 245.46) * mm});
            skLineSegment(sketch, "E572.74", {"start": v(-164.37, 245.95) * mm, "end": v(-164.63, 245.7) * mm});
            skLineSegment(sketch, "E572.75", {"start": v(-162.4, 247.8) * mm, "end": v(-164.37, 245.95) * mm});
            skLineSegment(sketch, "E572.76", {"start": v(-161.76, 248.47) * mm, "end": v(-162.4, 247.8) * mm});
            skLineSegment(sketch, "E572.77", {"start": v(-160.36, 249.98) * mm, "end": v(-161.76, 248.47) * mm});
            skLineSegment(sketch, "E572.78", {"start": v(-159.28, 251.11) * mm, "end": v(-160.36, 249.98) * mm});
            skLineSegment(sketch, "E572.79", {"start": v(-158.63, 251.73) * mm, "end": v(-159.28, 251.11) * mm});
            skLineSegment(sketch, "E572.80", {"start": v(-158.16, 252.17) * mm, "end": v(-158.63, 251.73) * mm});
            skLineSegment(sketch, "E572.81", {"start": v(-157.42, 252.83) * mm, "end": v(-158.16, 252.17) * mm});
            skLineSegment(sketch, "E572.82", {"start": v(-156.7, 253.48) * mm, "end": v(-157.42, 252.83) * mm});
            skLineSegment(sketch, "E572.83", {"start": v(-155.5, 254.5) * mm, "end": v(-156.7, 253.48) * mm});
            skLineSegment(sketch, "E572.84", {"start": v(-154.65, 255.38) * mm, "end": v(-155.5, 254.5) * mm});
            skLineSegment(sketch, "E572.85", {"start": v(-153.27, 256.8) * mm, "end": v(-154.65, 255.38) * mm});
            skLineSegment(sketch, "E572.86", {"start": v(-152.52, 257.49) * mm, "end": v(-153.27, 256.8) * mm});
            skLineSegment(sketch, "E572.87", {"start": v(-151, 258.89) * mm, "end": v(-152.52, 257.49) * mm});
            skLineSegment(sketch, "E572.88", {"start": v(-150.1, 259.85) * mm, "end": v(-151, 258.89) * mm});
            skLineSegment(sketch, "E572.89", {"start": v(-148.73, 261.24) * mm, "end": v(-150.1, 259.85) * mm});
            skLineSegment(sketch, "E572.90", {"start": v(-147.96, 262) * mm, "end": v(-148.73, 261.24) * mm});
            skLineSegment(sketch, "E572.91", {"start": v(-145.35, 264.56) * mm, "end": v(-147.96, 262) * mm});
            skLineSegment(sketch, "E572.92", {"start": v(-145.05, 264.86) * mm, "end": v(-145.35, 264.56) * mm});
            skLineSegment(sketch, "E572.93", {"start": v(-142.35, 267.48) * mm, "end": v(-145.05, 264.86) * mm});
            skLineSegment(sketch, "E572.94", {"start": v(-141.64, 268.19) * mm, "end": v(-142.35, 267.48) * mm});
            skLineSegment(sketch, "E572.95", {"start": v(-140.79, 268.96) * mm, "end": v(-141.64, 268.19) * mm});
            skLineSegment(sketch, "E572.96", {"start": v(-139.63, 270) * mm, "end": v(-140.79, 268.96) * mm});
            skLineSegment(sketch, "E572.97", {"start": v(-138.17, 271.19) * mm, "end": v(-139.63, 270) * mm});
            skLineSegment(sketch, "E572.98", {"start": v(-137.84, 271.45) * mm, "end": v(-138.17, 271.19) * mm});
            skLineSegment(sketch, "E572.99", {"start": v(-136.88, 272.15) * mm, "end": v(-137.84, 271.45) * mm});
            skLineSegment(sketch, "E572.100", {"start": v(-135.16, 273.42) * mm, "end": v(-136.88, 272.15) * mm});
            skLineSegment(sketch, "E572.101", {"start": v(-134.32, 274) * mm, "end": v(-135.16, 273.42) * mm});
            skLineSegment(sketch, "E572.102", {"start": v(-132.62, 275.18) * mm, "end": v(-134.32, 274) * mm});
            skLineSegment(sketch, "E572.103", {"start": v(-130.32, 276.54) * mm, "end": v(-132.62, 275.18) * mm});
            skLineSegment(sketch, "E572.104", {"start": v(-129.55, 277.02) * mm, "end": v(-130.32, 276.54) * mm});
            skLineSegment(sketch, "E572.105", {"start": v(-129.16, 277.23) * mm, "end": v(-129.55, 277.02) * mm});
            skLineSegment(sketch, "E572.106", {"start": v(-127.5, 278.15) * mm, "end": v(-129.16, 277.23) * mm});
            skLineSegment(sketch, "E572.107", {"start": v(-124.77, 279.54) * mm, "end": v(-127.5, 278.15) * mm});
            skLineSegment(sketch, "E572.108", {"start": v(-123.9, 279.98) * mm, "end": v(-124.77, 279.54) * mm});
            skLineSegment(sketch, "E572.109", {"start": v(-121.83, 280.91) * mm, "end": v(-123.9, 279.98) * mm});
            skLineSegment(sketch, "E572.110", {"start": v(-120.28, 281.54) * mm, "end": v(-121.83, 280.91) * mm});
            skLineSegment(sketch, "E572.111", {"start": v(-118.5, 282.28) * mm, "end": v(-120.28, 281.54) * mm});
            skLineSegment(sketch, "E572.112", {"start": v(-116.7, 282.89) * mm, "end": v(-118.5, 282.28) * mm});
            skLineSegment(sketch, "E572.113", {"start": v(-115.35, 283.31) * mm, "end": v(-116.7, 282.89) * mm});
            skLineSegment(sketch, "E572.114", {"start": v(-112.42, 284.17) * mm, "end": v(-115.35, 283.31) * mm});
            skLineSegment(sketch, "E572.115", {"start": v(-111.72, 284.38) * mm, "end": v(-112.42, 284.17) * mm});
            skLineSegment(sketch, "E572.116", {"start": v(-111.66, 284.4) * mm, "end": v(-111.72, 284.38) * mm});
            skLineSegment(sketch, "E572.117", {"start": v(-111.4, 284.47) * mm, "end": v(-111.66, 284.4) * mm});
            skLineSegment(sketch, "E572.118", {"start": v(-108.18, 285.34) * mm, "end": v(-111.4, 284.47) * mm});
            skLineSegment(sketch, "E572.119", {"start": v(-106.65, 285.75) * mm, "end": v(-108.18, 285.34) * mm});
            skLineSegment(sketch, "E572.120", {"start": v(-102.87, 286.68) * mm, "end": v(-106.65, 285.75) * mm});
            skLineSegment(sketch, "E572.121", {"start": v(-102.84, 286.69) * mm, "end": v(-102.87, 286.68) * mm});
            skLineSegment(sketch, "E572.122", {"start": v(-102.8, 286.7) * mm, "end": v(-102.84, 286.69) * mm});
            skLineSegment(sketch, "E572.123", {"start": v(-40.36, 296.81) * mm, "end": v(-42.5, 296.64) * mm});
            skLineSegment(sketch, "E572.124", {"start": v(-38.16, 296.98) * mm, "end": v(-40.36, 296.81) * mm});
            skLineSegment(sketch, "E572.125", {"start": v(-35.97, 297.13) * mm, "end": v(-38.16, 296.98) * mm});
            skLineSegment(sketch, "E572.126", {"start": v(-33.04, 297.33) * mm, "end": v(-35.97, 297.13) * mm});
            skLineSegment(sketch, "E572.127", {"start": v(-32.03, 297.4) * mm, "end": v(-33.04, 297.33) * mm});
            skLineSegment(sketch, "E572.128", {"start": v(-30.96, 297.44) * mm, "end": v(-32.03, 297.4) * mm});
            skLineSegment(sketch, "E572.129", {"start": v(-25.9, 297.63) * mm, "end": v(-30.96, 297.44) * mm});
            skLineSegment(sketch, "E572.130", {"start": v(-22.47, 297.79) * mm, "end": v(-25.9, 297.63) * mm});
            skLineSegment(sketch, "E572.131", {"start": v(-19.8, 297.89) * mm, "end": v(-22.47, 297.79) * mm});
            skLineSegment(sketch, "E572.132", {"start": v(-16.5, 297.91) * mm, "end": v(-19.8, 297.89) * mm});
            skLineSegment(sketch, "E572.133", {"start": v(-16.2, 297.91) * mm, "end": v(-16.5, 297.91) * mm});
            skLineSegment(sketch, "E572.134", {"start": v(-15.97, 297.9) * mm, "end": v(-16.2, 297.91) * mm});
            skLineSegment(sketch, "E572.135", {"start": v(-3.37, 297.69) * mm, "end": v(-4.35, 297.72) * mm});
            skLineSegment(sketch, "E572.136", {"start": v(-1.66, 297.62) * mm, "end": v(-3.37, 297.69) * mm});
            skLineSegment(sketch, "E572.137", {"start": v(-0.63, 297.7) * mm, "end": v(-1.66, 297.62) * mm});
            skLineSegment(sketch, "E572.138", {"start": v(1, 298.03) * mm, "end": v(-0.63, 297.7) * mm});
            skLineSegment(sketch, "E572.139", {"start": v(-4.35, 297.72) * mm, "end": v(-4.87, 297.74) * mm});
            skLineSegment(sketch, "E572.140", {"start": v(-4.87, 297.74) * mm, "end": v(-7.25, 297.8) * mm});
            skLineSegment(sketch, "E572.141", {"start": v(-7.25, 297.8) * mm, "end": v(-9.05, 297.77) * mm});
            skLineSegment(sketch, "E572.142", {"start": v(-9.05, 297.77) * mm, "end": v(-11.46, 297.77) * mm});
            skLineSegment(sketch, "E572.143", {"start": v(-11.46, 297.77) * mm, "end": v(-14.76, 297.88) * mm});
            skLineSegment(sketch, "E572.144", {"start": v(-14.76, 297.88) * mm, "end": v(-15.97, 297.9) * mm});
            skLineSegment(sketch, "E572.145", {"start": v(-42.5, 296.64) * mm, "end": v(-42.63, 296.63) * mm});
            skLineSegment(sketch, "E572.146", {"start": v(-42.63, 296.63) * mm, "end": v(-46.8, 296.3) * mm});
            skLineSegment(sketch, "E572.147", {"start": v(-46.8, 296.3) * mm, "end": v(-47.92, 296.2) * mm});
            skLineSegment(sketch, "E572.148", {"start": v(-47.92, 296.2) * mm, "end": v(-51.42, 295.87) * mm});
            skLineSegment(sketch, "E572.149", {"start": v(-51.42, 295.87) * mm, "end": v(-51.99, 295.81) * mm});
            skLineSegment(sketch, "E572.150", {"start": v(-51.99, 295.81) * mm, "end": v(-53.94, 295.6) * mm});
            skLineSegment(sketch, "E572.151", {"start": v(-53.94, 295.6) * mm, "end": v(-57.19, 295.17) * mm});
            skLineSegment(sketch, "E572.152", {"start": v(-57.19, 295.17) * mm, "end": v(-58.09, 295.05) * mm});
            skLineSegment(sketch, "E572.153", {"start": v(-58.09, 295.05) * mm, "end": v(-61.56, 294.56) * mm});
            skLineSegment(sketch, "E572.154", {"start": v(-61.56, 294.56) * mm, "end": v(-64.69, 294.15) * mm});
            skLineSegment(sketch, "E572.155", {"start": v(-64.69, 294.15) * mm, "end": v(-69, 293.53) * mm});
            skLineSegment(sketch, "E572.156", {"start": v(-69, 293.53) * mm, "end": v(-71.15, 293.2) * mm});
            skLineSegment(sketch, "E572.157", {"start": v(-71.15, 293.2) * mm, "end": v(-72.91, 292.91) * mm});
            skLineSegment(sketch, "E572.158", {"start": v(-72.91, 292.91) * mm, "end": v(-76.12, 292.35) * mm});
            skLineSegment(sketch, "E572.159", {"start": v(-76.12, 292.35) * mm, "end": v(-78.33, 291.98) * mm});
            skLineSegment(sketch, "E572.160", {"start": v(-78.33, 291.98) * mm, "end": v(-82.3, 291.25) * mm});
            skLineSegment(sketch, "E572.161", {"start": v(-82.3, 291.25) * mm, "end": v(-84.94, 290.76) * mm});
            skLineSegment(sketch, "E572.162", {"start": v(-84.94, 290.76) * mm, "end": v(-86, 290.53) * mm});
            skLineSegment(sketch, "E572.163", {"start": v(-86, 290.53) * mm, "end": v(-89.14, 289.84) * mm});
            skLineSegment(sketch, "E572.164", {"start": v(-89.14, 289.84) * mm, "end": v(-91.71, 289.33) * mm});
            skLineSegment(sketch, "E572.165", {"start": v(-91.71, 289.33) * mm, "end": v(-95.09, 288.58) * mm});
            skLineSegment(sketch, "E572.166", {"start": v(-95.09, 288.58) * mm, "end": v(-96.22, 288.33) * mm});
            skLineSegment(sketch, "E572.167", {"start": v(-96.22, 288.33) * mm, "end": v(-97, 288.14) * mm});
            skLineSegment(sketch, "E572.168", {"start": v(-97, 288.14) * mm, "end": v(-102.8, 286.7) * mm});
            skLineSegment(sketch, "E572.169", {"start": v(-164.93, 245.46) * mm, "end": v(-167.23, 243.79) * mm});
            skLineSegment(sketch, "E572.170", {"start": v(-167.23, 243.79) * mm, "end": v(-168.43, 243.14) * mm});
            skLineSegment(sketch, "E572.171", {"start": v(-168.43, 243.14) * mm, "end": v(-170.26, 242.01) * mm});
            skLineSegment(sketch, "E572.172", {"start": v(-170.26, 242.01) * mm, "end": v(-170.6, 241.82) * mm});
            skLineSegment(sketch, "E572.173", {"start": v(-170.6, 241.82) * mm, "end": v(-171.92, 240.44) * mm});
            skLineSegment(sketch, "E572.174", {"start": v(-171.92, 240.44) * mm, "end": v(-173.35, 238.82) * mm});
            skLineSegment(sketch, "E572.175", {"start": v(-173.35, 238.82) * mm, "end": v(-173.46, 238.7) * mm});
            skLineSegment(sketch, "E572.176", {"start": v(-173.46, 238.7) * mm, "end": v(-173.56, 238.59) * mm});
            skLineSegment(sketch, "E572.177", {"start": v(-173.56, 238.59) * mm, "end": v(-175.65, 236.32) * mm});
            skLineSegment(sketch, "E572.178", {"start": v(-175.65, 236.32) * mm, "end": v(-175.86, 236.1) * mm});
            skLineSegment(sketch, "E572.179", {"start": v(-175.86, 236.1) * mm, "end": v(-177.47, 234.48) * mm});
            skLineSegment(sketch, "E572.180", {"start": v(-177.47, 234.48) * mm, "end": v(-178.87, 233.14) * mm});
            skLineSegment(sketch, "E572.181", {"start": v(-178.87, 233.14) * mm, "end": v(-179.38, 232.67) * mm});
            skLineSegment(sketch, "E572.182", {"start": v(-179.38, 232.67) * mm, "end": v(-179.53, 232.5) * mm});
            skLineSegment(sketch, "E572.183", {"start": v(-179.53, 232.5) * mm, "end": v(-182.14, 229.89) * mm});
            skLineSegment(sketch, "E572.184", {"start": v(-182.14, 229.89) * mm, "end": v(-184.61, 227.67) * mm});
            skLineSegment(sketch, "E572.185", {"start": v(-184.61, 227.67) * mm, "end": v(-185.13, 227.2) * mm});
            skLineSegment(sketch, "E572.186", {"start": v(-185.13, 227.2) * mm, "end": v(-185.41, 226.95) * mm});
            skLineSegment(sketch, "E572.187", {"start": v(-185.41, 226.95) * mm, "end": v(-186.07, 226.3) * mm});
            skLineSegment(sketch, "E572.188", {"start": v(-186.07, 226.3) * mm, "end": v(-187.03, 225.34) * mm});
            skLineSegment(sketch, "E572.189", {"start": v(-187.03, 225.34) * mm, "end": v(-187.85, 224.51) * mm});
            skLineSegment(sketch, "E572.190", {"start": v(-187.85, 224.51) * mm, "end": v(-188.9, 223.43) * mm});
            skLineSegment(sketch, "E572.191", {"start": v(-188.9, 223.43) * mm, "end": v(-189.5, 222.85) * mm});
            skLineSegment(sketch, "E572.192", {"start": v(-189.5, 222.85) * mm, "end": v(-190.54, 221.82) * mm});
            skLineSegment(sketch, "E572.193", {"start": v(-190.54, 221.82) * mm, "end": v(-191.87, 220.52) * mm});
            skLineSegment(sketch, "E572.194", {"start": v(-191.87, 220.52) * mm, "end": v(-192.5, 219.93) * mm});
            skLineSegment(sketch, "E572.195", {"start": v(-192.5, 219.93) * mm, "end": v(-193.9, 218.64) * mm});
            skLineSegment(sketch, "E572.196", {"start": v(-193.9, 218.64) * mm, "end": v(-195.3, 217.2) * mm});
            skLineSegment(sketch, "E572.197", {"start": v(-195.3, 217.2) * mm, "end": v(-196.6, 215.96) * mm});
            skLineSegment(sketch, "E572.198", {"start": v(-196.6, 215.96) * mm, "end": v(-198.2, 214.54) * mm});
            skLineSegment(sketch, "E572.199", {"start": v(-198.2, 214.54) * mm, "end": v(-199.43, 213.4) * mm});
            skLineSegment(sketch, "E572.200", {"start": v(-199.43, 213.4) * mm, "end": v(-200.25, 212.61) * mm});
            skLineSegment(sketch, "E572.201", {"start": v(-200.25, 212.61) * mm, "end": v(-201.79, 211.1) * mm});
            skLineSegment(sketch, "E572.202", {"start": v(-201.79, 211.1) * mm, "end": v(-202.06, 210.83) * mm});
            skLineSegment(sketch, "E572.203", {"start": v(-202.06, 210.83) * mm, "end": v(-202.4, 210.5) * mm});
            skLineSegment(sketch, "E572.204", {"start": v(-202.4, 210.5) * mm, "end": v(-203.46, 209.5) * mm});
            skLineSegment(sketch, "E572.205", {"start": v(-203.46, 209.5) * mm, "end": v(-204.08, 208.95) * mm});
            skLineSegment(sketch, "E572.206", {"start": v(-204.08, 208.95) * mm, "end": v(-206.17, 206.9) * mm});
            skLineSegment(sketch, "E572.207", {"start": v(-206.17, 206.9) * mm, "end": v(-206.38, 206.7) * mm});
            skLineSegment(sketch, "E572.208", {"start": v(-206.38, 206.7) * mm, "end": v(-206.99, 206.13) * mm});
            skLineSegment(sketch, "E572.209", {"start": v(-206.99, 206.13) * mm, "end": v(-208.05, 205.13) * mm});
            skLineSegment(sketch, "E572.210", {"start": v(-208.05, 205.13) * mm, "end": v(-208.2, 204.96) * mm});
            skLineSegment(sketch, "E572.211", {"start": v(-208.2, 204.96) * mm, "end": v(-209.71, 203.29) * mm});
            skLineSegment(sketch, "E572.212", {"start": v(-209.71, 203.29) * mm, "end": v(-210.48, 202.56) * mm});
            skLineSegment(sketch, "E572.213", {"start": v(-210.48, 202.56) * mm, "end": v(-212, 201.03) * mm});
            skLineSegment(sketch, "E572.214", {"start": v(-212, 201.03) * mm, "end": v(-212.15, 200.9) * mm});
            skLineSegment(sketch, "E572.215", {"start": v(-212.15, 200.9) * mm, "end": v(-214.43, 198.86) * mm});
            skLineSegment(sketch, "E572.216", {"start": v(-214.43, 198.86) * mm, "end": v(-215.1, 198.16) * mm});
            skLineSegment(sketch, "E572.217", {"start": v(-215.1, 198.16) * mm, "end": v(-216.6, 196.7) * mm});
            skLineSegment(sketch, "E572.218", {"start": v(-216.6, 196.7) * mm, "end": v(-217.67, 195.66) * mm});
            skLineSegment(sketch, "E572.219", {"start": v(-217.67, 195.66) * mm, "end": v(-218.56, 194.77) * mm});
            skLineSegment(sketch, "E572.220", {"start": v(-218.56, 194.77) * mm, "end": v(-220.77, 192.6) * mm});
            skLineSegment(sketch, "E572.221", {"start": v(-220.77, 192.6) * mm, "end": v(-221.17, 192.2) * mm});
            skLineSegment(sketch, "E572.222", {"start": v(-221.17, 192.2) * mm, "end": v(-223.46, 190.03) * mm});
            skLineSegment(sketch, "E572.223", {"start": v(-223.46, 190.03) * mm, "end": v(-224.2, 189.27) * mm});
            skLineSegment(sketch, "E572.224", {"start": v(-224.2, 189.27) * mm, "end": v(-225.47, 188.03) * mm});
            skLineSegment(sketch, "E572.225", {"start": v(-225.47, 188.03) * mm, "end": v(-226.16, 187.39) * mm});
            skLineSegment(sketch, "E572.226", {"start": v(-226.16, 187.39) * mm, "end": v(-227.86, 185.88) * mm});
            skLineSegment(sketch, "E572.227", {"start": v(-227.86, 185.88) * mm, "end": v(-228.47, 185.3) * mm});
            skLineSegment(sketch, "E572.228", {"start": v(-228.47, 185.3) * mm, "end": v(-229.57, 184.26) * mm});
            skLineSegment(sketch, "E572.229", {"start": v(-229.57, 184.26) * mm, "end": v(-230.92, 182.96) * mm});
            skLineSegment(sketch, "E572.230", {"start": v(-230.92, 182.96) * mm, "end": v(-231.33, 182.54) * mm});
            skLineSegment(sketch, "E572.231", {"start": v(-231.33, 182.54) * mm, "end": v(-232.8, 181.02) * mm});
            skLineSegment(sketch, "E572.232", {"start": v(-232.8, 181.02) * mm, "end": v(-234.35, 179.62) * mm});
            skLineSegment(sketch, "E572.233", {"start": v(-234.35, 179.62) * mm, "end": v(-235.68, 178.46) * mm});
            skLineSegment(sketch, "E572.234", {"start": v(-235.68, 178.46) * mm, "end": v(-236.15, 178.04) * mm});
            skLineSegment(sketch, "E572.235", {"start": v(-236.15, 178.04) * mm, "end": v(-237.59, 176.87) * mm});
            skLineSegment(sketch, "E572.236", {"start": v(-237.59, 176.87) * mm, "end": v(-238.92, 175.87) * mm});
            skLineSegment(sketch, "E572.237", {"start": v(-238.92, 175.87) * mm, "end": v(-241.7, 173.6) * mm});
            skLineSegment(sketch, "E572.238", {"start": v(-241.7, 173.6) * mm, "end": v(-242.6, 172.92) * mm});
            skLineSegment(sketch, "E572.239", {"start": v(-242.6, 172.92) * mm, "end": v(-245.97, 170.6) * mm});
            skLineSegment(sketch, "E572.240", {"start": v(-245.97, 170.6) * mm, "end": v(-247.96, 169.23) * mm});
            skLineSegment(sketch, "E572.241", {"start": v(-247.96, 169.23) * mm, "end": v(-249.4, 168.24) * mm});
            skLineSegment(sketch, "E572.242", {"start": v(-249.4, 168.24) * mm, "end": v(-249.7, 168.03) * mm});
            skLineSegment(sketch, "E572.243", {"start": v(-249.7, 168.03) * mm, "end": v(-252.53, 166.19) * mm});
            skLineSegment(sketch, "E572.244", {"start": v(-252.53, 166.19) * mm, "end": v(-253.44, 165.55) * mm});
            skLineSegment(sketch, "E572.245", {"start": v(-253.44, 165.55) * mm, "end": v(-256.16, 163.67) * mm});
            skLineSegment(sketch, "E572.246", {"start": v(-256.16, 163.67) * mm, "end": v(-257.4, 162.84) * mm});
            skLineSegment(sketch, "E572.247", {"start": v(-257.4, 162.84) * mm, "end": v(-261.01, 160.48) * mm});
            skLineSegment(sketch, "E572.248", {"start": v(-261.01, 160.48) * mm, "end": v(-263.13, 159.06) * mm});
            skLineSegment(sketch, "E572.249", {"start": v(-263.13, 159.06) * mm, "end": v(-265.98, 157.1) * mm});
            skLineSegment(sketch, "E572.250", {"start": v(-265.98, 157.1) * mm, "end": v(-267.91, 155.84) * mm});
            skLineSegment(sketch, "E572.251", {"start": v(-267.91, 155.84) * mm, "end": v(-270.04, 154.4) * mm});
            skLineSegment(sketch, "E572.252", {"start": v(-270.04, 154.4) * mm, "end": v(-270.07, 154.37) * mm});
            skLineSegment(sketch, "E572.253", {"start": v(-270.07, 154.37) * mm, "end": v(-275.28, 150.43) * mm});
            skLineSegment(sketch, "E572.254", {"start": v(-275.28, 150.43) * mm, "end": v(-275.74, 150.1) * mm});
            skLineSegment(sketch, "E572.255", {"start": v(-275.74, 150.1) * mm, "end": v(-276.63, 149.38) * mm});
            skLineSegment(sketch, "E572.256", {"start": v(-276.63, 149.38) * mm, "end": v(-279.14, 147.32) * mm});
            skLineSegment(sketch, "E572.257", {"start": v(-279.14, 147.32) * mm, "end": v(-281.12, 145.62) * mm});
            skLineSegment(sketch, "E572.258", {"start": v(-281.12, 145.62) * mm, "end": v(-281.7, 145.12) * mm});
            skLineSegment(sketch, "E572.259", {"start": v(-281.7, 145.12) * mm, "end": v(-281.8, 145.03) * mm});
            skLineSegment(sketch, "E572.260", {"start": v(-281.8, 145.03) * mm, "end": v(-282.15, 144.7) * mm});
            skLineSegment(sketch, "E572.261", {"start": v(-282.15, 144.7) * mm, "end": v(-285.5, 141.63) * mm});
            skLineSegment(sketch, "E572.262", {"start": v(-285.5, 141.63) * mm, "end": v(-287.2, 140.23) * mm});
            skLineSegment(sketch, "E572.263", {"start": v(-287.2, 140.23) * mm, "end": v(-287.4, 140.06) * mm});
            skLineSegment(sketch, "E572.264", {"start": v(-287.4, 140.06) * mm, "end": v(-289.24, 138.24) * mm});
            skLineSegment(sketch, "E572.265", {"start": v(-289.24, 138.24) * mm, "end": v(-289.3, 138.18) * mm});
            skLineSegment(sketch, "E572.266", {"start": v(-289.3, 138.18) * mm, "end": v(-290.49, 136.81) * mm});
            skLineSegment(sketch, "E572.267", {"start": v(-290.49, 136.81) * mm, "end": v(-292.52, 134.65) * mm});
            skLineSegment(sketch, "E572.268", {"start": v(-292.52, 134.65) * mm, "end": v(-293.25, 133.87) * mm});
            skLineSegment(sketch, "E572.269", {"start": v(-293.25, 133.87) * mm, "end": v(-293.29, 133.83) * mm});
            skLineSegment(sketch, "E572.270", {"start": v(-293.29, 133.83) * mm, "end": v(-296.05, 130.7) * mm});
            skLineSegment(sketch, "E573", {"start": v(1, 298.03) * mm, "end": v(5, 278.43) * mm});
            skLineSegment(sketch, "E574", {"start": v(-331.75, 1.06) * mm, "end": v(-312.26, 5.65) * mm});
            skSolve(sketch);
        }
        {
            var Q0;
            Q0=qCreatedBy(id+"F0.planeOp",FACE);
            cPlane(context, id + "F4", {"entities" : qUnion([Q0]), "cplaneType" : CPlaneType.OFFSET, "offset" : 74 * mm, "width" : 150 * mm, "height" : 150 * mm});
        }
        {
            var Q0;
            Q0=qCreatedBy(id+"F4.planeOp",FACE);
            var sketch = newSketch(context, id + "F5", { "sketchPlane" : qUnion([Q0])});
            skPoint(sketch, "E575", {"position": v(0, 0) * mm});
            skLineSegment(sketch, "E576", {"start": v(-330.33, 0) * mm, "end": v(-330.4, 0.62) * mm});
            skLineSegment(sketch, "E577", {"start": v(-330.4, 0.62) * mm, "end": v(-330.41, 0.68) * mm});
            skLineSegment(sketch, "E578", {"start": v(-330.41, 0.68) * mm, "end": v(-330.57, 1.52) * mm});
            skLineSegment(sketch, "E579", {"start": v(-330.57, 1.52) * mm, "end": v(-331.02, 3.75) * mm});
            skLineSegment(sketch, "E580", {"start": v(-331.02, 3.75) * mm, "end": v(-331.13, 4.3) * mm});
            skLineSegment(sketch, "E581", {"start": v(-331.13, 4.3) * mm, "end": v(-331.18, 4.64) * mm});
            skLineSegment(sketch, "E582", {"start": v(-331.18, 4.64) * mm, "end": v(-331.34, 5.66) * mm});
            skLineSegment(sketch, "E583", {"start": v(-331.34, 5.66) * mm, "end": v(-331.66, 7.8) * mm});
            skLineSegment(sketch, "E584", {"start": v(-331.66, 7.8) * mm, "end": v(-331.83, 9.6) * mm});
            skLineSegment(sketch, "E585", {"start": v(-331.83, 9.6) * mm, "end": v(-332.2, 13.06) * mm});
            skLineSegment(sketch, "E586", {"start": v(-332.2, 13.06) * mm, "end": v(-332.3, 15.23) * mm});
            skLineSegment(sketch, "E587", {"start": v(-332.3, 15.23) * mm, "end": v(-332.39, 17.06) * mm});
            skLineSegment(sketch, "E588", {"start": v(-332.39, 17.06) * mm, "end": v(-332.48, 20.37) * mm});
            skLineSegment(sketch, "E589", {"start": v(-332.48, 20.37) * mm, "end": v(-332.5, 23.14) * mm});
            skLineSegment(sketch, "E590", {"start": v(-332.5, 23.14) * mm, "end": v(-332.45, 24.46) * mm});
            skLineSegment(sketch, "E591", {"start": v(-332.45, 24.46) * mm, "end": v(-332.5, 26.9) * mm});
            skLineSegment(sketch, "E592", {"start": v(-332.5, 26.9) * mm, "end": v(-332.48, 28.42) * mm});
            skLineSegment(sketch, "E593", {"start": v(-332.48, 28.42) * mm, "end": v(-332.43, 31.28) * mm});
            skLineSegment(sketch, "E594", {"start": v(-332.43, 31.28) * mm, "end": v(-332.4, 33.1) * mm});
            skLineSegment(sketch, "E595", {"start": v(-332.4, 33.1) * mm, "end": v(-332.3, 35.42) * mm});
            skLineSegment(sketch, "E596", {"start": v(-332.3, 35.42) * mm, "end": v(-332.21, 38.3) * mm});
            skLineSegment(sketch, "E597", {"start": v(-332.21, 38.3) * mm, "end": v(-332.16, 39.48) * mm});
            skLineSegment(sketch, "E598", {"start": v(-332.16, 39.48) * mm, "end": v(-332.07, 40.83) * mm});
            skLineSegment(sketch, "E599", {"start": v(-332.07, 40.83) * mm, "end": v(-331.96, 42.37) * mm});
            skLineSegment(sketch, "E600", {"start": v(-331.96, 42.37) * mm, "end": v(-331.63, 44.56) * mm});
            skLineSegment(sketch, "E601", {"start": v(-331.63, 44.56) * mm, "end": v(-331.52, 45.63) * mm});
            skLineSegment(sketch, "E602", {"start": v(-331.52, 45.63) * mm, "end": v(-331.2, 48.98) * mm});
            skLineSegment(sketch, "E603", {"start": v(-331.2, 48.98) * mm, "end": v(-331.18, 49.14) * mm});
            skLineSegment(sketch, "E604", {"start": v(-331.18, 49.14) * mm, "end": v(-331.1, 49.9) * mm});
            skLineSegment(sketch, "E605", {"start": v(-331.1, 49.9) * mm, "end": v(-330.74, 52.93) * mm});
            skLineSegment(sketch, "E606", {"start": v(-330.74, 52.93) * mm, "end": v(-330.6, 54.03) * mm});
            skLineSegment(sketch, "E607", {"start": v(-330.6, 54.03) * mm, "end": v(-330.35, 55.72) * mm});
            skLineSegment(sketch, "E608", {"start": v(-330.35, 55.72) * mm, "end": v(-330.1, 57.29) * mm});
            skLineSegment(sketch, "E609", {"start": v(-330.1, 57.29) * mm, "end": v(-329.9, 58.63) * mm});
            skLineSegment(sketch, "E610", {"start": v(-329.9, 58.63) * mm, "end": v(-329.65, 60) * mm});
            skLineSegment(sketch, "E611", {"start": v(-329.65, 60) * mm, "end": v(-329.42, 61.38) * mm});
            skLineSegment(sketch, "E612", {"start": v(-329.42, 61.38) * mm, "end": v(-329.19, 62.53) * mm});
            skLineSegment(sketch, "E613", {"start": v(-329.19, 62.53) * mm, "end": v(-328.96, 63.69) * mm});
            skLineSegment(sketch, "E614", {"start": v(-328.96, 63.69) * mm, "end": v(-328.62, 65.28) * mm});
            skLineSegment(sketch, "E615", {"start": v(-328.62, 65.28) * mm, "end": v(-328.36, 66.35) * mm});
            skLineSegment(sketch, "E616", {"start": v(-328.36, 66.35) * mm, "end": v(-327.9, 68.4) * mm});
            skLineSegment(sketch, "E617", {"start": v(-327.9, 68.4) * mm, "end": v(-326.94, 72.62) * mm});
            skLineSegment(sketch, "E618", {"start": v(-326.94, 72.62) * mm, "end": v(-326.91, 72.74) * mm});
            skLineSegment(sketch, "E619", {"start": v(-326.91, 72.74) * mm, "end": v(-326.9, 72.78) * mm});
            skLineSegment(sketch, "E620", {"start": v(-326.9, 72.78) * mm, "end": v(-325.73, 76.72) * mm});
            skLineSegment(sketch, "E621", {"start": v(-325.73, 76.72) * mm, "end": v(-325.5, 77.56) * mm});
            skLineSegment(sketch, "E622", {"start": v(-325.5, 77.56) * mm, "end": v(-325.05, 79.16) * mm});
            skLineSegment(sketch, "E623", {"start": v(-325.05, 79.16) * mm, "end": v(-324.87, 79.68) * mm});
            skLineSegment(sketch, "E624", {"start": v(-324.87, 79.68) * mm, "end": v(-324.68, 80.24) * mm});
            skLineSegment(sketch, "E625", {"start": v(-324.68, 80.24) * mm, "end": v(-323.26, 84.12) * mm});
            skLineSegment(sketch, "E626", {"start": v(-323.26, 84.12) * mm, "end": v(-322.85, 85.34) * mm});
            skLineSegment(sketch, "E627", {"start": v(-322.85, 85.34) * mm, "end": v(-322.04, 87.73) * mm});
            skLineSegment(sketch, "E628", {"start": v(-322.04, 87.73) * mm, "end": v(-321.66, 88.73) * mm});
            skLineSegment(sketch, "E629", {"start": v(-321.66, 88.73) * mm, "end": v(-321.3, 89.59) * mm});
            skLineSegment(sketch, "E630", {"start": v(-321.3, 89.59) * mm, "end": v(-319.97, 92.9) * mm});
            skLineSegment(sketch, "E631", {"start": v(-319.97, 92.9) * mm, "end": v(-319.77, 93.4) * mm});
            skLineSegment(sketch, "E632", {"start": v(-319.77, 93.4) * mm, "end": v(-319.54, 93.93) * mm});
            skLineSegment(sketch, "E633", {"start": v(-319.54, 93.93) * mm, "end": v(-317.6, 98.2) * mm});
            skLineSegment(sketch, "E634", {"start": v(-317.6, 98.2) * mm, "end": v(-317.3, 98.9) * mm});
            skLineSegment(sketch, "E635", {"start": v(-317.3, 98.9) * mm, "end": v(-316.33, 100.91) * mm});
            skLineSegment(sketch, "E636", {"start": v(-316.33, 100.91) * mm, "end": v(-316, 101.61) * mm});
            skLineSegment(sketch, "E637", {"start": v(-316, 101.61) * mm, "end": v(-315.34, 103.03) * mm});
            skLineSegment(sketch, "E638", {"start": v(-315.34, 103.03) * mm, "end": v(-314.66, 104.5) * mm});
            skLineSegment(sketch, "E639", {"start": v(-314.66, 104.5) * mm, "end": v(-314.31, 105.18) * mm});
            skLineSegment(sketch, "E640", {"start": v(-314.31, 105.18) * mm, "end": v(-312.9, 107.75) * mm});
            skLineSegment(sketch, "E641", {"start": v(-312.9, 107.75) * mm, "end": v(-312.77, 107.98) * mm});
            skLineSegment(sketch, "E642", {"start": v(-312.77, 107.98) * mm, "end": v(-312.65, 108.2) * mm});
            skLineSegment(sketch, "E643", {"start": v(-312.65, 108.2) * mm, "end": v(-310.75, 111.34) * mm});
            skLineSegment(sketch, "E644", {"start": v(-310.75, 111.34) * mm, "end": v(-310.24, 112.24) * mm});
            skLineSegment(sketch, "E645", {"start": v(-310.24, 112.24) * mm, "end": v(-309.07, 114.3) * mm});
            skLineSegment(sketch, "E646", {"start": v(-309.07, 114.3) * mm, "end": v(-308.23, 115.61) * mm});
            skLineSegment(sketch, "E647", {"start": v(-308.23, 115.61) * mm, "end": v(-307.65, 116.46) * mm});
            skLineSegment(sketch, "E648", {"start": v(-307.65, 116.46) * mm, "end": v(-307.12, 117.3) * mm});
            skLineSegment(sketch, "E649", {"start": v(-307.12, 117.3) * mm, "end": v(-306.1, 118.9) * mm});
            skLineSegment(sketch, "E650", {"start": v(-306.1, 118.9) * mm, "end": v(-305.12, 120.36) * mm});
            skLineSegment(sketch, "E651", {"start": v(-305.12, 120.36) * mm, "end": v(-304.49, 121.27) * mm});
            skLineSegment(sketch, "E652", {"start": v(-304.49, 121.27) * mm, "end": v(-302.96, 123.35) * mm});
            skLineSegment(sketch, "E653", {"start": v(-302.96, 123.35) * mm, "end": v(-302.81, 123.54) * mm});
            skLineSegment(sketch, "E654", {"start": v(-302.81, 123.54) * mm, "end": v(-302.72, 123.66) * mm});
            skLineSegment(sketch, "E655", {"start": v(-302.72, 123.66) * mm, "end": v(-300.64, 126.45) * mm});
            skLineSegment(sketch, "E656", {"start": v(-300.64, 126.45) * mm, "end": v(-300.37, 126.79) * mm});
            skLineSegment(sketch, "E657", {"start": v(-300.37, 126.79) * mm, "end": v(-298.75, 128.97) * mm});
            skLineSegment(sketch, "E658", {"start": v(-298.75, 128.97) * mm, "end": v(-297.27, 130.67) * mm});
            skLineSegment(sketch, "E659", {"start": v(-297.27, 130.67) * mm, "end": v(-296.48, 131.65) * mm});
            skLineSegment(sketch, "E660", {"start": v(-296.48, 131.65) * mm, "end": v(-294.56, 134.05) * mm});
            skLineSegment(sketch, "E661", {"start": v(-294.56, 134.05) * mm, "end": v(-293.99, 134.7) * mm});
            skLineSegment(sketch, "E662", {"start": v(-293.99, 134.7) * mm, "end": v(-293.25, 135.57) * mm});
            skLineSegment(sketch, "E663", {"start": v(-293.25, 135.57) * mm, "end": v(-291.88, 137.05) * mm});
            skLineSegment(sketch, "E664", {"start": v(-291.88, 137.05) * mm, "end": v(-290.07, 139) * mm});
            skLineSegment(sketch, "E665", {"start": v(-290.07, 139) * mm, "end": v(-289.45, 139.64) * mm});
            skLineSegment(sketch, "E666", {"start": v(-289.45, 139.64) * mm, "end": v(-287.05, 142.16) * mm});
            skLineSegment(sketch, "E667", {"start": v(-287.05, 142.16) * mm, "end": v(-285.3, 143.9) * mm});
            skLineSegment(sketch, "E668", {"start": v(-285.3, 143.9) * mm, "end": v(-284.85, 144.33) * mm});
            skLineSegment(sketch, "E669", {"start": v(-284.85, 144.33) * mm, "end": v(-283.42, 145.68) * mm});
            skLineSegment(sketch, "E670", {"start": v(-283.42, 145.68) * mm, "end": v(-279.97, 148.87) * mm});
            skLineSegment(sketch, "E671", {"start": v(-279.97, 148.87) * mm, "end": v(-279.93, 148.9) * mm});
            skLineSegment(sketch, "E672", {"start": v(-279.93, 148.9) * mm, "end": v(-279.91, 148.92) * mm});
            skLineSegment(sketch, "E673", {"start": v(-279.91, 148.92) * mm, "end": v(-276.6, 151.78) * mm});
            skLineSegment(sketch, "E674", {"start": v(-276.6, 151.78) * mm, "end": v(-276.4, 151.94) * mm});
            skLineSegment(sketch, "E675", {"start": v(-276.4, 151.94) * mm, "end": v(-275.88, 152.37) * mm});
            skLineSegment(sketch, "E676", {"start": v(-275.88, 152.37) * mm, "end": v(-273.06, 154.57) * mm});
            skLineSegment(sketch, "E677", {"start": v(-273.06, 154.57) * mm, "end": v(-271.58, 155.74) * mm});
            skLineSegment(sketch, "E678", {"start": v(-271.58, 155.74) * mm, "end": v(-269.62, 157.28) * mm});
            skLineSegment(sketch, "E679", {"start": v(-269.62, 157.28) * mm, "end": v(-266.8, 159.37) * mm});
            skLineSegment(sketch, "E680", {"start": v(-266.8, 159.37) * mm, "end": v(-265.92, 160) * mm});
            skLineSegment(sketch, "E681", {"start": v(-265.92, 160) * mm, "end": v(-265.1, 160.62) * mm});
            skLineSegment(sketch, "E682", {"start": v(-265.1, 160.62) * mm, "end": v(-263.49, 161.8) * mm});
            skLineSegment(sketch, "E683", {"start": v(-263.49, 161.8) * mm, "end": v(-262.81, 162.23) * mm});
            skLineSegment(sketch, "E684", {"start": v(-262.81, 162.23) * mm, "end": v(-261.25, 163.33) * mm});
            skLineSegment(sketch, "E685", {"start": v(-261.25, 163.33) * mm, "end": v(-260.86, 163.6) * mm});
            skLineSegment(sketch, "E686", {"start": v(-260.86, 163.6) * mm, "end": v(-258.3, 164.97) * mm});
            skLineSegment(sketch, "E687", {"start": v(-258.3, 164.97) * mm, "end": v(-258.17, 165.06) * mm});
            skLineSegment(sketch, "E688", {"start": v(-258.17, 165.06) * mm, "end": v(-255.08, 166.93) * mm});
            skLineSegment(sketch, "E689", {"start": v(-255.08, 166.93) * mm, "end": v(-254.73, 167.19) * mm});
            skLineSegment(sketch, "E690", {"start": v(-254.73, 167.19) * mm, "end": v(-252.52, 169.13) * mm});
            skLineSegment(sketch, "E691", {"start": v(-252.52, 169.13) * mm, "end": v(-252.51, 169.13) * mm});
            skLineSegment(sketch, "E692", {"start": v(-252.51, 169.13) * mm, "end": v(-250.85, 170.33) * mm});
            skLineSegment(sketch, "E693", {"start": v(-250.85, 170.33) * mm, "end": v(-248.7, 171.85) * mm});
            skLineSegment(sketch, "E694", {"start": v(-248.7, 171.85) * mm, "end": v(-248.19, 172.22) * mm});
            skLineSegment(sketch, "E695", {"start": v(-248.19, 172.22) * mm, "end": v(-245.66, 174.06) * mm});
            skLineSegment(sketch, "E696", {"start": v(-245.66, 174.06) * mm, "end": v(-242.3, 176.33) * mm});
            skLineSegment(sketch, "E697", {"start": v(-242.3, 176.33) * mm, "end": v(-242.15, 176.44) * mm});
            skLineSegment(sketch, "E698", {"start": v(-242.15, 176.44) * mm, "end": v(-241.95, 176.58) * mm});
            skLineSegment(sketch, "E699", {"start": v(-241.95, 176.58) * mm, "end": v(-239.58, 178.4) * mm});
            skLineSegment(sketch, "E700", {"start": v(-239.58, 178.4) * mm, "end": v(-238.5, 179.14) * mm});
            skLineSegment(sketch, "E701", {"start": v(-238.5, 179.14) * mm, "end": v(-237.33, 180) * mm});
            skLineSegment(sketch, "E702", {"start": v(-237.33, 180) * mm, "end": v(-235.23, 181.1) * mm});
            skLineSegment(sketch, "E703", {"start": v(-235.23, 181.1) * mm, "end": v(-234.62, 181.46) * mm});
            skLineSegment(sketch, "E704", {"start": v(-234.62, 181.46) * mm, "end": v(-233.19, 182.3) * mm});
            skLineSegment(sketch, "E705", {"start": v(-233.19, 182.3) * mm, "end": v(-232.96, 182.5) * mm});
            skLineSegment(sketch, "E706", {"start": v(-232.96, 182.5) * mm, "end": v(-232.63, 182.81) * mm});
            skLineSegment(sketch, "E707", {"start": v(-232.63, 182.81) * mm, "end": v(-231.03, 184.31) * mm});
            skLineSegment(sketch, "E708", {"start": v(-231.03, 184.31) * mm, "end": v(-229.5, 185.8) * mm});
            skLineSegment(sketch, "E709", {"start": v(-229.5, 185.8) * mm, "end": v(-228.05, 187.24) * mm});
            skLineSegment(sketch, "E710", {"start": v(-228.05, 187.24) * mm, "end": v(-225.89, 189.37) * mm});
            skLineSegment(sketch, "E711", {"start": v(-225.89, 189.37) * mm, "end": v(-225.4, 189.85) * mm});
            skLineSegment(sketch, "E712", {"start": v(-225.4, 189.85) * mm, "end": v(-225, 190.24) * mm});
            skLineSegment(sketch, "E713", {"start": v(-225, 190.24) * mm, "end": v(-221.92, 193.06) * mm});
            skLineSegment(sketch, "E714", {"start": v(-221.92, 193.06) * mm, "end": v(-221.7, 193.26) * mm});
            skLineSegment(sketch, "E715", {"start": v(-221.7, 193.26) * mm, "end": v(-221.39, 193.58) * mm});
            skLineSegment(sketch, "E716", {"start": v(-221.39, 193.58) * mm, "end": v(-219.45, 195.6) * mm});
            skLineSegment(sketch, "E717", {"start": v(-219.45, 195.6) * mm, "end": v(-217.32, 197.72) * mm});
            skLineSegment(sketch, "E718", {"start": v(-217.32, 197.72) * mm, "end": v(-217.02, 198.01) * mm});
            skLineSegment(sketch, "E719", {"start": v(-217.02, 198.01) * mm, "end": v(-215.55, 199.44) * mm});
            skLineSegment(sketch, "E720", {"start": v(-215.55, 199.44) * mm, "end": v(-213.04, 201.88) * mm});
            skLineSegment(sketch, "E721", {"start": v(-213.04, 201.88) * mm, "end": v(-212.8, 202.11) * mm});
            skLineSegment(sketch, "E722", {"start": v(-212.8, 202.11) * mm, "end": v(-212.03, 202.88) * mm});
            skLineSegment(sketch, "E723", {"start": v(-212.03, 202.88) * mm, "end": v(-208.32, 206.5) * mm});
            skLineSegment(sketch, "E724", {"start": v(-208.32, 206.5) * mm, "end": v(-206.58, 208.2) * mm});
            skLineSegment(sketch, "E725", {"start": v(-206.58, 208.2) * mm, "end": v(-205.32, 209.4) * mm});
            skLineSegment(sketch, "E726", {"start": v(-205.32, 209.4) * mm, "end": v(-205.02, 209.74) * mm});
            skLineSegment(sketch, "E727", {"start": v(-205.02, 209.74) * mm, "end": v(-203.78, 211.01) * mm});
            skLineSegment(sketch, "E728", {"start": v(-203.78, 211.01) * mm, "end": v(-202.85, 211.9) * mm});
            skLineSegment(sketch, "E729", {"start": v(-202.85, 211.9) * mm, "end": v(-200.29, 214.3) * mm});
            skLineSegment(sketch, "E730", {"start": v(-200.29, 214.3) * mm, "end": v(-199.93, 214.64) * mm});
            skLineSegment(sketch, "E731", {"start": v(-199.93, 214.64) * mm, "end": v(-199.75, 214.8) * mm});
            skLineSegment(sketch, "E732", {"start": v(-199.75, 214.8) * mm, "end": v(-197.32, 217.15) * mm});
            skLineSegment(sketch, "E733", {"start": v(-197.32, 217.15) * mm, "end": v(-196.74, 217.71) * mm});
            skLineSegment(sketch, "E734", {"start": v(-196.74, 217.71) * mm, "end": v(-195.85, 218.6) * mm});
            skLineSegment(sketch, "E735", {"start": v(-195.85, 218.6) * mm, "end": v(-194.42, 220) * mm});
            skLineSegment(sketch, "E736", {"start": v(-194.42, 220) * mm, "end": v(-192.3, 222.07) * mm});
            skLineSegment(sketch, "E737", {"start": v(-192.3, 222.07) * mm, "end": v(-191.2, 223.15) * mm});
            skLineSegment(sketch, "E738", {"start": v(-191.2, 223.15) * mm, "end": v(-190.69, 223.66) * mm});
            skLineSegment(sketch, "E739", {"start": v(-190.69, 223.66) * mm, "end": v(-190.05, 224.37) * mm});
            skLineSegment(sketch, "E740", {"start": v(-190.05, 224.37) * mm, "end": v(-188.4, 226.01) * mm});
            skLineSegment(sketch, "E741", {"start": v(-188.4, 226.01) * mm, "end": v(-187.19, 227.24) * mm});
            skLineSegment(sketch, "E742", {"start": v(-187.19, 227.24) * mm, "end": v(-187.09, 227.34) * mm});
            skLineSegment(sketch, "E743", {"start": v(-187.09, 227.34) * mm, "end": v(-185.16, 229.21) * mm});
            skLineSegment(sketch, "E744", {"start": v(-185.16, 229.21) * mm, "end": v(-185.04, 229.33) * mm});
            skLineSegment(sketch, "E745", {"start": v(-185.04, 229.33) * mm, "end": v(-182.06, 232.2) * mm});
            skLineSegment(sketch, "E746", {"start": v(-182.06, 232.2) * mm, "end": v(-180.95, 233.26) * mm});
            skLineSegment(sketch, "E747", {"start": v(-180.95, 233.26) * mm, "end": v(-179.87, 234.33) * mm});
            skLineSegment(sketch, "E748", {"start": v(-179.87, 234.33) * mm, "end": v(-178.73, 235.42) * mm});
            skLineSegment(sketch, "E749", {"start": v(-178.73, 235.42) * mm, "end": v(-177.38, 236.76) * mm});
            skLineSegment(sketch, "E750", {"start": v(-177.38, 236.76) * mm, "end": v(-176.6, 237.5) * mm});
            skLineSegment(sketch, "E751", {"start": v(-176.6, 237.5) * mm, "end": v(-176.16, 238.14) * mm});
            skLineSegment(sketch, "E752", {"start": v(-176.16, 238.14) * mm, "end": v(-175.36, 239.27) * mm});
            skLineSegment(sketch, "E753", {"start": v(-175.36, 239.27) * mm, "end": v(-175.03, 239.98) * mm});
            skLineSegment(sketch, "E754", {"start": v(-175.03, 239.98) * mm, "end": v(-174.65, 240.74) * mm});
            skLineSegment(sketch, "E755", {"start": v(-174.65, 240.74) * mm, "end": v(-173.97, 241.8) * mm});
            skLineSegment(sketch, "E756", {"start": v(-173.97, 241.8) * mm, "end": v(-173.44, 242.7) * mm});
            skLineSegment(sketch, "E757", {"start": v(-173.44, 242.7) * mm, "end": v(-173.13, 243.1) * mm});
            skLineSegment(sketch, "E758", {"start": v(-173.13, 243.1) * mm, "end": v(-172.68, 243.53) * mm});
            skLineSegment(sketch, "E759", {"start": v(-172.68, 243.53) * mm, "end": v(-170.49, 245.61) * mm});
            skLineSegment(sketch, "E760", {"start": v(-170.49, 245.61) * mm, "end": v(-170.03, 246) * mm});
            skLineSegment(sketch, "E761", {"start": v(-170.03, 246) * mm, "end": v(-168.07, 247.25) * mm});
            skLineSegment(sketch, "E762", {"start": v(-168.07, 247.25) * mm, "end": v(-167.46, 247.6) * mm});
            skLineSegment(sketch, "E763", {"start": v(-167.46, 247.6) * mm, "end": v(-166.11, 248.39) * mm});
            skLineSegment(sketch, "E764", {"start": v(-166.11, 248.39) * mm, "end": v(-163.52, 250.64) * mm});
            skLineSegment(sketch, "E765", {"start": v(-163.52, 250.64) * mm, "end": v(-163.17, 250.95) * mm});
            skLineSegment(sketch, "E766", {"start": v(-163.17, 250.95) * mm, "end": v(-163.1, 251.02) * mm});
            skLineSegment(sketch, "E767", {"start": v(-163.1, 251.02) * mm, "end": v(-162.9, 251.23) * mm});
            skLineSegment(sketch, "E768", {"start": v(-162.9, 251.23) * mm, "end": v(-160.32, 253.91) * mm});
            skLineSegment(sketch, "E769", {"start": v(-160.32, 253.91) * mm, "end": v(-157.68, 256.63) * mm});
            skLineSegment(sketch, "E770", {"start": v(-157.68, 256.63) * mm, "end": v(-157.51, 256.78) * mm});
            skLineSegment(sketch, "E771", {"start": v(-157.51, 256.78) * mm, "end": v(-157.43, 256.86) * mm});
            skLineSegment(sketch, "E772", {"start": v(-157.43, 256.86) * mm, "end": v(-154.49, 259.8) * mm});
            skLineSegment(sketch, "E773", {"start": v(-154.49, 259.8) * mm, "end": v(-154.24, 260.06) * mm});
            skLineSegment(sketch, "E774", {"start": v(-154.24, 260.06) * mm, "end": v(-154.23, 260.07) * mm});
            skLineSegment(sketch, "E775", {"start": v(-154.23, 260.07) * mm, "end": v(-154.2, 260.09) * mm});
            skLineSegment(sketch, "E776", {"start": v(-154.2, 260.09) * mm, "end": v(-151.35, 262.72) * mm});
            skLineSegment(sketch, "E777", {"start": v(-151.35, 262.72) * mm, "end": v(-150.22, 263.86) * mm});
            skLineSegment(sketch, "E778", {"start": v(-150.22, 263.86) * mm, "end": v(-148.34, 265.78) * mm});
            skLineSegment(sketch, "E779", {"start": v(-148.34, 265.78) * mm, "end": v(-147.37, 266.73) * mm});
            skLineSegment(sketch, "E780", {"start": v(-147.37, 266.73) * mm, "end": v(-144.8, 269.3) * mm});
            skLineSegment(sketch, "E781", {"start": v(-144.8, 269.3) * mm, "end": v(-144.68, 269.43) * mm});
            skLineSegment(sketch, "E782", {"start": v(-144.68, 269.43) * mm, "end": v(-144.42, 269.68) * mm});
            skLineSegment(sketch, "E783", {"start": v(-144.42, 269.68) * mm, "end": v(-142.23, 271.68) * mm});
            skLineSegment(sketch, "E784", {"start": v(-142.23, 271.68) * mm, "end": v(-140.71, 273.06) * mm});
            skLineSegment(sketch, "E785", {"start": v(-140.71, 273.06) * mm, "end": v(-140.42, 273.3) * mm});
            skLineSegment(sketch, "E786", {"start": v(-140.42, 273.3) * mm, "end": v(-137.59, 275.6) * mm});
            skLineSegment(sketch, "E787", {"start": v(-137.59, 275.6) * mm, "end": v(-137.16, 275.93) * mm});
            skLineSegment(sketch, "E788", {"start": v(-137.16, 275.93) * mm, "end": v(-135.3, 277.26) * mm});
            skLineSegment(sketch, "E789", {"start": v(-135.3, 277.26) * mm, "end": v(-134.72, 277.66) * mm});
            skLineSegment(sketch, "E790", {"start": v(-134.72, 277.66) * mm, "end": v(-133.19, 278.73) * mm});
            skLineSegment(sketch, "E791", {"start": v(-133.19, 278.73) * mm, "end": v(-132.4, 279.25) * mm});
            skLineSegment(sketch, "E792", {"start": v(-132.4, 279.25) * mm, "end": v(-129.14, 281.2) * mm});
            skLineSegment(sketch, "E793", {"start": v(-129.14, 281.2) * mm, "end": v(-128.68, 281.47) * mm});
            skLineSegment(sketch, "E794", {"start": v(-128.68, 281.47) * mm, "end": v(-127.7, 282) * mm});
            skLineSegment(sketch, "E795", {"start": v(-127.7, 282) * mm, "end": v(-127.2, 282.24) * mm});
            skLineSegment(sketch, "E796", {"start": v(-127.2, 282.24) * mm, "end": v(-124.45, 283.57) * mm});
            skLineSegment(sketch, "E797", {"start": v(-124.45, 283.57) * mm, "end": v(-121.78, 284.74) * mm});
            skLineSegment(sketch, "E798", {"start": v(-121.78, 284.74) * mm, "end": v(-120.23, 285.4) * mm});
            skLineSegment(sketch, "E799", {"start": v(-120.23, 285.4) * mm, "end": v(-118.9, 285.93) * mm});
            skLineSegment(sketch, "E800", {"start": v(-118.9, 285.93) * mm, "end": v(-117.46, 286.44) * mm});
            skLineSegment(sketch, "E801", {"start": v(-117.46, 286.44) * mm, "end": v(-114.97, 287.27) * mm});
            skLineSegment(sketch, "E802", {"start": v(-114.97, 287.27) * mm, "end": v(-114.73, 287.35) * mm});
            skLineSegment(sketch, "E803", {"start": v(-114.73, 287.35) * mm, "end": v(-114.35, 287.47) * mm});
            skLineSegment(sketch, "E804", {"start": v(-114.35, 287.47) * mm, "end": v(-110.8, 288.54) * mm});
            skLineSegment(sketch, "E805", {"start": v(-110.8, 288.54) * mm, "end": v(-108.47, 289.18) * mm});
            skLineSegment(sketch, "E806", {"start": v(-108.47, 289.18) * mm, "end": v(-106.96, 289.56) * mm});
            skLineSegment(sketch, "E807", {"start": v(-106.96, 289.56) * mm, "end": v(-106.04, 289.77) * mm});
            skLineSegment(sketch, "E808", {"start": v(-106.04, 289.77) * mm, "end": v(-104.8, 290.12) * mm});
            skLineSegment(sketch, "E809", {"start": v(-104.8, 290.12) * mm, "end": v(-102.31, 290.71) * mm});
            skLineSegment(sketch, "E810", {"start": v(-102.31, 290.71) * mm, "end": v(-100.32, 291.17) * mm});
            skLineSegment(sketch, "E811", {"start": v(-100.32, 291.17) * mm, "end": v(-97.56, 291.8) * mm});
            skLineSegment(sketch, "E812", {"start": v(-97.56, 291.8) * mm, "end": v(-93.69, 292.76) * mm});
            skLineSegment(sketch, "E813", {"start": v(-93.69, 292.76) * mm, "end": v(-93.24, 292.86) * mm});
            skLineSegment(sketch, "E814", {"start": v(-93.24, 292.86) * mm, "end": v(-92.93, 292.92) * mm});
            skLineSegment(sketch, "E815", {"start": v(-92.93, 292.92) * mm, "end": v(-92.24, 293.08) * mm});
            skLineSegment(sketch, "E816", {"start": v(-92.24, 293.08) * mm, "end": v(-90.25, 293.49) * mm});
            skLineSegment(sketch, "E817", {"start": v(-90.25, 293.49) * mm, "end": v(-89.6, 293.63) * mm});
            skLineSegment(sketch, "E818", {"start": v(-89.6, 293.63) * mm, "end": v(-88.1, 293.97) * mm});
            skLineSegment(sketch, "E819", {"start": v(-88.1, 293.97) * mm, "end": v(-87.44, 294.1) * mm});
            skLineSegment(sketch, "E820", {"start": v(-87.44, 294.1) * mm, "end": v(-87.1, 294.16) * mm});
            skLineSegment(sketch, "E821", {"start": v(-87.1, 294.16) * mm, "end": v(-86.6, 294.27) * mm});
            skLineSegment(sketch, "E822", {"start": v(-86.6, 294.27) * mm, "end": v(-83.86, 294.8) * mm});
            skLineSegment(sketch, "E823", {"start": v(-83.86, 294.8) * mm, "end": v(-82.2, 295.08) * mm});
            skLineSegment(sketch, "E824", {"start": v(-82.2, 295.08) * mm, "end": v(-79.1, 295.74) * mm});
            skLineSegment(sketch, "E825", {"start": v(-79.1, 295.74) * mm, "end": v(-79.03, 295.75) * mm});
            skLineSegment(sketch, "E826", {"start": v(-79.03, 295.75) * mm, "end": v(-78.99, 295.76) * mm});
            skLineSegment(sketch, "E827", {"start": v(-78.99, 295.76) * mm, "end": v(-76.27, 296.2) * mm});
            skLineSegment(sketch, "E828", {"start": v(-76.27, 296.2) * mm, "end": v(-74.36, 296.55) * mm});
            skLineSegment(sketch, "E829", {"start": v(-74.36, 296.55) * mm, "end": v(-73.95, 296.62) * mm});
            skLineSegment(sketch, "E830", {"start": v(-73.95, 296.62) * mm, "end": v(-72.78, 296.83) * mm});
            skLineSegment(sketch, "E831", {"start": v(-72.78, 296.83) * mm, "end": v(-69.22, 297.4) * mm});
            skLineSegment(sketch, "E832", {"start": v(-69.22, 297.4) * mm, "end": v(-66.88, 297.78) * mm});
            skLineSegment(sketch, "E833", {"start": v(-66.88, 297.78) * mm, "end": v(-65.16, 298.07) * mm});
            skLineSegment(sketch, "E834", {"start": v(-65.16, 298.07) * mm, "end": v(-62.47, 298.48) * mm});
            skLineSegment(sketch, "E835", {"start": v(-62.47, 298.48) * mm, "end": v(-61.87, 298.54) * mm});
            skLineSegment(sketch, "E836", {"start": v(-61.87, 298.54) * mm, "end": v(-60.58, 298.73) * mm});
            skLineSegment(sketch, "E837", {"start": v(-60.58, 298.73) * mm, "end": v(-58.38, 299) * mm});
            skLineSegment(sketch, "E838", {"start": v(-58.38, 299) * mm, "end": v(-55.2, 299.38) * mm});
            skLineSegment(sketch, "E839", {"start": v(-55.2, 299.38) * mm, "end": v(-54.53, 299.45) * mm});
            skLineSegment(sketch, "E840", {"start": v(-54.53, 299.45) * mm, "end": v(-54.39, 299.46) * mm});
            skLineSegment(sketch, "E841", {"start": v(-54.39, 299.46) * mm, "end": v(-54, 299.52) * mm});
            skLineSegment(sketch, "E842", {"start": v(-54, 299.52) * mm, "end": v(-51.41, 299.78) * mm});
            skLineSegment(sketch, "E843", {"start": v(-51.41, 299.78) * mm, "end": v(-49.53, 300.03) * mm});
            skLineSegment(sketch, "E844", {"start": v(-49.53, 300.03) * mm, "end": v(-48.67, 300.1) * mm});
            skLineSegment(sketch, "E845", {"start": v(-48.67, 300.1) * mm, "end": v(-46.5, 300.38) * mm});
            skLineSegment(sketch, "E846", {"start": v(-46.5, 300.38) * mm, "end": v(-45.75, 300.45) * mm});
            skLineSegment(sketch, "E847", {"start": v(-45.75, 300.45) * mm, "end": v(-45.38, 300.48) * mm});
            skLineSegment(sketch, "E848", {"start": v(-45.38, 300.48) * mm, "end": v(-43.13, 300.57) * mm});
            skLineSegment(sketch, "E849", {"start": v(-43.13, 300.57) * mm, "end": v(-41.39, 300.8) * mm});
            skLineSegment(sketch, "E850", {"start": v(-41.39, 300.8) * mm, "end": v(-40.58, 300.86) * mm});
            skLineSegment(sketch, "E851", {"start": v(-40.58, 300.86) * mm, "end": v(-38.35, 301.04) * mm});
            skLineSegment(sketch, "E852", {"start": v(-38.35, 301.04) * mm, "end": v(-38.3, 301.04) * mm});
            skLineSegment(sketch, "E853", {"start": v(-38.3, 301.04) * mm, "end": v(-36.5, 301.1) * mm});
            skLineSegment(sketch, "E854", {"start": v(-36.5, 301.1) * mm, "end": v(-33.84, 301.4) * mm});
            skLineSegment(sketch, "E855", {"start": v(-33.84, 301.4) * mm, "end": v(-33.8, 301.4) * mm});
            skLineSegment(sketch, "E856", {"start": v(-33.8, 301.4) * mm, "end": v(-30.13, 301.63) * mm});
            skLineSegment(sketch, "E857", {"start": v(-30.13, 301.63) * mm, "end": v(-28.42, 301.7) * mm});
            skLineSegment(sketch, "E858", {"start": v(-28.42, 301.7) * mm, "end": v(-26.41, 301.77) * mm});
            skLineSegment(sketch, "E859", {"start": v(-26.41, 301.77) * mm, "end": v(-23.24, 301.91) * mm});
            skLineSegment(sketch, "E860", {"start": v(-23.24, 301.91) * mm, "end": v(-22.87, 301.93) * mm});
            skLineSegment(sketch, "E861", {"start": v(-22.87, 301.93) * mm, "end": v(-22.34, 301.94) * mm});
            skLineSegment(sketch, "E862", {"start": v(-22.34, 301.94) * mm, "end": v(-18.3, 302.03) * mm});
            skLineSegment(sketch, "E863", {"start": v(-18.3, 302.03) * mm, "end": v(-15.44, 302.08) * mm});
            skLineSegment(sketch, "E864", {"start": v(-15.44, 302.08) * mm, "end": v(-13.75, 302.07) * mm});
            skLineSegment(sketch, "E865", {"start": v(-13.75, 302.07) * mm, "end": v(-10.52, 302) * mm});
            skLineSegment(sketch, "E866", {"start": v(-10.52, 302) * mm, "end": v(-9.14, 302.03) * mm});
            skLineSegment(sketch, "E867", {"start": v(-9.14, 302.03) * mm, "end": v(-7.4, 302.04) * mm});
            skLineSegment(sketch, "E868", {"start": v(-7.4, 302.04) * mm, "end": v(-5.02, 302.02) * mm});
            skLineSegment(sketch, "E869", {"start": v(-5.02, 302.02) * mm, "end": v(-3.7, 302.02) * mm});
            skLineSegment(sketch, "E870", {"start": v(-3.7, 302.02) * mm, "end": v(-1.29, 302.08) * mm});
            skLineSegment(sketch, "E871", {"start": v(-1.29, 302.08) * mm, "end": v(-1.13, 302.09) * mm});
            skLineSegment(sketch, "E872", {"start": v(-1.13, 302.09) * mm, "end": v(-0.94, 302.13) * mm});
            skLineSegment(sketch, "E873", {"start": v(-0.94, 302.13) * mm, "end": v(0, 302.3) * mm});
            skLineSegment(sketch, "E874.0", {"start": v(3.9, 277.6) * mm, "end": v(4.57, 277.72) * mm});
            skLineSegment(sketch, "E874.1", {"start": v(1.69, 277.14) * mm, "end": v(3.9, 277.6) * mm});
            skLineSegment(sketch, "E874.2", {"start": v(-0.7, 277.09) * mm, "end": v(1.69, 277.14) * mm});
            skLineSegment(sketch, "E874.3", {"start": v(-3.35, 277.02) * mm, "end": v(-0.7, 277.09) * mm});
            skLineSegment(sketch, "E874.4", {"start": v(-5.15, 277.02) * mm, "end": v(-3.35, 277.02) * mm});
            skLineSegment(sketch, "E874.5", {"start": v(-7.42, 277.04) * mm, "end": v(-5.15, 277.02) * mm});
            skLineSegment(sketch, "E874.6", {"start": v(-8.72, 277.03) * mm, "end": v(-7.42, 277.04) * mm});
            skLineSegment(sketch, "E874.7", {"start": v(-10.5, 276.99) * mm, "end": v(-8.72, 277.03) * mm});
            skLineSegment(sketch, "E874.8", {"start": v(-14.1, 277.07) * mm, "end": v(-10.5, 276.99) * mm});
            skLineSegment(sketch, "E874.9", {"start": v(-15.31, 277.07) * mm, "end": v(-14.1, 277.07) * mm});
            skLineSegment(sketch, "E874.10", {"start": v(-17.83, 277.04) * mm, "end": v(-15.31, 277.07) * mm});
            skLineSegment(sketch, "E874.11", {"start": v(-21.81, 276.95) * mm, "end": v(-17.83, 277.04) * mm});
            skLineSegment(sketch, "E874.12", {"start": v(-22, 276.94) * mm, "end": v(-21.81, 276.95) * mm});
            skLineSegment(sketch, "E874.13", {"start": v(-22.03, 276.94) * mm, "end": v(-22, 276.94) * mm});
            skLineSegment(sketch, "E874.14", {"start": v(-25.45, 276.78) * mm, "end": v(-22.03, 276.94) * mm});
            skLineSegment(sketch, "E874.15", {"start": v(-27.52, 276.72) * mm, "end": v(-25.45, 276.78) * mm});
            skLineSegment(sketch, "E874.16", {"start": v(-28.83, 276.66) * mm, "end": v(-27.52, 276.72) * mm});
            skLineSegment(sketch, "E874.17", {"start": v(-31.68, 276.49) * mm, "end": v(-28.83, 276.66) * mm});
            skLineSegment(sketch, "E874.18", {"start": v(-34.65, 276.16) * mm, "end": v(-31.68, 276.49) * mm});
            skLineSegment(sketch, "E874.19", {"start": v(-36.81, 276.08) * mm, "end": v(-34.65, 276.16) * mm});
            skLineSegment(sketch, "E874.20", {"start": v(-38.72, 275.92) * mm, "end": v(-36.81, 276.08) * mm});
            skLineSegment(sketch, "E874.21", {"start": v(-38.91, 275.91) * mm, "end": v(-38.72, 275.92) * mm});
            skLineSegment(sketch, "E874.22", {"start": v(-41, 275.64) * mm, "end": v(-38.91, 275.91) * mm});
            skLineSegment(sketch, "E874.23", {"start": v(-43.8, 275.53) * mm, "end": v(-41, 275.64) * mm});
            skLineSegment(sketch, "E874.24", {"start": v(-43.8, 275.53) * mm, "end": v(-43.41, 275.56) * mm});
            skLineSegment(sketch, "E874.25", {"start": v(-43.7, 275.53) * mm, "end": v(-43.41, 275.56) * mm});
            skLineSegment(sketch, "E874.26", {"start": v(-46, 275.24) * mm, "end": v(-43.7, 275.53) * mm});
            skLineSegment(sketch, "E874.27", {"start": v(-46.8, 275.17) * mm, "end": v(-46, 275.24) * mm});
            skLineSegment(sketch, "E874.28", {"start": v(-48.53, 274.95) * mm, "end": v(-46.8, 275.17) * mm});
            skLineSegment(sketch, "E874.29", {"start": v(-51, 274.7) * mm, "end": v(-48.53, 274.95) * mm});
            skLineSegment(sketch, "E874.30", {"start": v(-51.17, 274.67) * mm, "end": v(-51, 274.7) * mm});
            skLineSegment(sketch, "E874.31", {"start": v(-51.82, 274.6) * mm, "end": v(-51.17, 274.67) * mm});
            skLineSegment(sketch, "E874.32", {"start": v(-52.49, 274.53) * mm, "end": v(-51.82, 274.6) * mm});
            skLineSegment(sketch, "E874.33", {"start": v(-55.4, 274.18) * mm, "end": v(-52.49, 274.53) * mm});
            skLineSegment(sketch, "E874.34", {"start": v(-57.28, 273.95) * mm, "end": v(-55.4, 274.18) * mm});
            skLineSegment(sketch, "E874.35", {"start": v(-58.64, 273.75) * mm, "end": v(-57.28, 273.95) * mm});
            skLineSegment(sketch, "E874.36", {"start": v(-59.18, 273.69) * mm, "end": v(-58.64, 273.75) * mm});
            skLineSegment(sketch, "E874.37", {"start": v(-61.25, 273.37) * mm, "end": v(-59.18, 273.69) * mm});
            skLineSegment(sketch, "E874.38", {"start": v(-62.87, 273.1) * mm, "end": v(-61.25, 273.37) * mm});
            skLineSegment(sketch, "E874.39", {"start": v(-65.24, 272.73) * mm, "end": v(-62.87, 273.1) * mm});
            skLineSegment(sketch, "E874.40", {"start": v(-68.57, 272.19) * mm, "end": v(-65.24, 272.73) * mm});
            skLineSegment(sketch, "E874.41", {"start": v(-69.6, 272) * mm, "end": v(-68.57, 272.19) * mm});
            skLineSegment(sketch, "E874.42", {"start": v(-69.93, 271.94) * mm, "end": v(-69.6, 272) * mm});
            skLineSegment(sketch, "E874.43", {"start": v(-72.02, 271.56) * mm, "end": v(-69.93, 271.94) * mm});
            skLineSegment(sketch, "E874.44", {"start": v(-74.28, 271.2) * mm, "end": v(-72.02, 271.56) * mm});
            skLineSegment(sketch, "E874.45", {"start": v(-74.28, 271.2) * mm, "end": v(-74.15, 271.22) * mm});
            skLineSegment(sketch, "E874.46", {"start": v(-74.35, 271.2) * mm, "end": v(-74.15, 271.22) * mm});
            skLineSegment(sketch, "E874.47", {"start": v(-77.46, 270.53) * mm, "end": v(-74.35, 271.2) * mm});
            skLineSegment(sketch, "E874.48", {"start": v(-79.38, 270.2) * mm, "end": v(-77.46, 270.53) * mm});
            skLineSegment(sketch, "E874.49", {"start": v(-81.56, 269.78) * mm, "end": v(-79.38, 270.2) * mm});
            skLineSegment(sketch, "E874.50", {"start": v(-81.98, 269.69) * mm, "end": v(-81.56, 269.78) * mm});
            skLineSegment(sketch, "E874.51", {"start": v(-82.68, 269.55) * mm, "end": v(-81.98, 269.69) * mm});
            skLineSegment(sketch, "E874.52", {"start": v(-83, 269.49) * mm, "end": v(-82.68, 269.55) * mm});
            skLineSegment(sketch, "E874.53", {"start": v(-84.26, 269.2) * mm, "end": v(-83, 269.49) * mm});
            skLineSegment(sketch, "E874.54", {"start": v(-85.16, 269.01) * mm, "end": v(-84.26, 269.2) * mm});
            skLineSegment(sketch, "E874.55", {"start": v(-86.94, 268.65) * mm, "end": v(-85.16, 269.01) * mm});
            skLineSegment(sketch, "E874.56", {"start": v(-87.4, 268.54) * mm, "end": v(-86.94, 268.65) * mm});
            skLineSegment(sketch, "E874.57", {"start": v(-87.98, 268.42) * mm, "end": v(-87.4, 268.54) * mm});
            skLineSegment(sketch, "E874.58", {"start": v(-88.14, 268.38) * mm, "end": v(-87.98, 268.42) * mm});
            skLineSegment(sketch, "E874.59", {"start": v(-91.76, 267.48) * mm, "end": v(-88.14, 268.38) * mm});
            skLineSegment(sketch, "E874.60", {"start": v(-94.74, 266.8) * mm, "end": v(-91.76, 267.48) * mm});
            skLineSegment(sketch, "E874.61", {"start": v(-96.6, 266.38) * mm, "end": v(-94.74, 266.8) * mm});
            skLineSegment(sketch, "E874.62", {"start": v(-98.55, 265.9) * mm, "end": v(-96.6, 266.38) * mm});
            skLineSegment(sketch, "E874.63", {"start": v(-99.88, 265.54) * mm, "end": v(-98.55, 265.9) * mm});
            skLineSegment(sketch, "E874.64", {"start": v(-101.05, 265.27) * mm, "end": v(-99.88, 265.54) * mm});
            skLineSegment(sketch, "E874.65", {"start": v(-102.07, 265) * mm, "end": v(-101.05, 265.27) * mm});
            skLineSegment(sketch, "E874.66", {"start": v(-103.9, 264.5) * mm, "end": v(-102.07, 265) * mm});
            skLineSegment(sketch, "E874.67", {"start": v(-107.1, 263.54) * mm, "end": v(-103.9, 264.5) * mm});
            skLineSegment(sketch, "E874.68", {"start": v(-107.19, 263.52) * mm, "end": v(-107.1, 263.54) * mm});
            skLineSegment(sketch, "E874.69", {"start": v(-107.19, 263.52) * mm, "end": v(-107.1, 263.55) * mm});
            skLineSegment(sketch, "E874.70", {"start": v(-109.3, 262.8) * mm, "end": v(-107.1, 263.55) * mm});
            skLineSegment(sketch, "E874.71", {"start": v(-110.15, 262.5) * mm, "end": v(-109.3, 262.8) * mm});
            skLineSegment(sketch, "E874.72", {"start": v(-110.7, 262.29) * mm, "end": v(-110.15, 262.5) * mm});
            skLineSegment(sketch, "E874.73", {"start": v(-111.81, 261.8) * mm, "end": v(-110.7, 262.29) * mm});
            skLineSegment(sketch, "E874.74", {"start": v(-114.02, 260.85) * mm, "end": v(-111.81, 261.8) * mm});
            skLineSegment(sketch, "E874.75", {"start": v(-116.03, 259.88) * mm, "end": v(-114.02, 260.85) * mm});
            skLineSegment(sketch, "E874.76", {"start": v(-116.1, 259.85) * mm, "end": v(-116.03, 259.88) * mm});
            skLineSegment(sketch, "E874.77", {"start": v(-116.66, 259.55) * mm, "end": v(-116.1, 259.85) * mm});
            skLineSegment(sketch, "E874.78", {"start": v(-116.66, 259.55) * mm, "end": v(-116.54, 259.61) * mm});
            skLineSegment(sketch, "E874.79", {"start": v(-118.99, 258.15) * mm, "end": v(-116.54, 259.61) * mm});
            skLineSegment(sketch, "E874.80", {"start": v(-119.08, 258.08) * mm, "end": v(-118.99, 258.15) * mm});
            skLineSegment(sketch, "E874.81", {"start": v(-120.37, 257.2) * mm, "end": v(-119.08, 258.08) * mm});
            skLineSegment(sketch, "E874.82", {"start": v(-120.78, 256.9) * mm, "end": v(-120.37, 257.2) * mm});
            skLineSegment(sketch, "E874.83", {"start": v(-122.35, 255.78) * mm, "end": v(-120.78, 256.9) * mm});
            skLineSegment(sketch, "E874.84", {"start": v(-122.35, 255.78) * mm, "end": v(-122.16, 255.92) * mm});
            skLineSegment(sketch, "E874.85", {"start": v(-124.71, 253.85) * mm, "end": v(-122.16, 255.92) * mm});
            skLineSegment(sketch, "E874.86", {"start": v(-124.71, 253.85) * mm, "end": v(-124.44, 254.07) * mm});
            skLineSegment(sketch, "E874.87", {"start": v(-125.36, 253.22) * mm, "end": v(-124.44, 254.07) * mm});
            skLineSegment(sketch, "E874.88", {"start": v(-127.42, 251.34) * mm, "end": v(-125.36, 253.22) * mm});
            skLineSegment(sketch, "E874.89", {"start": v(-127.42, 251.34) * mm, "end": v(-127.3, 251.46) * mm});
            skLineSegment(sketch, "E874.90", {"start": v(-127.3, 251.46) * mm, "end": v(-127.12, 251.63) * mm});
            skLineSegment(sketch, "E874.91", {"start": v(-260.89, 132.34) * mm, "end": v(-260.74, 132.45) * mm});
            skLineSegment(sketch, "E874.92", {"start": v(-263.3, 130.23) * mm, "end": v(-260.74, 132.45) * mm});
            skLineSegment(sketch, "E874.93", {"start": v(-263.3, 130.23) * mm, "end": v(-263.08, 130.43) * mm});
            skLineSegment(sketch, "E874.94", {"start": v(-266.38, 127.39) * mm, "end": v(-263.08, 130.43) * mm});
            skLineSegment(sketch, "E874.95", {"start": v(-267.54, 126.3) * mm, "end": v(-266.38, 127.39) * mm});
            skLineSegment(sketch, "E874.96", {"start": v(-267.74, 126.1) * mm, "end": v(-267.54, 126.3) * mm});
            skLineSegment(sketch, "E874.97", {"start": v(-269.2, 124.66) * mm, "end": v(-267.74, 126.1) * mm});
            skLineSegment(sketch, "E874.98", {"start": v(-271.35, 122.4) * mm, "end": v(-269.2, 124.66) * mm});
            skLineSegment(sketch, "E874.99", {"start": v(-271.84, 121.88) * mm, "end": v(-271.35, 122.4) * mm});
            skLineSegment(sketch, "E874.100", {"start": v(-273.55, 120.05) * mm, "end": v(-271.84, 121.88) * mm});
            skLineSegment(sketch, "E874.101", {"start": v(-274.59, 118.92) * mm, "end": v(-273.55, 120.05) * mm});
            skLineSegment(sketch, "E874.102", {"start": v(-275.11, 118.31) * mm, "end": v(-274.59, 118.92) * mm});
            skLineSegment(sketch, "E874.103", {"start": v(-275.4, 118) * mm, "end": v(-275.11, 118.31) * mm});
            skLineSegment(sketch, "E874.104", {"start": v(-276.98, 116) * mm, "end": v(-275.4, 118) * mm});
            skLineSegment(sketch, "E874.105", {"start": v(-278.1, 114.63) * mm, "end": v(-276.98, 116) * mm});
            skLineSegment(sketch, "E874.106", {"start": v(-279.24, 113.3) * mm, "end": v(-278.1, 114.63) * mm});
            skLineSegment(sketch, "E874.107", {"start": v(-280.57, 111.51) * mm, "end": v(-279.24, 113.3) * mm});
            skLineSegment(sketch, "E874.108", {"start": v(-280.87, 111.13) * mm, "end": v(-280.57, 111.51) * mm});
            skLineSegment(sketch, "E874.109", {"start": v(-282.6, 108.83) * mm, "end": v(-280.87, 111.13) * mm});
            skLineSegment(sketch, "E874.110", {"start": v(-282.66, 108.74) * mm, "end": v(-282.6, 108.83) * mm});
            skLineSegment(sketch, "E874.111", {"start": v(-282.87, 108.47) * mm, "end": v(-282.66, 108.74) * mm});
            skLineSegment(sketch, "E874.112", {"start": v(-284.13, 106.75) * mm, "end": v(-282.87, 108.47) * mm});
            skLineSegment(sketch, "E874.113", {"start": v(-284.44, 106.3) * mm, "end": v(-284.13, 106.75) * mm});
            skLineSegment(sketch, "E874.114", {"start": v(-285.19, 105.19) * mm, "end": v(-284.44, 106.3) * mm});
            skLineSegment(sketch, "E874.115", {"start": v(-286.04, 103.86) * mm, "end": v(-285.19, 105.19) * mm});
            skLineSegment(sketch, "E874.116", {"start": v(-286.75, 102.75) * mm, "end": v(-286.04, 103.86) * mm});
            skLineSegment(sketch, "E874.117", {"start": v(-287.35, 101.86) * mm, "end": v(-286.75, 102.75) * mm});
            skLineSegment(sketch, "E874.118", {"start": v(-287.65, 101.39) * mm, "end": v(-287.35, 101.86) * mm});
            skLineSegment(sketch, "E874.119", {"start": v(-288.52, 99.86) * mm, "end": v(-287.65, 101.39) * mm});
            skLineSegment(sketch, "E874.120", {"start": v(-289.2, 98.67) * mm, "end": v(-288.52, 99.86) * mm});
            skLineSegment(sketch, "E874.121", {"start": v(-291.05, 95.6) * mm, "end": v(-289.2, 98.67) * mm});
            skLineSegment(sketch, "E874.122", {"start": v(-291.05, 95.6) * mm, "end": v(-290.9, 95.86) * mm});
            skLineSegment(sketch, "E874.123", {"start": v(-290.98, 95.72) * mm, "end": v(-290.9, 95.86) * mm});
            skLineSegment(sketch, "E874.124", {"start": v(-292.26, 93.4) * mm, "end": v(-290.98, 95.72) * mm});
            skLineSegment(sketch, "E874.125", {"start": v(-292.26, 93.4) * mm, "end": v(-292.18, 93.54) * mm});
            skLineSegment(sketch, "E874.126", {"start": v(-292.64, 92.54) * mm, "end": v(-292.18, 93.54) * mm});
            skLineSegment(sketch, "E874.127", {"start": v(-293.34, 91.04) * mm, "end": v(-292.64, 92.54) * mm});
            skLineSegment(sketch, "E874.128", {"start": v(-293.72, 90.23) * mm, "end": v(-293.34, 91.04) * mm});
            skLineSegment(sketch, "E874.129", {"start": v(-294.63, 88.33) * mm, "end": v(-293.72, 90.23) * mm});
            skLineSegment(sketch, "E874.130", {"start": v(-294.83, 87.9) * mm, "end": v(-294.63, 88.33) * mm});
            skLineSegment(sketch, "E874.131", {"start": v(-296.7, 83.74) * mm, "end": v(-294.83, 87.9) * mm});
            skLineSegment(sketch, "E874.132", {"start": v(-296.72, 83.7) * mm, "end": v(-296.7, 83.74) * mm});
            skLineSegment(sketch, "E874.133", {"start": v(-296.76, 83.6) * mm, "end": v(-296.72, 83.7) * mm});
            skLineSegment(sketch, "E874.134", {"start": v(-298.18, 80.07) * mm, "end": v(-296.76, 83.6) * mm});
            skLineSegment(sketch, "E874.135", {"start": v(-298.43, 79.49) * mm, "end": v(-298.18, 80.07) * mm});
            skLineSegment(sketch, "E874.136", {"start": v(-298.48, 79.34) * mm, "end": v(-298.43, 79.49) * mm});
            skLineSegment(sketch, "E874.137", {"start": v(-299.18, 77.28) * mm, "end": v(-298.48, 79.34) * mm});
            skLineSegment(sketch, "E874.138", {"start": v(-299.7, 75.79) * mm, "end": v(-299.18, 77.28) * mm});
            skLineSegment(sketch, "E874.139", {"start": v(-301.13, 71.85) * mm, "end": v(-299.7, 75.79) * mm});
            skLineSegment(sketch, "E874.140", {"start": v(-301.2, 71.64) * mm, "end": v(-301.13, 71.85) * mm});
            skLineSegment(sketch, "E874.141", {"start": v(-307.23, 37.36) * mm, "end": v(-307.2, 38.1) * mm});
            skLineSegment(sketch, "E874.142", {"start": v(-307.32, 34.47) * mm, "end": v(-307.23, 37.36) * mm});
            skLineSegment(sketch, "E874.143", {"start": v(-307.42, 32.37) * mm, "end": v(-307.32, 34.47) * mm});
            skLineSegment(sketch, "E874.144", {"start": v(-307.44, 30.89) * mm, "end": v(-307.42, 32.37) * mm});
            skLineSegment(sketch, "E874.145", {"start": v(-307.49, 28.1) * mm, "end": v(-307.44, 30.89) * mm});
            skLineSegment(sketch, "E874.146", {"start": v(-307.5, 27.06) * mm, "end": v(-307.49, 28.1) * mm});
            skLineSegment(sketch, "E874.147", {"start": v(-307.44, 24.22) * mm, "end": v(-307.5, 27.06) * mm});
            skLineSegment(sketch, "E874.148", {"start": v(-307.5, 22.74) * mm, "end": v(-307.44, 24.22) * mm});
            skLineSegment(sketch, "E874.149", {"start": v(-307.48, 20.8) * mm, "end": v(-307.5, 22.74) * mm});
            skLineSegment(sketch, "E874.150", {"start": v(-307.4, 17.94) * mm, "end": v(-307.48, 20.8) * mm});
            skLineSegment(sketch, "E874.151", {"start": v(-307.34, 16.43) * mm, "end": v(-307.4, 17.94) * mm});
            skLineSegment(sketch, "E874.152", {"start": v(-307.26, 15.02) * mm, "end": v(-307.34, 16.43) * mm});
            skLineSegment(sketch, "E874.153", {"start": v(-306.04, 6.33) * mm, "end": v(-306.5, 8.68) * mm});
            skLineSegment(sketch, "E874.154", {"start": v(-305.86, 5.37) * mm, "end": v(-306.04, 6.33) * mm});
            skLineSegment(sketch, "E874.155", {"start": v(-305.65, 4.3) * mm, "end": v(-305.86, 5.37) * mm});
            skLineSegment(sketch, "E874.156", {"start": v(-305.48, 2.7) * mm, "end": v(-305.65, 4.3) * mm});
            skLineSegment(sketch, "E874.157", {"start": v(-306.5, 8.68) * mm, "end": v(-306.53, 8.77) * mm});
            skLineSegment(sketch, "E874.158", {"start": v(-306.48, 8.5) * mm, "end": v(-306.53, 8.77) * mm});
            skLineSegment(sketch, "E874.159", {"start": v(-306.48, 8.5) * mm, "end": v(-306.62, 9.4) * mm});
            skLineSegment(sketch, "E874.160", {"start": v(-306.62, 9.4) * mm, "end": v(-306.84, 10.85) * mm});
            skLineSegment(sketch, "E874.161", {"start": v(-306.84, 10.85) * mm, "end": v(-306.96, 12.1) * mm});
            skLineSegment(sketch, "E874.162", {"start": v(-306.96, 12.1) * mm, "end": v(-307.26, 15.02) * mm});
            skLineSegment(sketch, "E874.163", {"start": v(-307.2, 38.1) * mm, "end": v(-307.13, 39.08) * mm});
            skLineSegment(sketch, "E874.164", {"start": v(-307.13, 39.08) * mm, "end": v(-307.1, 39.62) * mm});
            skLineSegment(sketch, "E874.165", {"start": v(-307.1, 39.62) * mm, "end": v(-306.82, 41.45) * mm});
            skLineSegment(sketch, "E874.166", {"start": v(-306.82, 41.45) * mm, "end": v(-306.65, 43.16) * mm});
            skLineSegment(sketch, "E874.167", {"start": v(-306.65, 43.16) * mm, "end": v(-306.35, 46.22) * mm});
            skLineSegment(sketch, "E874.168", {"start": v(-306.35, 46.22) * mm, "end": v(-306.35, 46.23) * mm});
            skLineSegment(sketch, "E874.169", {"start": v(-306.35, 46.23) * mm, "end": v(-306.26, 47.07) * mm});
            skLineSegment(sketch, "E874.170", {"start": v(-306.26, 47.07) * mm, "end": v(-305.92, 49.94) * mm});
            skLineSegment(sketch, "E874.171", {"start": v(-305.92, 49.94) * mm, "end": v(-305.83, 50.66) * mm});
            skLineSegment(sketch, "E874.172", {"start": v(-305.83, 50.66) * mm, "end": v(-305.64, 51.92) * mm});
            skLineSegment(sketch, "E874.173", {"start": v(-305.64, 51.92) * mm, "end": v(-305.4, 53.49) * mm});
            skLineSegment(sketch, "E874.174", {"start": v(-305.4, 53.49) * mm, "end": v(-305.24, 54.5) * mm});
            skLineSegment(sketch, "E874.175", {"start": v(-305.24, 54.5) * mm, "end": v(-305.03, 55.65) * mm});
            skLineSegment(sketch, "E874.176", {"start": v(-305.03, 55.65) * mm, "end": v(-304.83, 56.86) * mm});
            skLineSegment(sketch, "E874.177", {"start": v(-304.83, 56.86) * mm, "end": v(-304.66, 57.7) * mm});
            skLineSegment(sketch, "E874.178", {"start": v(-304.66, 57.7) * mm, "end": v(-304.48, 58.64) * mm});
            skLineSegment(sketch, "E874.179", {"start": v(-304.48, 58.64) * mm, "end": v(-304.25, 59.7) * mm});
            skLineSegment(sketch, "E874.180", {"start": v(-304.25, 59.7) * mm, "end": v(-304, 60.7) * mm});
            skLineSegment(sketch, "E874.181", {"start": v(-304, 60.7) * mm, "end": v(-303.51, 62.9) * mm});
            skLineSegment(sketch, "E874.182", {"start": v(-303.51, 62.9) * mm, "end": v(-302.72, 66.4) * mm});
            skLineSegment(sketch, "E874.183", {"start": v(-302.72, 66.4) * mm, "end": v(-301.7, 69.8) * mm});
            skLineSegment(sketch, "E874.184", {"start": v(-301.7, 69.8) * mm, "end": v(-301.43, 70.8) * mm});
            skLineSegment(sketch, "E874.185", {"start": v(-301.43, 70.8) * mm, "end": v(-301.14, 71.81) * mm});
            skLineSegment(sketch, "E874.186", {"start": v(-301.2, 71.64) * mm, "end": v(-301.14, 71.81) * mm});
            skLineSegment(sketch, "E874.187", {"start": v(-260.89, 132.34) * mm, "end": v(-260.33, 132.78) * mm});
            skLineSegment(sketch, "E874.188", {"start": v(-260.33, 132.78) * mm, "end": v(-257.6, 134.92) * mm});
            skLineSegment(sketch, "E874.189", {"start": v(-257.6, 134.92) * mm, "end": v(-256.09, 136.12) * mm});
            skLineSegment(sketch, "E874.190", {"start": v(-256.09, 136.12) * mm, "end": v(-254.46, 137.4) * mm});
            skLineSegment(sketch, "E874.191", {"start": v(-254.46, 137.4) * mm, "end": v(-252.06, 139.17) * mm});
            skLineSegment(sketch, "E874.192", {"start": v(-252.06, 139.17) * mm, "end": v(-251.07, 139.89) * mm});
            skLineSegment(sketch, "E874.193", {"start": v(-251.07, 139.89) * mm, "end": v(-250.17, 140.57) * mm});
            skLineSegment(sketch, "E874.194", {"start": v(-250.17, 140.57) * mm, "end": v(-249.39, 141.14) * mm});
            skLineSegment(sketch, "E874.195", {"start": v(-249.39, 141.14) * mm, "end": v(-248.93, 141.43) * mm});
            skLineSegment(sketch, "E874.196", {"start": v(-248.93, 141.43) * mm, "end": v(-247.13, 142.7) * mm});
            skLineSegment(sketch, "E874.197", {"start": v(-247.97, 142.13) * mm, "end": v(-247.13, 142.7) * mm});
            skLineSegment(sketch, "E874.198", {"start": v(-247.97, 142.13) * mm, "end": v(-245.33, 143.56) * mm});
            skLineSegment(sketch, "E874.199", {"start": v(-245.33, 143.56) * mm, "end": v(-244.68, 144) * mm});
            skLineSegment(sketch, "E874.200", {"start": v(-244.68, 144) * mm, "end": v(-241.16, 146.13) * mm});
            skLineSegment(sketch, "E874.201", {"start": v(-241.16, 146.13) * mm, "end": v(-239.05, 147.69) * mm});
            skLineSegment(sketch, "E874.202", {"start": v(-239.05, 147.69) * mm, "end": v(-236.93, 149.55) * mm});
            skLineSegment(sketch, "E874.203", {"start": v(-236.93, 149.55) * mm, "end": v(-236.32, 149.99) * mm});
            skLineSegment(sketch, "E874.204", {"start": v(-236.32, 149.99) * mm, "end": v(-234.2, 151.5) * mm});
            skLineSegment(sketch, "E874.205", {"start": v(-234.2, 151.5) * mm, "end": v(-233.53, 151.97) * mm});
            skLineSegment(sketch, "E874.206", {"start": v(-233.53, 151.97) * mm, "end": v(-231.3, 153.6) * mm});
            skLineSegment(sketch, "E874.207", {"start": v(-231.3, 153.6) * mm, "end": v(-228.28, 155.63) * mm});
            skLineSegment(sketch, "E874.208", {"start": v(-228.28, 155.63) * mm, "end": v(-227.68, 156.04) * mm});
            skLineSegment(sketch, "E874.209", {"start": v(-227.68, 156.04) * mm, "end": v(-226.9, 156.61) * mm});
            skLineSegment(sketch, "E874.210", {"start": v(-226.9, 156.61) * mm, "end": v(-224.85, 158.19) * mm});
            skLineSegment(sketch, "E874.211", {"start": v(-224.85, 158.19) * mm, "end": v(-224, 158.78) * mm});
            skLineSegment(sketch, "E874.212", {"start": v(-224.08, 158.72) * mm, "end": v(-224, 158.78) * mm});
            skLineSegment(sketch, "E874.213", {"start": v(-224.08, 158.72) * mm, "end": v(-223.15, 159.2) * mm});
            skLineSegment(sketch, "E874.214", {"start": v(-223.15, 159.2) * mm, "end": v(-221.96, 159.9) * mm});
            skLineSegment(sketch, "E874.215", {"start": v(-221.96, 159.9) * mm, "end": v(-218.55, 161.92) * mm});
            skLineSegment(sketch, "E874.216", {"start": v(-218.55, 161.92) * mm, "end": v(-216.25, 163.9) * mm});
            skLineSegment(sketch, "E874.217", {"start": v(-216.25, 163.9) * mm, "end": v(-215.5, 164.6) * mm});
            skLineSegment(sketch, "E874.218", {"start": v(-215.5, 164.6) * mm, "end": v(-213.79, 166.21) * mm});
            skLineSegment(sketch, "E874.219", {"start": v(-213.79, 166.21) * mm, "end": v(-211.98, 167.96) * mm});
            skLineSegment(sketch, "E874.220", {"start": v(-211.98, 167.96) * mm, "end": v(-210.44, 169.5) * mm});
            skLineSegment(sketch, "E874.221", {"start": v(-210.44, 169.5) * mm, "end": v(-208.34, 171.56) * mm});
            skLineSegment(sketch, "E874.222", {"start": v(-208.34, 171.56) * mm, "end": v(-208.07, 171.83) * mm});
            skLineSegment(sketch, "E874.223", {"start": v(-208.07, 171.83) * mm, "end": v(-207.97, 171.92) * mm});
            skLineSegment(sketch, "E874.224", {"start": v(-207.97, 171.92) * mm, "end": v(-204.91, 174.74) * mm});
            skLineSegment(sketch, "E874.225", {"start": v(-204.91, 174.74) * mm, "end": v(-204.24, 175.37) * mm});
            skLineSegment(sketch, "E874.226", {"start": v(-204.24, 175.37) * mm, "end": v(-203.48, 176.14) * mm});
            skLineSegment(sketch, "E874.227", {"start": v(-203.48, 176.14) * mm, "end": v(-201.62, 178.06) * mm});
            skLineSegment(sketch, "E874.228", {"start": v(-201.62, 178.06) * mm, "end": v(-199.74, 179.94) * mm});
            skLineSegment(sketch, "E874.229", {"start": v(-199.74, 179.94) * mm, "end": v(-199.54, 180.14) * mm});
            skLineSegment(sketch, "E874.230", {"start": v(-199.54, 180.14) * mm, "end": v(-198.13, 181.51) * mm});
            skLineSegment(sketch, "E874.231", {"start": v(-198.13, 181.51) * mm, "end": v(-195.61, 183.95) * mm});
            skLineSegment(sketch, "E874.232", {"start": v(-195.61, 183.95) * mm, "end": v(-195.21, 184.34) * mm});
            skLineSegment(sketch, "E874.233", {"start": v(-195.21, 184.34) * mm, "end": v(-194.45, 185.1) * mm});
            skLineSegment(sketch, "E874.234", {"start": v(-194.45, 185.1) * mm, "end": v(-190.83, 188.63) * mm});
            skLineSegment(sketch, "E874.235", {"start": v(-190.83, 188.63) * mm, "end": v(-189.2, 190.24) * mm});
            skLineSegment(sketch, "E874.236", {"start": v(-189.2, 190.24) * mm, "end": v(-187.43, 191.92) * mm});
            skLineSegment(sketch, "E874.237", {"start": v(-187.43, 191.92) * mm, "end": v(-186.78, 192.63) * mm});
            skLineSegment(sketch, "E874.238", {"start": v(-186.78, 192.63) * mm, "end": v(-186.18, 193.26) * mm});
            skLineSegment(sketch, "E874.239", {"start": v(-186.18, 193.26) * mm, "end": v(-185.69, 193.72) * mm});
            skLineSegment(sketch, "E874.240", {"start": v(-185.69, 193.72) * mm, "end": v(-183.24, 196.01) * mm});
            skLineSegment(sketch, "E874.241", {"start": v(-183.24, 196.01) * mm, "end": v(-182.97, 196.26) * mm});
            skLineSegment(sketch, "E874.242", {"start": v(-182.97, 196.26) * mm, "end": v(-182.6, 196.6) * mm});
            skLineSegment(sketch, "E874.243", {"start": v(-182.6, 196.6) * mm, "end": v(-179.88, 199.24) * mm});
            skLineSegment(sketch, "E874.244", {"start": v(-179.88, 199.24) * mm, "end": v(-179.2, 199.9) * mm});
            skLineSegment(sketch, "E874.245", {"start": v(-179.2, 199.9) * mm, "end": v(-178.32, 200.77) * mm});
            skLineSegment(sketch, "E874.246", {"start": v(-178.32, 200.77) * mm, "end": v(-176.95, 202.12) * mm});
            skLineSegment(sketch, "E874.247", {"start": v(-176.95, 202.12) * mm, "end": v(-174.82, 204.2) * mm});
            skLineSegment(sketch, "E874.248", {"start": v(-174.82, 204.2) * mm, "end": v(-173.6, 205.38) * mm});
            skLineSegment(sketch, "E874.249", {"start": v(-173.6, 205.38) * mm, "end": v(-172.5, 206.5) * mm});
            skLineSegment(sketch, "E874.250", {"start": v(-172.5, 206.5) * mm, "end": v(-171.93, 207.13) * mm});
            skLineSegment(sketch, "E874.251", {"start": v(-171.93, 207.13) * mm, "end": v(-170.68, 208.37) * mm});
            skLineSegment(sketch, "E874.252", {"start": v(-170.68, 208.37) * mm, "end": v(-169.62, 209.45) * mm});
            skLineSegment(sketch, "E874.253", {"start": v(-169.74, 209.34) * mm, "end": v(-169.62, 209.45) * mm});
            skLineSegment(sketch, "E874.254", {"start": v(-169.74, 209.34) * mm, "end": v(-167.77, 211.25) * mm});
            skLineSegment(sketch, "E874.255", {"start": v(-167.77, 211.25) * mm, "end": v(-167.7, 211.31) * mm});
            skLineSegment(sketch, "E874.256", {"start": v(-167.7, 211.31) * mm, "end": v(-164.74, 214.17) * mm});
            skLineSegment(sketch, "E874.257", {"start": v(-164.74, 214.17) * mm, "end": v(-163.5, 215.36) * mm});
            skLineSegment(sketch, "E874.258", {"start": v(-163.5, 215.36) * mm, "end": v(-162.46, 216.4) * mm});
            skLineSegment(sketch, "E874.259", {"start": v(-162.46, 216.4) * mm, "end": v(-161.27, 217.52) * mm});
            skLineSegment(sketch, "E874.260", {"start": v(-161.27, 217.52) * mm, "end": v(-159.88, 218.9) * mm});
            skLineSegment(sketch, "E874.261", {"start": v(-159.88, 218.9) * mm, "end": v(-157.5, 221.2) * mm});
            skLineSegment(sketch, "E874.262", {"start": v(-157.5, 221.2) * mm, "end": v(-155.74, 223.72) * mm});
            skLineSegment(sketch, "E874.274", {"start": v(-151.46, 228) * mm, "end": v(-146.95, 231.92) * mm});
            skLineSegment(sketch, "E874.275", {"start": v(-146.95, 231.92) * mm, "end": v(-146.02, 232.76) * mm});
            skLineSegment(sketch, "E874.276", {"start": v(-146.02, 232.76) * mm, "end": v(-145.46, 233.3) * mm});
            skLineSegment(sketch, "E874.277", {"start": v(-145.46, 233.3) * mm, "end": v(-145.02, 233.75) * mm});
            skLineSegment(sketch, "E874.278", {"start": v(-145.02, 233.75) * mm, "end": v(-142.33, 236.55) * mm});
            skLineSegment(sketch, "E874.279", {"start": v(-142.33, 236.55) * mm, "end": v(-140.25, 238.69) * mm});
            skLineSegment(sketch, "E874.280", {"start": v(-140.32, 238.63) * mm, "end": v(-140.25, 238.69) * mm});
            skLineSegment(sketch, "E874.281", {"start": v(-140.32, 238.63) * mm, "end": v(-139.85, 239.1) * mm});
            skLineSegment(sketch, "E874.282", {"start": v(-139.85, 239.1) * mm, "end": v(-136.83, 242.1) * mm});
            skLineSegment(sketch, "E874.283", {"start": v(-136.94, 242) * mm, "end": v(-136.83, 242.1) * mm});
            skLineSegment(sketch, "E874.284", {"start": v(-136.94, 242) * mm, "end": v(-133.98, 244.72) * mm});
            skLineSegment(sketch, "E874.285", {"start": v(-133.98, 244.72) * mm, "end": v(-132.4, 246.33) * mm});
            skLineSegment(sketch, "E874.286", {"start": v(-132.4, 246.33) * mm, "end": v(-130.68, 248.08) * mm});
            skLineSegment(sketch, "E874.287", {"start": v(-130.68, 248.08) * mm, "end": v(-129.77, 248.96) * mm});
            skLineSegment(sketch, "E874.288", {"start": v(-129.77, 248.96) * mm, "end": v(-127.12, 251.63) * mm});
            skLineSegment(sketch, "E875.0", {"start": v(0.03, 297.22) * mm, "end": v(0.91, 297.38) * mm});
            skLineSegment(sketch, "E875.1", {"start": v(-0.57, 297.1) * mm, "end": v(0.03, 297.22) * mm});
            skLineSegment(sketch, "E875.2", {"start": v(-1.17, 297.08) * mm, "end": v(-0.57, 297.1) * mm});
            skLineSegment(sketch, "E875.3", {"start": v(-3.63, 297.02) * mm, "end": v(-1.17, 297.08) * mm});
            skLineSegment(sketch, "E875.4", {"start": v(-5.04, 297.02) * mm, "end": v(-3.63, 297.02) * mm});
            skLineSegment(sketch, "E875.5", {"start": v(-7.41, 297.04) * mm, "end": v(-5.04, 297.02) * mm});
            skLineSegment(sketch, "E875.6", {"start": v(-9.06, 297.03) * mm, "end": v(-7.41, 297.04) * mm});
            skLineSegment(sketch, "E875.7", {"start": v(-10.51, 297) * mm, "end": v(-9.06, 297.03) * mm});
            skLineSegment(sketch, "E875.8", {"start": v(-13.82, 297.07) * mm, "end": v(-10.51, 297) * mm});
            skLineSegment(sketch, "E875.9", {"start": v(-15.41, 297.08) * mm, "end": v(-13.82, 297.07) * mm});
            skLineSegment(sketch, "E875.10", {"start": v(-18.2, 297.03) * mm, "end": v(-15.41, 297.08) * mm});
            skLineSegment(sketch, "E875.11", {"start": v(-22.23, 296.94) * mm, "end": v(-18.2, 297.03) * mm});
            skLineSegment(sketch, "E875.12", {"start": v(-22.7, 296.93) * mm, "end": v(-22.23, 296.94) * mm});
            skLineSegment(sketch, "E875.13", {"start": v(-23, 296.92) * mm, "end": v(-22.7, 296.93) * mm});
            skLineSegment(sketch, "E875.14", {"start": v(-26.22, 296.77) * mm, "end": v(-23, 296.92) * mm});
            skLineSegment(sketch, "E875.15", {"start": v(-28.24, 296.7) * mm, "end": v(-26.22, 296.77) * mm});
            skLineSegment(sketch, "E875.16", {"start": v(-29.87, 296.64) * mm, "end": v(-28.24, 296.7) * mm});
            skLineSegment(sketch, "E875.17", {"start": v(-33.39, 296.42) * mm, "end": v(-29.87, 296.64) * mm});
            skLineSegment(sketch, "E875.18", {"start": v(-36.13, 296.12) * mm, "end": v(-33.39, 296.42) * mm});
            skLineSegment(sketch, "E875.19", {"start": v(-38, 296.05) * mm, "end": v(-36.13, 296.12) * mm});
            skLineSegment(sketch, "E875.20", {"start": v(-40.2, 295.87) * mm, "end": v(-38, 296.05) * mm});
            skLineSegment(sketch, "E875.21", {"start": v(-40.9, 295.82) * mm, "end": v(-40.2, 295.87) * mm});
            skLineSegment(sketch, "E875.22", {"start": v(-42.7, 295.59) * mm, "end": v(-40.9, 295.82) * mm});
            skLineSegment(sketch, "E875.23", {"start": v(-45.06, 295.5) * mm, "end": v(-42.7, 295.59) * mm});
            skLineSegment(sketch, "E875.24", {"start": v(-45.29, 295.47) * mm, "end": v(-45.06, 295.5) * mm});
            skLineSegment(sketch, "E875.25", {"start": v(-45.93, 295.4) * mm, "end": v(-45.29, 295.47) * mm});
            skLineSegment(sketch, "E875.26", {"start": v(-48.13, 295.13) * mm, "end": v(-45.93, 295.4) * mm});
            skLineSegment(sketch, "E875.27", {"start": v(-48.98, 295.06) * mm, "end": v(-48.13, 295.13) * mm});
            skLineSegment(sketch, "E875.28", {"start": v(-50.84, 294.82) * mm, "end": v(-48.98, 295.06) * mm});
            skLineSegment(sketch, "E875.29", {"start": v(-53.4, 294.55) * mm, "end": v(-50.84, 294.82) * mm});
            skLineSegment(sketch, "E875.30", {"start": v(-53.74, 294.5) * mm, "end": v(-53.4, 294.55) * mm});
            skLineSegment(sketch, "E875.31", {"start": v(-53.99, 294.48) * mm, "end": v(-53.74, 294.5) * mm});
            skLineSegment(sketch, "E875.32", {"start": v(-54.65, 294.41) * mm, "end": v(-53.99, 294.48) * mm});
            skLineSegment(sketch, "E875.33", {"start": v(-57.78, 294.03) * mm, "end": v(-54.65, 294.41) * mm});
            skLineSegment(sketch, "E875.34", {"start": v(-59.92, 293.78) * mm, "end": v(-57.78, 294.03) * mm});
            skLineSegment(sketch, "E875.35", {"start": v(-61.23, 293.59) * mm, "end": v(-59.92, 293.78) * mm});
            skLineSegment(sketch, "E875.36", {"start": v(-61.8, 293.52) * mm, "end": v(-61.23, 293.59) * mm});
            skLineSegment(sketch, "E875.37", {"start": v(-64.38, 293.13) * mm, "end": v(-61.8, 293.52) * mm});
            skLineSegment(sketch, "E875.38", {"start": v(-66.08, 292.85) * mm, "end": v(-64.38, 293.13) * mm});
            skLineSegment(sketch, "E875.39", {"start": v(-68.43, 292.47) * mm, "end": v(-66.08, 292.85) * mm});
            skLineSegment(sketch, "E875.40", {"start": v(-71.94, 291.9) * mm, "end": v(-68.43, 292.47) * mm});
            skLineSegment(sketch, "E875.41", {"start": v(-73.08, 291.7) * mm, "end": v(-71.94, 291.9) * mm});
            skLineSegment(sketch, "E875.42", {"start": v(-73.47, 291.63) * mm, "end": v(-73.08, 291.7) * mm});
            skLineSegment(sketch, "E875.43", {"start": v(-75.42, 291.27) * mm, "end": v(-73.47, 291.63) * mm});
            skLineSegment(sketch, "E875.44", {"start": v(-78.04, 290.85) * mm, "end": v(-75.42, 291.27) * mm});
            skLineSegment(sketch, "E875.45", {"start": v(-78.06, 290.85) * mm, "end": v(-78.04, 290.85) * mm});
            skLineSegment(sketch, "E875.46", {"start": v(-78.15, 290.83) * mm, "end": v(-78.06, 290.85) * mm});
            skLineSegment(sketch, "E875.47", {"start": v(-81.26, 290.17) * mm, "end": v(-78.15, 290.83) * mm});
            skLineSegment(sketch, "E875.48", {"start": v(-82.96, 289.87) * mm, "end": v(-81.26, 290.17) * mm});
            skLineSegment(sketch, "E875.49", {"start": v(-85.6, 289.37) * mm, "end": v(-82.96, 289.87) * mm});
            skLineSegment(sketch, "E875.50", {"start": v(-86.07, 289.27) * mm, "end": v(-85.6, 289.37) * mm});
            skLineSegment(sketch, "E875.51", {"start": v(-86.5, 289.18) * mm, "end": v(-86.07, 289.27) * mm});
            skLineSegment(sketch, "E875.52", {"start": v(-87.07, 289.07) * mm, "end": v(-86.5, 289.18) * mm});
            skLineSegment(sketch, "E875.53", {"start": v(-88.53, 288.74) * mm, "end": v(-87.07, 289.07) * mm});
            skLineSegment(sketch, "E875.54", {"start": v(-89.23, 288.6) * mm, "end": v(-88.53, 288.74) * mm});
            skLineSegment(sketch, "E875.55", {"start": v(-91.18, 288.2) * mm, "end": v(-89.23, 288.6) * mm});
            skLineSegment(sketch, "E875.56", {"start": v(-91.82, 288.05) * mm, "end": v(-91.18, 288.2) * mm});
            skLineSegment(sketch, "E875.57", {"start": v(-92.19, 287.97) * mm, "end": v(-91.82, 288.05) * mm});
            skLineSegment(sketch, "E875.58", {"start": v(-92.58, 287.89) * mm, "end": v(-92.19, 287.97) * mm});
            skLineSegment(sketch, "E875.59", {"start": v(-96.4, 286.94) * mm, "end": v(-92.58, 287.89) * mm});
            skLineSegment(sketch, "E875.60", {"start": v(-99.2, 286.3) * mm, "end": v(-96.4, 286.94) * mm});
            skLineSegment(sketch, "E875.61", {"start": v(-101.17, 285.85) * mm, "end": v(-99.2, 286.3) * mm});
            skLineSegment(sketch, "E875.62", {"start": v(-103.55, 285.27) * mm, "end": v(-101.17, 285.85) * mm});
            skLineSegment(sketch, "E875.63", {"start": v(-104.8, 284.93) * mm, "end": v(-103.55, 285.27) * mm});
            skLineSegment(sketch, "E875.64", {"start": v(-105.77, 284.7) * mm, "end": v(-104.8, 284.93) * mm});
            skLineSegment(sketch, "E875.65", {"start": v(-107.19, 284.34) * mm, "end": v(-105.77, 284.7) * mm});
            skLineSegment(sketch, "E875.66", {"start": v(-109.41, 283.73) * mm, "end": v(-107.19, 284.34) * mm});
            skLineSegment(sketch, "E875.67", {"start": v(-112.9, 282.69) * mm, "end": v(-109.41, 283.73) * mm});
            skLineSegment(sketch, "E875.68", {"start": v(-113.22, 282.59) * mm, "end": v(-112.9, 282.69) * mm});
            skLineSegment(sketch, "E875.69", {"start": v(-113.4, 282.53) * mm, "end": v(-113.22, 282.59) * mm});
            skLineSegment(sketch, "E875.70", {"start": v(-115.83, 281.71) * mm, "end": v(-113.4, 282.53) * mm});
            skLineSegment(sketch, "E875.71", {"start": v(-117.15, 281.25) * mm, "end": v(-115.83, 281.71) * mm});
            skLineSegment(sketch, "E875.72", {"start": v(-118.33, 280.78) * mm, "end": v(-117.15, 281.25) * mm});
            skLineSegment(sketch, "E875.73", {"start": v(-119.79, 280.15) * mm, "end": v(-118.33, 280.78) * mm});
            skLineSegment(sketch, "E875.74", {"start": v(-122.36, 279.03) * mm, "end": v(-119.79, 280.15) * mm});
            skLineSegment(sketch, "E875.75", {"start": v(-124.97, 277.77) * mm, "end": v(-122.36, 279.03) * mm});
            skLineSegment(sketch, "E875.76", {"start": v(-125.37, 277.56) * mm, "end": v(-124.97, 277.77) * mm});
            skLineSegment(sketch, "E875.77", {"start": v(-126.27, 277.09) * mm, "end": v(-125.37, 277.56) * mm});
            skLineSegment(sketch, "E875.78", {"start": v(-126.62, 276.9) * mm, "end": v(-126.27, 277.09) * mm});
            skLineSegment(sketch, "E875.79", {"start": v(-129.72, 275.03) * mm, "end": v(-126.62, 276.9) * mm});
            skLineSegment(sketch, "E875.80", {"start": v(-130.37, 274.6) * mm, "end": v(-129.72, 275.03) * mm});
            skLineSegment(sketch, "E875.81", {"start": v(-131.85, 273.57) * mm, "end": v(-130.37, 274.6) * mm});
            skLineSegment(sketch, "E875.82", {"start": v(-132.4, 273.19) * mm, "end": v(-131.85, 273.57) * mm});
            skLineSegment(sketch, "E875.83", {"start": v(-134.2, 271.9) * mm, "end": v(-132.4, 273.19) * mm});
            skLineSegment(sketch, "E875.84", {"start": v(-134.5, 271.67) * mm, "end": v(-134.2, 271.9) * mm});
            skLineSegment(sketch, "E875.85", {"start": v(-137.28, 269.41) * mm, "end": v(-134.5, 271.67) * mm});
            skLineSegment(sketch, "E875.86", {"start": v(-137.46, 269.26) * mm, "end": v(-137.28, 269.41) * mm});
            skLineSegment(sketch, "E875.87", {"start": v(-138.85, 267.99) * mm, "end": v(-137.46, 269.26) * mm});
            skLineSegment(sketch, "E875.88", {"start": v(-141.02, 266) * mm, "end": v(-138.85, 267.99) * mm});
            skLineSegment(sketch, "E875.89", {"start": v(-141.2, 265.84) * mm, "end": v(-141.02, 266) * mm});
            skLineSegment(sketch, "E875.90", {"start": v(-141.27, 265.77) * mm, "end": v(-141.2, 265.84) * mm});
            skLineSegment(sketch, "E875.91", {"start": v(-273.43, 147.92) * mm, "end": v(-273.3, 148.02) * mm});
            skLineSegment(sketch, "E875.92", {"start": v(-276.58, 145.2) * mm, "end": v(-273.43, 147.92) * mm});
            skLineSegment(sketch, "E875.93", {"start": v(-276.59, 145.18) * mm, "end": v(-276.58, 145.2) * mm});
            skLineSegment(sketch, "E875.94", {"start": v(-280.01, 142.02) * mm, "end": v(-276.59, 145.18) * mm});
            skLineSegment(sketch, "E875.95", {"start": v(-281.4, 140.72) * mm, "end": v(-280.01, 142.02) * mm});
            skLineSegment(sketch, "E875.96", {"start": v(-281.79, 140.34) * mm, "end": v(-281.4, 140.72) * mm});
            skLineSegment(sketch, "E875.97", {"start": v(-283.48, 138.66) * mm, "end": v(-281.79, 140.34) * mm});
            skLineSegment(sketch, "E875.98", {"start": v(-285.83, 136.2) * mm, "end": v(-283.48, 138.66) * mm});
            skLineSegment(sketch, "E875.99", {"start": v(-286.42, 135.57) * mm, "end": v(-285.83, 136.2) * mm});
            skLineSegment(sketch, "E875.100", {"start": v(-288.21, 133.65) * mm, "end": v(-286.42, 135.57) * mm});
            skLineSegment(sketch, "E875.101", {"start": v(-289.51, 132.24) * mm, "end": v(-288.21, 133.65) * mm});
            skLineSegment(sketch, "E875.102", {"start": v(-290.21, 131.43) * mm, "end": v(-289.51, 132.24) * mm});
            skLineSegment(sketch, "E875.103", {"start": v(-290.73, 130.84) * mm, "end": v(-290.21, 131.43) * mm});
            skLineSegment(sketch, "E875.104", {"start": v(-292.58, 128.52) * mm, "end": v(-290.73, 130.84) * mm});
            skLineSegment(sketch, "E875.105", {"start": v(-293.44, 127.46) * mm, "end": v(-292.58, 128.52) * mm});
            skLineSegment(sketch, "E875.106", {"start": v(-294.85, 125.83) * mm, "end": v(-293.44, 127.46) * mm});
            skLineSegment(sketch, "E875.107", {"start": v(-296.4, 123.73) * mm, "end": v(-294.85, 125.83) * mm});
            skLineSegment(sketch, "E875.108", {"start": v(-296.69, 123.39) * mm, "end": v(-296.4, 123.73) * mm});
            skLineSegment(sketch, "E875.109", {"start": v(-298.7, 120.7) * mm, "end": v(-296.69, 123.39) * mm});
            skLineSegment(sketch, "E875.110", {"start": v(-298.78, 120.58) * mm, "end": v(-298.7, 120.7) * mm});
            skLineSegment(sketch, "E875.111", {"start": v(-298.94, 120.37) * mm, "end": v(-298.78, 120.58) * mm});
            skLineSegment(sketch, "E875.112", {"start": v(-300.42, 118.37) * mm, "end": v(-298.94, 120.37) * mm});
            skLineSegment(sketch, "E875.113", {"start": v(-300.98, 117.55) * mm, "end": v(-300.42, 118.37) * mm});
            skLineSegment(sketch, "E875.114", {"start": v(-301.92, 116.16) * mm, "end": v(-300.98, 117.55) * mm});
            skLineSegment(sketch, "E875.115", {"start": v(-302.9, 114.6) * mm, "end": v(-301.92, 116.16) * mm});
            skLineSegment(sketch, "E875.116", {"start": v(-303.47, 113.72) * mm, "end": v(-302.9, 114.6) * mm});
            skLineSegment(sketch, "E875.117", {"start": v(-304.05, 112.86) * mm, "end": v(-303.47, 113.72) * mm});
            skLineSegment(sketch, "E875.118", {"start": v(-304.79, 111.71) * mm, "end": v(-304.05, 112.86) * mm});
            skLineSegment(sketch, "E875.119", {"start": v(-305.9, 109.76) * mm, "end": v(-304.79, 111.71) * mm});
            skLineSegment(sketch, "E875.120", {"start": v(-306.44, 108.8) * mm, "end": v(-305.9, 109.76) * mm});
            skLineSegment(sketch, "E875.121", {"start": v(-308.33, 105.67) * mm, "end": v(-306.44, 108.8) * mm});
            skLineSegment(sketch, "E875.122", {"start": v(-308.4, 105.56) * mm, "end": v(-308.33, 105.67) * mm});
            skLineSegment(sketch, "E875.123", {"start": v(-308.52, 105.34) * mm, "end": v(-308.4, 105.56) * mm});
            skLineSegment(sketch, "E875.124", {"start": v(-309.9, 102.82) * mm, "end": v(-308.52, 105.34) * mm});
            skLineSegment(sketch, "E875.125", {"start": v(-310.17, 102.3) * mm, "end": v(-309.9, 102.82) * mm});
            skLineSegment(sketch, "E875.126", {"start": v(-310.8, 100.94) * mm, "end": v(-310.17, 102.3) * mm});
            skLineSegment(sketch, "E875.127", {"start": v(-311.47, 99.5) * mm, "end": v(-310.8, 100.94) * mm});
            skLineSegment(sketch, "E875.128", {"start": v(-311.8, 98.78) * mm, "end": v(-311.47, 99.5) * mm});
            skLineSegment(sketch, "E875.129", {"start": v(-312.76, 96.79) * mm, "end": v(-311.8, 98.78) * mm});
            skLineSegment(sketch, "E875.130", {"start": v(-313.05, 96.14) * mm, "end": v(-312.76, 96.79) * mm});
            skLineSegment(sketch, "E875.131", {"start": v(-314.97, 91.89) * mm, "end": v(-313.05, 96.14) * mm});
            skLineSegment(sketch, "E875.132", {"start": v(-315.16, 91.45) * mm, "end": v(-314.97, 91.89) * mm});
            skLineSegment(sketch, "E875.133", {"start": v(-315.33, 91.05) * mm, "end": v(-315.16, 91.45) * mm});
            skLineSegment(sketch, "E875.134", {"start": v(-316.68, 87.68) * mm, "end": v(-315.33, 91.05) * mm});
            skLineSegment(sketch, "E875.135", {"start": v(-317.01, 86.88) * mm, "end": v(-316.68, 87.68) * mm});
            skLineSegment(sketch, "E875.136", {"start": v(-317.32, 86.05) * mm, "end": v(-317.01, 86.88) * mm});
            skLineSegment(sketch, "E875.137", {"start": v(-318.11, 83.73) * mm, "end": v(-317.32, 86.05) * mm});
            skLineSegment(sketch, "E875.138", {"start": v(-318.55, 82.45) * mm, "end": v(-318.11, 83.73) * mm});
            skLineSegment(sketch, "E875.139", {"start": v(-319.97, 78.56) * mm, "end": v(-318.55, 82.45) * mm});
            skLineSegment(sketch, "E875.140", {"start": v(-320.14, 78.07) * mm, "end": v(-319.97, 78.56) * mm});
            skLineSegment(sketch, "E875.141", {"start": v(-327.22, 38.11) * mm, "end": v(-327.17, 39.2) * mm});
            skLineSegment(sketch, "E875.142", {"start": v(-327.3, 35.23) * mm, "end": v(-327.22, 38.11) * mm});
            skLineSegment(sketch, "E875.143", {"start": v(-327.4, 32.96) * mm, "end": v(-327.3, 35.23) * mm});
            skLineSegment(sketch, "E875.144", {"start": v(-327.43, 31.2) * mm, "end": v(-327.4, 32.96) * mm});
            skLineSegment(sketch, "E875.145", {"start": v(-327.48, 28.36) * mm, "end": v(-327.43, 31.2) * mm});
            skLineSegment(sketch, "E875.146", {"start": v(-327.5, 26.94) * mm, "end": v(-327.48, 28.36) * mm});
            skLineSegment(sketch, "E875.147", {"start": v(-327.44, 24.42) * mm, "end": v(-327.5, 26.94) * mm});
            skLineSegment(sketch, "E875.148", {"start": v(-327.5, 23.06) * mm, "end": v(-327.44, 24.42) * mm});
            skLineSegment(sketch, "E875.149", {"start": v(-327.48, 20.45) * mm, "end": v(-327.5, 23.06) * mm});
            skLineSegment(sketch, "E875.150", {"start": v(-327.4, 17.24) * mm, "end": v(-327.48, 20.45) * mm});
            skLineSegment(sketch, "E875.151", {"start": v(-327.32, 15.47) * mm, "end": v(-327.4, 17.24) * mm});
            skLineSegment(sketch, "E875.152", {"start": v(-327.2, 13.45) * mm, "end": v(-327.32, 15.47) * mm});
            skLineSegment(sketch, "E875.153", {"start": v(-325.67, 2.48) * mm, "end": v(-326.11, 4.73) * mm});
            skLineSegment(sketch, "E875.154", {"start": v(-325.5, 1.62) * mm, "end": v(-325.67, 2.48) * mm});
            skLineSegment(sketch, "E875.155", {"start": v(-325.45, 1.36) * mm, "end": v(-325.5, 1.62) * mm});
            skLineSegment(sketch, "E875.156", {"start": v(-325.36, 0.54) * mm, "end": v(-325.45, 1.36) * mm});
            skLineSegment(sketch, "E875.157", {"start": v(-326.11, 4.73) * mm, "end": v(-326.2, 5.2) * mm});
            skLineSegment(sketch, "E875.158", {"start": v(-326.2, 5.2) * mm, "end": v(-326.24, 5.41) * mm});
            skLineSegment(sketch, "E875.159", {"start": v(-326.24, 5.41) * mm, "end": v(-326.4, 6.41) * mm});
            skLineSegment(sketch, "E875.160", {"start": v(-326.4, 6.41) * mm, "end": v(-326.7, 8.4) * mm});
            skLineSegment(sketch, "E875.161", {"start": v(-326.7, 8.4) * mm, "end": v(-326.86, 10.1) * mm});
            skLineSegment(sketch, "E875.162", {"start": v(-326.86, 10.1) * mm, "end": v(-327.2, 13.45) * mm});
            skLineSegment(sketch, "E875.163", {"start": v(-327.17, 39.2) * mm, "end": v(-327.08, 40.48) * mm});
            skLineSegment(sketch, "E875.164", {"start": v(-327.08, 40.48) * mm, "end": v(-326.99, 41.82) * mm});
            skLineSegment(sketch, "E875.165", {"start": v(-326.99, 41.82) * mm, "end": v(-326.67, 43.94) * mm});
            skLineSegment(sketch, "E875.166", {"start": v(-326.67, 43.94) * mm, "end": v(-326.55, 45.14) * mm});
            skLineSegment(sketch, "E875.167", {"start": v(-326.55, 45.14) * mm, "end": v(-326.23, 48.43) * mm});
            skLineSegment(sketch, "E875.168", {"start": v(-326.23, 48.43) * mm, "end": v(-326.22, 48.56) * mm});
            skLineSegment(sketch, "E875.169", {"start": v(-326.22, 48.56) * mm, "end": v(-326.13, 49.33) * mm});
            skLineSegment(sketch, "E875.170", {"start": v(-326.13, 49.33) * mm, "end": v(-325.78, 52.33) * mm});
            skLineSegment(sketch, "E875.171", {"start": v(-325.78, 52.33) * mm, "end": v(-325.65, 53.36) * mm});
            skLineSegment(sketch, "E875.172", {"start": v(-325.65, 53.36) * mm, "end": v(-325.41, 54.96) * mm});
            skLineSegment(sketch, "E875.173", {"start": v(-325.41, 54.96) * mm, "end": v(-325.16, 56.53) * mm});
            skLineSegment(sketch, "E875.174", {"start": v(-325.16, 56.53) * mm, "end": v(-324.97, 57.8) * mm});
            skLineSegment(sketch, "E875.175", {"start": v(-324.97, 57.8) * mm, "end": v(-324.73, 59.13) * mm});
            skLineSegment(sketch, "E875.176", {"start": v(-324.73, 59.13) * mm, "end": v(-324.5, 60.48) * mm});
            skLineSegment(sketch, "E875.177", {"start": v(-324.5, 60.48) * mm, "end": v(-324.28, 61.57) * mm});
            skLineSegment(sketch, "E875.178", {"start": v(-324.28, 61.57) * mm, "end": v(-324.07, 62.68) * mm});
            skLineSegment(sketch, "E875.179", {"start": v(-324.07, 62.68) * mm, "end": v(-323.74, 64.16) * mm});
            skLineSegment(sketch, "E875.180", {"start": v(-323.74, 64.16) * mm, "end": v(-323.5, 65.21) * mm});
            skLineSegment(sketch, "E875.181", {"start": v(-323.5, 65.21) * mm, "end": v(-323.02, 67.3) * mm});
            skLineSegment(sketch, "E875.182", {"start": v(-323.02, 67.3) * mm, "end": v(-322.08, 71.47) * mm});
            skLineSegment(sketch, "E875.183", {"start": v(-322.08, 71.47) * mm, "end": v(-320.93, 75.34) * mm});
            skLineSegment(sketch, "E875.184", {"start": v(-320.93, 75.34) * mm, "end": v(-320.69, 76.2) * mm});
            skLineSegment(sketch, "E875.185", {"start": v(-320.69, 76.2) * mm, "end": v(-320.27, 77.7) * mm});
            skLineSegment(sketch, "E875.186", {"start": v(-320.27, 77.7) * mm, "end": v(-320.14, 78.07) * mm});
            skLineSegment(sketch, "E875.187", {"start": v(-273.3, 148.02) * mm, "end": v(-272.77, 148.45) * mm});
            skLineSegment(sketch, "E875.188", {"start": v(-272.77, 148.45) * mm, "end": v(-269.97, 150.64) * mm});
            skLineSegment(sketch, "E875.189", {"start": v(-269.97, 150.64) * mm, "end": v(-268.48, 151.81) * mm});
            skLineSegment(sketch, "E875.190", {"start": v(-268.48, 151.81) * mm, "end": v(-266.6, 153.3) * mm});
            skLineSegment(sketch, "E875.191", {"start": v(-266.6, 153.3) * mm, "end": v(-263.85, 155.33) * mm});
            skLineSegment(sketch, "E875.192", {"start": v(-263.85, 155.33) * mm, "end": v(-262.95, 155.98) * mm});
            skLineSegment(sketch, "E875.193", {"start": v(-262.95, 155.98) * mm, "end": v(-262.11, 156.6) * mm});
            skLineSegment(sketch, "E875.194", {"start": v(-262.11, 156.6) * mm, "end": v(-260.67, 157.67) * mm});
            skLineSegment(sketch, "E875.195", {"start": v(-260.67, 157.67) * mm, "end": v(-260.04, 158.07) * mm});
            skLineSegment(sketch, "E875.196", {"start": v(-260.04, 158.07) * mm, "end": v(-258.42, 159.2) * mm});
            skLineSegment(sketch, "E875.197", {"start": v(-258.42, 159.2) * mm, "end": v(-258.28, 159.3) * mm});
            skLineSegment(sketch, "E875.198", {"start": v(-258.28, 159.3) * mm, "end": v(-255.7, 160.7) * mm});
            skLineSegment(sketch, "E875.199", {"start": v(-255.7, 160.7) * mm, "end": v(-255.47, 160.85) * mm});
            skLineSegment(sketch, "E875.200", {"start": v(-255.47, 160.85) * mm, "end": v(-252.3, 162.77) * mm});
            skLineSegment(sketch, "E875.201", {"start": v(-252.3, 162.77) * mm, "end": v(-251.6, 163.29) * mm});
            skLineSegment(sketch, "E875.202", {"start": v(-251.6, 163.29) * mm, "end": v(-249.4, 165.2) * mm});
            skLineSegment(sketch, "E875.203", {"start": v(-249.4, 165.2) * mm, "end": v(-247.94, 166.26) * mm});
            skLineSegment(sketch, "E875.204", {"start": v(-247.94, 166.26) * mm, "end": v(-245.8, 167.78) * mm});
            skLineSegment(sketch, "E875.205", {"start": v(-245.8, 167.78) * mm, "end": v(-245.25, 168.17) * mm});
            skLineSegment(sketch, "E875.206", {"start": v(-245.25, 168.17) * mm, "end": v(-242.79, 169.97) * mm});
            skLineSegment(sketch, "E875.207", {"start": v(-242.79, 169.97) * mm, "end": v(-239.5, 172.2) * mm});
            skLineSegment(sketch, "E875.208", {"start": v(-239.5, 172.2) * mm, "end": v(-239.25, 172.36) * mm});
            skLineSegment(sketch, "E875.209", {"start": v(-239.25, 172.36) * mm, "end": v(-238.94, 172.59) * mm});
            skLineSegment(sketch, "E875.210", {"start": v(-238.94, 172.59) * mm, "end": v(-236.64, 174.35) * mm});
            skLineSegment(sketch, "E875.211", {"start": v(-236.64, 174.35) * mm, "end": v(-235.6, 175.07) * mm});
            skLineSegment(sketch, "E875.212", {"start": v(-235.6, 175.07) * mm, "end": v(-234.68, 175.75) * mm});
            skLineSegment(sketch, "E875.213", {"start": v(-234.68, 175.75) * mm, "end": v(-232.81, 176.72) * mm});
            skLineSegment(sketch, "E875.214", {"start": v(-232.81, 176.72) * mm, "end": v(-232.08, 177.15) * mm});
            skLineSegment(sketch, "E875.215", {"start": v(-232.08, 177.15) * mm, "end": v(-230.26, 178.23) * mm});
            skLineSegment(sketch, "E875.216", {"start": v(-230.26, 178.23) * mm, "end": v(-229.62, 178.78) * mm});
            skLineSegment(sketch, "E875.217", {"start": v(-229.62, 178.78) * mm, "end": v(-229.2, 179.17) * mm});
            skLineSegment(sketch, "E875.218", {"start": v(-229.2, 179.17) * mm, "end": v(-227.58, 180.7) * mm});
            skLineSegment(sketch, "E875.219", {"start": v(-227.58, 180.7) * mm, "end": v(-226, 182.23) * mm});
            skLineSegment(sketch, "E875.220", {"start": v(-226, 182.23) * mm, "end": v(-224.53, 183.7) * mm});
            skLineSegment(sketch, "E875.221", {"start": v(-224.53, 183.7) * mm, "end": v(-222.38, 185.8) * mm});
            skLineSegment(sketch, "E875.222", {"start": v(-222.38, 185.8) * mm, "end": v(-221.94, 186.24) * mm});
            skLineSegment(sketch, "E875.223", {"start": v(-221.94, 186.24) * mm, "end": v(-221.59, 186.57) * mm});
            skLineSegment(sketch, "E875.224", {"start": v(-221.59, 186.57) * mm, "end": v(-218.52, 189.4) * mm});
            skLineSegment(sketch, "E875.225", {"start": v(-218.52, 189.4) * mm, "end": v(-218.21, 189.68) * mm});
            skLineSegment(sketch, "E875.226", {"start": v(-218.21, 189.68) * mm, "end": v(-217.8, 190.1) * mm});
            skLineSegment(sketch, "E875.227", {"start": v(-217.8, 190.1) * mm, "end": v(-215.88, 192.1) * mm});
            skLineSegment(sketch, "E875.228", {"start": v(-215.88, 192.1) * mm, "end": v(-213.8, 194.16) * mm});
            skLineSegment(sketch, "E875.229", {"start": v(-213.8, 194.16) * mm, "end": v(-213.52, 194.44) * mm});
            skLineSegment(sketch, "E875.230", {"start": v(-213.52, 194.44) * mm, "end": v(-212.07, 195.85) * mm});
            skLineSegment(sketch, "E875.231", {"start": v(-212.07, 195.85) * mm, "end": v(-209.55, 198.3) * mm});
            skLineSegment(sketch, "E875.232", {"start": v(-209.55, 198.3) * mm, "end": v(-209.28, 198.56) * mm});
            skLineSegment(sketch, "E875.233", {"start": v(-209.28, 198.56) * mm, "end": v(-208.52, 199.33) * mm});
            skLineSegment(sketch, "E875.234", {"start": v(-208.52, 199.33) * mm, "end": v(-204.82, 202.92) * mm});
            skLineSegment(sketch, "E875.235", {"start": v(-204.82, 202.92) * mm, "end": v(-203.1, 204.61) * mm});
            skLineSegment(sketch, "E875.236", {"start": v(-203.1, 204.61) * mm, "end": v(-201.75, 205.9) * mm});
            skLineSegment(sketch, "E875.237", {"start": v(-201.75, 205.9) * mm, "end": v(-201.37, 206.32) * mm});
            skLineSegment(sketch, "E875.238", {"start": v(-201.37, 206.32) * mm, "end": v(-200.26, 207.46) * mm});
            skLineSegment(sketch, "E875.239", {"start": v(-200.26, 207.46) * mm, "end": v(-199.42, 208.26) * mm});
            skLineSegment(sketch, "E875.240", {"start": v(-199.42, 208.26) * mm, "end": v(-196.88, 210.64) * mm});
            skLineSegment(sketch, "E875.241", {"start": v(-196.88, 210.64) * mm, "end": v(-196.54, 210.96) * mm});
            skLineSegment(sketch, "E875.242", {"start": v(-196.54, 210.96) * mm, "end": v(-196.32, 211.16) * mm});
            skLineSegment(sketch, "E875.243", {"start": v(-196.32, 211.16) * mm, "end": v(-193.83, 213.57) * mm});
            skLineSegment(sketch, "E875.244", {"start": v(-193.83, 213.57) * mm, "end": v(-193.23, 214.15) * mm});
            skLineSegment(sketch, "E875.245", {"start": v(-193.23, 214.15) * mm, "end": v(-192.35, 215.04) * mm});
            skLineSegment(sketch, "E875.246", {"start": v(-192.35, 215.04) * mm, "end": v(-190.92, 216.42) * mm});
            skLineSegment(sketch, "E875.247", {"start": v(-190.92, 216.42) * mm, "end": v(-188.8, 218.5) * mm});
            skLineSegment(sketch, "E875.248", {"start": v(-188.8, 218.5) * mm, "end": v(-187.68, 219.6) * mm});
            skLineSegment(sketch, "E875.249", {"start": v(-187.68, 219.6) * mm, "end": v(-187.05, 220.23) * mm});
            skLineSegment(sketch, "E875.250", {"start": v(-187.05, 220.23) * mm, "end": v(-186.43, 220.92) * mm});
            skLineSegment(sketch, "E875.251", {"start": v(-186.43, 220.92) * mm, "end": v(-184.85, 222.48) * mm});
            skLineSegment(sketch, "E875.252", {"start": v(-184.85, 222.48) * mm, "end": v(-183.68, 223.68) * mm});
            skLineSegment(sketch, "E875.253", {"start": v(-183.68, 223.68) * mm, "end": v(-183.62, 223.74) * mm});
            skLineSegment(sketch, "E875.254", {"start": v(-183.62, 223.74) * mm, "end": v(-181.68, 225.62) * mm});
            skLineSegment(sketch, "E875.255", {"start": v(-181.68, 225.62) * mm, "end": v(-181.57, 225.73) * mm});
            skLineSegment(sketch, "E875.256", {"start": v(-181.57, 225.73) * mm, "end": v(-178.6, 228.6) * mm});
            skLineSegment(sketch, "E875.257", {"start": v(-178.6, 228.6) * mm, "end": v(-177.46, 229.68) * mm});
            skLineSegment(sketch, "E875.258", {"start": v(-177.46, 229.68) * mm, "end": v(-176.39, 230.74) * mm});
            skLineSegment(sketch, "E875.259", {"start": v(-176.39, 230.74) * mm, "end": v(-175.23, 231.84) * mm});
            skLineSegment(sketch, "E875.260", {"start": v(-175.23, 231.84) * mm, "end": v(-173.88, 233.2) * mm});
            skLineSegment(sketch, "E875.261", {"start": v(-173.88, 233.2) * mm, "end": v(-172.78, 234.25) * mm});
            skLineSegment(sketch, "E875.262", {"start": v(-172.78, 234.25) * mm, "end": v(-172.08, 235.26) * mm});
            skLineSegment(sketch, "E875.263", {"start": v(-172.08, 235.26) * mm, "end": v(-171.01, 236.74) * mm});
            skLineSegment(sketch, "E875.264", {"start": v(-171.01, 236.74) * mm, "end": v(-170.52, 237.82) * mm});
            skLineSegment(sketch, "E875.265", {"start": v(-170.52, 237.82) * mm, "end": v(-170.3, 238.27) * mm});
            skLineSegment(sketch, "E875.266", {"start": v(-170.3, 238.27) * mm, "end": v(-169.7, 239.2) * mm});
            skLineSegment(sketch, "E875.267", {"start": v(-169.7, 239.2) * mm, "end": v(-169.35, 239.8) * mm});
            skLineSegment(sketch, "E875.268", {"start": v(-169.35, 239.8) * mm, "end": v(-169.23, 239.91) * mm});
            skLineSegment(sketch, "E875.269", {"start": v(-169.23, 239.91) * mm, "end": v(-167.14, 241.9) * mm});
            skLineSegment(sketch, "E875.270", {"start": v(-167.14, 241.9) * mm, "end": v(-167.05, 241.97) * mm});
            skLineSegment(sketch, "E875.271", {"start": v(-167.05, 241.97) * mm, "end": v(-165.5, 242.96) * mm});
            skLineSegment(sketch, "E875.272", {"start": v(-165.5, 242.96) * mm, "end": v(-164.95, 243.27) * mm});
            skLineSegment(sketch, "E875.273", {"start": v(-164.95, 243.27) * mm, "end": v(-163.18, 244.3) * mm});
            skLineSegment(sketch, "E875.274", {"start": v(-163.18, 244.3) * mm, "end": v(-160.2, 246.9) * mm});
            skLineSegment(sketch, "E875.275", {"start": v(-160.2, 246.9) * mm, "end": v(-159.74, 247.31) * mm});
            skLineSegment(sketch, "E875.276", {"start": v(-159.74, 247.31) * mm, "end": v(-159.57, 247.48) * mm});
            skLineSegment(sketch, "E875.277", {"start": v(-159.57, 247.48) * mm, "end": v(-159.32, 247.73) * mm});
            skLineSegment(sketch, "E875.278", {"start": v(-159.32, 247.73) * mm, "end": v(-156.72, 250.44) * mm});
            skLineSegment(sketch, "E875.279", {"start": v(-156.72, 250.44) * mm, "end": v(-154.2, 253.04) * mm});
            skLineSegment(sketch, "E875.280", {"start": v(-154.2, 253.04) * mm, "end": v(-154.08, 253.15) * mm});
            skLineSegment(sketch, "E875.281", {"start": v(-154.08, 253.15) * mm, "end": v(-153.92, 253.3) * mm});
            skLineSegment(sketch, "E875.282", {"start": v(-153.92, 253.3) * mm, "end": v(-150.96, 256.27) * mm});
            skLineSegment(sketch, "E875.283", {"start": v(-150.96, 256.27) * mm, "end": v(-150.76, 256.46) * mm});
            skLineSegment(sketch, "E875.284", {"start": v(-150.76, 256.46) * mm, "end": v(-147.88, 259.12) * mm});
            skLineSegment(sketch, "E875.285", {"start": v(-147.88, 259.12) * mm, "end": v(-146.65, 260.36) * mm});
            skLineSegment(sketch, "E875.286", {"start": v(-146.65, 260.36) * mm, "end": v(-144.8, 262.24) * mm});
            skLineSegment(sketch, "E875.287", {"start": v(-144.8, 262.24) * mm, "end": v(-143.85, 263.18) * mm});
            skLineSegment(sketch, "E875.288", {"start": v(-143.85, 263.18) * mm, "end": v(-141.27, 265.77) * mm});
            skLineSegment(sketch, "E876", {"start": v(0.91, 297.38) * mm, "end": v(4.57, 277.72) * mm});
            skLineSegment(sketch, "E877", {"start": v(-325.36, 0.54) * mm, "end": v(-305.48, 2.7) * mm});
            skLineSegment(sketch, "E878", {"start": v(-151.46, 228) * mm, "end": v(-155.74, 223.72) * mm});
            skSolve(sketch);
        }
        {
            var Q0;
            Q0=qCreatedBy(id+"F2.planeOp",FACE);
            cPlane(context, id + "F6", {"entities" : qUnion([Q0]), "cplaneType" : CPlaneType.OFFSET, "offset" : 74 * mm, "oppositeDirection" : true, "width" : 150 * mm, "height" : 150 * mm});
        }
        {
            var Q0;
            Q0=qCreatedBy(id+"F6.planeOp",FACE);
            var sketch = newSketch(context, id + "F7", { "sketchPlane" : qUnion([Q0])});
            skPoint(sketch, "E879", {"position": v(0, 0) * mm});
            skLineSegment(sketch, "E880", {"start": v(-330.33, 0) * mm, "end": v(-330.4, 0.62) * mm});
            skLineSegment(sketch, "E881", {"start": v(-330.4, 0.62) * mm, "end": v(-330.41, 0.68) * mm});
            skLineSegment(sketch, "E882", {"start": v(-330.41, 0.68) * mm, "end": v(-330.57, 1.52) * mm});
            skLineSegment(sketch, "E883", {"start": v(-330.57, 1.52) * mm, "end": v(-331.02, 3.75) * mm});
            skLineSegment(sketch, "E884", {"start": v(-331.02, 3.75) * mm, "end": v(-331.13, 4.3) * mm});
            skLineSegment(sketch, "E885", {"start": v(-331.13, 4.3) * mm, "end": v(-331.18, 4.64) * mm});
            skLineSegment(sketch, "E886", {"start": v(-331.18, 4.64) * mm, "end": v(-331.34, 5.66) * mm});
            skLineSegment(sketch, "E887", {"start": v(-331.34, 5.66) * mm, "end": v(-331.66, 7.8) * mm});
            skLineSegment(sketch, "E888", {"start": v(-331.66, 7.8) * mm, "end": v(-331.83, 9.6) * mm});
            skLineSegment(sketch, "E889", {"start": v(-331.83, 9.6) * mm, "end": v(-332.2, 13.06) * mm});
            skLineSegment(sketch, "E890", {"start": v(-332.2, 13.06) * mm, "end": v(-332.3, 15.23) * mm});
            skLineSegment(sketch, "E891", {"start": v(-332.3, 15.23) * mm, "end": v(-332.39, 17.06) * mm});
            skLineSegment(sketch, "E892", {"start": v(-332.39, 17.06) * mm, "end": v(-332.48, 20.37) * mm});
            skLineSegment(sketch, "E893", {"start": v(-332.48, 20.37) * mm, "end": v(-332.5, 23.14) * mm});
            skLineSegment(sketch, "E894", {"start": v(-332.5, 23.14) * mm, "end": v(-332.45, 24.46) * mm});
            skLineSegment(sketch, "E895", {"start": v(-332.45, 24.46) * mm, "end": v(-332.5, 26.9) * mm});
            skLineSegment(sketch, "E896", {"start": v(-332.5, 26.9) * mm, "end": v(-332.48, 28.42) * mm});
            skLineSegment(sketch, "E897", {"start": v(-332.48, 28.42) * mm, "end": v(-332.43, 31.28) * mm});
            skLineSegment(sketch, "E898", {"start": v(-332.43, 31.28) * mm, "end": v(-332.4, 33.1) * mm});
            skLineSegment(sketch, "E899", {"start": v(-332.4, 33.1) * mm, "end": v(-332.3, 35.42) * mm});
            skLineSegment(sketch, "E900", {"start": v(-332.3, 35.42) * mm, "end": v(-332.21, 38.3) * mm});
            skLineSegment(sketch, "E901", {"start": v(-332.21, 38.3) * mm, "end": v(-332.16, 39.48) * mm});
            skLineSegment(sketch, "E902", {"start": v(-332.16, 39.48) * mm, "end": v(-332.07, 40.83) * mm});
            skLineSegment(sketch, "E903", {"start": v(-332.07, 40.83) * mm, "end": v(-331.96, 42.37) * mm});
            skLineSegment(sketch, "E904", {"start": v(-331.96, 42.37) * mm, "end": v(-331.63, 44.56) * mm});
            skLineSegment(sketch, "E905", {"start": v(-331.63, 44.56) * mm, "end": v(-331.52, 45.63) * mm});
            skLineSegment(sketch, "E906", {"start": v(-331.52, 45.63) * mm, "end": v(-331.2, 48.98) * mm});
            skLineSegment(sketch, "E907", {"start": v(-331.2, 48.98) * mm, "end": v(-331.18, 49.14) * mm});
            skLineSegment(sketch, "E908", {"start": v(-331.18, 49.14) * mm, "end": v(-331.1, 49.9) * mm});
            skLineSegment(sketch, "E909", {"start": v(-331.1, 49.9) * mm, "end": v(-330.74, 52.93) * mm});
            skLineSegment(sketch, "E910", {"start": v(-330.74, 52.93) * mm, "end": v(-330.6, 54.03) * mm});
            skLineSegment(sketch, "E911", {"start": v(-330.6, 54.03) * mm, "end": v(-330.35, 55.72) * mm});
            skLineSegment(sketch, "E912", {"start": v(-330.35, 55.72) * mm, "end": v(-330.1, 57.29) * mm});
            skLineSegment(sketch, "E913", {"start": v(-330.1, 57.29) * mm, "end": v(-329.9, 58.63) * mm});
            skLineSegment(sketch, "E914", {"start": v(-329.9, 58.63) * mm, "end": v(-329.65, 60) * mm});
            skLineSegment(sketch, "E915", {"start": v(-329.65, 60) * mm, "end": v(-329.42, 61.38) * mm});
            skLineSegment(sketch, "E916", {"start": v(-329.42, 61.38) * mm, "end": v(-329.19, 62.53) * mm});
            skLineSegment(sketch, "E917", {"start": v(-329.19, 62.53) * mm, "end": v(-328.96, 63.69) * mm});
            skLineSegment(sketch, "E918", {"start": v(-328.96, 63.69) * mm, "end": v(-328.62, 65.28) * mm});
            skLineSegment(sketch, "E919", {"start": v(-328.62, 65.28) * mm, "end": v(-328.36, 66.35) * mm});
            skLineSegment(sketch, "E920", {"start": v(-328.36, 66.35) * mm, "end": v(-327.9, 68.4) * mm});
            skLineSegment(sketch, "E921", {"start": v(-327.9, 68.4) * mm, "end": v(-326.94, 72.62) * mm});
            skLineSegment(sketch, "E922", {"start": v(-326.94, 72.62) * mm, "end": v(-326.91, 72.74) * mm});
            skLineSegment(sketch, "E923", {"start": v(-326.91, 72.74) * mm, "end": v(-326.9, 72.78) * mm});
            skLineSegment(sketch, "E924", {"start": v(-326.9, 72.78) * mm, "end": v(-325.73, 76.72) * mm});
            skLineSegment(sketch, "E925", {"start": v(-325.73, 76.72) * mm, "end": v(-325.5, 77.56) * mm});
            skLineSegment(sketch, "E926", {"start": v(-325.5, 77.56) * mm, "end": v(-325.05, 79.16) * mm});
            skLineSegment(sketch, "E927", {"start": v(-325.05, 79.16) * mm, "end": v(-324.87, 79.68) * mm});
            skLineSegment(sketch, "E928", {"start": v(-324.87, 79.68) * mm, "end": v(-324.68, 80.24) * mm});
            skLineSegment(sketch, "E929", {"start": v(-324.68, 80.24) * mm, "end": v(-323.26, 84.12) * mm});
            skLineSegment(sketch, "E930", {"start": v(-323.26, 84.12) * mm, "end": v(-322.85, 85.34) * mm});
            skLineSegment(sketch, "E931", {"start": v(-322.85, 85.34) * mm, "end": v(-322.04, 87.73) * mm});
            skLineSegment(sketch, "E932", {"start": v(-322.04, 87.73) * mm, "end": v(-321.66, 88.73) * mm});
            skLineSegment(sketch, "E933", {"start": v(-321.66, 88.73) * mm, "end": v(-321.3, 89.59) * mm});
            skLineSegment(sketch, "E934", {"start": v(-321.3, 89.59) * mm, "end": v(-319.97, 92.9) * mm});
            skLineSegment(sketch, "E935", {"start": v(-319.97, 92.9) * mm, "end": v(-319.77, 93.4) * mm});
            skLineSegment(sketch, "E936", {"start": v(-319.77, 93.4) * mm, "end": v(-319.54, 93.93) * mm});
            skLineSegment(sketch, "E937", {"start": v(-319.54, 93.93) * mm, "end": v(-317.6, 98.2) * mm});
            skLineSegment(sketch, "E938", {"start": v(-317.6, 98.2) * mm, "end": v(-317.3, 98.9) * mm});
            skLineSegment(sketch, "E939", {"start": v(-317.3, 98.9) * mm, "end": v(-316.33, 100.91) * mm});
            skLineSegment(sketch, "E940", {"start": v(-316.33, 100.91) * mm, "end": v(-316, 101.61) * mm});
            skLineSegment(sketch, "E941", {"start": v(-316, 101.61) * mm, "end": v(-315.34, 103.03) * mm});
            skLineSegment(sketch, "E942", {"start": v(-315.34, 103.03) * mm, "end": v(-314.66, 104.5) * mm});
            skLineSegment(sketch, "E943", {"start": v(-314.66, 104.5) * mm, "end": v(-314.31, 105.18) * mm});
            skLineSegment(sketch, "E944", {"start": v(-314.31, 105.18) * mm, "end": v(-312.9, 107.75) * mm});
            skLineSegment(sketch, "E945", {"start": v(-312.9, 107.75) * mm, "end": v(-312.77, 107.98) * mm});
            skLineSegment(sketch, "E946", {"start": v(-312.77, 107.98) * mm, "end": v(-312.65, 108.2) * mm});
            skLineSegment(sketch, "E947", {"start": v(-312.65, 108.2) * mm, "end": v(-310.75, 111.34) * mm});
            skLineSegment(sketch, "E948", {"start": v(-310.75, 111.34) * mm, "end": v(-310.24, 112.24) * mm});
            skLineSegment(sketch, "E949", {"start": v(-310.24, 112.24) * mm, "end": v(-309.07, 114.3) * mm});
            skLineSegment(sketch, "E950", {"start": v(-309.07, 114.3) * mm, "end": v(-308.23, 115.61) * mm});
            skLineSegment(sketch, "E951", {"start": v(-308.23, 115.61) * mm, "end": v(-307.65, 116.46) * mm});
            skLineSegment(sketch, "E952", {"start": v(-307.65, 116.46) * mm, "end": v(-307.12, 117.3) * mm});
            skLineSegment(sketch, "E953", {"start": v(-307.12, 117.3) * mm, "end": v(-306.1, 118.9) * mm});
            skLineSegment(sketch, "E954", {"start": v(-306.1, 118.9) * mm, "end": v(-305.12, 120.36) * mm});
            skLineSegment(sketch, "E955", {"start": v(-305.12, 120.36) * mm, "end": v(-304.49, 121.27) * mm});
            skLineSegment(sketch, "E956", {"start": v(-304.49, 121.27) * mm, "end": v(-302.96, 123.35) * mm});
            skLineSegment(sketch, "E957", {"start": v(-302.96, 123.35) * mm, "end": v(-302.81, 123.54) * mm});
            skLineSegment(sketch, "E958", {"start": v(-302.81, 123.54) * mm, "end": v(-302.72, 123.66) * mm});
            skLineSegment(sketch, "E959", {"start": v(-302.72, 123.66) * mm, "end": v(-300.64, 126.45) * mm});
            skLineSegment(sketch, "E960", {"start": v(-300.64, 126.45) * mm, "end": v(-300.37, 126.79) * mm});
            skLineSegment(sketch, "E961", {"start": v(-300.37, 126.79) * mm, "end": v(-298.75, 128.97) * mm});
            skLineSegment(sketch, "E962", {"start": v(-298.75, 128.97) * mm, "end": v(-297.27, 130.67) * mm});
            skLineSegment(sketch, "E963", {"start": v(-297.27, 130.67) * mm, "end": v(-296.48, 131.65) * mm});
            skLineSegment(sketch, "E964", {"start": v(-296.48, 131.65) * mm, "end": v(-294.56, 134.05) * mm});
            skLineSegment(sketch, "E965", {"start": v(-294.56, 134.05) * mm, "end": v(-293.99, 134.7) * mm});
            skLineSegment(sketch, "E966", {"start": v(-293.99, 134.7) * mm, "end": v(-293.25, 135.57) * mm});
            skLineSegment(sketch, "E967", {"start": v(-293.25, 135.57) * mm, "end": v(-291.88, 137.05) * mm});
            skLineSegment(sketch, "E968", {"start": v(-291.88, 137.05) * mm, "end": v(-290.07, 139) * mm});
            skLineSegment(sketch, "E969", {"start": v(-290.07, 139) * mm, "end": v(-289.45, 139.64) * mm});
            skLineSegment(sketch, "E970", {"start": v(-289.45, 139.64) * mm, "end": v(-287.05, 142.16) * mm});
            skLineSegment(sketch, "E971", {"start": v(-287.05, 142.16) * mm, "end": v(-285.3, 143.9) * mm});
            skLineSegment(sketch, "E972", {"start": v(-285.3, 143.9) * mm, "end": v(-284.85, 144.33) * mm});
            skLineSegment(sketch, "E973", {"start": v(-284.85, 144.33) * mm, "end": v(-283.42, 145.68) * mm});
            skLineSegment(sketch, "E974", {"start": v(-283.42, 145.68) * mm, "end": v(-279.97, 148.87) * mm});
            skLineSegment(sketch, "E975", {"start": v(-279.97, 148.87) * mm, "end": v(-279.93, 148.9) * mm});
            skLineSegment(sketch, "E976", {"start": v(-279.93, 148.9) * mm, "end": v(-279.91, 148.92) * mm});
            skLineSegment(sketch, "E977", {"start": v(-279.91, 148.92) * mm, "end": v(-276.6, 151.78) * mm});
            skLineSegment(sketch, "E978", {"start": v(-276.6, 151.78) * mm, "end": v(-276.4, 151.94) * mm});
            skLineSegment(sketch, "E979", {"start": v(-276.4, 151.94) * mm, "end": v(-275.88, 152.37) * mm});
            skLineSegment(sketch, "E980", {"start": v(-275.88, 152.37) * mm, "end": v(-273.06, 154.57) * mm});
            skLineSegment(sketch, "E981", {"start": v(-273.06, 154.57) * mm, "end": v(-271.58, 155.74) * mm});
            skLineSegment(sketch, "E982", {"start": v(-271.58, 155.74) * mm, "end": v(-269.62, 157.28) * mm});
            skLineSegment(sketch, "E983", {"start": v(-269.62, 157.28) * mm, "end": v(-266.8, 159.37) * mm});
            skLineSegment(sketch, "E984", {"start": v(-266.8, 159.37) * mm, "end": v(-265.92, 160) * mm});
            skLineSegment(sketch, "E985", {"start": v(-265.92, 160) * mm, "end": v(-265.1, 160.62) * mm});
            skLineSegment(sketch, "E986", {"start": v(-265.1, 160.62) * mm, "end": v(-263.49, 161.8) * mm});
            skLineSegment(sketch, "E987", {"start": v(-263.49, 161.8) * mm, "end": v(-262.81, 162.23) * mm});
            skLineSegment(sketch, "E988", {"start": v(-262.81, 162.23) * mm, "end": v(-261.25, 163.33) * mm});
            skLineSegment(sketch, "E989", {"start": v(-261.25, 163.33) * mm, "end": v(-260.86, 163.6) * mm});
            skLineSegment(sketch, "E990", {"start": v(-260.86, 163.6) * mm, "end": v(-258.3, 164.97) * mm});
            skLineSegment(sketch, "E991", {"start": v(-258.3, 164.97) * mm, "end": v(-258.17, 165.06) * mm});
            skLineSegment(sketch, "E992", {"start": v(-258.17, 165.06) * mm, "end": v(-255.08, 166.93) * mm});
            skLineSegment(sketch, "E993", {"start": v(-255.08, 166.93) * mm, "end": v(-254.73, 167.19) * mm});
            skLineSegment(sketch, "E994", {"start": v(-254.73, 167.19) * mm, "end": v(-252.52, 169.13) * mm});
            skLineSegment(sketch, "E995", {"start": v(-252.52, 169.13) * mm, "end": v(-252.51, 169.13) * mm});
            skLineSegment(sketch, "E996", {"start": v(-252.51, 169.13) * mm, "end": v(-250.85, 170.33) * mm});
            skLineSegment(sketch, "E997", {"start": v(-250.85, 170.33) * mm, "end": v(-248.7, 171.85) * mm});
            skLineSegment(sketch, "E998", {"start": v(-248.7, 171.85) * mm, "end": v(-248.19, 172.22) * mm});
            skLineSegment(sketch, "E999", {"start": v(-248.19, 172.22) * mm, "end": v(-245.66, 174.06) * mm});
            skLineSegment(sketch, "E1000", {"start": v(-245.66, 174.06) * mm, "end": v(-242.3, 176.33) * mm});
            skLineSegment(sketch, "E1001", {"start": v(-242.3, 176.33) * mm, "end": v(-242.15, 176.44) * mm});
            skLineSegment(sketch, "E1002", {"start": v(-242.15, 176.44) * mm, "end": v(-241.95, 176.58) * mm});
            skLineSegment(sketch, "E1003", {"start": v(-241.95, 176.58) * mm, "end": v(-239.58, 178.4) * mm});
            skLineSegment(sketch, "E1004", {"start": v(-239.58, 178.4) * mm, "end": v(-238.5, 179.14) * mm});
            skLineSegment(sketch, "E1005", {"start": v(-238.5, 179.14) * mm, "end": v(-237.33, 180) * mm});
            skLineSegment(sketch, "E1006", {"start": v(-237.33, 180) * mm, "end": v(-235.23, 181.1) * mm});
            skLineSegment(sketch, "E1007", {"start": v(-235.23, 181.1) * mm, "end": v(-234.62, 181.46) * mm});
            skLineSegment(sketch, "E1008", {"start": v(-234.62, 181.46) * mm, "end": v(-233.19, 182.3) * mm});
            skLineSegment(sketch, "E1009", {"start": v(-233.19, 182.3) * mm, "end": v(-232.96, 182.5) * mm});
            skLineSegment(sketch, "E1010", {"start": v(-232.96, 182.5) * mm, "end": v(-232.63, 182.81) * mm});
            skLineSegment(sketch, "E1011", {"start": v(-232.63, 182.81) * mm, "end": v(-231.03, 184.31) * mm});
            skLineSegment(sketch, "E1012", {"start": v(-231.03, 184.31) * mm, "end": v(-229.5, 185.8) * mm});
            skLineSegment(sketch, "E1013", {"start": v(-229.5, 185.8) * mm, "end": v(-228.05, 187.24) * mm});
            skLineSegment(sketch, "E1014", {"start": v(-228.05, 187.24) * mm, "end": v(-225.89, 189.37) * mm});
            skLineSegment(sketch, "E1015", {"start": v(-225.89, 189.37) * mm, "end": v(-225.4, 189.85) * mm});
            skLineSegment(sketch, "E1016", {"start": v(-225.4, 189.85) * mm, "end": v(-225, 190.24) * mm});
            skLineSegment(sketch, "E1017", {"start": v(-225, 190.24) * mm, "end": v(-221.92, 193.06) * mm});
            skLineSegment(sketch, "E1018", {"start": v(-221.92, 193.06) * mm, "end": v(-221.7, 193.26) * mm});
            skLineSegment(sketch, "E1019", {"start": v(-221.7, 193.26) * mm, "end": v(-221.39, 193.58) * mm});
            skLineSegment(sketch, "E1020", {"start": v(-221.39, 193.58) * mm, "end": v(-219.45, 195.6) * mm});
            skLineSegment(sketch, "E1021", {"start": v(-219.45, 195.6) * mm, "end": v(-217.32, 197.72) * mm});
            skLineSegment(sketch, "E1022", {"start": v(-217.32, 197.72) * mm, "end": v(-217.02, 198.01) * mm});
            skLineSegment(sketch, "E1023", {"start": v(-217.02, 198.01) * mm, "end": v(-215.55, 199.44) * mm});
            skLineSegment(sketch, "E1024", {"start": v(-215.55, 199.44) * mm, "end": v(-213.04, 201.88) * mm});
            skLineSegment(sketch, "E1025", {"start": v(-213.04, 201.88) * mm, "end": v(-212.8, 202.11) * mm});
            skLineSegment(sketch, "E1026", {"start": v(-212.8, 202.11) * mm, "end": v(-212.03, 202.88) * mm});
            skLineSegment(sketch, "E1027", {"start": v(-212.03, 202.88) * mm, "end": v(-208.32, 206.5) * mm});
            skLineSegment(sketch, "E1028", {"start": v(-208.32, 206.5) * mm, "end": v(-206.58, 208.2) * mm});
            skLineSegment(sketch, "E1029", {"start": v(-206.58, 208.2) * mm, "end": v(-205.32, 209.4) * mm});
            skLineSegment(sketch, "E1030", {"start": v(-205.32, 209.4) * mm, "end": v(-205.02, 209.74) * mm});
            skLineSegment(sketch, "E1031", {"start": v(-205.02, 209.74) * mm, "end": v(-203.78, 211.01) * mm});
            skLineSegment(sketch, "E1032", {"start": v(-203.78, 211.01) * mm, "end": v(-202.85, 211.9) * mm});
            skLineSegment(sketch, "E1033", {"start": v(-202.85, 211.9) * mm, "end": v(-200.29, 214.3) * mm});
            skLineSegment(sketch, "E1034", {"start": v(-200.29, 214.3) * mm, "end": v(-199.93, 214.64) * mm});
            skLineSegment(sketch, "E1035", {"start": v(-199.93, 214.64) * mm, "end": v(-199.75, 214.8) * mm});
            skLineSegment(sketch, "E1036", {"start": v(-199.75, 214.8) * mm, "end": v(-197.32, 217.15) * mm});
            skLineSegment(sketch, "E1037", {"start": v(-197.32, 217.15) * mm, "end": v(-196.74, 217.71) * mm});
            skLineSegment(sketch, "E1038", {"start": v(-196.74, 217.71) * mm, "end": v(-195.85, 218.6) * mm});
            skLineSegment(sketch, "E1039", {"start": v(-195.85, 218.6) * mm, "end": v(-194.42, 220) * mm});
            skLineSegment(sketch, "E1040", {"start": v(-194.42, 220) * mm, "end": v(-192.3, 222.07) * mm});
            skLineSegment(sketch, "E1041", {"start": v(-192.3, 222.07) * mm, "end": v(-191.2, 223.15) * mm});
            skLineSegment(sketch, "E1042", {"start": v(-191.2, 223.15) * mm, "end": v(-190.69, 223.66) * mm});
            skLineSegment(sketch, "E1043", {"start": v(-190.69, 223.66) * mm, "end": v(-190.05, 224.37) * mm});
            skLineSegment(sketch, "E1044", {"start": v(-190.05, 224.37) * mm, "end": v(-188.4, 226.01) * mm});
            skLineSegment(sketch, "E1045", {"start": v(-188.4, 226.01) * mm, "end": v(-187.19, 227.24) * mm});
            skLineSegment(sketch, "E1046", {"start": v(-187.19, 227.24) * mm, "end": v(-187.09, 227.34) * mm});
            skLineSegment(sketch, "E1047", {"start": v(-187.09, 227.34) * mm, "end": v(-185.16, 229.21) * mm});
            skLineSegment(sketch, "E1048", {"start": v(-185.16, 229.21) * mm, "end": v(-185.04, 229.33) * mm});
            skLineSegment(sketch, "E1049", {"start": v(-185.04, 229.33) * mm, "end": v(-182.06, 232.2) * mm});
            skLineSegment(sketch, "E1050", {"start": v(-182.06, 232.2) * mm, "end": v(-180.95, 233.26) * mm});
            skLineSegment(sketch, "E1051", {"start": v(-180.95, 233.26) * mm, "end": v(-179.87, 234.33) * mm});
            skLineSegment(sketch, "E1052", {"start": v(-179.87, 234.33) * mm, "end": v(-178.73, 235.42) * mm});
            skLineSegment(sketch, "E1053", {"start": v(-178.73, 235.42) * mm, "end": v(-177.38, 236.76) * mm});
            skLineSegment(sketch, "E1054", {"start": v(-177.38, 236.76) * mm, "end": v(-176.6, 237.5) * mm});
            skLineSegment(sketch, "E1055", {"start": v(-176.6, 237.5) * mm, "end": v(-176.16, 238.14) * mm});
            skLineSegment(sketch, "E1056", {"start": v(-176.16, 238.14) * mm, "end": v(-175.36, 239.27) * mm});
            skLineSegment(sketch, "E1057", {"start": v(-175.36, 239.27) * mm, "end": v(-175.03, 239.98) * mm});
            skLineSegment(sketch, "E1058", {"start": v(-175.03, 239.98) * mm, "end": v(-174.65, 240.74) * mm});
            skLineSegment(sketch, "E1059", {"start": v(-174.65, 240.74) * mm, "end": v(-173.97, 241.8) * mm});
            skLineSegment(sketch, "E1060", {"start": v(-173.97, 241.8) * mm, "end": v(-173.44, 242.7) * mm});
            skLineSegment(sketch, "E1061", {"start": v(-173.44, 242.7) * mm, "end": v(-173.13, 243.1) * mm});
            skLineSegment(sketch, "E1062", {"start": v(-173.13, 243.1) * mm, "end": v(-172.68, 243.53) * mm});
            skLineSegment(sketch, "E1063", {"start": v(-172.68, 243.53) * mm, "end": v(-170.49, 245.61) * mm});
            skLineSegment(sketch, "E1064", {"start": v(-170.49, 245.61) * mm, "end": v(-170.03, 246) * mm});
            skLineSegment(sketch, "E1065", {"start": v(-170.03, 246) * mm, "end": v(-168.07, 247.25) * mm});
            skLineSegment(sketch, "E1066", {"start": v(-168.07, 247.25) * mm, "end": v(-167.46, 247.6) * mm});
            skLineSegment(sketch, "E1067", {"start": v(-167.46, 247.6) * mm, "end": v(-166.11, 248.39) * mm});
            skLineSegment(sketch, "E1068", {"start": v(-166.11, 248.39) * mm, "end": v(-163.52, 250.64) * mm});
            skLineSegment(sketch, "E1069", {"start": v(-163.52, 250.64) * mm, "end": v(-163.17, 250.95) * mm});
            skLineSegment(sketch, "E1070", {"start": v(-163.17, 250.95) * mm, "end": v(-163.1, 251.02) * mm});
            skLineSegment(sketch, "E1071", {"start": v(-163.1, 251.02) * mm, "end": v(-162.9, 251.23) * mm});
            skLineSegment(sketch, "E1072", {"start": v(-162.9, 251.23) * mm, "end": v(-160.32, 253.91) * mm});
            skLineSegment(sketch, "E1073", {"start": v(-160.32, 253.91) * mm, "end": v(-157.68, 256.63) * mm});
            skLineSegment(sketch, "E1074", {"start": v(-157.68, 256.63) * mm, "end": v(-157.51, 256.78) * mm});
            skLineSegment(sketch, "E1075", {"start": v(-157.51, 256.78) * mm, "end": v(-157.43, 256.86) * mm});
            skLineSegment(sketch, "E1076", {"start": v(-157.43, 256.86) * mm, "end": v(-154.49, 259.8) * mm});
            skLineSegment(sketch, "E1077", {"start": v(-154.49, 259.8) * mm, "end": v(-154.24, 260.06) * mm});
            skLineSegment(sketch, "E1078", {"start": v(-154.24, 260.06) * mm, "end": v(-154.23, 260.07) * mm});
            skLineSegment(sketch, "E1079", {"start": v(-154.23, 260.07) * mm, "end": v(-154.2, 260.09) * mm});
            skLineSegment(sketch, "E1080", {"start": v(-154.2, 260.09) * mm, "end": v(-151.35, 262.72) * mm});
            skLineSegment(sketch, "E1081", {"start": v(-151.35, 262.72) * mm, "end": v(-150.22, 263.86) * mm});
            skLineSegment(sketch, "E1082", {"start": v(-150.22, 263.86) * mm, "end": v(-148.34, 265.78) * mm});
            skLineSegment(sketch, "E1083", {"start": v(-148.34, 265.78) * mm, "end": v(-147.37, 266.73) * mm});
            skLineSegment(sketch, "E1084", {"start": v(-147.37, 266.73) * mm, "end": v(-144.8, 269.3) * mm});
            skLineSegment(sketch, "E1085", {"start": v(-144.8, 269.3) * mm, "end": v(-144.68, 269.43) * mm});
            skLineSegment(sketch, "E1086", {"start": v(-144.68, 269.43) * mm, "end": v(-144.42, 269.68) * mm});
            skLineSegment(sketch, "E1087", {"start": v(-144.42, 269.68) * mm, "end": v(-142.23, 271.68) * mm});
            skLineSegment(sketch, "E1088", {"start": v(-142.23, 271.68) * mm, "end": v(-140.71, 273.06) * mm});
            skLineSegment(sketch, "E1089", {"start": v(-140.71, 273.06) * mm, "end": v(-140.42, 273.3) * mm});
            skLineSegment(sketch, "E1090", {"start": v(-140.42, 273.3) * mm, "end": v(-137.59, 275.6) * mm});
            skLineSegment(sketch, "E1091", {"start": v(-137.59, 275.6) * mm, "end": v(-137.16, 275.93) * mm});
            skLineSegment(sketch, "E1092", {"start": v(-137.16, 275.93) * mm, "end": v(-135.3, 277.26) * mm});
            skLineSegment(sketch, "E1093", {"start": v(-135.3, 277.26) * mm, "end": v(-134.72, 277.66) * mm});
            skLineSegment(sketch, "E1094", {"start": v(-134.72, 277.66) * mm, "end": v(-133.19, 278.73) * mm});
            skLineSegment(sketch, "E1095", {"start": v(-133.19, 278.73) * mm, "end": v(-132.4, 279.25) * mm});
            skLineSegment(sketch, "E1096", {"start": v(-132.4, 279.25) * mm, "end": v(-129.14, 281.2) * mm});
            skLineSegment(sketch, "E1097", {"start": v(-129.14, 281.2) * mm, "end": v(-128.68, 281.47) * mm});
            skLineSegment(sketch, "E1098", {"start": v(-128.68, 281.47) * mm, "end": v(-127.7, 282) * mm});
            skLineSegment(sketch, "E1099", {"start": v(-127.7, 282) * mm, "end": v(-127.2, 282.24) * mm});
            skLineSegment(sketch, "E1100", {"start": v(-127.2, 282.24) * mm, "end": v(-124.45, 283.57) * mm});
            skLineSegment(sketch, "E1101", {"start": v(-124.45, 283.57) * mm, "end": v(-121.78, 284.74) * mm});
            skLineSegment(sketch, "E1102", {"start": v(-121.78, 284.74) * mm, "end": v(-120.23, 285.4) * mm});
            skLineSegment(sketch, "E1103", {"start": v(-120.23, 285.4) * mm, "end": v(-118.9, 285.93) * mm});
            skLineSegment(sketch, "E1104", {"start": v(-118.9, 285.93) * mm, "end": v(-117.46, 286.44) * mm});
            skLineSegment(sketch, "E1105", {"start": v(-117.46, 286.44) * mm, "end": v(-114.97, 287.27) * mm});
            skLineSegment(sketch, "E1106", {"start": v(-114.97, 287.27) * mm, "end": v(-114.73, 287.35) * mm});
            skLineSegment(sketch, "E1107", {"start": v(-114.73, 287.35) * mm, "end": v(-114.35, 287.47) * mm});
            skLineSegment(sketch, "E1108", {"start": v(-114.35, 287.47) * mm, "end": v(-110.8, 288.54) * mm});
            skLineSegment(sketch, "E1109", {"start": v(-110.8, 288.54) * mm, "end": v(-108.47, 289.18) * mm});
            skLineSegment(sketch, "E1110", {"start": v(-108.47, 289.18) * mm, "end": v(-106.96, 289.56) * mm});
            skLineSegment(sketch, "E1111", {"start": v(-106.96, 289.56) * mm, "end": v(-106.04, 289.77) * mm});
            skLineSegment(sketch, "E1112", {"start": v(-106.04, 289.77) * mm, "end": v(-104.8, 290.12) * mm});
            skLineSegment(sketch, "E1113", {"start": v(-104.8, 290.12) * mm, "end": v(-102.31, 290.71) * mm});
            skLineSegment(sketch, "E1114", {"start": v(-102.31, 290.71) * mm, "end": v(-100.32, 291.17) * mm});
            skLineSegment(sketch, "E1115", {"start": v(-100.32, 291.17) * mm, "end": v(-97.56, 291.8) * mm});
            skLineSegment(sketch, "E1116", {"start": v(-97.56, 291.8) * mm, "end": v(-93.69, 292.76) * mm});
            skLineSegment(sketch, "E1117", {"start": v(-93.69, 292.76) * mm, "end": v(-93.24, 292.86) * mm});
            skLineSegment(sketch, "E1118", {"start": v(-93.24, 292.86) * mm, "end": v(-92.93, 292.92) * mm});
            skLineSegment(sketch, "E1119", {"start": v(-92.93, 292.92) * mm, "end": v(-92.24, 293.08) * mm});
            skLineSegment(sketch, "E1120", {"start": v(-92.24, 293.08) * mm, "end": v(-90.25, 293.49) * mm});
            skLineSegment(sketch, "E1121", {"start": v(-90.25, 293.49) * mm, "end": v(-89.6, 293.63) * mm});
            skLineSegment(sketch, "E1122", {"start": v(-89.6, 293.63) * mm, "end": v(-88.1, 293.97) * mm});
            skLineSegment(sketch, "E1123", {"start": v(-88.1, 293.97) * mm, "end": v(-87.44, 294.1) * mm});
            skLineSegment(sketch, "E1124", {"start": v(-87.44, 294.1) * mm, "end": v(-87.1, 294.16) * mm});
            skLineSegment(sketch, "E1125", {"start": v(-87.1, 294.16) * mm, "end": v(-86.6, 294.27) * mm});
            skLineSegment(sketch, "E1126", {"start": v(-86.6, 294.27) * mm, "end": v(-83.86, 294.8) * mm});
            skLineSegment(sketch, "E1127", {"start": v(-83.86, 294.8) * mm, "end": v(-82.2, 295.08) * mm});
            skLineSegment(sketch, "E1128", {"start": v(-82.2, 295.08) * mm, "end": v(-79.1, 295.74) * mm});
            skLineSegment(sketch, "E1129", {"start": v(-79.1, 295.74) * mm, "end": v(-79.03, 295.75) * mm});
            skLineSegment(sketch, "E1130", {"start": v(-79.03, 295.75) * mm, "end": v(-78.99, 295.76) * mm});
            skLineSegment(sketch, "E1131", {"start": v(-78.99, 295.76) * mm, "end": v(-76.27, 296.2) * mm});
            skLineSegment(sketch, "E1132", {"start": v(-76.27, 296.2) * mm, "end": v(-74.36, 296.55) * mm});
            skLineSegment(sketch, "E1133", {"start": v(-74.36, 296.55) * mm, "end": v(-73.95, 296.62) * mm});
            skLineSegment(sketch, "E1134", {"start": v(-73.95, 296.62) * mm, "end": v(-72.78, 296.83) * mm});
            skLineSegment(sketch, "E1135", {"start": v(-72.78, 296.83) * mm, "end": v(-69.22, 297.4) * mm});
            skLineSegment(sketch, "E1136", {"start": v(-69.22, 297.4) * mm, "end": v(-66.88, 297.78) * mm});
            skLineSegment(sketch, "E1137", {"start": v(-66.88, 297.78) * mm, "end": v(-65.16, 298.07) * mm});
            skLineSegment(sketch, "E1138", {"start": v(-65.16, 298.07) * mm, "end": v(-62.47, 298.48) * mm});
            skLineSegment(sketch, "E1139", {"start": v(-62.47, 298.48) * mm, "end": v(-61.87, 298.54) * mm});
            skLineSegment(sketch, "E1140", {"start": v(-61.87, 298.54) * mm, "end": v(-60.58, 298.73) * mm});
            skLineSegment(sketch, "E1141", {"start": v(-60.58, 298.73) * mm, "end": v(-58.38, 299) * mm});
            skLineSegment(sketch, "E1142", {"start": v(-58.38, 299) * mm, "end": v(-55.2, 299.38) * mm});
            skLineSegment(sketch, "E1143", {"start": v(-55.2, 299.38) * mm, "end": v(-54.53, 299.45) * mm});
            skLineSegment(sketch, "E1144", {"start": v(-54.53, 299.45) * mm, "end": v(-54.39, 299.46) * mm});
            skLineSegment(sketch, "E1145", {"start": v(-54.39, 299.46) * mm, "end": v(-54, 299.52) * mm});
            skLineSegment(sketch, "E1146", {"start": v(-54, 299.52) * mm, "end": v(-51.41, 299.78) * mm});
            skLineSegment(sketch, "E1147", {"start": v(-51.41, 299.78) * mm, "end": v(-49.53, 300.03) * mm});
            skLineSegment(sketch, "E1148", {"start": v(-49.53, 300.03) * mm, "end": v(-48.67, 300.1) * mm});
            skLineSegment(sketch, "E1149", {"start": v(-48.67, 300.1) * mm, "end": v(-46.5, 300.38) * mm});
            skLineSegment(sketch, "E1150", {"start": v(-46.5, 300.38) * mm, "end": v(-45.75, 300.45) * mm});
            skLineSegment(sketch, "E1151", {"start": v(-45.75, 300.45) * mm, "end": v(-45.38, 300.48) * mm});
            skLineSegment(sketch, "E1152", {"start": v(-45.38, 300.48) * mm, "end": v(-43.13, 300.57) * mm});
            skLineSegment(sketch, "E1153", {"start": v(-43.13, 300.57) * mm, "end": v(-41.39, 300.8) * mm});
            skLineSegment(sketch, "E1154", {"start": v(-41.39, 300.8) * mm, "end": v(-40.58, 300.86) * mm});
            skLineSegment(sketch, "E1155", {"start": v(-40.58, 300.86) * mm, "end": v(-38.35, 301.04) * mm});
            skLineSegment(sketch, "E1156", {"start": v(-38.35, 301.04) * mm, "end": v(-38.3, 301.04) * mm});
            skLineSegment(sketch, "E1157", {"start": v(-38.3, 301.04) * mm, "end": v(-36.5, 301.1) * mm});
            skLineSegment(sketch, "E1158", {"start": v(-36.5, 301.1) * mm, "end": v(-33.84, 301.4) * mm});
            skLineSegment(sketch, "E1159", {"start": v(-33.84, 301.4) * mm, "end": v(-33.8, 301.4) * mm});
            skLineSegment(sketch, "E1160", {"start": v(-33.8, 301.4) * mm, "end": v(-30.13, 301.63) * mm});
            skLineSegment(sketch, "E1161", {"start": v(-30.13, 301.63) * mm, "end": v(-28.42, 301.7) * mm});
            skLineSegment(sketch, "E1162", {"start": v(-28.42, 301.7) * mm, "end": v(-26.41, 301.77) * mm});
            skLineSegment(sketch, "E1163", {"start": v(-26.41, 301.77) * mm, "end": v(-23.24, 301.91) * mm});
            skLineSegment(sketch, "E1164", {"start": v(-23.24, 301.91) * mm, "end": v(-22.87, 301.93) * mm});
            skLineSegment(sketch, "E1165", {"start": v(-22.87, 301.93) * mm, "end": v(-22.34, 301.94) * mm});
            skLineSegment(sketch, "E1166", {"start": v(-22.34, 301.94) * mm, "end": v(-18.3, 302.03) * mm});
            skLineSegment(sketch, "E1167", {"start": v(-18.3, 302.03) * mm, "end": v(-15.44, 302.08) * mm});
            skLineSegment(sketch, "E1168", {"start": v(-15.44, 302.08) * mm, "end": v(-13.75, 302.07) * mm});
            skLineSegment(sketch, "E1169", {"start": v(-13.75, 302.07) * mm, "end": v(-10.52, 302) * mm});
            skLineSegment(sketch, "E1170", {"start": v(-10.52, 302) * mm, "end": v(-9.14, 302.03) * mm});
            skLineSegment(sketch, "E1171", {"start": v(-9.14, 302.03) * mm, "end": v(-7.4, 302.04) * mm});
            skLineSegment(sketch, "E1172", {"start": v(-7.4, 302.04) * mm, "end": v(-5.02, 302.02) * mm});
            skLineSegment(sketch, "E1173", {"start": v(-5.02, 302.02) * mm, "end": v(-3.7, 302.02) * mm});
            skLineSegment(sketch, "E1174", {"start": v(-3.7, 302.02) * mm, "end": v(-1.29, 302.08) * mm});
            skLineSegment(sketch, "E1175", {"start": v(-1.29, 302.08) * mm, "end": v(-1.13, 302.09) * mm});
            skLineSegment(sketch, "E1176", {"start": v(-1.13, 302.09) * mm, "end": v(-0.94, 302.13) * mm});
            skLineSegment(sketch, "E1177", {"start": v(-0.94, 302.13) * mm, "end": v(0, 302.3) * mm});
            skLineSegment(sketch, "E1178.0", {"start": v(3.9, 277.6) * mm, "end": v(4.57, 277.72) * mm});
            skLineSegment(sketch, "E1178.1", {"start": v(1.69, 277.14) * mm, "end": v(3.9, 277.6) * mm});
            skLineSegment(sketch, "E1178.2", {"start": v(-0.7, 277.09) * mm, "end": v(1.69, 277.14) * mm});
            skLineSegment(sketch, "E1178.3", {"start": v(-3.35, 277.02) * mm, "end": v(-0.7, 277.09) * mm});
            skLineSegment(sketch, "E1178.4", {"start": v(-5.15, 277.02) * mm, "end": v(-3.35, 277.02) * mm});
            skLineSegment(sketch, "E1178.5", {"start": v(-7.42, 277.04) * mm, "end": v(-5.15, 277.02) * mm});
            skLineSegment(sketch, "E1178.6", {"start": v(-8.72, 277.03) * mm, "end": v(-7.42, 277.04) * mm});
            skLineSegment(sketch, "E1178.7", {"start": v(-10.5, 276.99) * mm, "end": v(-8.72, 277.03) * mm});
            skLineSegment(sketch, "E1178.8", {"start": v(-14.1, 277.07) * mm, "end": v(-10.5, 276.99) * mm});
            skLineSegment(sketch, "E1178.9", {"start": v(-15.31, 277.07) * mm, "end": v(-14.1, 277.07) * mm});
            skLineSegment(sketch, "E1178.10", {"start": v(-17.83, 277.04) * mm, "end": v(-15.31, 277.07) * mm});
            skLineSegment(sketch, "E1178.11", {"start": v(-21.81, 276.95) * mm, "end": v(-17.83, 277.04) * mm});
            skLineSegment(sketch, "E1178.12", {"start": v(-21.99, 276.94) * mm, "end": v(-21.81, 276.95) * mm});
            skLineSegment(sketch, "E1178.13", {"start": v(-25.45, 276.78) * mm, "end": v(-21.99, 276.94) * mm});
            skLineSegment(sketch, "E1178.14", {"start": v(-27.52, 276.72) * mm, "end": v(-25.45, 276.78) * mm});
            skLineSegment(sketch, "E1178.15", {"start": v(-28.83, 276.66) * mm, "end": v(-27.52, 276.72) * mm});
            skLineSegment(sketch, "E1178.16", {"start": v(-31.68, 276.49) * mm, "end": v(-28.83, 276.66) * mm});
            skLineSegment(sketch, "E1178.17", {"start": v(-34.65, 276.16) * mm, "end": v(-31.68, 276.49) * mm});
            skLineSegment(sketch, "E1178.18", {"start": v(-36.81, 276.08) * mm, "end": v(-34.65, 276.16) * mm});
            skLineSegment(sketch, "E1178.19", {"start": v(-38.72, 275.92) * mm, "end": v(-36.81, 276.08) * mm});
            skLineSegment(sketch, "E1178.20", {"start": v(-38.91, 275.91) * mm, "end": v(-38.72, 275.92) * mm});
            skLineSegment(sketch, "E1178.21", {"start": v(-41, 275.64) * mm, "end": v(-38.91, 275.91) * mm});
            skLineSegment(sketch, "E1178.22", {"start": v(-43.71, 275.53) * mm, "end": v(-41, 275.64) * mm});
            skLineSegment(sketch, "E1178.23", {"start": v(-46, 275.24) * mm, "end": v(-43.71, 275.53) * mm});
            skLineSegment(sketch, "E1178.24", {"start": v(-46.8, 275.17) * mm, "end": v(-46, 275.24) * mm});
            skLineSegment(sketch, "E1178.25", {"start": v(-48.53, 274.95) * mm, "end": v(-46.8, 275.17) * mm});
            skLineSegment(sketch, "E1178.26", {"start": v(-51, 274.7) * mm, "end": v(-48.53, 274.95) * mm});
            skLineSegment(sketch, "E1178.27", {"start": v(-51.17, 274.67) * mm, "end": v(-51, 274.7) * mm});
            skLineSegment(sketch, "E1178.28", {"start": v(-51.82, 274.6) * mm, "end": v(-51.17, 274.67) * mm});
            skLineSegment(sketch, "E1178.29", {"start": v(-52.49, 274.53) * mm, "end": v(-51.82, 274.6) * mm});
            skLineSegment(sketch, "E1178.30", {"start": v(-55.4, 274.18) * mm, "end": v(-52.49, 274.53) * mm});
            skLineSegment(sketch, "E1178.31", {"start": v(-57.28, 273.95) * mm, "end": v(-55.4, 274.18) * mm});
            skLineSegment(sketch, "E1178.32", {"start": v(-58.64, 273.75) * mm, "end": v(-57.28, 273.95) * mm});
            skLineSegment(sketch, "E1178.33", {"start": v(-59.18, 273.69) * mm, "end": v(-58.64, 273.75) * mm});
            skLineSegment(sketch, "E1178.34", {"start": v(-61.25, 273.37) * mm, "end": v(-59.18, 273.69) * mm});
            skLineSegment(sketch, "E1178.35", {"start": v(-62.87, 273.1) * mm, "end": v(-61.25, 273.37) * mm});
            skLineSegment(sketch, "E1178.36", {"start": v(-65.24, 272.73) * mm, "end": v(-62.87, 273.1) * mm});
            skLineSegment(sketch, "E1178.37", {"start": v(-68.57, 272.19) * mm, "end": v(-65.24, 272.73) * mm});
            skLineSegment(sketch, "E1178.38", {"start": v(-69.6, 272) * mm, "end": v(-68.57, 272.19) * mm});
            skLineSegment(sketch, "E1178.39", {"start": v(-69.93, 271.94) * mm, "end": v(-69.6, 272) * mm});
            skLineSegment(sketch, "E1178.40", {"start": v(-72.02, 271.56) * mm, "end": v(-69.93, 271.94) * mm});
            skLineSegment(sketch, "E1178.41", {"start": v(-74.44, 271.17) * mm, "end": v(-72.02, 271.56) * mm});
            skLineSegment(sketch, "E1178.42", {"start": v(-77.46, 270.53) * mm, "end": v(-74.44, 271.17) * mm});
            skLineSegment(sketch, "E1178.43", {"start": v(-79.38, 270.2) * mm, "end": v(-77.46, 270.53) * mm});
            skLineSegment(sketch, "E1178.44", {"start": v(-81.56, 269.78) * mm, "end": v(-79.38, 270.2) * mm});
            skLineSegment(sketch, "E1178.45", {"start": v(-81.98, 269.69) * mm, "end": v(-81.56, 269.78) * mm});
            skLineSegment(sketch, "E1178.46", {"start": v(-82.68, 269.55) * mm, "end": v(-81.98, 269.69) * mm});
            skLineSegment(sketch, "E1178.47", {"start": v(-83, 269.49) * mm, "end": v(-82.68, 269.55) * mm});
            skLineSegment(sketch, "E1178.48", {"start": v(-84.26, 269.2) * mm, "end": v(-83, 269.49) * mm});
            skLineSegment(sketch, "E1178.49", {"start": v(-85.16, 269.01) * mm, "end": v(-84.26, 269.2) * mm});
            skLineSegment(sketch, "E1178.50", {"start": v(-86.94, 268.65) * mm, "end": v(-85.16, 269.01) * mm});
            skLineSegment(sketch, "E1178.51", {"start": v(-87.4, 268.54) * mm, "end": v(-86.94, 268.65) * mm});
            skLineSegment(sketch, "E1178.52", {"start": v(-87.98, 268.42) * mm, "end": v(-87.4, 268.54) * mm});
            skLineSegment(sketch, "E1178.53", {"start": v(-88.14, 268.38) * mm, "end": v(-87.98, 268.42) * mm});
            skLineSegment(sketch, "E1178.54", {"start": v(-91.76, 267.48) * mm, "end": v(-88.14, 268.38) * mm});
            skLineSegment(sketch, "E1178.55", {"start": v(-247.78, 142.24) * mm, "end": v(-245.33, 143.56) * mm});
            skLineSegment(sketch, "E1178.56", {"start": v(-248.93, 141.43) * mm, "end": v(-247.78, 142.24) * mm});
            skLineSegment(sketch, "E1178.57", {"start": v(-249.39, 141.14) * mm, "end": v(-248.93, 141.43) * mm});
            skLineSegment(sketch, "E1178.58", {"start": v(-250.17, 140.57) * mm, "end": v(-249.39, 141.14) * mm});
            skLineSegment(sketch, "E1178.59", {"start": v(-251.07, 139.89) * mm, "end": v(-250.17, 140.57) * mm});
            skLineSegment(sketch, "E1178.60", {"start": v(-252.06, 139.17) * mm, "end": v(-251.07, 139.89) * mm});
            skLineSegment(sketch, "E1178.61", {"start": v(-254.46, 137.4) * mm, "end": v(-252.06, 139.17) * mm});
            skLineSegment(sketch, "E1178.62", {"start": v(-256.09, 136.12) * mm, "end": v(-254.46, 137.4) * mm});
            skLineSegment(sketch, "E1178.63", {"start": v(-257.6, 134.92) * mm, "end": v(-256.09, 136.12) * mm});
            skLineSegment(sketch, "E1178.64", {"start": v(-260.33, 132.78) * mm, "end": v(-257.6, 134.92) * mm});
            skLineSegment(sketch, "E1178.65", {"start": v(-260.67, 132.51) * mm, "end": v(-260.33, 132.78) * mm});
            skLineSegment(sketch, "E1178.66", {"start": v(-263.25, 130.28) * mm, "end": v(-260.67, 132.51) * mm});
            skLineSegment(sketch, "E1178.67", {"start": v(-266.38, 127.39) * mm, "end": v(-263.25, 130.28) * mm});
            skLineSegment(sketch, "E1178.68", {"start": v(-267.54, 126.3) * mm, "end": v(-266.38, 127.39) * mm});
            skLineSegment(sketch, "E1178.69", {"start": v(-267.74, 126.1) * mm, "end": v(-267.54, 126.3) * mm});
            skLineSegment(sketch, "E1178.70", {"start": v(-269.2, 124.66) * mm, "end": v(-267.74, 126.1) * mm});
            skLineSegment(sketch, "E1178.71", {"start": v(-271.35, 122.4) * mm, "end": v(-269.2, 124.66) * mm});
            skLineSegment(sketch, "E1178.72", {"start": v(-271.84, 121.88) * mm, "end": v(-271.35, 122.4) * mm});
            skLineSegment(sketch, "E1178.73", {"start": v(-273.55, 120.05) * mm, "end": v(-271.84, 121.88) * mm});
            skLineSegment(sketch, "E1178.74", {"start": v(-274.59, 118.92) * mm, "end": v(-273.55, 120.05) * mm});
            skLineSegment(sketch, "E1178.75", {"start": v(-275.11, 118.31) * mm, "end": v(-274.59, 118.92) * mm});
            skLineSegment(sketch, "E1178.76", {"start": v(-275.4, 118) * mm, "end": v(-275.11, 118.31) * mm});
            skLineSegment(sketch, "E1178.77", {"start": v(-276.98, 116) * mm, "end": v(-275.4, 118) * mm});
            skLineSegment(sketch, "E1178.78", {"start": v(-278.1, 114.63) * mm, "end": v(-276.98, 116) * mm});
            skLineSegment(sketch, "E1178.79", {"start": v(-279.24, 113.3) * mm, "end": v(-278.1, 114.63) * mm});
            skLineSegment(sketch, "E1178.80", {"start": v(-280.57, 111.51) * mm, "end": v(-279.24, 113.3) * mm});
            skLineSegment(sketch, "E1178.81", {"start": v(-280.87, 111.13) * mm, "end": v(-280.57, 111.51) * mm});
            skLineSegment(sketch, "E1178.82", {"start": v(-282.6, 108.83) * mm, "end": v(-280.87, 111.13) * mm});
            skLineSegment(sketch, "E1178.83", {"start": v(-282.66, 108.74) * mm, "end": v(-282.6, 108.83) * mm});
            skLineSegment(sketch, "E1178.84", {"start": v(-282.87, 108.47) * mm, "end": v(-282.66, 108.74) * mm});
            skLineSegment(sketch, "E1178.85", {"start": v(-284.13, 106.75) * mm, "end": v(-282.87, 108.47) * mm});
            skLineSegment(sketch, "E1178.86", {"start": v(-284.44, 106.3) * mm, "end": v(-284.13, 106.75) * mm});
            skLineSegment(sketch, "E1178.87", {"start": v(-285.19, 105.19) * mm, "end": v(-284.44, 106.3) * mm});
            skLineSegment(sketch, "E1178.88", {"start": v(-286.04, 103.86) * mm, "end": v(-285.19, 105.19) * mm});
            skLineSegment(sketch, "E1178.89", {"start": v(-286.75, 102.75) * mm, "end": v(-286.04, 103.86) * mm});
            skLineSegment(sketch, "E1178.90", {"start": v(-287.35, 101.86) * mm, "end": v(-286.75, 102.75) * mm});
            skLineSegment(sketch, "E1178.91", {"start": v(-287.65, 101.39) * mm, "end": v(-287.35, 101.86) * mm});
            skLineSegment(sketch, "E1178.92", {"start": v(-288.52, 99.86) * mm, "end": v(-287.65, 101.39) * mm});
            skLineSegment(sketch, "E1178.93", {"start": v(-289.2, 98.67) * mm, "end": v(-288.52, 99.86) * mm});
            skLineSegment(sketch, "E1178.94", {"start": v(-291.01, 95.67) * mm, "end": v(-289.2, 98.67) * mm});
            skLineSegment(sketch, "E1178.95", {"start": v(-292.2, 93.5) * mm, "end": v(-291.01, 95.67) * mm});
            skLineSegment(sketch, "E1178.96", {"start": v(-292.64, 92.54) * mm, "end": v(-292.2, 93.5) * mm});
            skLineSegment(sketch, "E1178.97", {"start": v(-293.34, 91.04) * mm, "end": v(-292.64, 92.54) * mm});
            skLineSegment(sketch, "E1178.98", {"start": v(-293.72, 90.23) * mm, "end": v(-293.34, 91.04) * mm});
            skLineSegment(sketch, "E1178.99", {"start": v(-294.63, 88.33) * mm, "end": v(-293.72, 90.23) * mm});
            skLineSegment(sketch, "E1178.100", {"start": v(-294.83, 87.9) * mm, "end": v(-294.63, 88.33) * mm});
            skLineSegment(sketch, "E1178.101", {"start": v(-296.72, 83.7) * mm, "end": v(-294.83, 87.9) * mm});
            skLineSegment(sketch, "E1178.102", {"start": v(-296.76, 83.6) * mm, "end": v(-296.72, 83.7) * mm});
            skLineSegment(sketch, "E1178.103", {"start": v(-298.18, 80.07) * mm, "end": v(-296.76, 83.6) * mm});
            skLineSegment(sketch, "E1178.104", {"start": v(-298.43, 79.49) * mm, "end": v(-298.18, 80.07) * mm});
            skLineSegment(sketch, "E1178.105", {"start": v(-307.13, 39.08) * mm, "end": v(-307.1, 39.62) * mm});
            skLineSegment(sketch, "E1178.106", {"start": v(-307.2, 38.1) * mm, "end": v(-307.13, 39.08) * mm});
            skLineSegment(sketch, "E1178.107", {"start": v(-307.23, 37.36) * mm, "end": v(-307.2, 38.1) * mm});
            skLineSegment(sketch, "E1178.108", {"start": v(-307.32, 34.47) * mm, "end": v(-307.23, 37.36) * mm});
            skLineSegment(sketch, "E1178.109", {"start": v(-307.42, 32.37) * mm, "end": v(-307.32, 34.47) * mm});
            skLineSegment(sketch, "E1178.110", {"start": v(-307.44, 30.89) * mm, "end": v(-307.42, 32.37) * mm});
            skLineSegment(sketch, "E1178.111", {"start": v(-307.49, 28.1) * mm, "end": v(-307.44, 30.89) * mm});
            skLineSegment(sketch, "E1178.112", {"start": v(-307.5, 27.06) * mm, "end": v(-307.49, 28.1) * mm});
            skLineSegment(sketch, "E1178.113", {"start": v(-307.44, 24.22) * mm, "end": v(-307.5, 27.06) * mm});
            skLineSegment(sketch, "E1178.114", {"start": v(-307.5, 22.74) * mm, "end": v(-307.44, 24.22) * mm});
            skLineSegment(sketch, "E1178.115", {"start": v(-307.48, 20.8) * mm, "end": v(-307.5, 22.74) * mm});
            skLineSegment(sketch, "E1178.116", {"start": v(-307.4, 17.94) * mm, "end": v(-307.48, 20.8) * mm});
            skLineSegment(sketch, "E1178.117", {"start": v(-306.04, 6.33) * mm, "end": v(-306.52, 8.74) * mm});
            skLineSegment(sketch, "E1178.118", {"start": v(-305.86, 5.37) * mm, "end": v(-306.04, 6.33) * mm});
            skLineSegment(sketch, "E1178.119", {"start": v(-305.65, 4.3) * mm, "end": v(-305.86, 5.37) * mm});
            skLineSegment(sketch, "E1178.120", {"start": v(-305.48, 2.7) * mm, "end": v(-305.65, 4.3) * mm});
            skLineSegment(sketch, "E1178.121", {"start": v(-306.52, 8.74) * mm, "end": v(-306.62, 9.4) * mm});
            skLineSegment(sketch, "E1178.122", {"start": v(-306.62, 9.4) * mm, "end": v(-306.84, 10.85) * mm});
            skLineSegment(sketch, "E1178.123", {"start": v(-306.84, 10.85) * mm, "end": v(-306.96, 12.1) * mm});
            skLineSegment(sketch, "E1178.124", {"start": v(-306.96, 12.1) * mm, "end": v(-307.26, 15.02) * mm});
            skLineSegment(sketch, "E1178.125", {"start": v(-307.26, 15.02) * mm, "end": v(-307.34, 16.43) * mm});
            skLineSegment(sketch, "E1178.126", {"start": v(-307.34, 16.43) * mm, "end": v(-307.4, 17.94) * mm});
            skLineSegment(sketch, "E1178.127", {"start": v(-307.1, 39.62) * mm, "end": v(-306.82, 41.45) * mm});
            skLineSegment(sketch, "E1178.128", {"start": v(-306.82, 41.45) * mm, "end": v(-306.65, 43.16) * mm});
            skLineSegment(sketch, "E1178.129", {"start": v(-306.65, 43.16) * mm, "end": v(-306.35, 46.21) * mm});
            skLineSegment(sketch, "E1178.130", {"start": v(-306.35, 46.21) * mm, "end": v(-306.26, 47.07) * mm});
            skLineSegment(sketch, "E1178.131", {"start": v(-306.26, 47.07) * mm, "end": v(-305.92, 49.94) * mm});
            skLineSegment(sketch, "E1178.132", {"start": v(-305.92, 49.94) * mm, "end": v(-305.83, 50.66) * mm});
            skLineSegment(sketch, "E1178.133", {"start": v(-305.83, 50.66) * mm, "end": v(-305.64, 51.92) * mm});
            skLineSegment(sketch, "E1178.134", {"start": v(-305.64, 51.92) * mm, "end": v(-305.4, 53.49) * mm});
            skLineSegment(sketch, "E1178.135", {"start": v(-305.4, 53.49) * mm, "end": v(-305.24, 54.5) * mm});
            skLineSegment(sketch, "E1178.136", {"start": v(-305.24, 54.5) * mm, "end": v(-305.03, 55.65) * mm});
            skLineSegment(sketch, "E1178.137", {"start": v(-305.03, 55.65) * mm, "end": v(-304.83, 56.86) * mm});
            skLineSegment(sketch, "E1178.138", {"start": v(-304.83, 56.86) * mm, "end": v(-304.66, 57.7) * mm});
            skLineSegment(sketch, "E1178.139", {"start": v(-304.66, 57.7) * mm, "end": v(-304.48, 58.64) * mm});
            skLineSegment(sketch, "E1178.140", {"start": v(-304.48, 58.64) * mm, "end": v(-304.25, 59.7) * mm});
            skLineSegment(sketch, "E1178.141", {"start": v(-304.25, 59.7) * mm, "end": v(-304, 60.7) * mm});
            skLineSegment(sketch, "E1178.142", {"start": v(-304, 60.7) * mm, "end": v(-303.51, 62.9) * mm});
            skLineSegment(sketch, "E1178.143", {"start": v(-303.51, 62.9) * mm, "end": v(-302.72, 66.4) * mm});
            skLineSegment(sketch, "E1178.144", {"start": v(-302.72, 66.4) * mm, "end": v(-301.7, 69.8) * mm});
            skLineSegment(sketch, "E1178.145", {"start": v(-301.7, 69.8) * mm, "end": v(-301.43, 70.8) * mm});
            skLineSegment(sketch, "E1178.146", {"start": v(-301.43, 70.8) * mm, "end": v(-301.15, 71.79) * mm});
            skLineSegment(sketch, "E1178.147", {"start": v(-301.15, 71.79) * mm, "end": v(-299.7, 75.79) * mm});
            skLineSegment(sketch, "E1178.148", {"start": v(-299.7, 75.79) * mm, "end": v(-299.18, 77.28) * mm});
            skLineSegment(sketch, "E1178.149", {"start": v(-299.18, 77.28) * mm, "end": v(-298.48, 79.34) * mm});
            skLineSegment(sketch, "E1178.150", {"start": v(-298.48, 79.34) * mm, "end": v(-298.43, 79.49) * mm});
            skLineSegment(sketch, "E1178.151", {"start": v(-245.33, 143.56) * mm, "end": v(-244.68, 144) * mm});
            skLineSegment(sketch, "E1178.152", {"start": v(-244.68, 144) * mm, "end": v(-241.16, 146.13) * mm});
            skLineSegment(sketch, "E1178.153", {"start": v(-241.16, 146.13) * mm, "end": v(-239.05, 147.69) * mm});
            skLineSegment(sketch, "E1178.154", {"start": v(-239.05, 147.69) * mm, "end": v(-236.93, 149.55) * mm});
            skLineSegment(sketch, "E1178.155", {"start": v(-236.93, 149.55) * mm, "end": v(-236.32, 149.99) * mm});
            skLineSegment(sketch, "E1178.156", {"start": v(-236.32, 149.99) * mm, "end": v(-234.2, 151.5) * mm});
            skLineSegment(sketch, "E1178.157", {"start": v(-234.2, 151.5) * mm, "end": v(-233.53, 151.97) * mm});
            skLineSegment(sketch, "E1178.158", {"start": v(-233.53, 151.97) * mm, "end": v(-231.3, 153.6) * mm});
            skLineSegment(sketch, "E1178.159", {"start": v(-231.3, 153.6) * mm, "end": v(-228.28, 155.63) * mm});
            skLineSegment(sketch, "E1178.160", {"start": v(-228.28, 155.63) * mm, "end": v(-227.68, 156.04) * mm});
            skLineSegment(sketch, "E1178.161", {"start": v(-227.68, 156.04) * mm, "end": v(-226.9, 156.61) * mm});
            skLineSegment(sketch, "E1178.162", {"start": v(-226.9, 156.61) * mm, "end": v(-224.85, 158.19) * mm});
            skLineSegment(sketch, "E1178.163", {"start": v(-224.85, 158.19) * mm, "end": v(-224.1, 158.71) * mm});
            skLineSegment(sketch, "E1178.164", {"start": v(-224.1, 158.71) * mm, "end": v(-223.15, 159.2) * mm});
            skLineSegment(sketch, "E1178.165", {"start": v(-223.15, 159.2) * mm, "end": v(-221.96, 159.9) * mm});
            skLineSegment(sketch, "E1178.166", {"start": v(-221.96, 159.9) * mm, "end": v(-218.55, 161.92) * mm});
            skLineSegment(sketch, "E1178.167", {"start": v(-218.55, 161.92) * mm, "end": v(-216.25, 163.9) * mm});
            skLineSegment(sketch, "E1178.168", {"start": v(-216.25, 163.9) * mm, "end": v(-215.5, 164.6) * mm});
            skLineSegment(sketch, "E1178.169", {"start": v(-215.5, 164.6) * mm, "end": v(-213.79, 166.21) * mm});
            skLineSegment(sketch, "E1178.170", {"start": v(-213.79, 166.21) * mm, "end": v(-211.98, 167.96) * mm});
            skLineSegment(sketch, "E1178.171", {"start": v(-211.98, 167.96) * mm, "end": v(-210.44, 169.5) * mm});
            skLineSegment(sketch, "E1178.172", {"start": v(-210.44, 169.5) * mm, "end": v(-208.34, 171.56) * mm});
            skLineSegment(sketch, "E1178.173", {"start": v(-208.34, 171.56) * mm, "end": v(-208.07, 171.83) * mm});
            skLineSegment(sketch, "E1178.174", {"start": v(-208.07, 171.83) * mm, "end": v(-207.97, 171.92) * mm});
            skLineSegment(sketch, "E1178.175", {"start": v(-207.97, 171.92) * mm, "end": v(-204.91, 174.74) * mm});
            skLineSegment(sketch, "E1178.176", {"start": v(-204.91, 174.74) * mm, "end": v(-204.24, 175.37) * mm});
            skLineSegment(sketch, "E1178.177", {"start": v(-204.24, 175.37) * mm, "end": v(-203.48, 176.14) * mm});
            skLineSegment(sketch, "E1178.178", {"start": v(-203.48, 176.14) * mm, "end": v(-201.62, 178.06) * mm});
            skLineSegment(sketch, "E1178.179", {"start": v(-201.62, 178.06) * mm, "end": v(-199.74, 179.94) * mm});
            skLineSegment(sketch, "E1178.180", {"start": v(-199.74, 179.94) * mm, "end": v(-199.54, 180.14) * mm});
            skLineSegment(sketch, "E1178.181", {"start": v(-199.54, 180.14) * mm, "end": v(-198.13, 181.51) * mm});
            skLineSegment(sketch, "E1178.182", {"start": v(-198.13, 181.51) * mm, "end": v(-195.61, 183.95) * mm});
            skLineSegment(sketch, "E1178.183", {"start": v(-195.61, 183.95) * mm, "end": v(-195.21, 184.34) * mm});
            skLineSegment(sketch, "E1178.184", {"start": v(-195.21, 184.34) * mm, "end": v(-194.45, 185.1) * mm});
            skLineSegment(sketch, "E1178.185", {"start": v(-194.45, 185.1) * mm, "end": v(-190.83, 188.63) * mm});
            skLineSegment(sketch, "E1178.186", {"start": v(-190.83, 188.63) * mm, "end": v(-189.2, 190.24) * mm});
            skLineSegment(sketch, "E1178.187", {"start": v(-189.2, 190.24) * mm, "end": v(-187.43, 191.92) * mm});
            skLineSegment(sketch, "E1178.188", {"start": v(-187.43, 191.92) * mm, "end": v(-186.78, 192.63) * mm});
            skLineSegment(sketch, "E1178.189", {"start": v(-186.78, 192.63) * mm, "end": v(-186.18, 193.26) * mm});
            skLineSegment(sketch, "E1178.190", {"start": v(-186.18, 193.26) * mm, "end": v(-185.69, 193.72) * mm});
            skLineSegment(sketch, "E1178.191", {"start": v(-185.69, 193.72) * mm, "end": v(-183.24, 196.01) * mm});
            skLineSegment(sketch, "E1178.192", {"start": v(-183.24, 196.01) * mm, "end": v(-182.97, 196.26) * mm});
            skLineSegment(sketch, "E1178.193", {"start": v(-182.97, 196.26) * mm, "end": v(-182.6, 196.6) * mm});
            skLineSegment(sketch, "E1178.194", {"start": v(-182.6, 196.6) * mm, "end": v(-179.88, 199.24) * mm});
            skLineSegment(sketch, "E1178.195", {"start": v(-179.88, 199.24) * mm, "end": v(-179.2, 199.9) * mm});
            skLineSegment(sketch, "E1178.196", {"start": v(-179.2, 199.9) * mm, "end": v(-178.32, 200.77) * mm});
            skLineSegment(sketch, "E1178.197", {"start": v(-178.32, 200.77) * mm, "end": v(-176.95, 202.12) * mm});
            skLineSegment(sketch, "E1178.198", {"start": v(-176.95, 202.12) * mm, "end": v(-174.82, 204.2) * mm});
            skLineSegment(sketch, "E1178.199", {"start": v(-174.82, 204.2) * mm, "end": v(-173.6, 205.38) * mm});
            skLineSegment(sketch, "E1178.200", {"start": v(-173.6, 205.38) * mm, "end": v(-172.5, 206.5) * mm});
            skLineSegment(sketch, "E1178.201", {"start": v(-172.5, 206.5) * mm, "end": v(-171.93, 207.13) * mm});
            skLineSegment(sketch, "E1178.202", {"start": v(-171.93, 207.13) * mm, "end": v(-170.68, 208.37) * mm});
            skLineSegment(sketch, "E1178.203", {"start": v(-170.68, 208.37) * mm, "end": v(-169.58, 209.5) * mm});
            skLineSegment(sketch, "E1178.204", {"start": v(-169.58, 209.5) * mm, "end": v(-167.77, 211.25) * mm});
            skLineSegment(sketch, "E1178.205", {"start": v(-167.77, 211.25) * mm, "end": v(-167.7, 211.31) * mm});
            skLineSegment(sketch, "E1178.206", {"start": v(-167.7, 211.31) * mm, "end": v(-164.74, 214.17) * mm});
            skLineSegment(sketch, "E1178.207", {"start": v(-164.74, 214.17) * mm, "end": v(-163.5, 215.36) * mm});
            skLineSegment(sketch, "E1178.208", {"start": v(-163.5, 215.36) * mm, "end": v(-162.46, 216.4) * mm});
            skLineSegment(sketch, "E1178.209", {"start": v(-162.46, 216.4) * mm, "end": v(-161.27, 217.52) * mm});
            skLineSegment(sketch, "E1178.210", {"start": v(-161.27, 217.52) * mm, "end": v(-159.88, 218.9) * mm});
            skLineSegment(sketch, "E1178.211", {"start": v(-159.88, 218.9) * mm, "end": v(-157.5, 221.2) * mm});
            skLineSegment(sketch, "E1178.212", {"start": v(-157.5, 221.2) * mm, "end": v(-155.74, 223.72) * mm});
            skLineSegment(sketch, "E1178.213", {"start": v(-155.74, 223.72) * mm, "end": v(-153.56, 226.77) * mm});
            skLineSegment(sketch, "E1178.214", {"start": v(-153.56, 226.77) * mm, "end": v(-151.46, 228) * mm});
            skLineSegment(sketch, "E1178.215", {"start": v(-151.46, 228) * mm, "end": v(-146.95, 231.92) * mm});
            skLineSegment(sketch, "E1178.216", {"start": v(-146.95, 231.92) * mm, "end": v(-146.02, 232.76) * mm});
            skLineSegment(sketch, "E1178.217", {"start": v(-146.02, 232.76) * mm, "end": v(-145.46, 233.3) * mm});
            skLineSegment(sketch, "E1178.218", {"start": v(-145.46, 233.3) * mm, "end": v(-145.02, 233.75) * mm});
            skLineSegment(sketch, "E1178.219", {"start": v(-145.02, 233.75) * mm, "end": v(-142.33, 236.55) * mm});
            skLineSegment(sketch, "E1178.220", {"start": v(-142.33, 236.55) * mm, "end": v(-140.17, 238.78) * mm});
            skLineSegment(sketch, "E1178.221", {"start": v(-140.17, 238.78) * mm, "end": v(-139.85, 239.1) * mm});
            skLineSegment(sketch, "E1178.222", {"start": v(-139.85, 239.1) * mm, "end": v(-136.93, 242.01) * mm});
            skLineSegment(sketch, "E1178.223", {"start": v(-136.93, 242.01) * mm, "end": v(-133.98, 244.72) * mm});
            skLineSegment(sketch, "E1178.224", {"start": v(-133.98, 244.72) * mm, "end": v(-132.4, 246.33) * mm});
            skLineSegment(sketch, "E1178.225", {"start": v(-132.4, 246.33) * mm, "end": v(-130.68, 248.08) * mm});
            skLineSegment(sketch, "E1178.226", {"start": v(-130.68, 248.08) * mm, "end": v(-129.77, 248.96) * mm});
            skLineSegment(sketch, "E1178.227", {"start": v(-129.77, 248.96) * mm, "end": v(-127.31, 251.44) * mm});
            skLineSegment(sketch, "E1178.228", {"start": v(-127.31, 251.44) * mm, "end": v(-125.36, 253.22) * mm});
            skLineSegment(sketch, "E1178.229", {"start": v(-125.36, 253.22) * mm, "end": v(-124.41, 254.1) * mm});
            skLineSegment(sketch, "E1178.230", {"start": v(-124.41, 254.1) * mm, "end": v(-122.24, 255.86) * mm});
            skLineSegment(sketch, "E1178.231", {"start": v(-122.24, 255.86) * mm, "end": v(-120.78, 256.9) * mm});
            skLineSegment(sketch, "E1178.232", {"start": v(-120.78, 256.9) * mm, "end": v(-120.37, 257.2) * mm});
            skLineSegment(sketch, "E1178.233", {"start": v(-120.37, 257.2) * mm, "end": v(-119.08, 258.08) * mm});
            skLineSegment(sketch, "E1178.234", {"start": v(-119.08, 258.08) * mm, "end": v(-118.99, 258.15) * mm});
            skLineSegment(sketch, "E1178.235", {"start": v(-118.99, 258.15) * mm, "end": v(-116.6, 259.57) * mm});
            skLineSegment(sketch, "E1178.236", {"start": v(-116.6, 259.57) * mm, "end": v(-116.1, 259.85) * mm});
            skLineSegment(sketch, "E1178.237", {"start": v(-116.1, 259.85) * mm, "end": v(-116.03, 259.88) * mm});
            skLineSegment(sketch, "E1178.238", {"start": v(-116.03, 259.88) * mm, "end": v(-114.02, 260.85) * mm});
            skLineSegment(sketch, "E1178.239", {"start": v(-114.02, 260.85) * mm, "end": v(-111.81, 261.8) * mm});
            skLineSegment(sketch, "E1178.240", {"start": v(-111.81, 261.8) * mm, "end": v(-110.7, 262.29) * mm});
            skLineSegment(sketch, "E1178.241", {"start": v(-110.7, 262.29) * mm, "end": v(-110.15, 262.5) * mm});
            skLineSegment(sketch, "E1178.242", {"start": v(-110.15, 262.5) * mm, "end": v(-109.3, 262.8) * mm});
            skLineSegment(sketch, "E1178.243", {"start": v(-109.3, 262.8) * mm, "end": v(-107.17, 263.52) * mm});
            skLineSegment(sketch, "E1178.244", {"start": v(-107.17, 263.52) * mm, "end": v(-107.1, 263.54) * mm});
            skLineSegment(sketch, "E1178.245", {"start": v(-107.1, 263.54) * mm, "end": v(-103.9, 264.5) * mm});
            skLineSegment(sketch, "E1178.246", {"start": v(-103.9, 264.5) * mm, "end": v(-102.07, 265) * mm});
            skLineSegment(sketch, "E1178.247", {"start": v(-102.07, 265) * mm, "end": v(-101.05, 265.27) * mm});
            skLineSegment(sketch, "E1178.248", {"start": v(-101.05, 265.27) * mm, "end": v(-99.88, 265.54) * mm});
            skLineSegment(sketch, "E1178.249", {"start": v(-99.88, 265.54) * mm, "end": v(-98.55, 265.9) * mm});
            skLineSegment(sketch, "E1178.250", {"start": v(-98.55, 265.9) * mm, "end": v(-96.6, 266.38) * mm});
            skLineSegment(sketch, "E1178.251", {"start": v(-96.6, 266.38) * mm, "end": v(-94.74, 266.8) * mm});
            skLineSegment(sketch, "E1178.252", {"start": v(-94.74, 266.8) * mm, "end": v(-91.76, 267.48) * mm});
            skLineSegment(sketch, "E1179.0", {"start": v(0.03, 297.22) * mm, "end": v(0.91, 297.38) * mm});
            skLineSegment(sketch, "E1179.1", {"start": v(-0.57, 297.1) * mm, "end": v(0.03, 297.22) * mm});
            skLineSegment(sketch, "E1179.2", {"start": v(-1.17, 297.08) * mm, "end": v(-0.57, 297.1) * mm});
            skLineSegment(sketch, "E1179.3", {"start": v(-3.63, 297.02) * mm, "end": v(-1.17, 297.08) * mm});
            skLineSegment(sketch, "E1179.4", {"start": v(-5.04, 297.02) * mm, "end": v(-3.63, 297.02) * mm});
            skLineSegment(sketch, "E1179.5", {"start": v(-7.41, 297.04) * mm, "end": v(-5.04, 297.02) * mm});
            skLineSegment(sketch, "E1179.6", {"start": v(-9.06, 297.03) * mm, "end": v(-7.41, 297.04) * mm});
            skLineSegment(sketch, "E1179.7", {"start": v(-10.51, 297) * mm, "end": v(-9.06, 297.03) * mm});
            skLineSegment(sketch, "E1179.8", {"start": v(-13.82, 297.07) * mm, "end": v(-10.51, 297) * mm});
            skLineSegment(sketch, "E1179.9", {"start": v(-15.41, 297.08) * mm, "end": v(-13.82, 297.07) * mm});
            skLineSegment(sketch, "E1179.10", {"start": v(-18.2, 297.03) * mm, "end": v(-15.41, 297.08) * mm});
            skLineSegment(sketch, "E1179.11", {"start": v(-22.23, 296.94) * mm, "end": v(-18.2, 297.03) * mm});
            skLineSegment(sketch, "E1179.12", {"start": v(-22.7, 296.93) * mm, "end": v(-22.23, 296.94) * mm});
            skLineSegment(sketch, "E1179.13", {"start": v(-23, 296.92) * mm, "end": v(-22.7, 296.93) * mm});
            skLineSegment(sketch, "E1179.14", {"start": v(-26.22, 296.77) * mm, "end": v(-23, 296.92) * mm});
            skLineSegment(sketch, "E1179.15", {"start": v(-28.24, 296.7) * mm, "end": v(-26.22, 296.77) * mm});
            skLineSegment(sketch, "E1179.16", {"start": v(-29.87, 296.64) * mm, "end": v(-28.24, 296.7) * mm});
            skLineSegment(sketch, "E1179.17", {"start": v(-33.39, 296.42) * mm, "end": v(-29.87, 296.64) * mm});
            skLineSegment(sketch, "E1179.18", {"start": v(-36.13, 296.12) * mm, "end": v(-33.39, 296.42) * mm});
            skLineSegment(sketch, "E1179.19", {"start": v(-38, 296.05) * mm, "end": v(-36.13, 296.12) * mm});
            skLineSegment(sketch, "E1179.20", {"start": v(-40.2, 295.87) * mm, "end": v(-38, 296.05) * mm});
            skLineSegment(sketch, "E1179.21", {"start": v(-40.9, 295.82) * mm, "end": v(-40.2, 295.87) * mm});
            skLineSegment(sketch, "E1179.22", {"start": v(-42.7, 295.59) * mm, "end": v(-40.9, 295.82) * mm});
            skLineSegment(sketch, "E1179.23", {"start": v(-45.06, 295.5) * mm, "end": v(-42.7, 295.59) * mm});
            skLineSegment(sketch, "E1179.24", {"start": v(-45.29, 295.47) * mm, "end": v(-45.06, 295.5) * mm});
            skLineSegment(sketch, "E1179.25", {"start": v(-45.93, 295.4) * mm, "end": v(-45.29, 295.47) * mm});
            skLineSegment(sketch, "E1179.26", {"start": v(-48.13, 295.13) * mm, "end": v(-45.93, 295.4) * mm});
            skLineSegment(sketch, "E1179.27", {"start": v(-48.98, 295.06) * mm, "end": v(-48.13, 295.13) * mm});
            skLineSegment(sketch, "E1179.28", {"start": v(-50.84, 294.82) * mm, "end": v(-48.98, 295.06) * mm});
            skLineSegment(sketch, "E1179.29", {"start": v(-53.4, 294.55) * mm, "end": v(-50.84, 294.82) * mm});
            skLineSegment(sketch, "E1179.30", {"start": v(-53.74, 294.5) * mm, "end": v(-53.4, 294.55) * mm});
            skLineSegment(sketch, "E1179.31", {"start": v(-53.99, 294.48) * mm, "end": v(-53.74, 294.5) * mm});
            skLineSegment(sketch, "E1179.32", {"start": v(-54.65, 294.41) * mm, "end": v(-53.99, 294.48) * mm});
            skLineSegment(sketch, "E1179.33", {"start": v(-57.78, 294.03) * mm, "end": v(-54.65, 294.41) * mm});
            skLineSegment(sketch, "E1179.34", {"start": v(-59.92, 293.78) * mm, "end": v(-57.78, 294.03) * mm});
            skLineSegment(sketch, "E1179.35", {"start": v(-61.23, 293.59) * mm, "end": v(-59.92, 293.78) * mm});
            skLineSegment(sketch, "E1179.36", {"start": v(-61.8, 293.52) * mm, "end": v(-61.23, 293.59) * mm});
            skLineSegment(sketch, "E1179.37", {"start": v(-64.38, 293.13) * mm, "end": v(-61.8, 293.52) * mm});
            skLineSegment(sketch, "E1179.38", {"start": v(-66.08, 292.85) * mm, "end": v(-64.38, 293.13) * mm});
            skLineSegment(sketch, "E1179.39", {"start": v(-68.43, 292.47) * mm, "end": v(-66.08, 292.85) * mm});
            skLineSegment(sketch, "E1179.40", {"start": v(-71.94, 291.9) * mm, "end": v(-68.43, 292.47) * mm});
            skLineSegment(sketch, "E1179.41", {"start": v(-73.08, 291.7) * mm, "end": v(-71.94, 291.9) * mm});
            skLineSegment(sketch, "E1179.42", {"start": v(-73.47, 291.63) * mm, "end": v(-73.08, 291.7) * mm});
            skLineSegment(sketch, "E1179.43", {"start": v(-75.42, 291.27) * mm, "end": v(-73.47, 291.63) * mm});
            skLineSegment(sketch, "E1179.44", {"start": v(-78.04, 290.85) * mm, "end": v(-75.42, 291.27) * mm});
            skLineSegment(sketch, "E1179.45", {"start": v(-78.06, 290.85) * mm, "end": v(-78.04, 290.85) * mm});
            skLineSegment(sketch, "E1179.46", {"start": v(-78.15, 290.83) * mm, "end": v(-78.06, 290.85) * mm});
            skLineSegment(sketch, "E1179.47", {"start": v(-81.26, 290.17) * mm, "end": v(-78.15, 290.83) * mm});
            skLineSegment(sketch, "E1179.48", {"start": v(-82.96, 289.87) * mm, "end": v(-81.26, 290.17) * mm});
            skLineSegment(sketch, "E1179.49", {"start": v(-85.6, 289.37) * mm, "end": v(-82.96, 289.87) * mm});
            skLineSegment(sketch, "E1179.50", {"start": v(-86.07, 289.27) * mm, "end": v(-85.6, 289.37) * mm});
            skLineSegment(sketch, "E1179.51", {"start": v(-86.5, 289.18) * mm, "end": v(-86.07, 289.27) * mm});
            skLineSegment(sketch, "E1179.52", {"start": v(-87.07, 289.07) * mm, "end": v(-86.5, 289.18) * mm});
            skLineSegment(sketch, "E1179.53", {"start": v(-88.53, 288.74) * mm, "end": v(-87.07, 289.07) * mm});
            skLineSegment(sketch, "E1179.54", {"start": v(-89.23, 288.6) * mm, "end": v(-88.53, 288.74) * mm});
            skLineSegment(sketch, "E1179.55", {"start": v(-91.18, 288.2) * mm, "end": v(-89.23, 288.6) * mm});
            skLineSegment(sketch, "E1179.56", {"start": v(-91.82, 288.05) * mm, "end": v(-91.18, 288.2) * mm});
            skLineSegment(sketch, "E1179.57", {"start": v(-92.19, 287.97) * mm, "end": v(-91.82, 288.05) * mm});
            skLineSegment(sketch, "E1179.58", {"start": v(-92.58, 287.89) * mm, "end": v(-92.19, 287.97) * mm});
            skLineSegment(sketch, "E1179.59", {"start": v(-96.4, 286.94) * mm, "end": v(-92.58, 287.89) * mm});
            skLineSegment(sketch, "E1179.60", {"start": v(-99.2, 286.3) * mm, "end": v(-96.4, 286.94) * mm});
            skLineSegment(sketch, "E1179.61", {"start": v(-101.17, 285.85) * mm, "end": v(-99.2, 286.3) * mm});
            skLineSegment(sketch, "E1179.62", {"start": v(-103.55, 285.27) * mm, "end": v(-101.17, 285.85) * mm});
            skLineSegment(sketch, "E1179.63", {"start": v(-104.8, 284.93) * mm, "end": v(-103.55, 285.27) * mm});
            skLineSegment(sketch, "E1179.64", {"start": v(-105.77, 284.7) * mm, "end": v(-104.8, 284.93) * mm});
            skLineSegment(sketch, "E1179.65", {"start": v(-107.19, 284.34) * mm, "end": v(-105.77, 284.7) * mm});
            skLineSegment(sketch, "E1179.66", {"start": v(-109.41, 283.73) * mm, "end": v(-107.19, 284.34) * mm});
            skLineSegment(sketch, "E1179.67", {"start": v(-112.9, 282.69) * mm, "end": v(-109.41, 283.73) * mm});
            skLineSegment(sketch, "E1179.68", {"start": v(-113.22, 282.59) * mm, "end": v(-112.9, 282.69) * mm});
            skLineSegment(sketch, "E1179.69", {"start": v(-113.4, 282.53) * mm, "end": v(-113.22, 282.59) * mm});
            skLineSegment(sketch, "E1179.70", {"start": v(-115.83, 281.71) * mm, "end": v(-113.4, 282.53) * mm});
            skLineSegment(sketch, "E1179.71", {"start": v(-117.15, 281.25) * mm, "end": v(-115.83, 281.71) * mm});
            skLineSegment(sketch, "E1179.72", {"start": v(-118.33, 280.78) * mm, "end": v(-117.15, 281.25) * mm});
            skLineSegment(sketch, "E1179.73", {"start": v(-119.79, 280.15) * mm, "end": v(-118.33, 280.78) * mm});
            skLineSegment(sketch, "E1179.74", {"start": v(-122.36, 279.03) * mm, "end": v(-119.79, 280.15) * mm});
            skLineSegment(sketch, "E1179.75", {"start": v(-124.97, 277.77) * mm, "end": v(-122.36, 279.03) * mm});
            skLineSegment(sketch, "E1179.76", {"start": v(-125.37, 277.56) * mm, "end": v(-124.97, 277.77) * mm});
            skLineSegment(sketch, "E1179.77", {"start": v(-126.27, 277.09) * mm, "end": v(-125.37, 277.56) * mm});
            skLineSegment(sketch, "E1179.78", {"start": v(-126.62, 276.9) * mm, "end": v(-126.27, 277.09) * mm});
            skLineSegment(sketch, "E1179.79", {"start": v(-129.72, 275.03) * mm, "end": v(-126.62, 276.9) * mm});
            skLineSegment(sketch, "E1179.80", {"start": v(-130.37, 274.6) * mm, "end": v(-129.72, 275.03) * mm});
            skLineSegment(sketch, "E1179.81", {"start": v(-131.85, 273.57) * mm, "end": v(-130.37, 274.6) * mm});
            skLineSegment(sketch, "E1179.82", {"start": v(-132.4, 273.19) * mm, "end": v(-131.85, 273.57) * mm});
            skLineSegment(sketch, "E1179.83", {"start": v(-134.2, 271.9) * mm, "end": v(-132.4, 273.19) * mm});
            skLineSegment(sketch, "E1179.84", {"start": v(-134.5, 271.67) * mm, "end": v(-134.2, 271.9) * mm});
            skLineSegment(sketch, "E1179.85", {"start": v(-137.28, 269.41) * mm, "end": v(-134.5, 271.67) * mm});
            skLineSegment(sketch, "E1179.86", {"start": v(-137.46, 269.26) * mm, "end": v(-137.28, 269.41) * mm});
            skLineSegment(sketch, "E1179.87", {"start": v(-138.85, 267.99) * mm, "end": v(-137.46, 269.26) * mm});
            skLineSegment(sketch, "E1179.88", {"start": v(-141.02, 266) * mm, "end": v(-138.85, 267.99) * mm});
            skLineSegment(sketch, "E1179.89", {"start": v(-141.2, 265.84) * mm, "end": v(-141.02, 266) * mm});
            skLineSegment(sketch, "E1179.90", {"start": v(-141.27, 265.77) * mm, "end": v(-141.2, 265.84) * mm});
            skLineSegment(sketch, "E1179.91", {"start": v(-273.43, 147.92) * mm, "end": v(-273.3, 148.02) * mm});
            skLineSegment(sketch, "E1179.92", {"start": v(-276.58, 145.2) * mm, "end": v(-273.43, 147.92) * mm});
            skLineSegment(sketch, "E1179.93", {"start": v(-276.59, 145.18) * mm, "end": v(-276.58, 145.2) * mm});
            skLineSegment(sketch, "E1179.94", {"start": v(-280.01, 142.02) * mm, "end": v(-276.59, 145.18) * mm});
            skLineSegment(sketch, "E1179.95", {"start": v(-281.4, 140.72) * mm, "end": v(-280.01, 142.02) * mm});
            skLineSegment(sketch, "E1179.96", {"start": v(-281.79, 140.34) * mm, "end": v(-281.4, 140.72) * mm});
            skLineSegment(sketch, "E1179.97", {"start": v(-283.48, 138.66) * mm, "end": v(-281.79, 140.34) * mm});
            skLineSegment(sketch, "E1179.98", {"start": v(-285.83, 136.2) * mm, "end": v(-283.48, 138.66) * mm});
            skLineSegment(sketch, "E1179.99", {"start": v(-286.42, 135.57) * mm, "end": v(-285.83, 136.2) * mm});
            skLineSegment(sketch, "E1179.100", {"start": v(-288.21, 133.65) * mm, "end": v(-286.42, 135.57) * mm});
            skLineSegment(sketch, "E1179.101", {"start": v(-289.51, 132.24) * mm, "end": v(-288.21, 133.65) * mm});
            skLineSegment(sketch, "E1179.102", {"start": v(-290.21, 131.43) * mm, "end": v(-289.51, 132.24) * mm});
            skLineSegment(sketch, "E1179.103", {"start": v(-290.73, 130.84) * mm, "end": v(-290.21, 131.43) * mm});
            skLineSegment(sketch, "E1179.104", {"start": v(-292.58, 128.52) * mm, "end": v(-290.73, 130.84) * mm});
            skLineSegment(sketch, "E1179.105", {"start": v(-293.44, 127.46) * mm, "end": v(-292.58, 128.52) * mm});
            skLineSegment(sketch, "E1179.106", {"start": v(-294.85, 125.83) * mm, "end": v(-293.44, 127.46) * mm});
            skLineSegment(sketch, "E1179.107", {"start": v(-296.4, 123.73) * mm, "end": v(-294.85, 125.83) * mm});
            skLineSegment(sketch, "E1179.108", {"start": v(-296.69, 123.39) * mm, "end": v(-296.4, 123.73) * mm});
            skLineSegment(sketch, "E1179.109", {"start": v(-298.7, 120.7) * mm, "end": v(-296.69, 123.39) * mm});
            skLineSegment(sketch, "E1179.110", {"start": v(-298.78, 120.58) * mm, "end": v(-298.7, 120.7) * mm});
            skLineSegment(sketch, "E1179.111", {"start": v(-298.94, 120.37) * mm, "end": v(-298.78, 120.58) * mm});
            skLineSegment(sketch, "E1179.112", {"start": v(-300.42, 118.37) * mm, "end": v(-298.94, 120.37) * mm});
            skLineSegment(sketch, "E1179.113", {"start": v(-300.98, 117.55) * mm, "end": v(-300.42, 118.37) * mm});
            skLineSegment(sketch, "E1179.114", {"start": v(-301.92, 116.16) * mm, "end": v(-300.98, 117.55) * mm});
            skLineSegment(sketch, "E1179.115", {"start": v(-302.9, 114.6) * mm, "end": v(-301.92, 116.16) * mm});
            skLineSegment(sketch, "E1179.116", {"start": v(-303.47, 113.72) * mm, "end": v(-302.9, 114.6) * mm});
            skLineSegment(sketch, "E1179.117", {"start": v(-304.05, 112.86) * mm, "end": v(-303.47, 113.72) * mm});
            skLineSegment(sketch, "E1179.118", {"start": v(-304.79, 111.71) * mm, "end": v(-304.05, 112.86) * mm});
            skLineSegment(sketch, "E1179.119", {"start": v(-305.9, 109.76) * mm, "end": v(-304.79, 111.71) * mm});
            skLineSegment(sketch, "E1179.120", {"start": v(-306.44, 108.8) * mm, "end": v(-305.9, 109.76) * mm});
            skLineSegment(sketch, "E1179.121", {"start": v(-308.33, 105.67) * mm, "end": v(-306.44, 108.8) * mm});
            skLineSegment(sketch, "E1179.122", {"start": v(-308.4, 105.56) * mm, "end": v(-308.33, 105.67) * mm});
            skLineSegment(sketch, "E1179.123", {"start": v(-308.52, 105.34) * mm, "end": v(-308.4, 105.56) * mm});
            skLineSegment(sketch, "E1179.124", {"start": v(-309.9, 102.82) * mm, "end": v(-308.52, 105.34) * mm});
            skLineSegment(sketch, "E1179.125", {"start": v(-310.17, 102.3) * mm, "end": v(-309.9, 102.82) * mm});
            skLineSegment(sketch, "E1179.126", {"start": v(-310.8, 100.94) * mm, "end": v(-310.17, 102.3) * mm});
            skLineSegment(sketch, "E1179.127", {"start": v(-311.47, 99.5) * mm, "end": v(-310.8, 100.94) * mm});
            skLineSegment(sketch, "E1179.128", {"start": v(-311.8, 98.78) * mm, "end": v(-311.47, 99.5) * mm});
            skLineSegment(sketch, "E1179.129", {"start": v(-312.76, 96.79) * mm, "end": v(-311.8, 98.78) * mm});
            skLineSegment(sketch, "E1179.130", {"start": v(-313.05, 96.14) * mm, "end": v(-312.76, 96.79) * mm});
            skLineSegment(sketch, "E1179.131", {"start": v(-314.97, 91.89) * mm, "end": v(-313.05, 96.14) * mm});
            skLineSegment(sketch, "E1179.132", {"start": v(-315.16, 91.45) * mm, "end": v(-314.97, 91.89) * mm});
            skLineSegment(sketch, "E1179.133", {"start": v(-315.33, 91.05) * mm, "end": v(-315.16, 91.45) * mm});
            skLineSegment(sketch, "E1179.134", {"start": v(-316.68, 87.68) * mm, "end": v(-315.33, 91.05) * mm});
            skLineSegment(sketch, "E1179.135", {"start": v(-317.01, 86.88) * mm, "end": v(-316.68, 87.68) * mm});
            skLineSegment(sketch, "E1179.136", {"start": v(-317.32, 86.05) * mm, "end": v(-317.01, 86.88) * mm});
            skLineSegment(sketch, "E1179.137", {"start": v(-318.11, 83.73) * mm, "end": v(-317.32, 86.05) * mm});
            skLineSegment(sketch, "E1179.138", {"start": v(-318.55, 82.45) * mm, "end": v(-318.11, 83.73) * mm});
            skLineSegment(sketch, "E1179.139", {"start": v(-319.97, 78.56) * mm, "end": v(-318.55, 82.45) * mm});
            skLineSegment(sketch, "E1179.140", {"start": v(-320.14, 78.07) * mm, "end": v(-319.97, 78.56) * mm});
            skLineSegment(sketch, "E1179.141", {"start": v(-327.22, 38.11) * mm, "end": v(-327.17, 39.2) * mm});
            skLineSegment(sketch, "E1179.142", {"start": v(-327.3, 35.23) * mm, "end": v(-327.22, 38.11) * mm});
            skLineSegment(sketch, "E1179.143", {"start": v(-327.4, 32.96) * mm, "end": v(-327.3, 35.23) * mm});
            skLineSegment(sketch, "E1179.144", {"start": v(-327.43, 31.2) * mm, "end": v(-327.4, 32.96) * mm});
            skLineSegment(sketch, "E1179.145", {"start": v(-327.48, 28.36) * mm, "end": v(-327.43, 31.2) * mm});
            skLineSegment(sketch, "E1179.146", {"start": v(-327.5, 26.94) * mm, "end": v(-327.48, 28.36) * mm});
            skLineSegment(sketch, "E1179.147", {"start": v(-327.44, 24.42) * mm, "end": v(-327.5, 26.94) * mm});
            skLineSegment(sketch, "E1179.148", {"start": v(-327.5, 23.06) * mm, "end": v(-327.44, 24.42) * mm});
            skLineSegment(sketch, "E1179.149", {"start": v(-327.48, 20.45) * mm, "end": v(-327.5, 23.06) * mm});
            skLineSegment(sketch, "E1179.150", {"start": v(-327.4, 17.24) * mm, "end": v(-327.48, 20.45) * mm});
            skLineSegment(sketch, "E1179.151", {"start": v(-327.32, 15.47) * mm, "end": v(-327.4, 17.24) * mm});
            skLineSegment(sketch, "E1179.152", {"start": v(-327.2, 13.45) * mm, "end": v(-327.32, 15.47) * mm});
            skLineSegment(sketch, "E1179.153", {"start": v(-325.67, 2.48) * mm, "end": v(-326.11, 4.73) * mm});
            skLineSegment(sketch, "E1179.154", {"start": v(-325.5, 1.62) * mm, "end": v(-325.67, 2.48) * mm});
            skLineSegment(sketch, "E1179.155", {"start": v(-325.45, 1.36) * mm, "end": v(-325.5, 1.62) * mm});
            skLineSegment(sketch, "E1179.156", {"start": v(-325.36, 0.54) * mm, "end": v(-325.45, 1.36) * mm});
            skLineSegment(sketch, "E1179.157", {"start": v(-326.11, 4.73) * mm, "end": v(-326.2, 5.2) * mm});
            skLineSegment(sketch, "E1179.158", {"start": v(-326.2, 5.2) * mm, "end": v(-326.24, 5.41) * mm});
            skLineSegment(sketch, "E1179.159", {"start": v(-326.24, 5.41) * mm, "end": v(-326.4, 6.41) * mm});
            skLineSegment(sketch, "E1179.160", {"start": v(-326.4, 6.41) * mm, "end": v(-326.7, 8.4) * mm});
            skLineSegment(sketch, "E1179.161", {"start": v(-326.7, 8.4) * mm, "end": v(-326.86, 10.1) * mm});
            skLineSegment(sketch, "E1179.162", {"start": v(-326.86, 10.1) * mm, "end": v(-327.2, 13.45) * mm});
            skLineSegment(sketch, "E1179.163", {"start": v(-327.17, 39.2) * mm, "end": v(-327.08, 40.48) * mm});
            skLineSegment(sketch, "E1179.164", {"start": v(-327.08, 40.48) * mm, "end": v(-326.99, 41.82) * mm});
            skLineSegment(sketch, "E1179.165", {"start": v(-326.99, 41.82) * mm, "end": v(-326.67, 43.94) * mm});
            skLineSegment(sketch, "E1179.166", {"start": v(-326.67, 43.94) * mm, "end": v(-326.55, 45.14) * mm});
            skLineSegment(sketch, "E1179.167", {"start": v(-326.55, 45.14) * mm, "end": v(-326.23, 48.43) * mm});
            skLineSegment(sketch, "E1179.168", {"start": v(-326.23, 48.43) * mm, "end": v(-326.22, 48.56) * mm});
            skLineSegment(sketch, "E1179.169", {"start": v(-326.22, 48.56) * mm, "end": v(-326.13, 49.33) * mm});
            skLineSegment(sketch, "E1179.170", {"start": v(-326.13, 49.33) * mm, "end": v(-325.78, 52.33) * mm});
            skLineSegment(sketch, "E1179.171", {"start": v(-325.78, 52.33) * mm, "end": v(-325.65, 53.36) * mm});
            skLineSegment(sketch, "E1179.172", {"start": v(-325.65, 53.36) * mm, "end": v(-325.41, 54.96) * mm});
            skLineSegment(sketch, "E1179.173", {"start": v(-325.41, 54.96) * mm, "end": v(-325.16, 56.53) * mm});
            skLineSegment(sketch, "E1179.174", {"start": v(-325.16, 56.53) * mm, "end": v(-324.97, 57.8) * mm});
            skLineSegment(sketch, "E1179.175", {"start": v(-324.97, 57.8) * mm, "end": v(-324.73, 59.13) * mm});
            skLineSegment(sketch, "E1179.176", {"start": v(-324.73, 59.13) * mm, "end": v(-324.5, 60.48) * mm});
            skLineSegment(sketch, "E1179.177", {"start": v(-324.5, 60.48) * mm, "end": v(-324.28, 61.57) * mm});
            skLineSegment(sketch, "E1179.178", {"start": v(-324.28, 61.57) * mm, "end": v(-324.07, 62.68) * mm});
            skLineSegment(sketch, "E1179.179", {"start": v(-324.07, 62.68) * mm, "end": v(-323.74, 64.16) * mm});
            skLineSegment(sketch, "E1179.180", {"start": v(-323.74, 64.16) * mm, "end": v(-323.5, 65.21) * mm});
            skLineSegment(sketch, "E1179.181", {"start": v(-323.5, 65.21) * mm, "end": v(-323.02, 67.3) * mm});
            skLineSegment(sketch, "E1179.182", {"start": v(-323.02, 67.3) * mm, "end": v(-322.08, 71.47) * mm});
            skLineSegment(sketch, "E1179.183", {"start": v(-322.08, 71.47) * mm, "end": v(-320.93, 75.34) * mm});
            skLineSegment(sketch, "E1179.184", {"start": v(-320.93, 75.34) * mm, "end": v(-320.69, 76.2) * mm});
            skLineSegment(sketch, "E1179.185", {"start": v(-320.69, 76.2) * mm, "end": v(-320.27, 77.7) * mm});
            skLineSegment(sketch, "E1179.186", {"start": v(-320.27, 77.7) * mm, "end": v(-320.14, 78.07) * mm});
            skLineSegment(sketch, "E1179.187", {"start": v(-273.3, 148.02) * mm, "end": v(-272.77, 148.45) * mm});
            skLineSegment(sketch, "E1179.188", {"start": v(-272.77, 148.45) * mm, "end": v(-269.97, 150.64) * mm});
            skLineSegment(sketch, "E1179.189", {"start": v(-269.97, 150.64) * mm, "end": v(-268.48, 151.81) * mm});
            skLineSegment(sketch, "E1179.190", {"start": v(-268.48, 151.81) * mm, "end": v(-266.6, 153.3) * mm});
            skLineSegment(sketch, "E1179.191", {"start": v(-266.6, 153.3) * mm, "end": v(-263.85, 155.33) * mm});
            skLineSegment(sketch, "E1179.192", {"start": v(-263.85, 155.33) * mm, "end": v(-262.95, 155.98) * mm});
            skLineSegment(sketch, "E1179.193", {"start": v(-262.95, 155.98) * mm, "end": v(-262.11, 156.6) * mm});
            skLineSegment(sketch, "E1179.194", {"start": v(-262.11, 156.6) * mm, "end": v(-260.67, 157.67) * mm});
            skLineSegment(sketch, "E1179.195", {"start": v(-260.67, 157.67) * mm, "end": v(-260.04, 158.07) * mm});
            skLineSegment(sketch, "E1179.196", {"start": v(-260.04, 158.07) * mm, "end": v(-258.42, 159.2) * mm});
            skLineSegment(sketch, "E1179.197", {"start": v(-258.42, 159.2) * mm, "end": v(-258.28, 159.3) * mm});
            skLineSegment(sketch, "E1179.198", {"start": v(-258.28, 159.3) * mm, "end": v(-255.7, 160.7) * mm});
            skLineSegment(sketch, "E1179.199", {"start": v(-255.7, 160.7) * mm, "end": v(-255.47, 160.85) * mm});
            skLineSegment(sketch, "E1179.200", {"start": v(-255.47, 160.85) * mm, "end": v(-252.3, 162.77) * mm});
            skLineSegment(sketch, "E1179.201", {"start": v(-252.3, 162.77) * mm, "end": v(-251.6, 163.29) * mm});
            skLineSegment(sketch, "E1179.202", {"start": v(-251.6, 163.29) * mm, "end": v(-249.4, 165.2) * mm});
            skLineSegment(sketch, "E1179.203", {"start": v(-249.4, 165.2) * mm, "end": v(-247.94, 166.26) * mm});
            skLineSegment(sketch, "E1179.204", {"start": v(-247.94, 166.26) * mm, "end": v(-245.8, 167.78) * mm});
            skLineSegment(sketch, "E1179.205", {"start": v(-245.8, 167.78) * mm, "end": v(-245.25, 168.17) * mm});
            skLineSegment(sketch, "E1179.206", {"start": v(-245.25, 168.17) * mm, "end": v(-242.79, 169.97) * mm});
            skLineSegment(sketch, "E1179.207", {"start": v(-242.79, 169.97) * mm, "end": v(-239.5, 172.2) * mm});
            skLineSegment(sketch, "E1179.208", {"start": v(-239.5, 172.2) * mm, "end": v(-239.25, 172.36) * mm});
            skLineSegment(sketch, "E1179.209", {"start": v(-239.25, 172.36) * mm, "end": v(-238.94, 172.59) * mm});
            skLineSegment(sketch, "E1179.210", {"start": v(-238.94, 172.59) * mm, "end": v(-236.64, 174.35) * mm});
            skLineSegment(sketch, "E1179.211", {"start": v(-236.64, 174.35) * mm, "end": v(-235.6, 175.07) * mm});
            skLineSegment(sketch, "E1179.212", {"start": v(-235.6, 175.07) * mm, "end": v(-234.68, 175.75) * mm});
            skLineSegment(sketch, "E1179.213", {"start": v(-234.68, 175.75) * mm, "end": v(-232.81, 176.72) * mm});
            skLineSegment(sketch, "E1179.214", {"start": v(-232.81, 176.72) * mm, "end": v(-232.08, 177.15) * mm});
            skLineSegment(sketch, "E1179.215", {"start": v(-232.08, 177.15) * mm, "end": v(-230.26, 178.23) * mm});
            skLineSegment(sketch, "E1179.216", {"start": v(-230.26, 178.23) * mm, "end": v(-229.62, 178.78) * mm});
            skLineSegment(sketch, "E1179.217", {"start": v(-229.62, 178.78) * mm, "end": v(-229.2, 179.17) * mm});
            skLineSegment(sketch, "E1179.218", {"start": v(-229.2, 179.17) * mm, "end": v(-227.58, 180.7) * mm});
            skLineSegment(sketch, "E1179.219", {"start": v(-227.58, 180.7) * mm, "end": v(-226, 182.23) * mm});
            skLineSegment(sketch, "E1179.220", {"start": v(-226, 182.23) * mm, "end": v(-224.53, 183.7) * mm});
            skLineSegment(sketch, "E1179.221", {"start": v(-224.53, 183.7) * mm, "end": v(-222.38, 185.8) * mm});
            skLineSegment(sketch, "E1179.222", {"start": v(-222.38, 185.8) * mm, "end": v(-221.94, 186.24) * mm});
            skLineSegment(sketch, "E1179.223", {"start": v(-221.94, 186.24) * mm, "end": v(-221.59, 186.57) * mm});
            skLineSegment(sketch, "E1179.224", {"start": v(-221.59, 186.57) * mm, "end": v(-218.52, 189.4) * mm});
            skLineSegment(sketch, "E1179.225", {"start": v(-218.52, 189.4) * mm, "end": v(-218.21, 189.68) * mm});
            skLineSegment(sketch, "E1179.226", {"start": v(-218.21, 189.68) * mm, "end": v(-217.8, 190.1) * mm});
            skLineSegment(sketch, "E1179.227", {"start": v(-217.8, 190.1) * mm, "end": v(-215.88, 192.1) * mm});
            skLineSegment(sketch, "E1179.228", {"start": v(-215.88, 192.1) * mm, "end": v(-213.8, 194.16) * mm});
            skLineSegment(sketch, "E1179.229", {"start": v(-213.8, 194.16) * mm, "end": v(-213.52, 194.44) * mm});
            skLineSegment(sketch, "E1179.230", {"start": v(-213.52, 194.44) * mm, "end": v(-212.07, 195.85) * mm});
            skLineSegment(sketch, "E1179.231", {"start": v(-212.07, 195.85) * mm, "end": v(-209.55, 198.3) * mm});
            skLineSegment(sketch, "E1179.232", {"start": v(-209.55, 198.3) * mm, "end": v(-209.28, 198.56) * mm});
            skLineSegment(sketch, "E1179.233", {"start": v(-209.28, 198.56) * mm, "end": v(-208.52, 199.33) * mm});
            skLineSegment(sketch, "E1179.234", {"start": v(-208.52, 199.33) * mm, "end": v(-204.82, 202.92) * mm});
            skLineSegment(sketch, "E1179.235", {"start": v(-204.82, 202.92) * mm, "end": v(-203.1, 204.61) * mm});
            skLineSegment(sketch, "E1179.236", {"start": v(-203.1, 204.61) * mm, "end": v(-201.75, 205.9) * mm});
            skLineSegment(sketch, "E1179.237", {"start": v(-201.75, 205.9) * mm, "end": v(-201.37, 206.32) * mm});
            skLineSegment(sketch, "E1179.238", {"start": v(-201.37, 206.32) * mm, "end": v(-200.26, 207.46) * mm});
            skLineSegment(sketch, "E1179.239", {"start": v(-200.26, 207.46) * mm, "end": v(-199.42, 208.26) * mm});
            skLineSegment(sketch, "E1179.240", {"start": v(-199.42, 208.26) * mm, "end": v(-196.88, 210.64) * mm});
            skLineSegment(sketch, "E1179.241", {"start": v(-196.88, 210.64) * mm, "end": v(-196.54, 210.96) * mm});
            skLineSegment(sketch, "E1179.242", {"start": v(-196.54, 210.96) * mm, "end": v(-196.32, 211.16) * mm});
            skLineSegment(sketch, "E1179.243", {"start": v(-196.32, 211.16) * mm, "end": v(-193.83, 213.57) * mm});
            skLineSegment(sketch, "E1179.244", {"start": v(-193.83, 213.57) * mm, "end": v(-193.23, 214.15) * mm});
            skLineSegment(sketch, "E1179.245", {"start": v(-193.23, 214.15) * mm, "end": v(-192.35, 215.04) * mm});
            skLineSegment(sketch, "E1179.246", {"start": v(-192.35, 215.04) * mm, "end": v(-190.92, 216.42) * mm});
            skLineSegment(sketch, "E1179.247", {"start": v(-190.92, 216.42) * mm, "end": v(-188.8, 218.5) * mm});
            skLineSegment(sketch, "E1179.248", {"start": v(-188.8, 218.5) * mm, "end": v(-187.68, 219.6) * mm});
            skLineSegment(sketch, "E1179.249", {"start": v(-187.68, 219.6) * mm, "end": v(-187.05, 220.23) * mm});
            skLineSegment(sketch, "E1179.250", {"start": v(-187.05, 220.23) * mm, "end": v(-186.43, 220.92) * mm});
            skLineSegment(sketch, "E1179.251", {"start": v(-186.43, 220.92) * mm, "end": v(-184.85, 222.48) * mm});
            skLineSegment(sketch, "E1179.252", {"start": v(-184.85, 222.48) * mm, "end": v(-183.68, 223.68) * mm});
            skLineSegment(sketch, "E1179.253", {"start": v(-183.68, 223.68) * mm, "end": v(-183.62, 223.74) * mm});
            skLineSegment(sketch, "E1179.254", {"start": v(-183.62, 223.74) * mm, "end": v(-181.68, 225.62) * mm});
            skLineSegment(sketch, "E1179.255", {"start": v(-181.68, 225.62) * mm, "end": v(-181.57, 225.73) * mm});
            skLineSegment(sketch, "E1179.256", {"start": v(-181.57, 225.73) * mm, "end": v(-178.6, 228.6) * mm});
            skLineSegment(sketch, "E1179.257", {"start": v(-178.6, 228.6) * mm, "end": v(-177.46, 229.68) * mm});
            skLineSegment(sketch, "E1179.258", {"start": v(-177.46, 229.68) * mm, "end": v(-176.39, 230.74) * mm});
            skLineSegment(sketch, "E1179.259", {"start": v(-176.39, 230.74) * mm, "end": v(-175.23, 231.84) * mm});
            skLineSegment(sketch, "E1179.260", {"start": v(-175.23, 231.84) * mm, "end": v(-173.88, 233.2) * mm});
            skLineSegment(sketch, "E1179.261", {"start": v(-173.88, 233.2) * mm, "end": v(-172.78, 234.25) * mm});
            skLineSegment(sketch, "E1179.262", {"start": v(-172.78, 234.25) * mm, "end": v(-172.08, 235.26) * mm});
            skLineSegment(sketch, "E1179.263", {"start": v(-172.08, 235.26) * mm, "end": v(-171.01, 236.74) * mm});
            skLineSegment(sketch, "E1179.264", {"start": v(-171.01, 236.74) * mm, "end": v(-170.52, 237.82) * mm});
            skLineSegment(sketch, "E1179.265", {"start": v(-170.52, 237.82) * mm, "end": v(-170.3, 238.27) * mm});
            skLineSegment(sketch, "E1179.266", {"start": v(-170.3, 238.27) * mm, "end": v(-169.7, 239.2) * mm});
            skLineSegment(sketch, "E1179.267", {"start": v(-169.7, 239.2) * mm, "end": v(-169.35, 239.8) * mm});
            skLineSegment(sketch, "E1179.268", {"start": v(-169.35, 239.8) * mm, "end": v(-169.23, 239.91) * mm});
            skLineSegment(sketch, "E1179.269", {"start": v(-169.23, 239.91) * mm, "end": v(-167.14, 241.9) * mm});
            skLineSegment(sketch, "E1179.270", {"start": v(-167.14, 241.9) * mm, "end": v(-167.05, 241.97) * mm});
            skLineSegment(sketch, "E1179.271", {"start": v(-167.05, 241.97) * mm, "end": v(-165.5, 242.96) * mm});
            skLineSegment(sketch, "E1179.272", {"start": v(-165.5, 242.96) * mm, "end": v(-164.95, 243.27) * mm});
            skLineSegment(sketch, "E1179.273", {"start": v(-164.95, 243.27) * mm, "end": v(-163.18, 244.3) * mm});
            skLineSegment(sketch, "E1179.274", {"start": v(-163.18, 244.3) * mm, "end": v(-160.2, 246.9) * mm});
            skLineSegment(sketch, "E1179.275", {"start": v(-160.2, 246.9) * mm, "end": v(-159.74, 247.31) * mm});
            skLineSegment(sketch, "E1179.276", {"start": v(-159.74, 247.31) * mm, "end": v(-159.57, 247.48) * mm});
            skLineSegment(sketch, "E1179.277", {"start": v(-159.57, 247.48) * mm, "end": v(-159.32, 247.73) * mm});
            skLineSegment(sketch, "E1179.278", {"start": v(-159.32, 247.73) * mm, "end": v(-156.72, 250.44) * mm});
            skLineSegment(sketch, "E1179.279", {"start": v(-156.72, 250.44) * mm, "end": v(-154.2, 253.04) * mm});
            skLineSegment(sketch, "E1179.280", {"start": v(-154.2, 253.04) * mm, "end": v(-154.08, 253.15) * mm});
            skLineSegment(sketch, "E1179.281", {"start": v(-154.08, 253.15) * mm, "end": v(-153.92, 253.3) * mm});
            skLineSegment(sketch, "E1179.282", {"start": v(-153.92, 253.3) * mm, "end": v(-150.96, 256.27) * mm});
            skLineSegment(sketch, "E1179.283", {"start": v(-150.96, 256.27) * mm, "end": v(-150.76, 256.46) * mm});
            skLineSegment(sketch, "E1179.284", {"start": v(-150.76, 256.46) * mm, "end": v(-147.88, 259.12) * mm});
            skLineSegment(sketch, "E1179.285", {"start": v(-147.88, 259.12) * mm, "end": v(-146.65, 260.36) * mm});
            skLineSegment(sketch, "E1179.286", {"start": v(-146.65, 260.36) * mm, "end": v(-144.8, 262.24) * mm});
            skLineSegment(sketch, "E1179.287", {"start": v(-144.8, 262.24) * mm, "end": v(-143.85, 263.18) * mm});
            skLineSegment(sketch, "E1179.288", {"start": v(-143.85, 263.18) * mm, "end": v(-141.27, 265.77) * mm});
            skLineSegment(sketch, "E1180", {"start": v(0.91, 297.38) * mm, "end": v(4.57, 277.72) * mm});
            skLineSegment(sketch, "E1181", {"start": v(-305.48, 2.7) * mm, "end": v(-325.36, 0.54) * mm});
            skSolve(sketch);
        }
        {
            var Q0;
            Q0=qCreatedBy(makeId("Top.planeOp"),FACE);
            cPlane(context, id + "F8", {"entities" : qUnion([Q0]), "cplaneType" : CPlaneType.OFFSET, "offset" : 177 * mm, "width" : 150 * mm, "height" : 150 * mm});
        }
        {
            var Q0;
            Q0=qCreatedBy(id+"F8.planeOp",FACE);
            var sketch = newSketch(context, id + "F9", { "sketchPlane" : qUnion([Q0])});
            skPoint(sketch, "E1182", {"position": v(0, 0) * mm});
            skLineSegment(sketch, "E1183", {"start": v(-201.4, 0) * mm, "end": v(-175.19, -162.86) * mm});
            skArc(sketch, "E1184", {"start": v(-175.19, -162.86) * mm, "mid": v(-141.87, -218.93) * mm, "end": v(-80.85, -241.95) * mm});
            skArc(sketch, "E1185", {"start": v(-80.85, -241.95) * mm, "mid": v(-40.44, -243.83) * mm, "end": v(0, -244.6) * mm});
            skArc(sketch, "E1186", {"start": v(0, -244.6) * mm, "mid": v(40.44, -243.83) * mm, "end": v(80.85, -241.95) * mm});
            skArc(sketch, "E1187", {"start": v(80.85, -241.95) * mm, "mid": v(141.87, -218.93) * mm, "end": v(175.19, -162.86) * mm});
            skLineSegment(sketch, "E1188", {"start": v(175.19, -162.86) * mm, "end": v(201.4, 0) * mm});
            skLineSegment(sketch, "E1189.0", {"start": v(150.59, -158.36) * mm, "end": v(176.73, 3.97) * mm});
            skArc(sketch, "E1189.1", {"start": v(79.83, -216.96) * mm, "mid": v(125.47, -200.05) * mm, "end": v(150.59, -158.36) * mm});
            skLineSegment(sketch, "E1189.2", {"start": v(-176.73, 3.97) * mm, "end": v(-150.59, -158.36) * mm});
            skArc(sketch, "E1189.3", {"start": v(-150.59, -158.36) * mm, "mid": v(-125.47, -200.05) * mm, "end": v(-79.83, -216.96) * mm});
            skArc(sketch, "E1189.4", {"start": v(-79.83, -216.96) * mm, "mid": v(-39.93, -218.84) * mm, "end": v(0, -219.6) * mm});
            skArc(sketch, "E1189.5", {"start": v(0, -219.6) * mm, "mid": v(39.93, -218.84) * mm, "end": v(79.83, -216.96) * mm});
            skLineSegment(sketch, "E1190.0", {"start": v(170.27, -161.96) * mm, "end": v(196.47, 0.8) * mm});
            skArc(sketch, "E1190.1", {"start": v(80.64, -236.95) * mm, "mid": v(138.59, -215.16) * mm, "end": v(170.27, -161.96) * mm});
            skLineSegment(sketch, "E1190.2", {"start": v(-196.47, 0.8) * mm, "end": v(-170.27, -161.96) * mm});
            skArc(sketch, "E1190.3", {"start": v(-170.27, -161.96) * mm, "mid": v(-138.59, -215.16) * mm, "end": v(-80.64, -236.95) * mm});
            skArc(sketch, "E1190.4", {"start": v(-80.64, -236.95) * mm, "mid": v(-40.34, -238.83) * mm, "end": v(0, -239.6) * mm});
            skArc(sketch, "E1190.5", {"start": v(0, -239.6) * mm, "mid": v(40.34, -238.83) * mm, "end": v(80.64, -236.95) * mm});
            skLineSegment(sketch, "E1191", {"start": v(-196.47, 0.8) * mm, "end": v(-176.73, 3.97) * mm});
            skLineSegment(sketch, "E1192", {"start": v(176.73, 3.97) * mm, "end": v(196.47, 0.8) * mm});
            skSolve(sketch);
        }
        {
            var Q0;
            Q0=qCreatedBy(makeId("Top.planeOp"),FACE);
            cPlane(context, id + "F10", {"entities" : qUnion([Q0]), "cplaneType" : CPlaneType.OFFSET, "offset" : 248 * mm, "width" : 150 * mm, "height" : 150 * mm});
        }
        {
            var Q0;
            Q0=qCreatedBy(id+"F10.planeOp",FACE);
            var sketch = newSketch(context, id + "F11", { "sketchPlane" : qUnion([Q0])});
            skPoint(sketch, "E1193", {"position": v(0, 0) * mm});
            skLineSegment(sketch, "E1194", {"start": v(-178.86, 0) * mm, "end": v(-178.86, -5.24) * mm});
            skLineSegment(sketch, "E1195", {"start": v(-178.86, -5.24) * mm, "end": v(-157.65, -113.23) * mm});
            skArc(sketch, "E1196", {"start": v(-157.65, -113.23) * mm, "mid": v(-145.4, -139.97) * mm, "end": v(-121.72, -157.43) * mm});
            skArc(sketch, "E1197", {"start": v(-121.72, -157.43) * mm, "mid": v(-96.94, -162.07) * mm, "end": v(-71.8, -164.02) * mm});
            skArc(sketch, "E1198", {"start": v(-71.8, -164.02) * mm, "mid": v(-35.92, -165.54) * mm, "end": v(0, -166.03) * mm});
            skArc(sketch, "E1199", {"start": v(0, -166.03) * mm, "mid": v(35.92, -165.54) * mm, "end": v(71.8, -164.02) * mm});
            skArc(sketch, "E1200", {"start": v(71.8, -164.02) * mm, "mid": v(96.94, -162.07) * mm, "end": v(121.72, -157.43) * mm});
            skArc(sketch, "E1201", {"start": v(121.72, -157.43) * mm, "mid": v(145.4, -139.97) * mm, "end": v(157.65, -113.23) * mm});
            skLineSegment(sketch, "E1202", {"start": v(157.65, -113.23) * mm, "end": v(178.86, -5.24) * mm});
            skLineSegment(sketch, "E1203", {"start": v(178.86, -5.24) * mm, "end": v(178.86, 0) * mm});
            skLineSegment(sketch, "E1204.0", {"start": v(153.86, -2.81) * mm, "end": v(153.86, 0) * mm});
            skLineSegment(sketch, "E1204.1", {"start": v(133.07, -108.65) * mm, "end": v(153.86, -2.81) * mm});
            skArc(sketch, "E1204.2", {"start": v(113.86, -133.6) * mm, "mid": v(126.55, -123.5) * mm, "end": v(133.07, -108.65) * mm});
            skArc(sketch, "E1204.3", {"start": v(70.8, -139.04) * mm, "mid": v(92.48, -137.43) * mm, "end": v(113.86, -133.6) * mm});
            skArc(sketch, "E1204.4", {"start": v(0, -141.03) * mm, "mid": v(35.42, -140.54) * mm, "end": v(70.8, -139.04) * mm});
            skArc(sketch, "E1204.5", {"start": v(-70.8, -139.04) * mm, "mid": v(-35.42, -140.54) * mm, "end": v(0, -141.03) * mm});
            skLineSegment(sketch, "E1204.6", {"start": v(-153.86, 0) * mm, "end": v(-153.86, -2.81) * mm});
            skLineSegment(sketch, "E1204.7", {"start": v(-153.86, -2.81) * mm, "end": v(-133.07, -108.65) * mm});
            skArc(sketch, "E1204.8", {"start": v(-133.07, -108.65) * mm, "mid": v(-126.55, -123.5) * mm, "end": v(-113.86, -133.6) * mm});
            skArc(sketch, "E1204.9", {"start": v(-113.86, -133.6) * mm, "mid": v(-92.48, -137.43) * mm, "end": v(-70.8, -139.04) * mm});
            skLineSegment(sketch, "E1205.0", {"start": v(173.86, -4.76) * mm, "end": v(173.86, 0) * mm});
            skLineSegment(sketch, "E1205.1", {"start": v(152.73, -112.3) * mm, "end": v(173.86, -4.76) * mm});
            skArc(sketch, "E1205.2", {"start": v(120.19, -152.66) * mm, "mid": v(141.64, -136.66) * mm, "end": v(152.73, -112.3) * mm});
            skArc(sketch, "E1205.3", {"start": v(71.6, -159.03) * mm, "mid": v(96.06, -157.14) * mm, "end": v(120.19, -152.66) * mm});
            skArc(sketch, "E1205.4", {"start": v(0, -161.03) * mm, "mid": v(35.82, -160.54) * mm, "end": v(71.6, -159.03) * mm});
            skArc(sketch, "E1205.5", {"start": v(-71.6, -159.03) * mm, "mid": v(-35.82, -160.54) * mm, "end": v(0, -161.03) * mm});
            skLineSegment(sketch, "E1205.6", {"start": v(-173.86, 0) * mm, "end": v(-173.86, -4.76) * mm});
            skLineSegment(sketch, "E1205.7", {"start": v(-173.86, -4.76) * mm, "end": v(-152.73, -112.3) * mm});
            skArc(sketch, "E1205.8", {"start": v(-152.73, -112.3) * mm, "mid": v(-141.64, -136.66) * mm, "end": v(-120.19, -152.66) * mm});
            skArc(sketch, "E1205.9", {"start": v(-120.19, -152.66) * mm, "mid": v(-96.06, -157.14) * mm, "end": v(-71.6, -159.03) * mm});
            skLineSegment(sketch, "E1206", {"start": v(-173.86, 0) * mm, "end": v(-153.86, 0) * mm});
            skLineSegment(sketch, "E1207", {"start": v(153.86, 0) * mm, "end": v(173.86, 0) * mm});
            skSolve(sketch);
        }
        {
            var Q0;
            Q0=qCreatedBy(makeId("Top.planeOp"),FACE);
            cPlane(context, id + "F12", {"entities" : qUnion([Q0]), "cplaneType" : CPlaneType.OFFSET, "offset" : 82 * mm, "width" : 150 * mm, "height" : 150 * mm});
        }
        {
            var Q0;
            Q0=qCreatedBy(id+"F12.planeOp",FACE);
            var sketch = newSketch(context, id + "F13", { "sketchPlane" : qUnion([Q0])});
            skPoint(sketch, "E1208", {"position": v(0, 0) * mm});
            skLineSegment(sketch, "E1209", {"start": v(-215, 0) * mm, "end": v(-177.3, -230.93) * mm});
            skArc(sketch, "E1210", {"start": v(-177.3, -230.93) * mm, "mid": v(-153.1, -283.35) * mm, "end": v(-107.6, -318.86) * mm});
            skArc(sketch, "E1211", {"start": v(-107.6, -318.86) * mm, "mid": v(-88.72, -323.1) * mm, "end": v(-69.52, -325.35) * mm});
            skArc(sketch, "E1212", {"start": v(-69.52, -325.35) * mm, "mid": v(-34.79, -327.68) * mm, "end": v(0, -329.02) * mm});
            skArc(sketch, "E1213", {"start": v(0, -329.02) * mm, "mid": v(34.79, -327.68) * mm, "end": v(69.52, -325.35) * mm});
            skArc(sketch, "E1214", {"start": v(69.52, -325.35) * mm, "mid": v(88.72, -323.1) * mm, "end": v(107.6, -318.86) * mm});
            skArc(sketch, "E1215", {"start": v(107.6, -318.86) * mm, "mid": v(153.1, -283.35) * mm, "end": v(177.3, -230.93) * mm});
            skLineSegment(sketch, "E1216", {"start": v(177.3, -230.93) * mm, "end": v(215, 0) * mm});
            skLineSegment(sketch, "E1217.0", {"start": v(152.7, -226.47) * mm, "end": v(190.32, 4.03) * mm});
            skArc(sketch, "E1217.1", {"start": v(98.98, -295.3) * mm, "mid": v(133.97, -267.24) * mm, "end": v(152.7, -226.47) * mm});
            skArc(sketch, "E1217.2", {"start": v(67.7, -300.41) * mm, "mid": v(83.47, -298.63) * mm, "end": v(98.98, -295.3) * mm});
            skArc(sketch, "E1217.3", {"start": v(0, -304.02) * mm, "mid": v(33.88, -302.7) * mm, "end": v(67.7, -300.41) * mm});
            skLineSegment(sketch, "E1217.4", {"start": v(-190.32, 4.03) * mm, "end": v(-152.7, -226.47) * mm});
            skArc(sketch, "E1217.5", {"start": v(-152.7, -226.47) * mm, "mid": v(-133.97, -267.24) * mm, "end": v(-98.98, -295.3) * mm});
            skArc(sketch, "E1217.6", {"start": v(-98.98, -295.3) * mm, "mid": v(-83.47, -298.63) * mm, "end": v(-67.7, -300.41) * mm});
            skArc(sketch, "E1217.7", {"start": v(-67.7, -300.41) * mm, "mid": v(-33.88, -302.7) * mm, "end": v(0, -304.02) * mm});
            skLineSegment(sketch, "E1218.0", {"start": v(172.38, -230.04) * mm, "end": v(210.06, 0.8) * mm});
            skArc(sketch, "E1218.1", {"start": v(105.87, -314.15) * mm, "mid": v(149.28, -280.12) * mm, "end": v(172.38, -230.04) * mm});
            skArc(sketch, "E1218.2", {"start": v(69.16, -320.36) * mm, "mid": v(87.68, -318.2) * mm, "end": v(105.87, -314.15) * mm});
            skArc(sketch, "E1218.3", {"start": v(0, -324.02) * mm, "mid": v(34.6, -322.69) * mm, "end": v(69.16, -320.36) * mm});
            skLineSegment(sketch, "E1218.4", {"start": v(-210.06, 0.8) * mm, "end": v(-172.38, -230.04) * mm});
            skArc(sketch, "E1218.5", {"start": v(-172.38, -230.04) * mm, "mid": v(-149.28, -280.12) * mm, "end": v(-105.87, -314.15) * mm});
            skArc(sketch, "E1218.6", {"start": v(-105.87, -314.15) * mm, "mid": v(-87.68, -318.2) * mm, "end": v(-69.16, -320.36) * mm});
            skArc(sketch, "E1218.7", {"start": v(-69.16, -320.36) * mm, "mid": v(-34.6, -322.69) * mm, "end": v(0, -324.02) * mm});
            skLineSegment(sketch, "E1219", {"start": v(-210.06, 0.8) * mm, "end": v(-190.32, 4.03) * mm});
            skLineSegment(sketch, "E1220", {"start": v(190.32, 4.03) * mm, "end": v(210.06, 0.8) * mm});
            skSolve(sketch);
        }
        {
            var Q0;
            Q0 = qSketchRegion(id + "F13", true);
            extrude(context, id + "F14", {"entities" : qUnion([Q0]), "endBound" : BoundingType.SYMMETRIC, "depth" : 2 * mm, "offsetDistance" : 25 * mm});
        }
        {
            var Q0;
            Q0 = qSketchRegion(id + "F11", true);
            extrude(context, id + "F15", {"entities" : qUnion([Q0]), "endBound" : BoundingType.SYMMETRIC, "depth" : 2 * mm, "offsetDistance" : 25 * mm});
        }
        {
            var Q0;
            Q0 = qSketchRegion(id + "F9", true);
            extrude(context, id + "F16", {"entities" : qUnion([Q0]), "endBound" : BoundingType.SYMMETRIC, "depth" : 2 * mm, "offsetDistance" : 25 * mm});
        }
        {
            var Q0;
            Q0 = qSketchRegion(id + "F1", true);
            extrude(context, id + "F17", {"entities" : qUnion([Q0]), "endBound" : BoundingType.SYMMETRIC, "depth" : 2 * mm, "offsetDistance" : 25 * mm});
        }
        {
            var Q0;
            Q0 = qSketchRegion(id + "F7", true);
            extrude(context, id + "F18", {"entities" : qUnion([Q0]), "operationType" : NewBodyOperationType.ADD, "endBound" : BoundingType.SYMMETRIC, "depth" : 2 * mm, "offsetDistance" : 25 * mm});
        }
        {
            var Q0;
            Q0 = qSketchRegion(id + "F3", true);
            extrude(context, id + "F19", {"entities" : qUnion([Q0]), "endBound" : BoundingType.SYMMETRIC, "depth" : 2 * mm, "offsetDistance" : 25 * mm});
        }
        {
            var Q0;
            Q0 = qSketchRegion(id + "F5", true);
            extrude(context, id + "F20", {"entities" : qUnion([Q0]), "endBound" : BoundingType.SYMMETRIC, "depth" : 2 * mm, "offsetDistance" : 25 * mm});
        }
        {
            var Q0;
            Q0=qCreatedBy(makeId("Top.planeOp"),FACE);
            var sketch = newSketch(context, id + "F21", { "sketchPlane" : qUnion([Q0])});
            skLineSegment(sketch, "E1221.bottom", {"start": v(-254.21, 0) * mm, "end": v(251.63, 0) * mm});
            skLineSegment(sketch, "E1221.top", {"start": v(-254.21, -357.24) * mm, "end": v(251.63, -357.24) * mm});
            skLineSegment(sketch, "E1221.left", {"start": v(-254.21, 0) * mm, "end": v(-254.21, -357.24) * mm});
            skLineSegment(sketch, "E1221.right", {"start": v(251.63, 0) * mm, "end": v(251.63, -357.24) * mm});
            skSolve(sketch);
        }
        {
            var Q0;
            Q0 = qSketchRegion(id + "F21", true);
            extrude(context, id + "F22", {"entities" : qUnion([Q0]), "oppositeDirection" : true, "depth" : 25 * mm, "offsetDistance" : 25 * mm});
        }
        {
            var Q0;
            Q0=makeQuery(id+"F22.opExtrude","SWEPT_FACE",FACE,{"disambiguationData":[OSD([sQuery(id+"F21.wireOp",EDGE,"E1221.bottom")])]});
            var sketch = newSketch(context, id + "F23", { "sketchPlane" : qUnion([Q0])});
            skLineSegment(sketch, "E1222.bottom", {"start": v(-251.63, 0) * mm, "end": v(254.21, 0) * mm});
            skLineSegment(sketch, "E1222.top", {"start": v(-251.63, 327.99) * mm, "end": v(254.21, 327.99) * mm});
            skLineSegment(sketch, "E1222.left", {"start": v(-251.63, 0) * mm, "end": v(-251.63, 327.99) * mm});
            skLineSegment(sketch, "E1222.right", {"start": v(254.21, 0) * mm, "end": v(254.21, 327.99) * mm});
            skSolve(sketch);
        }
        {
            var Q0;
            Q0=makeQuery(id+"F23.imprint","IMPRINT",FACE,{"disambiguationData":[TD([[makeQuery(id+"F23.imprint","IMPRINT",EDGE,{"derivedFrom":sQuery(id+"F23.wireOp",EDGE,"E1222.bottom")}),1.0]])]});
            var Q1;
            Q1=makeQuery(id+"F23.imprint","IMPRINT",FACE,{"disambiguationData":[TD([[makeQuery(id+"F23.imprint","IMPRINT",EDGE,{"derivedFrom":sQuery(id+"F23.wireOp",EDGE,"E1222.bottom")}),-1.0]])]});
            extrude(context, id + "F24", {"entities" : qUnion([Q0, Q1]), "operationType" : NewBodyOperationType.ADD, "depth" : 25 * mm, "offsetDistance" : 25 * mm});
        }
    });
